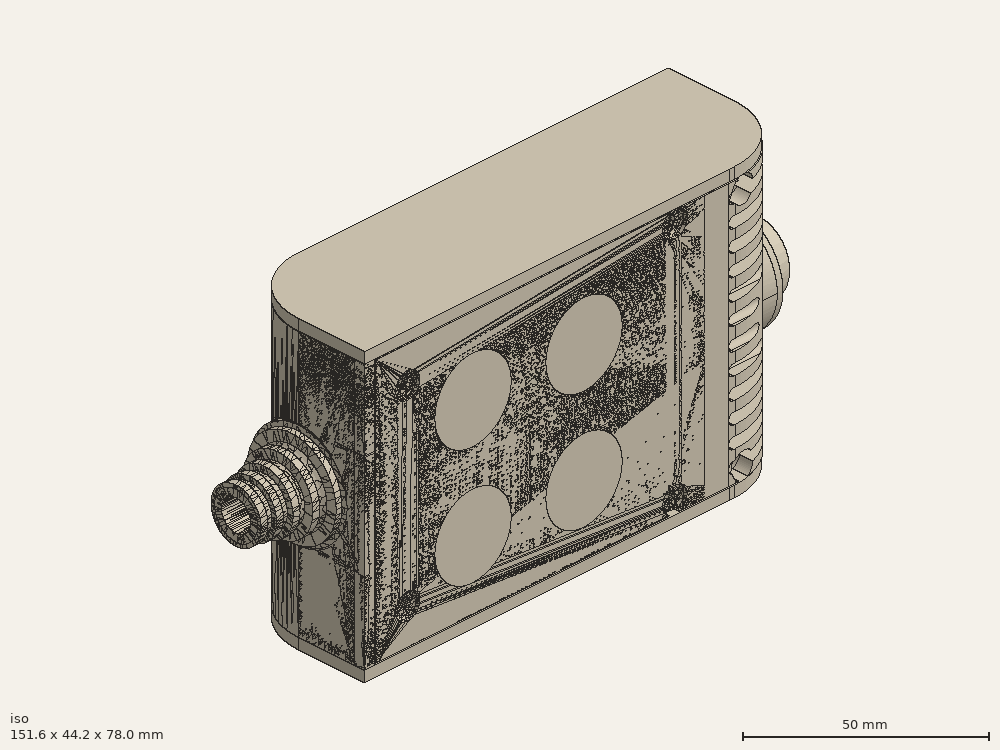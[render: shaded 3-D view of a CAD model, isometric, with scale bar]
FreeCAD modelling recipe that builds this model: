
FCSTD DOCUMENT  (FreeCAD 0.19R0.19.2)
Label: enclosure_179FCStd
License: All rights reserved
LicenseURL: http://en.wikipedia.org/wiki/All_rights_reserved
objects: Part::Revolution×152, Part::MultiFuse×146, Part::Feature×146, Sketcher::SketchObject×84, Part::Cut×70, Part::Cylinder×70, Part::Extrusion×67, Part::Fillet×58, Part::Box×36, App::MeasureDistance×4, PartDesign::Body×2, Image::ImagePlane×1
note: 831 computed .brp shape members not serialized (recipe doc carries the construction recipe); baked Part::Feature solids carry a one-line shape summary decoded from their .brp

FEATURE [Sketcher::SketchObject] Sketch  label="topSketch"
  FullyConstrained = true
  sketch-geometry (20):
    g0: LineSegment StartX=5.21097e-06 StartY=3 StartZ=0 EndX=5.21097e-06 EndY=19 EndZ=0
    g1: ArcOfCircle CenterX=19 CenterY=19 CenterZ=0 NormalX=0 NormalY=0 NormalZ=1 AngleXU=0 Radius=19 StartAngle=1.5708 EndAngle=3.14159
    g2: ArcOfCircle CenterX=19 CenterY=19 CenterZ=0 NormalX=0 NormalY=0 NormalZ=1 AngleXU=0 Radius=16 StartAngle=1.5708 EndAngle=3.14159
    g3: LineSegment StartX=114 StartY=35 StartZ=0 EndX=19 EndY=35 EndZ=0
    g4: LineSegment StartX=5.21097e-06 StartY=3 StartZ=0 EndX=5.21097e-06 EndY=0 EndZ=0
    g5: LineSegment StartX=3 StartY=0 StartZ=0 EndX=5.21097e-06 EndY=0 EndZ=0
    g6: LineSegment StartX=3 StartY=19 StartZ=0 EndX=3 EndY=0 EndZ=0
    g7: LineSegment StartX=19 StartY=38 StartZ=0 EndX=124 EndY=38 EndZ=0
    g8: Circle CenterX=119 CenterY=35 CenterZ=0 NormalX=0 NormalY=0 NormalZ=1 AngleXU=0 Radius=1
    g9: Circle CenterX=121 CenterY=35 CenterZ=0 NormalX=0 NormalY=0 NormalZ=1 AngleXU=0 Radius=1
    g10: Circle CenterX=121 CenterY=33 CenterZ=0 NormalX=0 NormalY=0 NormalZ=1 AngleXU=0 Radius=1
    g11: BSplineCurve PolesCount=3 KnotsCount=2 Degree=2 IsPeriodic=0
    g12: GeomPoint X=119 Y=35 Z=0
    g13: GeomPoint X=121 Y=33 Z=0
    g14: LineSegment StartX=119 StartY=35 StartZ=0 EndX=114 EndY=35 EndZ=0
    g15: ArcOfCircle CenterX=105 CenterY=19 CenterZ=0 NormalX=0 NormalY=0 NormalZ=1 AngleXU=0 Radius=19 StartAngle=5.7297 EndAngle=6.28319
    g16: ArcOfCircle CenterX=105 CenterY=19 CenterZ=0 NormalX=0 NormalY=0 NormalZ=1 AngleXU=0 Radius=16 StartAngle=5.60905 EndAngle=6.28319
    g17: LineSegment StartX=121 StartY=33 StartZ=0 EndX=121 EndY=19 EndZ=0
    g18: LineSegment StartX=124 StartY=38 StartZ=0 EndX=124 EndY=19 EndZ=0
    g19: LineSegment StartX=117.5 StartY=9.01251 StartZ=0 EndX=121.163 EndY=9.0125 EndZ=0
  constraints (46):
    c: Vertical(g0)
    c: Block(g0)
    c: Coincident(g1,g0)
    c: Block(g1)
    c: Coincident(g2,g1)
    c: Block(g2)
    c: Coincident(g3,g2)
    c: Horizontal(g3)
    c: Tangent(g3,g2)
    c: Coincident(g4,g0)
    c: Distance(g4) = 3
    c: Vertical(g4)
    c: Coincident(g5,g4)
    c: Horizontal(g5)
    c: Coincident(g6,g2)
    c: Coincident(g6,g5)
    c: Vertical(g6)
    c: Horizontal(g7)
    c: Distance(g7) = 105
    c: Coincident(g7,g1)
    c: Block(g3)
    c: Weight(g8) = 1
    c: Equal(g8,g9)
    c: Equal(g8,g10)
    c: InternalAlignment(g8,g11)
    c: InternalAlignment(g9,g11)
    c: InternalAlignment(g10,g11)
    c: InternalAlignment(g12,g11)
    c: InternalAlignment(g13,g11)
    c: Block(g11)
    c: Coincident(g14,g11)
    c: Coincident(g14,g3)
    c: Horizontal(g14)
    c: Block(g15)
    c: Coincident(g16,g15)
    c: Block(g16)
    c: Coincident(g17,g11)
    c: Coincident(g17,g16)
    c: Vertical(g17)
    c: Distance(g17) = 14
    c: Coincident(g18,g7)
    c: Coincident(g18,g15)
    c: Vertical(g18)
    c: Distance(g18) = 19
    c: Coincident(g19,g16)
    c: Coincident(g19,g15)
FEATURE [Sketcher::SketchObject] Sketch001  label="bottomSketch"
  FullyConstrained = true
  sketch-geometry (32):
    g0: LineSegment StartX=3.3 StartY=-6.03275e-07 StartZ=0 EndX=98 EndY=-6.03275e-07 EndZ=0
    g1: ArcOfCircle CenterX=98 CenterY=19 CenterZ=0 NormalX=0 NormalY=0 NormalZ=1 AngleXU=0 Radius=19 StartAngle=4.71239 EndAngle=5.71103
    g2: LineSegment StartX=6.3 StartY=8 StartZ=0 EndX=3.3 EndY=8 EndZ=0
    g3: LineSegment StartX=3.3 StartY=8 StartZ=0 EndX=3.3 EndY=-6.03275e-07 EndZ=0
    g4: ArcOfCircle CenterX=8.3 CenterY=5 CenterZ=0 NormalX=0 NormalY=0 NormalZ=1 AngleXU=0 Radius=2 StartAngle=3.14159 EndAngle=4.71239
    g5: LineSegment StartX=6.3 StartY=8 StartZ=0 EndX=6.3 EndY=5 EndZ=0
    g6: ArcOfCircle CenterX=98 CenterY=19 CenterZ=0 NormalX=0 NormalY=0 NormalZ=1 AngleXU=0 Radius=12.7 StartAngle=4.71239 EndAngle=6.28319
    g7: LineSegment StartX=94.7 StartY=3 StartZ=0 EndX=8.3 EndY=3 EndZ=0
    g8-g12: Circle x5 (B-spline internal-alignment scaffolding for g13; pole/knot coordinates omitted)
    g13: BSplineCurve PolesCount=5 KnotsCount=3 Degree=3 IsPeriodic=0
    g14: GeomPoint X=98 Y=6.3 Z=0
    g15: GeomPoint X=96.3938 Y=4.71946 Z=0
    g16: GeomPoint X=94.7 Y=3 Z=0
    g17-g23: Circle x7 (B-spline internal-alignment scaffolding for g24; pole/knot coordinates omitted)
    g24: BSplineCurve PolesCount=7 KnotsCount=5 Degree=3 IsPeriodic=0
    g25-g29: GeomPoint x5 (B-spline internal-alignment scaffolding for g24; pole/knot coordinates omitted)
    g30: ArcOfCircle CenterX=98 CenterY=19 CenterZ=0 NormalX=0 NormalY=0 NormalZ=1 AngleXU=0 Radius=15.7 StartAngle=5.81226 EndAngle=6.28319
    g31: LineSegment StartX=110.7 StartY=19 StartZ=0 EndX=113.7 EndY=19 EndZ=0
  constraints (41):
    c: Horizontal(g0)
    c: Coincident(g1,g0)
    c: Block(g1)
    c: Horizontal(g2)
    c: Distance(g2) = 3
    c: Coincident(g3,g2)
    c: Vertical(g3)
    c: Coincident(g3,g0)
    c: Block(g4)
    c: Block(g2)
    c: Coincident(g5,g2)
    c: Coincident(g5,g4)
    c: Vertical(g5)
    c: Coincident(g6,g1)
    c: Block(g6)
    c: Coincident(g7,g4)
    c: Horizontal(g7)
    c: Block(g0)
    c: Block(g7)
    c: Block(g3)
    c: Coincident(g13,g6)
    c: Weight(g8) = 1
    c: Equal(g8, g9-g12) x4
    c: Coincident(g13,g7)
    c: InternalAlignment(g8-g12 -> g13) x5
    c: InternalAlignment(g14,g13)
    c: InternalAlignment(g15,g13)
    c: InternalAlignment(g16,g13)
    c: Block(g13)
    c: Weight(g17) = 1
    c: Equal(g17, g18-g23) x6
    c: Coincident(g24,g1)
    c: InternalAlignment(g17-g23 -> g24) x7
    c: InternalAlignment(g25-g29 -> g24) x5
    c: Block(g24)
    c: Coincident(g30,g24)
    c: Coincident(g31,g6)
    c: Coincident(g31,g30)
    c: Horizontal(g31)
    c: Block(g31)
    c: Block(g30)
FEATURE [Part::Extrusion] Extrude  label="top"
  Base = -> Sketch
  Dir = (0,0,1)
  DirMode = 2
  FaceMakerClass = Part::FaceMakerBullseye
  LengthFwd = 72
  LengthRev = 0
  Solid = true
  Symmetric = false
FEATURE [Part::Extrusion] Extrude001  label="bottom"
  Base = -> Sketch001
  Dir = (0,0,1)
  DirMode = 2
  FaceMakerClass = Part::FaceMakerBullseye
  LengthFwd = 71.4
  LengthRev = 0
  Placement = pos=(0,0,0.3) rot=(0,0,1;0rad)
  Solid = true
  Symmetric = false
FEATURE [Sketcher::SketchObject] Sketch002  label="topSketch001"
  FullyConstrained = true
  sketch-geometry (8):
    g0: ArcOfCircle CenterX=19 CenterY=19.0975 CenterZ=0 NormalX=0 NormalY=0 NormalZ=1 AngleXU=0 Radius=18.9025 StartAngle=1.5708 EndAngle=3.14674
    g1: LineSegment StartX=0.0977805 StartY=19.0003 StartZ=0 EndX=0.0977805 EndY=0.000251602 EndZ=0
    g2: LineSegment StartX=19 StartY=38 StartZ=0 EndX=124 EndY=38 EndZ=0
    g3: LineSegment StartX=0.0977805 StartY=0.000251602 StartZ=0 EndX=105.098 EndY=0.000251602 EndZ=0
    g4: LineSegment StartX=124 StartY=38 StartZ=0 EndX=125.616 EndY=38 EndZ=0
    g5: LineSegment StartX=105.098 StartY=0.000251602 StartZ=0 EndX=106.713 EndY=0.000251602 EndZ=0
    g6: ArcOfCircle CenterX=106.616 CenterY=19 CenterZ=0 NormalX=0 NormalY=0 NormalZ=1 AngleXU=0 Radius=19 StartAngle=4.71754 EndAngle=6.28319
    g7: LineSegment StartX=125.616 StartY=38 StartZ=0 EndX=125.616 EndY=19 EndZ=0
  constraints (21):
    c: Block(g0)
    c: Coincident(g1,g0)
    c: Vertical(g1)
    c: Horizontal(g2)
    c: Distance(g2) = 105
    c: Coincident(g2,g0)
    c: Distance(g1) = 19
    c: Coincident(g3,g1)
    c: Horizontal(g3)
    c: Distance(g3) = 105
    c: Coincident(g4,g2)
    c: Horizontal(g4)
    c: Distance(g4) = 1.61553
    c: Horizontal(g5)
    c: Equal(g4,g5) = 1.61553
    c: Coincident(g5,g3)
    c: Block(g6)
    c: Coincident(g6,g5)
    c: Coincident(g7,g4)
    c: Coincident(g7,g6)
    c: Vertical(g7)
FEATURE [Part::Extrusion] Extrude002  label="sideA"
  Base = -> Sketch002
  Dir = (0,0,1)
  DirMode = 2
  FaceMakerClass = Part::FaceMakerBullseye
  LengthFwd = 3
  LengthRev = 0
  Placement = pos=(0,0,-3) rot=(0,0,1;0rad)
  Solid = true
  Symmetric = false
FEATURE [Sketcher::SketchObject] Sketch003  label="topSketch002"
  FullyConstrained = true
  sketch-geometry (6):
    g0: LineSegment StartX=19 StartY=38 StartZ=0 EndX=117 EndY=38 EndZ=0
    g1: ArcOfCircle CenterX=19 CenterY=19 CenterZ=0 NormalX=0 NormalY=0 NormalZ=1 AngleXU=0 Radius=19 StartAngle=1.5708 EndAngle=3.14159
    g2: LineSegment StartX=117 StartY=38 StartZ=0 EndX=117 EndY=19 EndZ=0
    g3: LineSegment StartX=98 StartY=1.0161e-12 StartZ=0 EndX=5.22862e-06 EndY=1.0161e-12 EndZ=0
    g4: LineSegment StartX=5.22862e-06 StartY=19 StartZ=0 EndX=5.22862e-06 EndY=1.0161e-12 EndZ=0
    g5: ArcOfCircle CenterX=98 CenterY=19 CenterZ=0 NormalX=0 NormalY=0 NormalZ=1 AngleXU=0 Radius=19 StartAngle=4.71239 EndAngle=6.28319
  constraints (16):
    c: Horizontal(g0)
    c: Distance(g0) = 98
    c: Coincident(g1,g0)
    c: Block(g1)
    c: Coincident(g2,g0)
    c: Vertical(g2)
    c: Distance(g2) = 19
    c: Horizontal(g3)
    c: Coincident(g4,g1)
    c: Vertical(g4)
    c: Coincident(g3,g4)
    c: Block(g3)
    c: Coincident(g5,g2)
    c: Coincident(g5,g3)
    c: Block(g0)
    c: Block(g5)
FEATURE [Sketcher::SketchObject] Sketch004
  FullyConstrained = true
  MapMode = 3
  Placement = pos=(0,0,0) rot=(1,0,0;1.5708rad)
  Support = -> [Extrude]
  sketch-geometry (8):
    g0: Circle CenterX=80.351 CenterY=-67.6202 CenterZ=0 NormalX=0 NormalY=0 NormalZ=1 AngleXU=0 Radius=2
    g1: Circle CenterX=80.351 CenterY=-67.6202 CenterZ=0 NormalX=0 NormalY=0 NormalZ=1 AngleXU=0 Radius=3
    g2: Circle CenterX=80.351 CenterY=-4.92017 CenterZ=0 NormalX=0 NormalY=0 NormalZ=1 AngleXU=0 Radius=2
    g3: Circle CenterX=80.351 CenterY=-4.92017 CenterZ=0 NormalX=0 NormalY=0 NormalZ=1 AngleXU=0 Radius=3
    g4: Circle CenterX=23.851 CenterY=-4.92017 CenterZ=0 NormalX=0 NormalY=0 NormalZ=1 AngleXU=0 Radius=2
    g5: Circle CenterX=23.851 CenterY=-4.92017 CenterZ=0 NormalX=0 NormalY=0 NormalZ=1 AngleXU=0 Radius=3
    g6: Circle CenterX=23.851 CenterY=-67.6202 CenterZ=0 NormalX=0 NormalY=0 NormalZ=1 AngleXU=0 Radius=2
    g7: Circle CenterX=23.851 CenterY=-67.6202 CenterZ=0 NormalX=0 NormalY=0 NormalZ=1 AngleXU=0 Radius=3
  constraints (8):
    c: Block(g3)
    c: Block(g2)
    c: Block(g1)
    c: Block(g0)
    c: Block(g6)
    c: Block(g7)
    c: Block(g4)
    c: Block(g5)
FEATURE [Part::Extrusion] Extrude004
  Base = -> Sketch004
  Dir = (0,-1,2e-16)
  DirMode = 2
  FaceMakerClass = Part::FaceMakerBullseye
  LengthFwd = 6
  LengthRev = 0
  Placement = pos=(0,9,0) rot=(0,0,1;0rad)
  Solid = true
  Symmetric = false
FEATURE [Sketcher::SketchObject] Sketch005
  FullyConstrained = true
  MapMode = 3
  Placement = pos=(0,0,0) rot=(1,0,0;1.5708rad)
  Support = -> [Extrude]
  sketch-geometry (8):
    g0: Circle CenterX=80.351 CenterY=-67.6202 CenterZ=0 NormalX=0 NormalY=0 NormalZ=1 AngleXU=0 Radius=3
    g1: Circle CenterX=80.351 CenterY=-4.92017 CenterZ=0 NormalX=0 NormalY=0 NormalZ=1 AngleXU=0 Radius=3
    g2: Circle CenterX=23.851 CenterY=-4.92017 CenterZ=0 NormalX=0 NormalY=0 NormalZ=1 AngleXU=0 Radius=3
    g3: Circle CenterX=23.851 CenterY=-67.6202 CenterZ=0 NormalX=0 NormalY=0 NormalZ=1 AngleXU=0 Radius=3
    g4: Circle CenterX=23.851 CenterY=-67.6202 CenterZ=0 NormalX=0 NormalY=0 NormalZ=1 AngleXU=0 Radius=5
    g5: Circle CenterX=80.351 CenterY=-67.6202 CenterZ=0 NormalX=0 NormalY=0 NormalZ=1 AngleXU=0 Radius=5
    g6: Circle CenterX=23.851 CenterY=-4.92017 CenterZ=0 NormalX=0 NormalY=0 NormalZ=1 AngleXU=0 Radius=5
    g7: Circle CenterX=80.351 CenterY=-4.92017 CenterZ=0 NormalX=0 NormalY=0 NormalZ=1 AngleXU=0 Radius=5
  constraints (8):
    c: Block(g1)
    c: Block(g0)
    c: Block(g3)
    c: Block(g2)
    c: Block(g5)
    c: Block(g4)
    c: Block(g6)
    c: Block(g7)
FEATURE [Part::Extrusion] Extrude005
  Base = -> Sketch005
  Dir = (0,-1,2e-16)
  DirMode = 2
  FaceMakerClass = Part::FaceMakerBullseye
  LengthFwd = 2
  LengthRev = 0
  Solid = true
  Symmetric = false
FEATURE [Sketcher::SketchObject] Sketch006
  FullyConstrained = true
  MapMode = 3
  Placement = pos=(0,0,0) rot=(1,0,0;1.5708rad)
  sketch-geometry (8):
    g0: Circle CenterX=80.351 CenterY=-67.6202 CenterZ=0 NormalX=0 NormalY=0 NormalZ=1 AngleXU=0 Radius=3
    g1: Circle CenterX=80.351 CenterY=-4.92017 CenterZ=0 NormalX=0 NormalY=0 NormalZ=1 AngleXU=0 Radius=3
    g2: Circle CenterX=23.851 CenterY=-4.92017 CenterZ=0 NormalX=0 NormalY=0 NormalZ=1 AngleXU=0 Radius=3
    g3: Circle CenterX=23.851 CenterY=-67.6202 CenterZ=0 NormalX=0 NormalY=0 NormalZ=1 AngleXU=0 Radius=3
    g4: Circle CenterX=23.851 CenterY=-67.6202 CenterZ=0 NormalX=0 NormalY=0 NormalZ=1 AngleXU=0 Radius=5
    g5: Circle CenterX=80.351 CenterY=-67.6202 CenterZ=0 NormalX=0 NormalY=0 NormalZ=1 AngleXU=0 Radius=5
    g6: Circle CenterX=23.851 CenterY=-4.92017 CenterZ=0 NormalX=0 NormalY=0 NormalZ=1 AngleXU=0 Radius=5
    g7: Circle CenterX=80.351 CenterY=-4.92017 CenterZ=0 NormalX=0 NormalY=0 NormalZ=1 AngleXU=0 Radius=5
  constraints (8):
    c: Block(g1)
    c: Block(g0)
    c: Block(g3)
    c: Block(g2)
    c: Block(g5)
    c: Block(g4)
    c: Block(g6)
    c: Block(g7)
FEATURE [Part::Extrusion] Extrude007
  Base = -> Sketch006
  Dir = (0,-1,2e-16)
  DirMode = 2
  FaceMakerClass = Part::FaceMakerBullseye
  LengthFwd = 2
  LengthRev = 0
  Solid = true
  Symmetric = false
FEATURE [Part::Fillet] Fillet
  Base = -> Extrude007
  Edges = 4 edges r=1.99: [Edge6,Edge12,Edge18,Edge24]
FEATURE [Part::Cut] Cut
  Base = -> Extrude005
  Placement = pos=(0,5,0) rot=(0,0,1;0rad)
  Tool = -> Fillet
FEATURE [Part::MultiFuse] Fusion  label="pCBScrews"
  Placement = pos=(-2.5,0,72.3) rot=(0,0,1;0rad)
  Shapes = -> [Extrude004,Cut]
FEATURE [App::MeasureDistance] Distance  label="Distance: 0.69 mm"
  Distance = 0.685967
  P1 = (24.0138,2.9647,0.3)
  P2 = (23.8901,3,-0.373787)
FEATURE [App::MeasureDistance] Distance001  label="Distance: 0.53 mm"
  Distance = 0.533607
  P1 = (80.2939,3,72.2334)
  P2 = (80.281,2.99661,71.7)
FEATURE [Part::Fillet] Fillet001
  Base = -> Extrude001
  Edges = 1 edges r=2.4: [Edge17]
FEATURE [Part::Fillet] Fillet002  label="bottom001"
  Base = -> Fillet001
  Edges = 1 edges r=2.4: [Edge36]
FEATURE [Part::Fillet] Fillet003  label="top001"
  Base = -> Extrude
  Edges = 1 edges r=2: [Edge1]
FEATURE [Sketcher::SketchObject] Sketch007
  FullyConstrained = true
  sketch-geometry (16):
    g0: LineSegment StartX=4 StartY=0 StartZ=0 EndX=4 EndY=2.4 EndZ=0
    g1: LineSegment StartX=4 StartY=2.4 StartZ=0 EndX=7 EndY=2.4 EndZ=0
    g2: LineSegment StartX=4 StartY=0 StartZ=0 EndX=5.7 EndY=0 EndZ=0
    g3: LineSegment StartX=5.7 StartY=0 StartZ=0 EndX=5.7 EndY=-5.6 EndZ=0
    g4-g8: Circle x5 (B-spline internal-alignment scaffolding for g9; pole/knot coordinates omitted)
    g9: BSplineCurve PolesCount=5 KnotsCount=3 Degree=3 IsPeriodic=0
    g10: GeomPoint X=7 Y=2.4 Z=0
    g11: GeomPoint X=10.4582 Y=-1.55472 Z=0
    g12: GeomPoint X=14 Y=-5.6 Z=0
    g13: LineSegment StartX=14 StartY=-5.6 StartZ=0 EndX=14 EndY=-14.1 EndZ=0
    g14: LineSegment StartX=14 StartY=-14.1 StartZ=0 EndX=6.5 EndY=-14.1 EndZ=0
    g15: LineSegment StartX=5.7 StartY=-5.6 StartZ=0 EndX=6.5 EndY=-14.1 EndZ=0
  constraints (28):
    c: Distance(g0) = 2.4
    c: Vertical(g0)
    c: Block(g0)
    c: Coincident(g1,g0)
    c: Horizontal(g1)
    c: Distance(g1) = 3
    c: Coincident(g2,g0)
    c: Horizontal(g2)
    c: Distance(g2) = 1.7
    c: Coincident(g3,g2)
    c: Vertical(g3)
    c: Distance(g3) = 5.6
    c: Coincident(g9,g1)
    c: Weight(g4) = 1
    c: Equal(g4, g5-g8) x4
    c: InternalAlignment(g4-g8 -> g9) x5
    c: InternalAlignment(g10,g9)
    c: InternalAlignment(g11,g9)
    c: InternalAlignment(g12,g9)
    c: Block(g9)
    c: Coincident(g13,g9)
    c: Vertical(g13)
    c: Distance(g13) = 8.5
    c: Coincident(g14,g13)
    c: Horizontal(g14)
    c: Distance(g14) = 7.5
    c: Coincident(g15,g3)
    c: Coincident(g15,g14)
FEATURE [Part::Feature] Face
  shape: bbox 10 x 16.5 x 2e-07 mm, 1 faces, 0 solids (baked)
FEATURE [Part::Revolution] Revolve  label="plugHousing"
  Angle = 360
  Axis = (0,1,0)
  Base = (0,0,0)
  FaceMakerClass = Part::FaceMakerBullseye
  Placement = pos=(0,0,36.15) rot=(0,0,1;0rad)
  Solid = false
  Source = -> Face
  Symmetric = false
FEATURE [Part::Feature] Face001
  shape: bbox 10 x 16.5 x 2e-07 mm, 1 faces, 0 solids (baked)
FEATURE [Part::Revolution] Revolve001  label="plugHousing001"
  Angle = 360
  Axis = (0,1,0)
  Base = (0,0,0)
  FaceMakerClass = Part::FaceMakerBullseye
  Placement = pos=(0,0,36.15) rot=(0,0,1;0rad)
  Solid = false
  Source = -> Face001
  Symmetric = false
FEATURE [Part::MultiFuse] Fusion001  label="plugHousing002"
  Placement = pos=(0,0,0) rot=(0,0,1;1.5708rad)
  Shapes = -> [Revolve001,Revolve]
FEATURE [Part::Feature] Face002
  shape: bbox 10 x 16.5 x 2e-07 mm, 1 faces, 0 solids (baked)
FEATURE [Part::Revolution] Revolve003  label="plugHousing005"
  Angle = 360
  Axis = (0,1,0)
  Base = (0,0,0)
  FaceMakerClass = Part::FaceMakerBullseye
  Placement = pos=(0,0,36.15) rot=(0,0,1;0rad)
  Solid = false
  Source = -> Face002
  Symmetric = false
FEATURE [Part::Feature] Face003
  shape: bbox 10 x 16.5 x 2e-07 mm, 1 faces, 0 solids (baked)
FEATURE [Part::Revolution] Revolve002  label="plugHousing003"
  Angle = 360
  Axis = (0,1,0)
  Base = (0,0,0)
  FaceMakerClass = Part::FaceMakerBullseye
  Placement = pos=(0,0,36.15) rot=(0,0,1;0rad)
  Solid = false
  Source = -> Face003
  Symmetric = false
FEATURE [Part::MultiFuse] Fusion002  label="plugHousing004"
  Placement = pos=(0,0,0) rot=(0,0,1;1.5708rad)
  Shapes = -> [Revolve002,Revolve003]
FEATURE [Part::MultiFuse] Fusion003  label="plugHousing006"
  Placement = pos=(0,19,0) rot=(0,0,1;3.14159rad)
  Shapes = -> [Fusion002,Fusion001]
FEATURE [Part::Feature] Face004
  shape: bbox 10 x 16.5 x 2e-07 mm, 1 faces, 0 solids (baked)
FEATURE [Part::Revolution] Revolve006  label="plugHousing010"
  Angle = 360
  Axis = (0,1,0)
  Base = (0,0,0)
  FaceMakerClass = Part::FaceMakerBullseye
  Placement = pos=(0,0,36.15) rot=(0,0,1;0rad)
  Solid = false
  Source = -> Face004
  Symmetric = false
FEATURE [Part::Feature] Face005
  shape: bbox 10 x 16.5 x 2e-07 mm, 1 faces, 0 solids (baked)
FEATURE [Part::Revolution] Revolve007  label="plugHousing011"
  Angle = 360
  Axis = (0,1,0)
  Base = (0,0,0)
  FaceMakerClass = Part::FaceMakerBullseye
  Placement = pos=(0,0,36.15) rot=(0,0,1;0rad)
  Solid = false
  Source = -> Face005
  Symmetric = false
FEATURE [Part::Feature] Face006
  shape: bbox 10 x 16.5 x 2e-07 mm, 1 faces, 0 solids (baked)
FEATURE [Part::Revolution] Revolve004  label="plugHousing007"
  Angle = 360
  Axis = (0,1,0)
  Base = (0,0,0)
  FaceMakerClass = Part::FaceMakerBullseye
  Placement = pos=(0,0,36.15) rot=(0,0,1;0rad)
  Solid = false
  Source = -> Face006
  Symmetric = false
FEATURE [Part::MultiFuse] Fusion004  label="plugHousing009"
  Placement = pos=(0,0,0) rot=(0,0,1;1.5708rad)
  Shapes = -> [Revolve004,Revolve007]
FEATURE [Part::Feature] Face007
  shape: bbox 10 x 16.5 x 2e-07 mm, 1 faces, 0 solids (baked)
FEATURE [Part::Revolution] Revolve005  label="plugHousing008"
  Angle = 360
  Axis = (0,1,0)
  Base = (0,0,0)
  FaceMakerClass = Part::FaceMakerBullseye
  Placement = pos=(0,0,36.15) rot=(0,0,1;0rad)
  Solid = false
  Source = -> Face007
  Symmetric = false
FEATURE [Part::MultiFuse] Fusion005  label="plugHousing012"
  Placement = pos=(0,0,0) rot=(0,0,1;1.5708rad)
  Shapes = -> [Revolve006,Revolve005]
FEATURE [Part::MultiFuse] Fusion006  label="plugHousing013"
  Placement = pos=(0,19,0) rot=(0,0,1;3.14159rad)
  Shapes = -> [Fusion005,Fusion004]
FEATURE [Part::MultiFuse] Fusion007  label="plugHousing014"
  Placement = pos=(122.621,0,-0.15) rot=(0,0,1;0rad)
  Shapes = -> [Fusion003,Fusion006]
FEATURE [Part::Cylinder] Cylinder002
  Angle = 360
  AttacherType = Attacher::AttachEngine3D
  Height = 20
  Placement = pos=(0,0,36.15) rot=(0,0,1;0rad)
  Radius = 4
FEATURE [Part::Cylinder] Cylinder003
  Angle = 360
  AttacherType = Attacher::AttachEngine3D
  Height = 10
  Placement = pos=(0,0,36.15) rot=(0,0,1;0rad)
  Radius = 4
FEATURE [Part::MultiFuse] Fusion009  label="removeToCreateHoleForPlugHousing"
  Placement = pos=(70,19,36.15) rot=(0,1,0;1.5708rad)
  Shapes = -> [Cylinder002,Cylinder003]
FEATURE [Part::Cylinder] Cylinder004
  Angle = 360
  AttacherType = Attacher::AttachEngine3D
  Height = 20
  Placement = pos=(0,0,36.15) rot=(0,0,1;0rad)
  Radius = 4
FEATURE [Part::Cylinder] Cylinder005
  Angle = 360
  AttacherType = Attacher::AttachEngine3D
  Height = 10
  Placement = pos=(0,0,36.15) rot=(0,0,1;0rad)
  Radius = 4
FEATURE [Part::MultiFuse] Fusion010  label="removeToCreateHoleForPlugHousing001"
  Placement = pos=(70,19,36.15) rot=(0,1,0;1.5708rad)
  Shapes = -> [Cylinder004,Cylinder005]
FEATURE [Part::Cut] Cut001
  Base = -> Fillet003
  Tool = -> Fusion010
FEATURE [Part::Cut] Cut002  label="Bottom"
  Base = -> Fillet002
  Tool = -> Fusion009
FEATURE [Part::Feature] Face008
  shape: bbox 10 x 16.5 x 2e-07 mm, 1 faces, 0 solids (baked)
FEATURE [Part::Revolution] Revolve011  label="plugHousing021"
  Angle = 360
  Axis = (0,1,0)
  Base = (0,0,0)
  FaceMakerClass = Part::FaceMakerBullseye
  Placement = pos=(0,0,36.15) rot=(0,0,1;0rad)
  Solid = false
  Source = -> Face008
  Symmetric = false
FEATURE [Part::Feature] Face009
  shape: bbox 10 x 16.5 x 2e-07 mm, 1 faces, 0 solids (baked)
FEATURE [Part::Revolution] Revolve012  label="plugHousing022"
  Angle = 360
  Axis = (0,1,0)
  Base = (0,0,0)
  FaceMakerClass = Part::FaceMakerBullseye
  Placement = pos=(0,0,36.15) rot=(0,0,1;0rad)
  Solid = false
  Source = -> Face009
  Symmetric = false
FEATURE [Part::Feature] Face010 .. Face013  x4 (patterned run collapsed; names and placements below)
  shape: bbox 10 x 16.5 x 2e-07 mm, 1 faces, 0 solids (baked)
FEATURE [Part::Revolution] Revolve015  label="plugHousing027"
  Angle = 360
  Axis = (0,1,0)
  Base = (0,0,0)
  FaceMakerClass = Part::FaceMakerBullseye
  Placement = pos=(0,0,36.15) rot=(0,0,1;0rad)
  Solid = false
  Source = -> Face013
  Symmetric = false
FEATURE [Part::Feature] Face014
  shape: bbox 10 x 16.5 x 2e-07 mm, 1 faces, 0 solids (baked)
FEATURE [Part::Feature] Face015
  shape: bbox 10 x 16.5 x 2e-07 mm, 1 faces, 0 solids (baked)
FEATURE [Part::Feature] Face016
  shape: bbox 10 x 16.5 x 2e-07 mm, 1 faces, 0 solids (baked)
FEATURE [Part::Revolution] Revolve019  label="plugHousing033"
  Angle = 360
  Axis = (0,1,0)
  Base = (0,0,0)
  FaceMakerClass = Part::FaceMakerBullseye
  Placement = pos=(0,0,36.15) rot=(0,0,1;0rad)
  Solid = false
  Source = -> Face016
  Symmetric = false
FEATURE [Part::Feature] Face017
  shape: bbox 10 x 16.5 x 2e-07 mm, 1 faces, 0 solids (baked)
FEATURE [Part::Revolution] Revolve020  label="plugHousing034"
  Angle = 360
  Axis = (0,1,0)
  Base = (0,0,0)
  FaceMakerClass = Part::FaceMakerBullseye
  Placement = pos=(0,0,36.15) rot=(0,0,1;0rad)
  Solid = false
  Source = -> Face017
  Symmetric = false
FEATURE [Part::Feature] Face018
  shape: bbox 10 x 16.5 x 2e-07 mm, 1 faces, 0 solids (baked)
FEATURE [Part::Revolution] Revolve016  label="plugHousing030"
  Angle = 360
  Axis = (0,1,0)
  Base = (0,0,0)
  FaceMakerClass = Part::FaceMakerBullseye
  Placement = pos=(0,0,36.15) rot=(0,0,1;0rad)
  Solid = false
  Source = -> Face018
  Symmetric = false
FEATURE [Part::MultiFuse] Fusion020  label="plugHousing038"
  Placement = pos=(0,0,0) rot=(0,0,1;1.5708rad)
  Shapes = -> [Revolve016,Revolve020]
FEATURE [Part::Feature] Face019
  shape: bbox 10 x 16.5 x 2e-07 mm, 1 faces, 0 solids (baked)
FEATURE [Part::Feature] Face020
  shape: bbox 10 x 16.5 x 2e-07 mm, 1 faces, 0 solids (baked)
FEATURE [Part::Revolution] Revolve017  label="plugHousing031"
  Angle = 360
  Axis = (0,1,0)
  Base = (0,0,0)
  FaceMakerClass = Part::FaceMakerBullseye
  Placement = pos=(0,0,36.15) rot=(0,0,1;0rad)
  Solid = false
  Source = -> Face020
  Symmetric = false
FEATURE [Part::MultiFuse] Fusion021  label="plugHousing039"
  Placement = pos=(0,0,0) rot=(0,0,1;1.5708rad)
  Shapes = -> [Revolve019,Revolve017]
FEATURE [Part::MultiFuse] Fusion023  label="plugHousing041"
  Placement = pos=(0,19,0) rot=(0,0,1;3.14159rad)
  Shapes = -> [Fusion021,Fusion020]
FEATURE [Part::Revolution] Revolve022  label="plugHousing043"
  Angle = 360
  Axis = (0,1,0)
  Base = (0,0,0)
  FaceMakerClass = Part::FaceMakerBullseye
  Placement = pos=(0,0,36.15) rot=(0,0,1;0rad)
  Solid = false
  Source = -> Face019
  Symmetric = false
FEATURE [Part::Feature] Face021
  shape: bbox 10 x 16.5 x 2e-07 mm, 1 faces, 0 solids (baked)
FEATURE [Part::Revolution] Revolve023  label="plugHousing044"
  Angle = 360
  Axis = (0,1,0)
  Base = (0,0,0)
  FaceMakerClass = Part::FaceMakerBullseye
  Placement = pos=(0,0,36.15) rot=(0,0,1;0rad)
  Solid = false
  Source = -> Face021
  Symmetric = false
FEATURE [Part::Feature] Face022
  shape: bbox 10 x 16.5 x 2e-07 mm, 1 faces, 0 solids (baked)
FEATURE [Part::Revolution] Revolve018  label="plugHousing032"
  Angle = 360
  Axis = (0,1,0)
  Base = (0,0,0)
  FaceMakerClass = Part::FaceMakerBullseye
  Placement = pos=(0,0,36.15) rot=(0,0,1;0rad)
  Solid = false
  Source = -> Face022
  Symmetric = false
FEATURE [Part::MultiFuse] Fusion022  label="plugHousing040"
  Placement = pos=(0,0,0) rot=(0,0,1;1.5708rad)
  Shapes = -> [Revolve018,Revolve023]
FEATURE [Part::Feature] Face023
  shape: bbox 10 x 16.5 x 2e-07 mm, 1 faces, 0 solids (baked)
FEATURE [Part::Revolution] Revolve021  label="plugHousing035"
  Angle = 360
  Axis = (0,1,0)
  Base = (0,0,0)
  FaceMakerClass = Part::FaceMakerBullseye
  Placement = pos=(0,0,36.15) rot=(0,0,1;0rad)
  Solid = false
  Source = -> Face023
  Symmetric = false
FEATURE [Part::MultiFuse] Fusion018  label="plugHousing036"
  Placement = pos=(0,0,0) rot=(0,0,1;1.5708rad)
  Shapes = -> [Revolve022,Revolve021]
FEATURE [Part::MultiFuse] Fusion019  label="plugHousing037"
  Placement = pos=(0,19,0) rot=(0,0,1;3.14159rad)
  Shapes = -> [Fusion018,Fusion022]
FEATURE [Part::MultiFuse] Fusion024  label="plugHousing042"
  Placement = pos=(122.621,0,-0.15) rot=(0,0,1;0rad)
  Shapes = -> [Fusion023,Fusion019]
FEATURE [Part::Cylinder] Cylinder006
  Angle = 360
  AttacherType = Attacher::AttachEngine3D
  Height = 20
  Placement = pos=(0,0,36.15) rot=(0,0,1;0rad)
  Radius = 14.3
FEATURE [Part::Cylinder] Cylinder007
  Angle = 360
  AttacherType = Attacher::AttachEngine3D
  Height = 10
  Placement = pos=(0,0,36.15) rot=(0,0,1;0rad)
  Radius = 4
FEATURE [Part::MultiFuse] Fusion026  label="removeToCreteHoleForPlugHousing"
  Placement = pos=(70,19,36) rot=(0,1,0;1.5708rad)
  Shapes = -> [Cylinder006,Cylinder007]
FEATURE [Part::Box] Box001  label="Cube001"
  AttacherType = Attacher::AttachEngine3D
  Height = 28
  Length = 3
  Placement = pos=(110.7,19,22) rot=(0,0,1;0rad)
  Width = 15.7
FEATURE [Part::Cut] Cut003  label="top002"
  Base = -> Cut001
  Tool = -> Fusion007
FEATURE [Part::Revolution] Revolve008  label="plugHousing015"
  Angle = 360
  Axis = (0,1,0)
  Base = (0,0,0)
  FaceMakerClass = Part::FaceMakerBullseye
  Placement = pos=(0,0,36.15) rot=(0,0,1;0rad)
  Solid = false
  Source = -> Face010
  Symmetric = false
FEATURE [Part::MultiFuse] Fusion013  label="plugHousing020"
  Placement = pos=(0,0,0) rot=(0,0,1;1.5708rad)
  Shapes = -> [Revolve008,Revolve012]
FEATURE [Part::Cut] Cut004  label="top003"
  Base = -> Cut003
  Placement = pos=(1,0,0) rot=(0,0,1;0rad)
  Tool = -> Fusion026
FEATURE [Part::Cylinder] Cylinder008
  Angle = 360
  AttacherType = Attacher::AttachEngine3D
  Height = 20
  Placement = pos=(0,0,36.15) rot=(0,0,1;0rad)
  Radius = 10.3
FEATURE [Part::Cylinder] Cylinder009
  Angle = 360
  AttacherType = Attacher::AttachEngine3D
  Height = 10
  Placement = pos=(0,0,36.15) rot=(0,0,1;0rad)
  Radius = 4
FEATURE [Part::MultiFuse] Fusion027  label="removeToCreteHoleForPlugHousing001"
  Placement = pos=(70,19,36) rot=(0,1,0;1.5708rad)
  Shapes = -> [Cylinder008,Cylinder009]
FEATURE [Part::Cut] Cut005  label="plugHousingTab"
  Base = -> Box001
  Tool = -> Fusion027
FEATURE [Part::MultiFuse] Fusion028  label="plugHousing045"
  Shapes = -> [Fusion024,Cut005]
FEATURE [Part::Box] Box002  label="Cube002"
  AttacherType = Attacher::AttachEngine3D
  Height = 28.8
  Length = 3
  Placement = pos=(107.3,28,21.6) rot=(0,0,1;0rad)
  Width = 7
FEATURE [Part::Box] Box003  label="Cube003"
  AttacherType = Attacher::AttachEngine3D
  Height = 3
  Length = 6.4
  Placement = pos=(107.3,28,18.6) rot=(0,0,1;0rad)
  Width = 7
FEATURE [Part::Box] Box004  label="Cube004"
  AttacherType = Attacher::AttachEngine3D
  Height = 3
  Length = 6.4
  Placement = pos=(107.3,28,50.4) rot=(0,0,1;0rad)
  Width = 7
FEATURE [Part::MultiFuse] Fusion029  label="plugHousingBracketHolder"
  Shapes = -> [Box004,Box002,Box003]
FEATURE [Part::Cylinder] Cylinder010
  Angle = 360
  AttacherType = Attacher::AttachEngine3D
  Height = 20
  Placement = pos=(0,0,36.15) rot=(0,0,1;0rad)
  Radius = 14.3
FEATURE [Part::Cylinder] Cylinder011
  Angle = 360
  AttacherType = Attacher::AttachEngine3D
  Height = 10
  Placement = pos=(0,0,36.15) rot=(0,0,1;0rad)
  Radius = 4
FEATURE [Part::MultiFuse] Fusion030  label="removeToCreteHoleForPlugHousing002"
  Placement = pos=(70,19,36) rot=(0,1,0;1.5708rad)
  Shapes = -> [Cylinder010,Cylinder011]
FEATURE [Part::Cut] Cut006  label="plugHousingBracketHolder001"
  Base = -> Fusion029
  Tool = -> Fusion030
FEATURE [Part::Cylinder] Cylinder012
  Angle = 360
  AttacherType = Attacher::AttachEngine3D
  Height = 20
  Placement = pos=(0,0,36.15) rot=(0,0,1;0rad)
  Radius = 7
FEATURE [Part::Cylinder] Cylinder013
  Angle = 360
  AttacherType = Attacher::AttachEngine3D
  Height = 10
  Placement = pos=(0,0,36.15) rot=(0,0,1;0rad)
  Radius = 4
FEATURE [Part::MultiFuse] Fusion032  label="removeToCreteHoleForPlugHousing003"
  Placement = pos=(70,19,36) rot=(0,1,0;1.5708rad)
  Shapes = -> [Cylinder012,Cylinder013]
FEATURE [Part::Cut] Cut007  label="bottom002"
  Base = -> Cut002
  Tool = -> Fusion032
FEATURE [Sketcher::SketchObject] Sketch008
  FullyConstrained = true
  sketch-geometry (54):
    g0: LineSegment StartX=-4.2 StartY=0 StartZ=0 EndX=-6.2 EndY=0 EndZ=0
    g1: LineSegment StartX=-14 StartY=-18 StartZ=0 EndX=-14 EndY=-26.5 EndZ=0
    g2: LineSegment StartX=-4.2 StartY=0 StartZ=0 EndX=-4.2 EndY=-13.4877 EndZ=0
    g3: Circle CenterX=-4.2 CenterY=-13.4877 CenterZ=0 NormalX=0 NormalY=0 NormalZ=1 AngleXU=0 Radius=1
    g4: Circle CenterX=-4.2 CenterY=-26.5 CenterZ=0 NormalX=0 NormalY=0 NormalZ=1 AngleXU=0 Radius=1
    g5: Circle CenterX=-8.2 CenterY=-26.5 CenterZ=0 NormalX=0 NormalY=0 NormalZ=1 AngleXU=0 Radius=1
    g6: BSplineCurve PolesCount=3 KnotsCount=2 Degree=2 IsPeriodic=0
    g7: GeomPoint X=-4.2 Y=-13.4877 Z=0
    g8: GeomPoint X=-8.2 Y=-26.5 Z=0
    g9: LineSegment StartX=-14 StartY=-26.5 StartZ=0 EndX=-8.2 EndY=-26.5 EndZ=0
    g10: LineSegment StartX=-10.15 StartY=-12 StartZ=0 EndX=-10.15 EndY=-14 EndZ=0
    g11: LineSegment StartX=-12.8401 StartY=-16 StartZ=0 EndX=-10.1571 EndY=-16 EndZ=0
    g12: LineSegment StartX=-10.15 StartY=-14 StartZ=0 EndX=-8.70761 EndY=-14 EndZ=0
    g13: LineSegment StartX=-12.8401 StartY=-16 StartZ=0 EndX=-12.8401 EndY=-17.6958 EndZ=0
    g14: LineSegment StartX=-10.15 StartY=-12 StartZ=0 EndX=-7.79258 EndY=-12 EndZ=0
    g15: Circle CenterX=-6.2215 CenterY=-2 CenterZ=0 NormalX=0 NormalY=0 NormalZ=1 AngleXU=0 Radius=1
    g16: Circle CenterX=-6.22762 CenterY=-2.58724 CenterZ=0 NormalX=0 NormalY=0 NormalZ=1 AngleXU=0 Radius=1
    g17: Circle CenterX=-6.32538 CenterY=-4 CenterZ=0 NormalX=0 NormalY=0 NormalZ=1 AngleXU=0 Radius=1
    g18: BSplineCurve PolesCount=3 KnotsCount=2 Degree=2 IsPeriodic=0
    g19: GeomPoint X=-6.2215 Y=-2 Z=0
    g20: GeomPoint X=-6.32538 Y=-4 Z=0
    g21: Circle CenterX=-6.48644 CenterY=-5.99526 CenterZ=0 NormalX=0 NormalY=0 NormalZ=1 AngleXU=0 Radius=1
    g22: Circle CenterX=-6.58486 CenterY=-6.99526 CenterZ=0 NormalX=0 NormalY=0 NormalZ=1 AngleXU=0 Radius=1
    g23: Circle CenterX=-6.77343 CenterY=-8 CenterZ=0 NormalX=0 NormalY=0 NormalZ=1 AngleXU=0 Radius=1
    g24: BSplineCurve PolesCount=3 KnotsCount=2 Degree=2 IsPeriodic=0
    g25: GeomPoint X=-6.48644 Y=-5.99526 Z=0
    g26: GeomPoint X=-6.77343 Y=-8 Z=0
    g27: Circle CenterX=-7.19003 CenterY=-10 CenterZ=0 NormalX=0 NormalY=0 NormalZ=1 AngleXU=0 Radius=1
    g28: Circle CenterX=-7.44407 CenterY=-11.0915 CenterZ=0 NormalX=0 NormalY=0 NormalZ=1 AngleXU=0 Radius=1
    g29: Circle CenterX=-7.79258 CenterY=-12 CenterZ=0 NormalX=0 NormalY=0 NormalZ=1 AngleXU=0 Radius=1
    g30: BSplineCurve PolesCount=3 KnotsCount=2 Degree=2 IsPeriodic=0
    g31: GeomPoint X=-7.19003 Y=-10 Z=0
    g32: GeomPoint X=-7.79258 Y=-12 Z=0
    g33: Circle CenterX=-8.70761 CenterY=-14 CenterZ=0 NormalX=0 NormalY=0 NormalZ=1 AngleXU=0 Radius=1
    g34: Circle CenterX=-9.33087 CenterY=-15.1837 CenterZ=0 NormalX=0 NormalY=0 NormalZ=1 AngleXU=0 Radius=1
    g35: Circle CenterX=-10.1571 CenterY=-16 CenterZ=0 NormalX=0 NormalY=0 NormalZ=1 AngleXU=0 Radius=1
    g36: BSplineCurve PolesCount=3 KnotsCount=2 Degree=2 IsPeriodic=0
    g37: GeomPoint X=-8.70761 Y=-14 Z=0
    g38: GeomPoint X=-10.1571 Y=-16 Z=0
    g39: Circle CenterX=-12.8401 CenterY=-17.6958 CenterZ=0 NormalX=0 NormalY=0 NormalZ=1 AngleXU=0 Radius=1
    g40: Circle CenterX=-13.3521 CenterY=-17.9027 CenterZ=0 NormalX=0 NormalY=0 NormalZ=1 AngleXU=0 Radius=1
    g41: Circle CenterX=-14 CenterY=-18 CenterZ=0 NormalX=0 NormalY=0 NormalZ=1 AngleXU=0 Radius=1
    g42: BSplineCurve PolesCount=3 KnotsCount=2 Degree=2 IsPeriodic=0
    g43: GeomPoint X=-12.8401 Y=-17.6958 Z=0
    g44: GeomPoint X=-14 Y=-18 Z=0
    g45: LineSegment StartX=-6.2 StartY=0 StartZ=0 EndX=-7.2 EndY=0 EndZ=0
    g46: LineSegment StartX=-7.2 StartY=0 StartZ=0 EndX=-7.2 EndY=-2 EndZ=0
    g47: LineSegment StartX=-7.2 StartY=-2 StartZ=0 EndX=-6.2215 EndY=-2 EndZ=0
    g48: LineSegment StartX=-6.32538 StartY=-4 StartZ=0 EndX=-7.65538 EndY=-4 EndZ=0
    g49: LineSegment StartX=-7.65538 StartY=-4 StartZ=0 EndX=-7.65538 EndY=-5.99526 EndZ=0
    g50: LineSegment StartX=-7.65538 StartY=-5.99526 StartZ=0 EndX=-6.48644 EndY=-5.99526 EndZ=0
    g51: LineSegment StartX=-6.77343 StartY=-8 StartZ=0 EndX=-8.43343 EndY=-8 EndZ=0
    g52: LineSegment StartX=-8.43343 StartY=-8 StartZ=0 EndX=-8.43343 EndY=-10 EndZ=0
    g53: LineSegment StartX=-8.43343 StartY=-10 StartZ=0 EndX=-7.19003 EndY=-10 EndZ=0
  constraints (112):
    c: Horizontal(g0)
    c: Distance(g0) = 2
    c: Block(g0)
    c: Vertical(g1)
    c: Coincident(g2,g0)
    c: Vertical(g2)
    c: Block(g2)
    c: Coincident(g6,g2)
    c: Weight(g3) = 1
    c: Equal(g3,g4)
    c: Equal(g3,g5)
    c: InternalAlignment(g3,g6)
    c: InternalAlignment(g4,g6)
    c: InternalAlignment(g5,g6)
    c: InternalAlignment(g7,g6)
    c: InternalAlignment(g8,g6)
    c: Block(g6)
    c: Coincident(g9,g1)
    c: Coincident(g9,g6)
    c: Horizontal(g9)
    c: Vertical(g10)
    c: Block(g10)
    c: Horizontal(g11)
    c: Block(g11)
    c: Coincident(g12,g10)
    c: Horizontal(g12)
    c: Block(g12)
    c: Coincident(g13,g11)
    c: Vertical(g13)
    c: Block(g13)
    c: Coincident(g14,g10)
    c: Horizontal(g14)
    c: Block(g14)
    c: Block(g9)
    c: Block(g1)
    c: Weight(g15) = 1
    c: Equal(g15,g16)
    c: Equal(g15,g17)
    c: InternalAlignment(g15,g18)
    c: InternalAlignment(g16,g18)
    c: InternalAlignment(g17,g18)
    c: InternalAlignment(g19,g18)
    c: InternalAlignment(g20,g18)
    c: Weight(g21) = 1
    c: Equal(g21,g22)
    c: Equal(g21,g23)
    c: InternalAlignment(g21,g24)
    c: InternalAlignment(g22,g24)
    c: InternalAlignment(g23,g24)
    c: InternalAlignment(g25,g24)
    c: InternalAlignment(g26,g24)
    c: Weight(g27) = 1
    c: Equal(g27,g28)
    c: Equal(g27,g29)
    c: Coincident(g30,g14)
    c: InternalAlignment(g27,g30)
    c: InternalAlignment(g28,g30)
    c: InternalAlignment(g29,g30)
    c: InternalAlignment(g31,g30)
    c: InternalAlignment(g32,g30)
    c: Coincident(g36,g12)
    c: Weight(g33) = 1
    c: Equal(g33,g34)
    c: Equal(g33,g35)
    c: Coincident(g36,g11)
    c: InternalAlignment(g33,g36)
    c: InternalAlignment(g34,g36)
    c: InternalAlignment(g35,g36)
    c: InternalAlignment(g37,g36)
    c: InternalAlignment(g38,g36)
    c: Coincident(g42,g13)
    c: Weight(g39) = 1
    c: Equal(g39,g40)
    c: Equal(g39,g41)
    c: Coincident(g42,g1)
    c: InternalAlignment(g39,g42)
    c: InternalAlignment(g40,g42)
    c: InternalAlignment(g41,g42)
    c: InternalAlignment(g43,g42)
    c: InternalAlignment(g44,g42)
    c: Block(g18)
    c: Block(g24)
    c: Block(g30)
    c: Block(g36)
    c: Block(g42)
    c: Horizontal(g45)
    c: Coincident(g45,g0)
    c: Vertical(g46)
    c: Coincident(g46,g45)
    c: Coincident(g47,g46)
    c: Coincident(g47,g18)
    c: Horizontal(g47)
    c: Block(g46)
    c: Coincident(g48,g18)
    c: Horizontal(g48)
    c: Distance(g48) = 1.33
    c: Vertical(g49)
    c: Coincident(g49,g48)
    c: Coincident(g50,g49)
    c: Coincident(g50,g24)
    c: Horizontal(g50)
    c: Tangent(g50,g22)
    c: Horizontal(g51)
    c: Coincident(g51,g24)
    c: Block(g51)
    c: Vertical(g52)
    c: Block(g52)
    c: Coincident(g52,g51)
    c: Coincident(g53,g52)
    c: Coincident(g53,g30)
    c: Horizontal(g53)
    c: Distance(g1) = 8.5
FEATURE [Part::Feature] Face024
  shape: bbox 9.8 x 26.5 x 2e-07 mm, 1 faces, 0 solids (baked)
FEATURE [Part::Revolution] Revolve024
  Angle = 360
  Axis = (0,1,0)
  Base = (0,0,0)
  FaceMakerClass = Part::FaceMakerBullseye
  Placement = pos=(0,0,0) rot=(0,0,1;1.5708rad)
  Solid = false
  Source = -> Face024
  Symmetric = false
FEATURE [Part::Feature] Face025
  shape: bbox 9.8 x 26.5 x 2e-07 mm, 1 faces, 0 solids (baked)
FEATURE [Part::Revolution] Revolve025
  Angle = 360
  Axis = (0,1,0)
  Base = (0,0,0)
  FaceMakerClass = Part::FaceMakerBullseye
  Placement = pos=(0,0,0) rot=(0,0,1;1.5708rad)
  Solid = false
  Source = -> Face025
  Symmetric = false
FEATURE [Part::MultiFuse] Fusion033
  Placement = pos=(-18,19,36) rot=(0,0,1;0rad)
  Shapes = -> [Revolve025,Revolve024]
FEATURE [Part::Cylinder] Cylinder014
  Angle = 360
  AttacherType = Attacher::AttachEngine3D
  Height = 20
  Placement = pos=(0,0,36.15) rot=(0,0,1;0rad)
  Radius = 14.3
FEATURE [Part::Cylinder] Cylinder015
  Angle = 360
  AttacherType = Attacher::AttachEngine3D
  Height = 10
  Placement = pos=(0,0,36.15) rot=(0,0,1;0rad)
  Radius = 4
FEATURE [Part::MultiFuse] Fusion034  label="removeToCreteHoleForPlugHousing004"
  Placement = pos=(-42,19,36) rot=(0,1,0;1.5708rad)
  Shapes = -> [Cylinder014,Cylinder015]
FEATURE [Part::Cut] Cut008  label="top004"
  Base = -> Cut004
  Placement = pos=(-1,0,0) rot=(0,0,1;0rad)
  Tool = -> Fusion034
FEATURE [Part::Box] Box005  label="Cube005"
  AttacherType = Attacher::AttachEngine3D
  Height = 28
  Length = 3
  Placement = pos=(110.7,19,22) rot=(0,0,1;0rad)
  Width = 15.7
FEATURE [Part::Cylinder] Cylinder016
  Angle = 360
  AttacherType = Attacher::AttachEngine3D
  Height = 10
  Placement = pos=(0,0,36.15) rot=(0,0,1;0rad)
  Radius = 4
FEATURE [Part::Cylinder] Cylinder017
  Angle = 360
  AttacherType = Attacher::AttachEngine3D
  Height = 20
  Placement = pos=(0,0,36.15) rot=(0,0,1;0rad)
  Radius = 10.3
FEATURE [Part::MultiFuse] Fusion035  label="removeToCreteHoleForPlugHousing005"
  Placement = pos=(70,19,36) rot=(0,1,0;1.5708rad)
  Shapes = -> [Cylinder017,Cylinder016]
FEATURE [Part::Cut] Cut009  label="plugHousingTab001"
  Base = -> Box005
  Placement = pos=(-107.4,-14,0) rot=(0,0,1;0rad)
  Tool = -> Fusion035
FEATURE [Part::Box] Box006  label="Cube006"
  AttacherType = Attacher::AttachEngine3D
  Height = 28
  Length = 3
  Placement = pos=(110.7,19,22) rot=(0,0,1;0rad)
  Width = 15.7
FEATURE [Part::Cylinder] Cylinder018
  Angle = 360
  AttacherType = Attacher::AttachEngine3D
  Height = 10
  Placement = pos=(0,0,36.15) rot=(0,0,1;0rad)
  Radius = 4
FEATURE [Part::Cylinder] Cylinder019
  Angle = 360
  AttacherType = Attacher::AttachEngine3D
  Height = 20
  Placement = pos=(0,0,36.15) rot=(0,0,1;0rad)
  Radius = 10.3
FEATURE [Part::MultiFuse] Fusion036  label="removeToCreteHoleForPlugHousing006"
  Placement = pos=(70,19,36) rot=(0,1,0;1.5708rad)
  Shapes = -> [Cylinder019,Cylinder018]
FEATURE [Part::Cut] Cut010  label="plugHousingTab002"
  Base = -> Box006
  Placement = pos=(-107.4,-14,0) rot=(0,0,1;0rad)
  Tool = -> Fusion036
FEATURE [Part::MultiFuse] Fusion037
  Placement = pos=(9.6,23,0) rot=(0,0,1;3.14159rad)
  Shapes = -> [Cut009,Cut010]
FEATURE [Part::Box] Box  label="Cube"
  AttacherType = Attacher::AttachEngine3D
  Height = 10
  Length = 3
  Placement = pos=(3.3,4,12) rot=(0,0,1;0rad)
  Width = 10
FEATURE [Part::Fillet] Fillet004
  Base = -> Fusion028
  Edges = 1 edges r=2: [Edge25]
FEATURE [Part::Fillet] Fillet005  label="plugHousing046"
  Base = -> Fillet004
  Edges = 1 edges r=2: [Edge8]
FEATURE [Part::Fillet] Fillet006
  Base = -> Box
  Edges = 1 edges r=2: [Edge11]
FEATURE [Part::Box] Box007  label="Cube007"
  AttacherType = Attacher::AttachEngine3D
  Height = 10
  Length = 3
  Placement = pos=(3.3,4,50) rot=(0,0,1;0rad)
  Width = 10
FEATURE [Part::Fillet] Fillet007
  Base = -> Box007
  Edges = 1 edges r=2: [Edge12]
FEATURE [Part::Box] Box008  label="Cube008"
  AttacherType = Attacher::AttachEngine3D
  Height = 28
  Length = 4
  Placement = pos=(5,0,22) rot=(0,0,1;0rad)
  Width = 10
FEATURE [Part::Fillet] Fillet008
  Base = -> Box008
  Edges = 1 edges r=1: [Edge7]
FEATURE [Part::Fillet] Fillet009
  Base = -> Fillet008
  Edges = 1 edges r=2: [Edge5]
FEATURE [Part::Fillet] Fillet010
  Base = -> Fillet009
  Edges = 1 edges r=2: [Edge2]
FEATURE [Sketcher::SketchObject] Sketch009  label="topSketch003"
  FullyConstrained = true
  sketch-geometry (4):
    g0: LineSegment StartX=16.8446 StartY=31.512 StartZ=0 EndX=16.3251 EndY=34.4666 EndZ=0
    g1: ArcOfCircle CenterX=19 CenterY=19.2524 CenterZ=0 NormalX=0 NormalY=0 NormalZ=1 AngleXU=0 Radius=15.4476 StartAngle=1.74483 EndAngle=2.72717
    g2: ArcOfCircle CenterX=19 CenterY=19.2524 CenterZ=0 NormalX=0 NormalY=0 NormalZ=1 AngleXU=0 Radius=12.4476 StartAngle=1.74483 EndAngle=2.73189
    g3: LineSegment StartX=4.86004 StartY=25.4725 StartZ=0 EndX=7.58253 EndY=24.2107 EndZ=0
  constraints (7):
    c: Block(g0)
    c: Coincident(g1,g0)
    c: Coincident(g2,g0)
    c: Coincident(g3,g1)
    c: Coincident(g3,g2)
    c: Block(g1)
    c: Block(g2)
FEATURE [Part::Extrusion] Extrude008
  Base = -> Sketch009
  Dir = (0,0,1)
  DirMode = 2
  FaceMakerClass = Part::FaceMakerBullseye
  LengthFwd = 10
  LengthRev = 0
  Placement = pos=(0,0,31) rot=(0,0,1;0rad)
  Solid = true
  Symmetric = false
FEATURE [Part::Cylinder] Cylinder020
  Angle = 360
  AttacherType = Attacher::AttachEngine3D
  Height = 20
  Placement = pos=(0,0,36.15) rot=(0,0,1;0rad)
  Radius = 8.2
FEATURE [Part::Cylinder] Cylinder021
  Angle = 360
  AttacherType = Attacher::AttachEngine3D
  Height = 10
  Placement = pos=(0,0,36.15) rot=(0,0,1;0rad)
  Radius = 4
FEATURE [Part::MultiFuse] Fusion038  label="removeToCreteHoleForPlugHousing007"
  Placement = pos=(-42,19,36) rot=(0,1,0;1.5708rad)
  Shapes = -> [Cylinder020,Cylinder021]
FEATURE [Part::Cut] Cut011
  Base = -> Extrude008
  Tool = -> Fusion038
FEATURE [Part::Fillet] Fillet011
  Base = -> Cut011
  Edges = 1 edges r=2: [Edge1]
FEATURE [Part::Fillet] Fillet012
  Base = -> Fillet011
  Edges = 1 edges r=2.5: [Edge1]
FEATURE [Part::Fillet] Fillet013
  Base = -> Fillet012
  Edges = 1 edges r=2.5: [Edge2]
FEATURE [Part::Box] Box010  label="Cube010"
  AttacherType = Attacher::AttachEngine3D
  Height = 16
  Length = 8
  Placement = pos=(12.7,31.52,28) rot=(0,0,1;0rad)
  Width = 4
FEATURE [Sketcher::SketchObject] Sketch010  label="topSketch004"
  FullyConstrained = true
  sketch-geometry (4):
    g0: LineSegment StartX=16.8446 StartY=31.512 StartZ=0 EndX=16.3251 EndY=34.4666 EndZ=0
    g1: ArcOfCircle CenterX=19 CenterY=19.2524 CenterZ=0 NormalX=0 NormalY=0 NormalZ=1 AngleXU=0 Radius=15.4476 StartAngle=1.74483 EndAngle=2.72717
    g2: ArcOfCircle CenterX=19 CenterY=19.2524 CenterZ=0 NormalX=0 NormalY=0 NormalZ=1 AngleXU=0 Radius=12.4476 StartAngle=1.74483 EndAngle=2.73189
    g3: LineSegment StartX=4.86004 StartY=25.4725 StartZ=0 EndX=7.58253 EndY=24.2107 EndZ=0
  constraints (7):
    c: Block(g0)
    c: Coincident(g1,g0)
    c: Coincident(g2,g0)
    c: Coincident(g3,g1)
    c: Coincident(g3,g2)
    c: Block(g1)
    c: Block(g2)
FEATURE [Part::Cylinder] Cylinder022
  Angle = 360
  AttacherType = Attacher::AttachEngine3D
  Height = 10
  Placement = pos=(0,0,36.15) rot=(0,0,1;0rad)
  Radius = 4
FEATURE [Sketcher::SketchObject] Sketch011  label="topSketch005"
  FullyConstrained = true
  sketch-geometry (4):
    g0: LineSegment StartX=16.8446 StartY=31.512 StartZ=0 EndX=16.3251 EndY=34.4666 EndZ=0
    g1: ArcOfCircle CenterX=19 CenterY=19.2524 CenterZ=0 NormalX=0 NormalY=0 NormalZ=1 AngleXU=0 Radius=15.4476 StartAngle=1.74483 EndAngle=2.72717
    g2: ArcOfCircle CenterX=19 CenterY=19.2524 CenterZ=0 NormalX=0 NormalY=0 NormalZ=1 AngleXU=0 Radius=12.4476 StartAngle=1.74483 EndAngle=2.73189
    g3: LineSegment StartX=4.86004 StartY=25.4725 StartZ=0 EndX=7.58253 EndY=24.2107 EndZ=0
  constraints (7):
    c: Block(g0)
    c: Coincident(g1,g0)
    c: Coincident(g2,g0)
    c: Coincident(g3,g1)
    c: Coincident(g3,g2)
    c: Block(g1)
    c: Block(g2)
FEATURE [Part::Extrusion] Extrude010
  Base = -> Sketch011
  Dir = (0,0,1)
  DirMode = 2
  FaceMakerClass = Part::FaceMakerBullseye
  LengthFwd = 10.6
  LengthRev = 0
  Placement = pos=(0,0,31) rot=(0,0,1;0rad)
  Solid = true
  Symmetric = false
FEATURE [Part::Cylinder] Cylinder023
  Angle = 360
  AttacherType = Attacher::AttachEngine3D
  Height = 20
  Placement = pos=(0,0,36.15) rot=(0,0,1;0rad)
  Radius = 8.2
FEATURE [Part::MultiFuse] Fusion039  label="removeToCreteHoleForPlugHousing008"
  Placement = pos=(-42,19,36) rot=(0,1,0;1.5708rad)
  Shapes = -> [Cylinder023,Cylinder022]
FEATURE [Part::Cut] Cut012
  Base = -> Extrude010
  Placement = pos=(0,0,-0.3) rot=(0,0,1;0rad)
  Tool = -> Fusion039
FEATURE [Part::Cut] Cut013
  Base = -> Box010
  Tool = -> Cut012
FEATURE [Part::Fillet] Fillet014
  Base = -> Cut013
  Edges = 1 edges r=0.7: [Edge13]
FEATURE [Part::Fillet] Fillet015
  Base = -> Fillet014
  Edges = 1 edges r=0.7: [Edge13]
FEATURE [Part::Fillet] Fillet016
  Base = -> Fillet015
  Edges = 1 edges r=0.7: [Edge16]
FEATURE [Part::Fillet] Fillet017
  Base = -> Fillet016
  Edges = 1 edges r=0.7: [Edge11]
FEATURE [Part::Fillet] Fillet018
  Base = -> Fillet017
  Edges = 1 edges r=0.7: [Edge10]
FEATURE [Part::Fillet] Fillet019
  Base = -> Fillet018
  Edges = 1 edges r=1.2: [Edge5]
FEATURE [Part::Fillet] Fillet020
  Base = -> Fillet019
  Edges = 1 edges r=1.2: [Edge12]
FEATURE [Part::Fillet] Fillet021
  Base = -> Fillet020
  Edges = 1 edges r=2: [Edge1]
  Placement = pos=(0.3,0,0) rot=(0,0,1;0rad)
FEATURE [Part::MultiFuse] Fusion040  label="top005"
  Shapes = -> [Cut008,Fillet021]
FEATURE [Part::MultiFuse] Fusion041  label="wireHolder"
  Shapes = -> [Fusion033,Fillet013]
FEATURE [Part::MultiFuse] Fusion042
  Shapes = -> [Fillet007,Fusion041]
FEATURE [Part::MultiFuse] Fusion043  label="wireHolder001"
  Shapes = -> [Fusion042,Fillet010]
FEATURE [Part::MultiFuse] Fusion044  label="wireHolder002"
  Shapes = -> [Fillet006,Fusion037,Fusion043]
FEATURE [Part::Feature] Face026
  shape: bbox 11 x 6 x 2e-07 mm, 1 faces, 0 solids (baked)
FEATURE [Part::Revolution] Revolve026
  Angle = 360
  Axis = (0,1,0)
  Base = (0,0,0)
  FaceMakerClass = Part::FaceMakerBullseye
  Placement = pos=(30.3,-1,19.7) rot=(0,0,1;0rad)
  Solid = false
  Source = -> Face026
  Symmetric = false
FEATURE [Sketcher::SketchObject] Sketch013  label="topSketch006"
  FullyConstrained = true
  sketch-geometry (13):
    g0: LineSegment StartX=117 StartY=19 StartZ=0 EndX=117 EndY=38 EndZ=0
    g1: ArcOfCircle CenterX=98 CenterY=19 CenterZ=0 NormalX=0 NormalY=0 NormalZ=1 AngleXU=0 Radius=19 StartAngle=5.7297 EndAngle=6.28319
    g2: LineSegment StartX=0 StartY=3 StartZ=0 EndX=0 EndY=19 EndZ=0
    g3: LineSegment StartX=19 StartY=38 StartZ=0 EndX=117 EndY=38 EndZ=0
    g4: ArcOfCircle CenterX=19 CenterY=19 CenterZ=0 NormalX=0 NormalY=0 NormalZ=1 AngleXU=0 Radius=19 StartAngle=1.5708 EndAngle=3.14159
    g5: ArcOfCircle CenterX=19 CenterY=19 CenterZ=0 NormalX=0 NormalY=0 NormalZ=1 AngleXU=0 Radius=16 StartAngle=1.5708 EndAngle=3.14159
    g6: ArcOfCircle CenterX=98 CenterY=19 CenterZ=0 NormalX=0 NormalY=0 NormalZ=1 AngleXU=0 Radius=16 StartAngle=5.60905 EndAngle=6.28319
    g7: LineSegment StartX=114 StartY=19 StartZ=0 EndX=114 EndY=35 EndZ=0
    g8: LineSegment StartX=110.5 StartY=9.01251 StartZ=0 EndX=114.163 EndY=9.01251 EndZ=0
    g9: LineSegment StartX=114 StartY=35 StartZ=0 EndX=19 EndY=35 EndZ=0
    g10: LineSegment StartX=0 StartY=3 StartZ=0 EndX=0 EndY=0 EndZ=0
    g11: LineSegment StartX=3 StartY=0 StartZ=0 EndX=0 EndY=0 EndZ=0
    g12: LineSegment StartX=3 StartY=19 StartZ=0 EndX=3 EndY=0 EndZ=0
  constraints (33):
    c: Vertical(g0)
    c: Distance(g0) = 19
    c: Block(g0)
    c: Coincident(g1,g0)
    c: Block(g1)
    c: Vertical(g2)
    c: Block(g2)
    c: Coincident(g3,g0)
    c: Horizontal(g3)
    c: Distance(g3) = 98
    c: Coincident(g4,g3)
    c: Coincident(g4,g2)
    c: Block(g4)
    c: Coincident(g5,g4)
    c: Coincident(g6,g1)
    c: Block(g6)
    c: Block(g5)
    c: Coincident(g7,g6)
    c: Vertical(g7)
    c: Coincident(g8,g6)
    c: Coincident(g8,g1)
    c: Coincident(g9,g7)
    c: Coincident(g9,g5)
    c: Horizontal(g9)
    c: Tangent(g9,g5)
    c: Coincident(g10,g2)
    c: Distance(g10) = 3
    c: Vertical(g10)
    c: Coincident(g11,g10)
    c: Horizontal(g11)
    c: Coincident(g12,g5)
    c: Coincident(g12,g11)
    c: Vertical(g12)
FEATURE [Part::Extrusion] Extrude011  label="top006"
  Base = -> Sketch013
  Dir = (0,0,1)
  DirMode = 2
  FaceMakerClass = Part::FaceMakerBullseye
  LengthFwd = 72
  LengthRev = 0
  Solid = true
  Symmetric = false
FEATURE [Sketcher::SketchObject] Sketch014
  FullyConstrained = true
  MapMode = 3
  Placement = pos=(0,0,0) rot=(1,0,0;1.5708rad)
  Support = -> [Extrude011]
  sketch-geometry (8):
    g0: Circle CenterX=80.351 CenterY=-67.6202 CenterZ=0 NormalX=0 NormalY=0 NormalZ=1 AngleXU=0 Radius=2
    g1: Circle CenterX=80.351 CenterY=-67.6202 CenterZ=0 NormalX=0 NormalY=0 NormalZ=1 AngleXU=0 Radius=3
    g2: Circle CenterX=80.351 CenterY=-4.92017 CenterZ=0 NormalX=0 NormalY=0 NormalZ=1 AngleXU=0 Radius=2
    g3: Circle CenterX=80.351 CenterY=-4.92017 CenterZ=0 NormalX=0 NormalY=0 NormalZ=1 AngleXU=0 Radius=3
    g4: Circle CenterX=23.851 CenterY=-4.92017 CenterZ=0 NormalX=0 NormalY=0 NormalZ=1 AngleXU=0 Radius=2
    g5: Circle CenterX=23.851 CenterY=-4.92017 CenterZ=0 NormalX=0 NormalY=0 NormalZ=1 AngleXU=0 Radius=3
    g6: Circle CenterX=23.851 CenterY=-67.6202 CenterZ=0 NormalX=0 NormalY=0 NormalZ=1 AngleXU=0 Radius=2
    g7: Circle CenterX=23.851 CenterY=-67.6202 CenterZ=0 NormalX=0 NormalY=0 NormalZ=1 AngleXU=0 Radius=3
  constraints (8):
    c: Block(g3)
    c: Block(g2)
    c: Block(g1)
    c: Block(g0)
    c: Block(g6)
    c: Block(g7)
    c: Block(g4)
    c: Block(g5)
FEATURE [Part::Feature] Face027
  shape: bbox 11 x 6 x 2e-07 mm, 1 faces, 0 solids (baked)
FEATURE [Part::Revolution] Revolve027
  Angle = 360
  Axis = (0,1,0)
  Base = (0,0,0)
  FaceMakerClass = Part::FaceMakerBullseye
  Placement = pos=(30.3,-1,51.7) rot=(0,0,1;0rad)
  Solid = false
  Source = -> Face027
  Symmetric = false
FEATURE [Part::Feature] Face028
  shape: bbox 11 x 6 x 2e-07 mm, 1 faces, 0 solids (baked)
FEATURE [Part::Revolution] Revolve028
  Angle = 360
  Axis = (0,1,0)
  Base = (0,0,0)
  FaceMakerClass = Part::FaceMakerBullseye
  Placement = pos=(62.3,-1,19.7) rot=(0,0,1;0rad)
  Solid = false
  Source = -> Face028
  Symmetric = false
FEATURE [Part::Feature] Face029
  shape: bbox 11 x 6 x 2e-07 mm, 1 faces, 0 solids (baked)
FEATURE [Part::Revolution] Revolve029
  Angle = 360
  Axis = (0,1,0)
  Base = (0,0,0)
  FaceMakerClass = Part::FaceMakerBullseye
  Placement = pos=(62.3,-1,51.7) rot=(0,0,1;0rad)
  Solid = false
  Source = -> Face029
  Symmetric = false
FEATURE [Part::Feature] Wire
  shape: bbox 11 x 5.2 x 2e-07 mm, 0 faces, 0 solids (baked)
FEATURE [Part::Revolution] Revolve030
  Angle = 360
  Axis = (0,1,0)
  Base = (0,0,0)
  FaceMakerClass = Part::FaceMakerBullseye
  Placement = pos=(30.3,38,19.7) rot=(0,0,1;0rad)
  Solid = true
  Source = -> Wire
  Symmetric = false
FEATURE [Part::Feature] Wire001
  shape: bbox 11 x 5.2 x 2e-07 mm, 0 faces, 0 solids (baked)
FEATURE [Part::Revolution] Revolve031
  Angle = 360
  Axis = (0,1,0)
  Base = (0,0,0)
  FaceMakerClass = Part::FaceMakerBullseye
  Placement = pos=(30.3,38,51.7) rot=(0,0,1;0rad)
  Solid = true
  Source = -> Wire001
  Symmetric = false
FEATURE [Part::Feature] Wire002
  shape: bbox 11 x 5.2 x 2e-07 mm, 0 faces, 0 solids (baked)
FEATURE [Part::Revolution] Revolve032
  Angle = 360
  Axis = (0,1,0)
  Base = (0,0,0)
  FaceMakerClass = Part::FaceMakerBullseye
  Placement = pos=(62.3,38,51.7) rot=(0,0,1;0rad)
  Solid = true
  Source = -> Wire002
  Symmetric = false
FEATURE [Part::Feature] Wire003
  shape: bbox 11 x 5.2 x 2e-07 mm, 0 faces, 0 solids (baked)
FEATURE [Part::Revolution] Revolve033
  Angle = 360
  Axis = (0,1,0)
  Base = (0,0,0)
  FaceMakerClass = Part::FaceMakerBullseye
  Placement = pos=(62.3,38,19.7) rot=(0,0,1;0rad)
  Solid = true
  Source = -> Wire003
  Symmetric = false
FEATURE [Part::MultiFuse] Fusion045  label="altRandScrewHousing"
  Shapes = -> [Revolve029,Revolve027,Revolve028,Revolve026]
FEATURE [Part::MultiFuse] Fusion046  label="fanScrewHousing"
  Shapes = -> [Revolve033,Revolve032,Revolve031,Revolve030]
FEATURE [Sketcher::SketchObject] Sketch015
  FullyConstrained = true
  sketch-geometry (17):
    g0: Circle CenterX=-3.5 CenterY=23.5 CenterZ=0 NormalX=0 NormalY=0 NormalZ=1 AngleXU=0 Radius=1
    g1: Circle CenterX=-1 CenterY=15.25 CenterZ=0 NormalX=0 NormalY=0 NormalZ=1 AngleXU=0 Radius=1
    g2: Circle CenterX=-3.5 CenterY=7 CenterZ=0 NormalX=0 NormalY=0 NormalZ=1 AngleXU=0 Radius=1
    g3: BSplineCurve PolesCount=3 KnotsCount=2 Degree=2 IsPeriodic=0
    g4: GeomPoint X=-3.5 Y=23.5 Z=0
    g5: GeomPoint X=-3.5 Y=7 Z=0
    g6: Circle CenterX=-4.8 CenterY=30.5 CenterZ=0 NormalX=0 NormalY=0 NormalZ=1 AngleXU=0 Radius=1
    g7: Circle CenterX=-3.5 CenterY=30.5 CenterZ=0 NormalX=0 NormalY=0 NormalZ=1 AngleXU=0 Radius=1
    g8: Circle CenterX=-3.5 CenterY=29.2 CenterZ=0 NormalX=0 NormalY=0 NormalZ=1 AngleXU=0 Radius=1
    g9: BSplineCurve PolesCount=3 KnotsCount=2 Degree=2 IsPeriodic=0
    g10: GeomPoint X=-4.8 Y=30.5 Z=0
    g11: GeomPoint X=-3.5 Y=29.2 Z=0
    g12: LineSegment StartX=-3.5 StartY=29.2 StartZ=0 EndX=-3.5 EndY=23.5 EndZ=0
    g13: LineSegment StartX=-4.8 StartY=30.5 StartZ=0 EndX=0 EndY=30.5 EndZ=0
    g14: LineSegment StartX=-3.5 StartY=0.3 StartZ=0 EndX=0 EndY=0.3 EndZ=0
    g15: LineSegment StartX=-3.5 StartY=0.3 StartZ=0 EndX=-3.5 EndY=7 EndZ=0
    g16: LineSegment StartX=0 StartY=0.3 StartZ=0 EndX=0 EndY=30.5 EndZ=0
  constraints (33):
    c: Weight(g0) = 1
    c: Equal(g0,g1)
    c: Equal(g0,g2)
    c: InternalAlignment(g0,g3)
    c: InternalAlignment(g1,g3)
    c: InternalAlignment(g2,g3)
    c: InternalAlignment(g4,g3)
    c: InternalAlignment(g5,g3)
    c: Block(g3)
    c: Weight(g6) = 1
    c: Equal(g6,g7)
    c: Equal(g6,g8)
    c: InternalAlignment(g6,g9)
    c: InternalAlignment(g7,g9)
    c: InternalAlignment(g8,g9)
    c: InternalAlignment(g10,g9)
    c: InternalAlignment(g11,g9)
    c: Block(g9)
    c: Coincident(g12,g9)
    c: Coincident(g12,g3)
    c: Vertical(g12)
    c: Coincident(g13,g9)
    c: Horizontal(g13)
    c: Distance(g13) = 4.8
    c: Horizontal(g14)
    c: Block(g14)
    c: Coincident(g15,g14)
    c: Coincident(g15,g3)
    c: Vertical(g15)
    c: Coincident(g16,g14)
    c: Coincident(g16,g13)
    c: Vertical(g16)
    c: Tangent(g16,g1)
FEATURE [Sketcher::SketchObject] Sketch016
  FullyConstrained = true
  sketch-geometry (16):
    g0: Circle CenterX=-3.5 CenterY=23.5 CenterZ=0 NormalX=0 NormalY=0 NormalZ=1 AngleXU=0 Radius=1
    g1: Circle CenterX=-1 CenterY=15.25 CenterZ=0 NormalX=0 NormalY=0 NormalZ=1 AngleXU=0 Radius=1
    g2: Circle CenterX=-3.5 CenterY=7 CenterZ=0 NormalX=0 NormalY=0 NormalZ=1 AngleXU=0 Radius=1
    g3: BSplineCurve PolesCount=3 KnotsCount=2 Degree=2 IsPeriodic=0
    g4: GeomPoint X=-3.5 Y=23.5 Z=0
    g5: GeomPoint X=-3.5 Y=7 Z=0
    g6: LineSegment StartX=-3.5 StartY=28.2 StartZ=0 EndX=-3.5 EndY=23.5 EndZ=0
    g7: LineSegment StartX=0 StartY=29.5 StartZ=0 EndX=0 EndY=30 EndZ=0
    g8: LineSegment StartX=-3.5 StartY=28.2 StartZ=0 EndX=-3.5 EndY=30 EndZ=0
    g9: LineSegment StartX=0 StartY=30 StartZ=0 EndX=0 EndY=30.5 EndZ=0
    g10: LineSegment StartX=0 StartY=30.5 StartZ=0 EndX=-3.5 EndY=30.5 EndZ=0
    g11: LineSegment StartX=-3.5 StartY=30.5 StartZ=0 EndX=-3.5 EndY=30 EndZ=0
    g12: LineSegment StartX=0 StartY=29.5 StartZ=0 EndX=0 EndY=5 EndZ=0
    g13: LineSegment StartX=-3.5 StartY=0.3 StartZ=0 EndX=-3.5 EndY=7 EndZ=0
    g14: LineSegment StartX=-3.5 StartY=0.3 StartZ=0 EndX=0 EndY=0.3 EndZ=0
    g15: LineSegment StartX=0 StartY=5 StartZ=0 EndX=0 EndY=0.3 EndZ=0
  constraints (39):
    c: Weight(g0) = 1
    c: Equal(g0,g1)
    c: Equal(g0,g2)
    c: InternalAlignment(g0,g3)
    c: InternalAlignment(g1,g3)
    c: InternalAlignment(g2,g3)
    c: InternalAlignment(g4,g3)
    c: InternalAlignment(g5,g3)
    c: Block(g3)
    c: Coincident(g6,g3)
    c: Vertical(g6)
    c: Vertical(g7)
    c: Distance(g7) = 0.5
    c: Coincident(g8,g6)
    c: Vertical(g8)
    c: Block(g6)
    c: Block(g7)
    c: Vertical(g9)
    c: Equal(g7,g9) = 0.5
    c: Block(g9)
    c: Coincident(g9,g7)
    c: Horizontal(g10)
    c: Coincident(g10,g9)
    c: Coincident(g11,g10)
    c: Coincident(g11,g8)
    c: Vertical(g11)
    c: Block(g11)
    c: Coincident(g12,g7)
    c: Vertical(g12)
    c: Coincident(g13,g3)
    c: Vertical(g13)
    c: Distance(g13) = 6.7
    c: Coincident(g14,g13)
    c: Horizontal(g14)
    c: Block(g14)
    c: Coincident(g15,g12)
    c: Coincident(g15,g14)
    c: Vertical(g15)
    c: Block(g15)
FEATURE [Sketcher::SketchObject] Sketch017
  FullyConstrained = true
  sketch-geometry (11):
    g0: LineSegment StartX=-3.5 StartY=1e-16 StartZ=0 EndX=-1.6 EndY=1e-16 EndZ=0
    g1: LineSegment StartX=-1.6 StartY=1e-16 StartZ=0 EndX=-1.6 EndY=1.5 EndZ=0
    g2: LineSegment StartX=-3.5 StartY=1.5 StartZ=0 EndX=-1.6 EndY=1.5 EndZ=0
    g3: LineSegment StartX=-3.5 StartY=1e-16 StartZ=0 EndX=-4.8 EndY=1e-16 EndZ=0
    g4: Circle CenterX=-3.5 CenterY=1.3 CenterZ=0 NormalX=0 NormalY=0 NormalZ=1 AngleXU=0 Radius=1
    g5: Circle CenterX=-3.5 CenterY=1e-16 CenterZ=0 NormalX=0 NormalY=0 NormalZ=1 AngleXU=0 Radius=1
    g6: Circle CenterX=-4.8 CenterY=1e-16 CenterZ=0 NormalX=0 NormalY=0 NormalZ=1 AngleXU=0 Radius=1
    g7: BSplineCurve PolesCount=3 KnotsCount=2 Degree=2 IsPeriodic=0
    g8: GeomPoint X=-3.5 Y=1.3 Z=0
    g9: GeomPoint X=-4.8 Y=1e-16 Z=0
    g10: LineSegment StartX=-3.5 StartY=1.3 StartZ=0 EndX=-3.5 EndY=1.5 EndZ=0
  constraints (24):
    c: Horizontal(g0)
    c: Distance(g0) = 1.9
    c: Block(g0)
    c: Coincident(g1,g0)
    c: Vertical(g1)
    c: Coincident(g2,g1)
    c: Horizontal(g2)
    c: Coincident(g3,g0)
    c: Horizontal(g3)
    c: Distance(g3) = 1.3
    c: Weight(g4) = 1
    c: Equal(g4,g5)
    c: Coincident(g5,g0)
    c: Equal(g4,g6)
    c: Coincident(g7,g3)
    c: InternalAlignment(g4,g7)
    c: InternalAlignment(g5,g7)
    c: InternalAlignment(g6,g7)
    c: InternalAlignment(g8,g7)
    c: InternalAlignment(g9,g7)
    c: Coincident(g10,g7)
    c: Coincident(g10,g2)
    c: Vertical(g10)
    c: Block(g10)
FEATURE [Part::Feature] Face035
  shape: bbox 3.2 x 1.5 x 2e-07 mm, 1 faces, 0 solids (baked)
FEATURE [Part::Revolution] Revolve039  label="backCaseScrewRetainer"
  Angle = 360
  Axis = (0,1,0)
  Base = (0,0,0)
  FaceMakerClass = Part::FaceMakerBullseye
  Placement = pos=(12.5,3,62) rot=(0,0,1;0rad)
  Solid = false
  Source = -> Face035
  Symmetric = false
FEATURE [Part::Feature] Face036
  shape: bbox 3.2 x 1.5 x 2e-07 mm, 1 faces, 0 solids (baked)
FEATURE [Part::Feature] Face039
  shape: bbox 4.8 x 30.2 x 2e-07 mm, 1 faces, 0 solids (baked)
FEATURE [Part::Revolution] Revolve043  label="frontCaseScrewPost002"
  Angle = 360
  Axis = (0,1,0)
  Base = (0,0,0)
  FaceMakerClass = Part::FaceMakerBullseye
  Placement = pos=(89.5,4.5,3.5) rot=(0,0,1;0rad)
  Solid = false
  Source = -> Face039
  Symmetric = false
FEATURE [Part::Feature] Face042
  shape: bbox 4.8 x 30.2 x 2e-07 mm, 1 faces, 0 solids (baked)
FEATURE [Part::Revolution] Revolve046  label="frontCaseScrewPost003"
  Angle = 360
  Axis = (0,1,0)
  Base = (0,0,0)
  FaceMakerClass = Part::FaceMakerBullseye
  Placement = pos=(89.5,4.5,68.5) rot=(0,0,1;0rad)
  Solid = false
  Source = -> Face042
  Symmetric = false
FEATURE [Part::Feature] Face043
  shape: bbox 3.2 x 1.5 x 2e-07 mm, 1 faces, 0 solids (baked)
FEATURE [Part::Revolution] Revolve047  label="frontCaseScrewRetainer002"
  Angle = 360
  Axis = (0,1,0)
  Base = (0,0,0)
  FaceMakerClass = Part::FaceMakerBullseye
  Placement = pos=(89.5,3,68.5) rot=(0,0,1;0rad)
  Solid = false
  Source = -> Face043
  Symmetric = false
FEATURE [Part::Feature] Face044
  shape: bbox 3.2 x 1.5 x 2e-07 mm, 1 faces, 0 solids (baked)
FEATURE [Part::Revolution] Revolve048  label="frontCaseScrewRetainer003"
  Angle = 360
  Axis = (0,1,0)
  Base = (0,0,0)
  FaceMakerClass = Part::FaceMakerBullseye
  Placement = pos=(89.5,3,3.5) rot=(0,0,1;0rad)
  Solid = false
  Source = -> Face044
  Symmetric = false
FEATURE [App::MeasureDistance] Distance002  label="Distance: 1.67 mm"
  Distance = 1.66921
  P1 = (99.2361,4.7524,71.7)
  P2 = (99.2347,6.42161,71.7)
FEATURE [Sketcher::SketchObject] Sketch018
  FullyConstrained = true
  sketch-geometry (7):
    g0: LineSegment StartX=0 StartY=0 StartZ=0 EndX=0 EndY=6 EndZ=0
    g1: Circle CenterX=0 CenterY=0 CenterZ=0 NormalX=0 NormalY=0 NormalZ=1 AngleXU=0 Radius=1
    g2: Circle CenterX=8 CenterY=6 CenterZ=0 NormalX=0 NormalY=0 NormalZ=1 AngleXU=0 Radius=1
    g3: BSplineCurve PolesCount=3 KnotsCount=2 Degree=2 IsPeriodic=0
    g4: GeomPoint X=0 Y=0 Z=0
    g5: GeomPoint X=8 Y=6 Z=0
    g6: LineSegment StartX=0 StartY=6 StartZ=0 EndX=8 EndY=6 EndZ=0
  constraints (14):
    c: Coincident(g0,g-1)
    c: Distance(g0) = 6
    c: Vertical(g0)
    c: Coincident(g3,g0)
    c: Weight(g1) = 1
    c: Equal(g1,g2)
    c: InternalAlignment(g1,g3)
    c: InternalAlignment(g2,g3)
    c: InternalAlignment(g4,g3)
    c: InternalAlignment(g5,g3)
    c: Block(g3)
    c: Coincident(g6,g0)
    c: Coincident(g6,g3)
    c: Horizontal(g6)
FEATURE [Part::Extrusion] Extrude012  label="caseScrewPillarBracket"
  Base = -> Sketch018
  Dir = (0,0,1)
  DirMode = 2
  FaceMakerClass = Part::FaceMakerBullseye
  LengthFwd = 2.4
  LengthRev = 0
  Placement = pos=(15.76,29,8.8) rot=(0,1,0;0rad)
  Solid = true
  Symmetric = false
FEATURE [Sketcher::SketchObject] Sketch019
  FullyConstrained = true
  sketch-geometry (7):
    g0: LineSegment StartX=0 StartY=0 StartZ=0 EndX=0 EndY=6 EndZ=0
    g1: Circle CenterX=0 CenterY=0 CenterZ=0 NormalX=0 NormalY=0 NormalZ=1 AngleXU=0 Radius=1
    g2: Circle CenterX=8 CenterY=6 CenterZ=0 NormalX=0 NormalY=0 NormalZ=1 AngleXU=0 Radius=1
    g3: BSplineCurve PolesCount=3 KnotsCount=2 Degree=2 IsPeriodic=0
    g4: GeomPoint X=0 Y=0 Z=0
    g5: GeomPoint X=8 Y=6 Z=0
    g6: LineSegment StartX=0 StartY=6 StartZ=0 EndX=8 EndY=6 EndZ=0
  constraints (14):
    c: Coincident(g0,g-1)
    c: Distance(g0) = 6
    c: Vertical(g0)
    c: Coincident(g3,g0)
    c: Weight(g1) = 1
    c: Equal(g1,g2)
    c: InternalAlignment(g1,g3)
    c: InternalAlignment(g2,g3)
    c: InternalAlignment(g4,g3)
    c: InternalAlignment(g5,g3)
    c: Block(g3)
    c: Coincident(g6,g0)
    c: Coincident(g6,g3)
    c: Horizontal(g6)
FEATURE [Part::Extrusion] Extrude013  label="caseScrewPillarBracket001"
  Base = -> Sketch019
  Dir = (0,0,1)
  DirMode = 2
  FaceMakerClass = Part::FaceMakerBullseye
  LengthFwd = 2.4
  LengthRev = 0
  Placement = pos=(15.76,29,60.8) rot=(0,0,1;0rad)
  Solid = true
  Symmetric = false
FEATURE [Sketcher::SketchObject] Sketch020
  FullyConstrained = true
  sketch-geometry (7):
    g0: LineSegment StartX=0 StartY=0 StartZ=0 EndX=0 EndY=6 EndZ=0
    g1: Circle CenterX=0 CenterY=0 CenterZ=0 NormalX=0 NormalY=0 NormalZ=1 AngleXU=0 Radius=1
    g2: Circle CenterX=8 CenterY=6 CenterZ=0 NormalX=0 NormalY=0 NormalZ=1 AngleXU=0 Radius=1
    g3: BSplineCurve PolesCount=3 KnotsCount=2 Degree=2 IsPeriodic=0
    g4: GeomPoint X=0 Y=0 Z=0
    g5: GeomPoint X=8 Y=6 Z=0
    g6: LineSegment StartX=0 StartY=6 StartZ=0 EndX=8 EndY=6 EndZ=0
  constraints (14):
    c: Coincident(g0,g-1)
    c: Distance(g0) = 6
    c: Vertical(g0)
    c: Coincident(g3,g0)
    c: Weight(g1) = 1
    c: Equal(g1,g2)
    c: InternalAlignment(g1,g3)
    c: InternalAlignment(g2,g3)
    c: InternalAlignment(g4,g3)
    c: InternalAlignment(g5,g3)
    c: Block(g3)
    c: Coincident(g6,g0)
    c: Coincident(g6,g3)
    c: Horizontal(g6)
FEATURE [Part::Extrusion] Extrude014  label="caseScrewPillarBracket002"
  Base = -> Sketch020
  Dir = (0,0,1)
  DirMode = 2
  FaceMakerClass = Part::FaceMakerBullseye
  LengthFwd = 2.4
  LengthRev = 0
  Placement = pos=(13.7,29,13.26) rot=(0,-1,0;1.5708rad)
  Solid = true
  Symmetric = false
FEATURE [Sketcher::SketchObject] Sketch021
  FullyConstrained = true
  sketch-geometry (7):
    g0: LineSegment StartX=0 StartY=0 StartZ=0 EndX=0 EndY=6 EndZ=0
    g1: Circle CenterX=0 CenterY=0 CenterZ=0 NormalX=0 NormalY=0 NormalZ=1 AngleXU=0 Radius=1
    g2: Circle CenterX=8 CenterY=6 CenterZ=0 NormalX=0 NormalY=0 NormalZ=1 AngleXU=0 Radius=1
    g3: BSplineCurve PolesCount=3 KnotsCount=2 Degree=2 IsPeriodic=0
    g4: GeomPoint X=0 Y=0 Z=0
    g5: GeomPoint X=8 Y=6 Z=0
    g6: LineSegment StartX=0 StartY=6 StartZ=0 EndX=8 EndY=6 EndZ=0
  constraints (14):
    c: Coincident(g0,g-1)
    c: Distance(g0) = 6
    c: Vertical(g0)
    c: Coincident(g3,g0)
    c: Weight(g1) = 1
    c: Equal(g1,g2)
    c: InternalAlignment(g1,g3)
    c: InternalAlignment(g2,g3)
    c: InternalAlignment(g4,g3)
    c: InternalAlignment(g5,g3)
    c: Block(g3)
    c: Coincident(g6,g0)
    c: Coincident(g6,g3)
    c: Horizontal(g6)
FEATURE [Part::Extrusion] Extrude015  label="caseScrewPillarBracket003"
  Base = -> Sketch021
  Dir = (0,0,1)
  DirMode = 2
  FaceMakerClass = Part::FaceMakerBullseye
  LengthFwd = 2.4
  LengthRev = 0
  Placement = pos=(11.3,29,58.74) rot=(0,1,0;1.5708rad)
  Solid = true
  Symmetric = false
FEATURE [Sketcher::SketchObject] Sketch022
  FullyConstrained = true
  sketch-geometry (7):
    g0: LineSegment StartX=0 StartY=0 StartZ=0 EndX=0 EndY=6 EndZ=0
    g1: Circle CenterX=0 CenterY=0 CenterZ=0 NormalX=0 NormalY=0 NormalZ=1 AngleXU=0 Radius=1
    g2: Circle CenterX=8 CenterY=6 CenterZ=0 NormalX=0 NormalY=0 NormalZ=1 AngleXU=0 Radius=1
    g3: BSplineCurve PolesCount=3 KnotsCount=2 Degree=2 IsPeriodic=0
    g4: GeomPoint X=0 Y=0 Z=0
    g5: GeomPoint X=8 Y=6 Z=0
    g6: LineSegment StartX=0 StartY=6 StartZ=0 EndX=8 EndY=6 EndZ=0
  constraints (14):
    c: Coincident(g0,g-1)
    c: Distance(g0) = 6
    c: Vertical(g0)
    c: Coincident(g3,g0)
    c: Weight(g1) = 1
    c: Equal(g1,g2)
    c: InternalAlignment(g1,g3)
    c: InternalAlignment(g2,g3)
    c: InternalAlignment(g4,g3)
    c: InternalAlignment(g5,g3)
    c: Block(g3)
    c: Coincident(g6,g0)
    c: Coincident(g6,g3)
    c: Horizontal(g6)
FEATURE [Part::Extrusion] Extrude016  label="caseScrewPillarBracket004"
  Base = -> Sketch022
  Dir = (0,0,1)
  DirMode = 2
  FaceMakerClass = Part::FaceMakerBullseye
  LengthFwd = 2.4
  LengthRev = 0
  Placement = pos=(88.3,29,65.23) rot=(0,1,0;1.5708rad)
  Solid = true
  Symmetric = false
FEATURE [Sketcher::SketchObject] Sketch023
  FullyConstrained = true
  sketch-geometry (7):
    g0: LineSegment StartX=0 StartY=0 StartZ=0 EndX=0 EndY=6 EndZ=0
    g1: Circle CenterX=0 CenterY=0 CenterZ=0 NormalX=0 NormalY=0 NormalZ=1 AngleXU=0 Radius=1
    g2: Circle CenterX=8 CenterY=6 CenterZ=0 NormalX=0 NormalY=0 NormalZ=1 AngleXU=0 Radius=1
    g3: BSplineCurve PolesCount=3 KnotsCount=2 Degree=2 IsPeriodic=0
    g4: GeomPoint X=0 Y=0 Z=0
    g5: GeomPoint X=8 Y=6 Z=0
    g6: LineSegment StartX=0 StartY=6 StartZ=0 EndX=8 EndY=6 EndZ=0
  constraints (14):
    c: Coincident(g0,g-1)
    c: Distance(g0) = 6
    c: Vertical(g0)
    c: Coincident(g3,g0)
    c: Weight(g1) = 1
    c: Equal(g1,g2)
    c: InternalAlignment(g1,g3)
    c: InternalAlignment(g2,g3)
    c: InternalAlignment(g4,g3)
    c: InternalAlignment(g5,g3)
    c: Block(g3)
    c: Coincident(g6,g0)
    c: Coincident(g6,g3)
    c: Horizontal(g6)
FEATURE [Part::Extrusion] Extrude017  label="caseScrewPillarBracket005"
  Base = -> Sketch023
  Dir = (0,0,1)
  DirMode = 2
  FaceMakerClass = Part::FaceMakerBullseye
  LengthFwd = 2.4
  LengthRev = 0
  Placement = pos=(90.7,29,6.77) rot=(0,-1,0;1.5708rad)
  Solid = true
  Symmetric = false
FEATURE [Sketcher::SketchObject] Sketch024
  FullyConstrained = true
  sketch-geometry (7):
    g0: LineSegment StartX=0 StartY=0 StartZ=0 EndX=0 EndY=6 EndZ=0
    g1: Circle CenterX=0 CenterY=0 CenterZ=0 NormalX=0 NormalY=0 NormalZ=1 AngleXU=0 Radius=1
    g2: Circle CenterX=8 CenterY=6 CenterZ=0 NormalX=0 NormalY=0 NormalZ=1 AngleXU=0 Radius=1
    g3: BSplineCurve PolesCount=3 KnotsCount=2 Degree=2 IsPeriodic=0
    g4: GeomPoint X=0 Y=0 Z=0
    g5: GeomPoint X=8 Y=6 Z=0
    g6: LineSegment StartX=0 StartY=6 StartZ=0 EndX=8 EndY=6 EndZ=0
  constraints (14):
    c: Coincident(g0,g-1)
    c: Distance(g0) = 6
    c: Vertical(g0)
    c: Coincident(g3,g0)
    c: Weight(g1) = 1
    c: Equal(g1,g2)
    c: InternalAlignment(g1,g3)
    c: InternalAlignment(g2,g3)
    c: InternalAlignment(g4,g3)
    c: InternalAlignment(g5,g3)
    c: Block(g3)
    c: Coincident(g6,g0)
    c: Coincident(g6,g3)
    c: Horizontal(g6)
FEATURE [Part::Extrusion] Extrude018  label="caseScrewPillarBracket006"
  Base = -> Sketch024
  Dir = (0,0,1)
  DirMode = 2
  FaceMakerClass = Part::FaceMakerBullseye
  LengthFwd = 2.4
  LengthRev = 0
  Placement = pos=(103.7,29,6.77) rot=(0,-1,0;1.5708rad)
  Solid = true
  Symmetric = false
FEATURE [Sketcher::SketchObject] Sketch025
  FullyConstrained = true
  sketch-geometry (7):
    g0: LineSegment StartX=0 StartY=0 StartZ=0 EndX=0 EndY=6 EndZ=0
    g1: Circle CenterX=0 CenterY=0 CenterZ=0 NormalX=0 NormalY=0 NormalZ=1 AngleXU=0 Radius=1
    g2: Circle CenterX=8 CenterY=6 CenterZ=0 NormalX=0 NormalY=0 NormalZ=1 AngleXU=0 Radius=1
    g3: BSplineCurve PolesCount=3 KnotsCount=2 Degree=2 IsPeriodic=0
    g4: GeomPoint X=0 Y=0 Z=0
    g5: GeomPoint X=8 Y=6 Z=0
    g6: LineSegment StartX=0 StartY=6 StartZ=0 EndX=8 EndY=6 EndZ=0
  constraints (14):
    c: Coincident(g0,g-1)
    c: Distance(g0) = 6
    c: Vertical(g0)
    c: Coincident(g3,g0)
    c: Weight(g1) = 1
    c: Equal(g1,g2)
    c: InternalAlignment(g1,g3)
    c: InternalAlignment(g2,g3)
    c: InternalAlignment(g4,g3)
    c: InternalAlignment(g5,g3)
    c: Block(g3)
    c: Coincident(g6,g0)
    c: Coincident(g6,g3)
    c: Horizontal(g6)
FEATURE [Part::Extrusion] Extrude019  label="caseScrewPillarBracket007"
  Base = -> Sketch025
  Dir = (0,0,1)
  DirMode = 2
  FaceMakerClass = Part::FaceMakerBullseye
  LengthFwd = 2.4
  LengthRev = 0
  Placement = pos=(101.3,29,65.23) rot=(0,1,0;1.5708rad)
  Solid = true
  Symmetric = false
FEATURE [Part::Box] Box011  label="frontCaseScrewPillarBracket"
  AttacherType = Attacher::AttachEngine3D
  Height = 2.4
  Length = 16
  Placement = pos=(87,28,2.3) rot=(0,0,1;0rad)
  Width = 7
FEATURE [Part::Box] Box012  label="frontCaseScrewPillarBracket001"
  AttacherType = Attacher::AttachEngine3D
  Height = 2.4
  Length = 16
  Placement = pos=(87,28,67.3) rot=(0,0,1;0rad)
  Width = 7
FEATURE [Sketcher::SketchObject] Sketch026
  FullyConstrained = true
  sketch-geometry (17):
    g0: Circle CenterX=-3.5 CenterY=23.5 CenterZ=0 NormalX=0 NormalY=0 NormalZ=1 AngleXU=0 Radius=1
    g1: Circle CenterX=-1 CenterY=15.25 CenterZ=0 NormalX=0 NormalY=0 NormalZ=1 AngleXU=0 Radius=1
    g2: Circle CenterX=-3.5 CenterY=7 CenterZ=0 NormalX=0 NormalY=0 NormalZ=1 AngleXU=0 Radius=1
    g3: BSplineCurve PolesCount=3 KnotsCount=2 Degree=2 IsPeriodic=0
    g4: GeomPoint X=-3.5 Y=23.5 Z=0
    g5: GeomPoint X=-3.5 Y=7 Z=0
    g6: Circle CenterX=-4.8 CenterY=30.5 CenterZ=0 NormalX=0 NormalY=0 NormalZ=1 AngleXU=0 Radius=1
    g7: Circle CenterX=-3.5 CenterY=30.5 CenterZ=0 NormalX=0 NormalY=0 NormalZ=1 AngleXU=0 Radius=1
    g8: Circle CenterX=-3.5 CenterY=29.2 CenterZ=0 NormalX=0 NormalY=0 NormalZ=1 AngleXU=0 Radius=1
    g9: BSplineCurve PolesCount=3 KnotsCount=2 Degree=2 IsPeriodic=0
    g10: GeomPoint X=-4.8 Y=30.5 Z=0
    g11: GeomPoint X=-3.5 Y=29.2 Z=0
    g12: LineSegment StartX=-3.5 StartY=29.2 StartZ=0 EndX=-3.5 EndY=23.5 EndZ=0
    g13: LineSegment StartX=-4.8 StartY=30.5 StartZ=0 EndX=0 EndY=30.5 EndZ=0
    g14: LineSegment StartX=-3.5 StartY=5 StartZ=0 EndX=-3.5 EndY=7 EndZ=0
    g15: LineSegment StartX=0 StartY=5 StartZ=0 EndX=0 EndY=30.5 EndZ=0
    g16: LineSegment StartX=-3.5 StartY=5 StartZ=0 EndX=0 EndY=5 EndZ=0
  constraints (33):
    c: Weight(g0) = 1
    c: Equal(g0,g1)
    c: Equal(g0,g2)
    c: InternalAlignment(g0,g3)
    c: InternalAlignment(g1,g3)
    c: InternalAlignment(g2,g3)
    c: InternalAlignment(g4,g3)
    c: InternalAlignment(g5,g3)
    c: Block(g3)
    c: Weight(g6) = 1
    c: Equal(g6,g7)
    c: Equal(g6,g8)
    c: InternalAlignment(g6,g9)
    c: InternalAlignment(g7,g9)
    c: InternalAlignment(g8,g9)
    c: InternalAlignment(g10,g9)
    c: InternalAlignment(g11,g9)
    c: Block(g9)
    c: Coincident(g12,g9)
    c: Coincident(g12,g3)
    c: Vertical(g12)
    c: Coincident(g13,g9)
    c: Horizontal(g13)
    c: Distance(g13) = 4.8
    c: Coincident(g14,g3)
    c: Vertical(g14)
    c: Coincident(g15,g13)
    c: Vertical(g15)
    c: Tangent(g15,g1)
    c: Distance(g14) = 2
    c: Coincident(g16,g14)
    c: Horizontal(g16)
    c: Coincident(g15,g16)
FEATURE [Part::Feature] Face050
  shape: bbox 4.8 x 25.5 x 2e-07 mm, 1 faces, 0 solids (baked)
FEATURE [Part::Revolution] Revolve054  label="moreFrontCaseScrewPost001"
  Angle = 360
  Axis = (0,1,0)
  Base = (0,0,0)
  FaceMakerClass = Part::FaceMakerBullseye
  Placement = pos=(102.5,4.5,3.5) rot=(0,0,1;0rad)
  Solid = false
  Source = -> Face050
  Symmetric = false
FEATURE [Part::Feature] Face051
  shape: bbox 4.8 x 25.5 x 2e-07 mm, 1 faces, 0 solids (baked)
FEATURE [Part::Revolution] Revolve055  label="moreFrontCaseScrewPost002"
  Angle = 360
  Axis = (0,1,0)
  Base = (0,0,0)
  FaceMakerClass = Part::FaceMakerBullseye
  Placement = pos=(102.5,4.5,68.5) rot=(0,0,1;0rad)
  Solid = false
  Source = -> Face051
  Symmetric = false
FEATURE [Sketcher::SketchObject] Sketch027
  FullyConstrained = true
  sketch-geometry (10):
    g0: LineSegment StartX=-1.6 StartY=4.7 StartZ=0 EndX=-1.6 EndY=1.7 EndZ=0
    g1: LineSegment StartX=-3.5 StartY=4.7 StartZ=0 EndX=-1.6 EndY=4.7 EndZ=0
    g2: LineSegment StartX=-1.6 StartY=1.7 StartZ=0 EndX=-1.6 EndY=1.5 EndZ=0
    g3: LineSegment StartX=-1.6 StartY=1.5 StartZ=0 EndX=-5.2 EndY=1.5 EndZ=0
    g4: Circle CenterX=-3.5 CenterY=4.7 CenterZ=0 NormalX=0 NormalY=0 NormalZ=1 AngleXU=0 Radius=1
    g5: Circle CenterX=-3.59627 CenterY=2.99743 CenterZ=0 NormalX=0 NormalY=0 NormalZ=1 AngleXU=0 Radius=1
    g6: Circle CenterX=-5.2 CenterY=1.5 CenterZ=0 NormalX=0 NormalY=0 NormalZ=1 AngleXU=0 Radius=1
    g7: BSplineCurve PolesCount=3 KnotsCount=2 Degree=2 IsPeriodic=0
    g8: GeomPoint X=-3.5 Y=4.7 Z=0
    g9: GeomPoint X=-5.2 Y=1.5 Z=0
  constraints (23):
    c: Vertical(g0)
    c: Distance(g0) = 3
    c: Coincident(g1,g0)
    c: Horizontal(g1)
    c: Block(g0)
    c: Block(g1)
    c: Coincident(g2,g0)
    c: Vertical(g2)
    c: Distance(g2) = 0.2
    c: Coincident(g3,g2)
    c: Horizontal(g3)
    c: Block(g3)
    c: Coincident(g7,g1)
    c: Weight(g4) = 1
    c: Equal(g4,g5)
    c: Equal(g4,g6)
    c: Coincident(g7,g3)
    c: InternalAlignment(g4,g7)
    c: InternalAlignment(g5,g7)
    c: InternalAlignment(g6,g7)
    c: InternalAlignment(g8,g7)
    c: InternalAlignment(g9,g7)
    c: Block(g7)
FEATURE [Sketcher::SketchObject] Sketch028
  FullyConstrained = true
  sketch-geometry (18):
    g0: LineSegment StartX=0 StartY=3e-16 StartZ=0 EndX=0 EndY=1.7 EndZ=0
    g1: LineSegment StartX=-3.5 StartY=0 StartZ=0 EndX=-3.5 EndY=0.9 EndZ=0
    g2: Circle CenterX=-2.7 CenterY=1.7 CenterZ=0 NormalX=0 NormalY=0 NormalZ=1 AngleXU=0 Radius=1
    g3: Circle CenterX=-3.5 CenterY=1.7 CenterZ=0 NormalX=0 NormalY=0 NormalZ=1 AngleXU=0 Radius=1
    g4: Circle CenterX=-3.5 CenterY=0.9 CenterZ=0 NormalX=0 NormalY=0 NormalZ=1 AngleXU=0 Radius=1
    g5: BSplineCurve PolesCount=3 KnotsCount=2 Degree=2 IsPeriodic=0
    g6: GeomPoint X=-2.7 Y=1.7 Z=0
    g7: GeomPoint X=-3.5 Y=0.9 Z=0
    g8: LineSegment StartX=-3.5 StartY=0 StartZ=0 EndX=-3.5 EndY=-7 EndZ=0
    g9: LineSegment StartX=0 StartY=3e-16 StartZ=0 EndX=0 EndY=-7 EndZ=0
    g10: LineSegment StartX=-3.5 StartY=-7 StartZ=0 EndX=0 EndY=-7 EndZ=0
    g11: LineSegment StartX=-2.7 StartY=1.7 StartZ=0 EndX=-1.6 EndY=1.7 EndZ=0
    g12: LineSegment StartX=0 StartY=1.7 StartZ=0 EndX=0 EndY=4.5 EndZ=0
    g13: LineSegment StartX=0 StartY=4.5 StartZ=0 EndX=0 EndY=10.8 EndZ=0
    g14: LineSegment StartX=0 StartY=10.8 StartZ=0 EndX=-2 EndY=10.8 EndZ=0
    g15: LineSegment StartX=-1.6 StartY=4.7 StartZ=0 EndX=-1.6 EndY=1.7 EndZ=0
    g16: LineSegment StartX=-1.6 StartY=4.7 StartZ=0 EndX=-2 EndY=4.7 EndZ=0
    g17: LineSegment StartX=-2 StartY=4.7 StartZ=0 EndX=-2 EndY=10.8 EndZ=0
  constraints (44):
    c: Vertical(g0)
    c: Vertical(g1)
    c: Distance(g1) = 0.9
    c: Block(g0)
    c: Distance(g0) = 1.7
    c: Weight(g2) = 1
    c: Equal(g2,g3)
    c: Equal(g2,g4)
    c: Coincident(g5,g1)
    c: InternalAlignment(g2,g5)
    c: InternalAlignment(g3,g5)
    c: InternalAlignment(g4,g5)
    c: InternalAlignment(g6,g5)
    c: InternalAlignment(g7,g5)
    c: Block(g5)
    c: Coincident(g8,g1)
    c: Vertical(g8)
    c: Distance(g8) = 7
    c: Vertical(g9)
    c: Equal(g8,g9) = 7
    c: Coincident(g9,g0)
    c: Coincident(g10,g8)
    c: Coincident(g10,g9)
    c: Horizontal(g10)
    c: Coincident(g11,g5)
    c: Horizontal(g11)
    c: Coincident(g12,g0)
    c: Vertical(g12)
    c: Distance(g12) = 2.8
    c: Coincident(g13,g12)
    c: Vertical(g13)
    c: Distance(g13) = 6.3
    c: Coincident(g14,g13)
    c: Horizontal(g14)
    c: Distance(g14) = 2
    c: Vertical(g15)
    c: Distance(g15) = 3
    c: Block(g11)
    c: Coincident(g15,g11)
    c: Coincident(g16,g15)
    c: Horizontal(g16)
    c: Coincident(g17,g16)
    c: Coincident(g17,g14)
    c: Vertical(g17)
FEATURE [Part::Revolution] Revolve040  label="backCaseScrewRetainer001"
  Angle = 360
  Axis = (0,1,0)
  Base = (0,0,0)
  FaceMakerClass = Part::FaceMakerBullseye
  Placement = pos=(12.5,3,10) rot=(0,0,1;0rad)
  Solid = false
  Source = -> Face036
  Symmetric = false
FEATURE [Part::Feature] Face055
  shape: bbox 3.5 x 30.2 x 2e-07 mm, 1 faces, 0 solids (baked)
FEATURE [Part::Revolution] Revolve059  label="backCaseScrewPost"
  Angle = 360
  Axis = (0,1,0)
  Base = (0,0,0)
  FaceMakerClass = Part::FaceMakerBullseye
  Placement = pos=(12.5,4.5,10) rot=(0,0,1;0rad)
  Solid = false
  Source = -> Face055
  Symmetric = false
FEATURE [Part::Feature] Face056
  shape: bbox 3.5 x 30.2 x 2e-07 mm, 1 faces, 0 solids (baked)
FEATURE [Part::Revolution] Revolve060  label="backCaseScrewPost001"
  Angle = 360
  Axis = (0,1,0)
  Base = (0,0,0)
  FaceMakerClass = Part::FaceMakerBullseye
  Placement = pos=(12.5,4.5,62) rot=(0,0,1;0rad)
  Solid = false
  Source = -> Face056
  Symmetric = false
FEATURE [Part::Feature] Face057
  shape: bbox 3.5 x 17.8 x 2e-07 mm, 1 faces, 0 solids (baked)
FEATURE [Part::Revolution] Revolve061  label="removeToCreateScrewAndThreadedInsertHole"
  Angle = 360
  Axis = (0,1,0)
  Base = (0,0,0)
  FaceMakerClass = Part::FaceMakerBullseye
  Placement = pos=(12.5,0,10) rot=(0,0,1;0rad)
  Solid = false
  Source = -> Face057
  Symmetric = false
FEATURE [Part::Feature] Face058
  shape: bbox 3.5 x 17.8 x 2e-07 mm, 1 faces, 0 solids (baked)
FEATURE [Part::Revolution] Revolve062  label="removeToCreateScrewAndThreadedInsertHole001"
  Angle = 360
  Axis = (0,1,0)
  Base = (0,0,0)
  FaceMakerClass = Part::FaceMakerBullseye
  Placement = pos=(12.5,0,62) rot=(0,0,1;0rad)
  Solid = false
  Source = -> Face058
  Symmetric = false
FEATURE [Part::Feature] Face059
  shape: bbox 3.5 x 17.8 x 2e-07 mm, 1 faces, 0 solids (baked)
FEATURE [Part::Revolution] Revolve063  label="removeToCreateScrewAndThreadedInsertHole002"
  Angle = 360
  Axis = (0,1,0)
  Base = (0,0,0)
  FaceMakerClass = Part::FaceMakerBullseye
  Placement = pos=(89.5,0,68.5) rot=(0,0,1;0rad)
  Solid = false
  Source = -> Face059
  Symmetric = false
FEATURE [Part::Feature] Face060
  shape: bbox 3.5 x 17.8 x 2e-07 mm, 1 faces, 0 solids (baked)
FEATURE [Part::Revolution] Revolve064  label="removeToCreateScrewAndThreadedInsertHole003"
  Angle = 360
  Axis = (0,1,0)
  Base = (0,0,0)
  FaceMakerClass = Part::FaceMakerBullseye
  Placement = pos=(89.5,0,3.5) rot=(0,0,1;0rad)
  Solid = false
  Source = -> Face060
  Symmetric = false
FEATURE [Part::Feature] Face061
  shape: bbox 3.5 x 17.8 x 2e-07 mm, 1 faces, 0 solids (baked)
FEATURE [Part::Revolution] Revolve065  label="removeToCreateScrewAndThreadedInsertHole004"
  Angle = 360
  Axis = (0,1,0)
  Base = (0,0,0)
  FaceMakerClass = Part::FaceMakerBullseye
  Placement = pos=(102.5,4.7,3.5) rot=(0,0,1;0rad)
  Solid = false
  Source = -> Face061
  Symmetric = false
FEATURE [Part::Feature] Face062
  shape: bbox 3.5 x 17.8 x 2e-07 mm, 1 faces, 0 solids (baked)
FEATURE [Part::Revolution] Revolve066  label="removeToCreateScrewAndThreadedInsertHole005"
  Angle = 360
  Axis = (0,1,0)
  Base = (0,0,0)
  FaceMakerClass = Part::FaceMakerBullseye
  Placement = pos=(102.5,4.7,68.5) rot=(0,0,1;0rad)
  Solid = false
  Source = -> Face062
  Symmetric = false
FEATURE [Part::MultiFuse] Fusion047  label="makeHoles"
  Shapes = -> [Revolve066,Revolve065,Revolve064,Revolve063,Revolve062,Revolve061]
FEATURE [Part::Feature] Face063
  shape: bbox 3.6 x 3.2 x 2e-07 mm, 1 faces, 0 solids (baked)
FEATURE [Part::Revolution] Revolve067  label="moreFrontCaseScrewRetainer002"
  Angle = 360
  Axis = (0,1,0)
  Base = (0,0,0)
  FaceMakerClass = Part::FaceMakerBullseye
  Placement = pos=(102.5,4.5,68.5) rot=(0,0,1;0rad)
  Solid = false
  Source = -> Face063
  Symmetric = false
FEATURE [Part::Feature] Face064
  shape: bbox 3.6 x 3.2 x 2e-07 mm, 1 faces, 0 solids (baked)
FEATURE [Part::Revolution] Revolve068  label="moreFrontCaseScrewRetainer003"
  Angle = 360
  Axis = (0,1,0)
  Base = (0,0,0)
  FaceMakerClass = Part::FaceMakerBullseye
  Placement = pos=(102.5,4.5,3.5) rot=(0,0,1;0rad)
  Solid = false
  Source = -> Face064
  Symmetric = false
FEATURE [Part::Feature] Face065
  shape: bbox 3.5 x 17.8 x 2e-07 mm, 1 faces, 0 solids (baked)
FEATURE [Part::Revolution] Revolve069  label="removeToCreateScrewAndThreadedInsertHole006"
  Angle = 360
  Axis = (0,1,0)
  Base = (0,0,0)
  FaceMakerClass = Part::FaceMakerBullseye
  Placement = pos=(12.5,0,10) rot=(0,0,1;0rad)
  Solid = false
  Source = -> Face065
  Symmetric = false
FEATURE [Part::Feature] Face066
  shape: bbox 3.5 x 17.8 x 2e-07 mm, 1 faces, 0 solids (baked)
FEATURE [Part::Revolution] Revolve070  label="removeToCreateScrewAndThreadedInsertHole007"
  Angle = 360
  Axis = (0,1,0)
  Base = (0,0,0)
  FaceMakerClass = Part::FaceMakerBullseye
  Placement = pos=(12.5,0,62) rot=(0,0,1;0rad)
  Solid = false
  Source = -> Face066
  Symmetric = false
FEATURE [Part::Feature] Face067
  shape: bbox 3.5 x 17.8 x 2e-07 mm, 1 faces, 0 solids (baked)
FEATURE [Part::Revolution] Revolve071  label="removeToCreateScrewAndThreadedInsertHole008"
  Angle = 360
  Axis = (0,1,0)
  Base = (0,0,0)
  FaceMakerClass = Part::FaceMakerBullseye
  Placement = pos=(89.5,0,68.5) rot=(0,0,1;0rad)
  Solid = false
  Source = -> Face067
  Symmetric = false
FEATURE [Part::Feature] Face068
  shape: bbox 3.5 x 17.8 x 2e-07 mm, 1 faces, 0 solids (baked)
FEATURE [Part::Revolution] Revolve072  label="removeToCreateScrewAndThreadedInsertHole009"
  Angle = 360
  Axis = (0,1,0)
  Base = (0,0,0)
  FaceMakerClass = Part::FaceMakerBullseye
  Placement = pos=(89.5,0,3.5) rot=(0,0,1;0rad)
  Solid = false
  Source = -> Face068
  Symmetric = false
FEATURE [Part::Feature] Face069
  shape: bbox 3.5 x 17.8 x 2e-07 mm, 1 faces, 0 solids (baked)
FEATURE [Part::Feature] Face070
  shape: bbox 3.5 x 17.8 x 2e-07 mm, 1 faces, 0 solids (baked)
FEATURE [Part::Revolution] Revolve073  label="removeToCreateScrewAndThreadedInsertHole010"
  Angle = 360
  Axis = (0,1,0)
  Base = (0,0,0)
  FaceMakerClass = Part::FaceMakerBullseye
  Placement = pos=(102.5,4.7,3.5) rot=(0,0,1;0rad)
  Solid = false
  Source = -> Face069
  Symmetric = false
FEATURE [Part::Revolution] Revolve074  label="removeToCreateScrewAndThreadedInsertHole011"
  Angle = 360
  Axis = (0,1,0)
  Base = (0,0,0)
  FaceMakerClass = Part::FaceMakerBullseye
  Placement = pos=(102.5,4.7,68.5) rot=(0,0,1;0rad)
  Solid = false
  Source = -> Face070
  Symmetric = false
FEATURE [Part::MultiFuse] Fusion048  label="makeHoles001"
  Shapes = -> [Revolve074,Revolve073,Revolve072,Revolve071,Revolve070,Revolve069]
FEATURE [Part::MultiFuse] Fusion049  label="caseScrewRetainers"
  Shapes = -> [Revolve067,Revolve068,Revolve048,Revolve047,Revolve039,Revolve040]
FEATURE [Part::Cut] Cut015  label="caseScrewRetainers001"
  Base = -> Fusion049
  Tool = -> Fusion048
FEATURE [Part::MultiFuse] Fusion050  label="casePillars"
  Shapes = -> [Revolve055,Revolve054,Revolve043,Revolve046,Revolve059,Revolve060]
FEATURE [Part::Feature] Face071 .. Face076  x6 (patterned run collapsed; names and placements below)
  shape: bbox 3.5 x 17.8 x 2e-07 mm, 1 faces, 0 solids (baked)
FEATURE [Part::Revolution] Revolve075  label="removeToCreateScrewAndThreadedInsertHole012"
  Angle = 360
  Axis = (0,1,0)
  Base = (0,0,0)
  FaceMakerClass = Part::FaceMakerBullseye
  Placement = pos=(12.5,0,10) rot=(0,0,1;0rad)
  Solid = false
  Source = -> Face071
  Symmetric = false
FEATURE [Part::Revolution] Revolve076  label="removeToCreateScrewAndThreadedInsertHole013"
  Angle = 360
  Axis = (0,1,0)
  Base = (0,0,0)
  FaceMakerClass = Part::FaceMakerBullseye
  Placement = pos=(12.5,0,62) rot=(0,0,1;0rad)
  Solid = false
  Source = -> Face072
  Symmetric = false
FEATURE [Part::Revolution] Revolve077  label="removeToCreateScrewAndThreadedInsertHole014"
  Angle = 360
  Axis = (0,1,0)
  Base = (0,0,0)
  FaceMakerClass = Part::FaceMakerBullseye
  Placement = pos=(89.5,0,68.5) rot=(0,0,1;0rad)
  Solid = false
  Source = -> Face073
  Symmetric = false
FEATURE [Part::Revolution] Revolve078  label="removeToCreateScrewAndThreadedInsertHole015"
  Angle = 360
  Axis = (0,1,0)
  Base = (0,0,0)
  FaceMakerClass = Part::FaceMakerBullseye
  Placement = pos=(89.5,0,3.5) rot=(0,0,1;0rad)
  Solid = false
  Source = -> Face074
  Symmetric = false
FEATURE [Part::Revolution] Revolve079  label="removeToCreateScrewAndThreadedInsertHole016"
  Angle = 360
  Axis = (0,1,0)
  Base = (0,0,0)
  FaceMakerClass = Part::FaceMakerBullseye
  Placement = pos=(102.5,4.7,3.5) rot=(0,0,1;0rad)
  Solid = false
  Source = -> Face075
  Symmetric = false
FEATURE [Part::Revolution] Revolve080  label="removeToCreateScrewAndThreadedInsertHole017"
  Angle = 360
  Axis = (0,1,0)
  Base = (0,0,0)
  FaceMakerClass = Part::FaceMakerBullseye
  Placement = pos=(102.5,4.7,68.5) rot=(0,0,1;0rad)
  Solid = false
  Source = -> Face076
  Symmetric = false
FEATURE [Part::MultiFuse] Fusion051  label="makeHoles002"
  Shapes = -> [Revolve080,Revolve079,Revolve078,Revolve077,Revolve076,Revolve075]
FEATURE [Part::Cut] Cut016  label="caesPillars"
  Base = -> Fusion050
  Tool = -> Fusion051
FEATURE [Part::Revolution] Revolve009  label="plugHousing016"
  Angle = 360
  Axis = (0,1,0)
  Base = (0,0,0)
  FaceMakerClass = Part::FaceMakerBullseye
  Placement = pos=(0,0,36.15) rot=(0,0,1;0rad)
  Solid = false
  Source = -> Face012
  Symmetric = false
FEATURE [Part::MultiFuse] Fusion014  label="plugHousing023"
  Placement = pos=(0,0,0) rot=(0,0,1;1.5708rad)
  Shapes = -> [Revolve011,Revolve009]
FEATURE [Part::Revolution] Revolve010  label="plugHousing017"
  Angle = 360
  Axis = (0,1,0)
  Base = (0,0,0)
  FaceMakerClass = Part::FaceMakerBullseye
  Placement = pos=(0,0,36.15) rot=(0,0,1;0rad)
  Solid = false
  Source = -> Face014
  Symmetric = false
FEATURE [Part::MultiFuse] Fusion015  label="plugHousing024"
  Placement = pos=(0,0,0) rot=(0,0,1;1.5708rad)
  Shapes = -> [Revolve010,Revolve015]
FEATURE [Part::Revolution] Revolve014  label="plugHousing026"
  Angle = 360
  Axis = (0,1,0)
  Base = (0,0,0)
  FaceMakerClass = Part::FaceMakerBullseye
  Placement = pos=(0,0,36.15) rot=(0,0,1;0rad)
  Solid = false
  Source = -> Face011
  Symmetric = false
FEATURE [Part::Revolution] Revolve013  label="plugHousing025"
  Angle = 360
  Axis = (0,1,0)
  Base = (0,0,0)
  FaceMakerClass = Part::FaceMakerBullseye
  Placement = pos=(0,0,36.15) rot=(0,0,1;0rad)
  Solid = false
  Source = -> Face015
  Symmetric = false
FEATURE [Part::MultiFuse] Fusion016  label="plugHousing028"
  Placement = pos=(0,19,0) rot=(0,0,1;3.14159rad)
  Shapes = -> [Fusion014,Fusion013]
FEATURE [Part::MultiFuse] Fusion011  label="plugHousing018"
  Placement = pos=(0,0,0) rot=(0,0,1;1.5708rad)
  Shapes = -> [Revolve014,Revolve013]
FEATURE [Part::MultiFuse] Fusion012  label="plugHousing019"
  Placement = pos=(0,19,0) rot=(0,0,1;3.14159rad)
  Shapes = -> [Fusion011,Fusion015]
FEATURE [Part::MultiFuse] Fusion017  label="plugHousing029"
  Placement = pos=(122.621,0,-0.15) rot=(0,0,1;0rad)
  Shapes = -> [Fusion016,Fusion012]
FEATURE [Part::MultiFuse] Fusion052  label="casePillarRetainers"
  Shapes = -> [Extrude012,Extrude013,Extrude014,Extrude015,Extrude016,Extrude017,Extrude018,Extrude019,Box011,Box012]
FEATURE [Part::Feature] Face077
  shape: bbox 3.5 x 17.8 x 2e-07 mm, 1 faces, 0 solids (baked)
FEATURE [Part::Revolution] Revolve081  label="removeToCreateScrewAndThreadedInsertHole018"
  Angle = 360
  Axis = (0,1,0)
  Base = (0,0,0)
  FaceMakerClass = Part::FaceMakerBullseye
  Placement = pos=(62.3,30.3,19.7) rot=(0,0,1;0rad)
  Solid = false
  Source = -> Face077
  Symmetric = false
FEATURE [Part::Feature] Face078
  shape: bbox 3.5 x 17.8 x 2e-07 mm, 1 faces, 0 solids (baked)
FEATURE [Part::Revolution] Revolve082  label="removeToCreateScrewAndThreadedInsertHole019"
  Angle = 360
  Axis = (0,1,0)
  Base = (0,0,0)
  FaceMakerClass = Part::FaceMakerBullseye
  Placement = pos=(62.3,30.3,51.7) rot=(0,0,1;0rad)
  Solid = false
  Source = -> Face078
  Symmetric = false
FEATURE [Part::Feature] Face079
  shape: bbox 3.5 x 17.8 x 2e-07 mm, 1 faces, 0 solids (baked)
FEATURE [Part::Revolution] Revolve083  label="removeToCreateScrewAndThreadedInsertHole020"
  Angle = 360
  Axis = (0,1,0)
  Base = (0,0,0)
  FaceMakerClass = Part::FaceMakerBullseye
  Placement = pos=(30.3,30.3,19.7) rot=(0,0,1;0rad)
  Solid = false
  Source = -> Face079
  Symmetric = false
FEATURE [Part::Feature] Face080
  shape: bbox 3.5 x 17.8 x 2e-07 mm, 1 faces, 0 solids (baked)
FEATURE [Part::Revolution] Revolve084  label="removeToCreateScrewAndThreadedInsertHole021"
  Angle = 360
  Axis = (0,1,0)
  Base = (0,0,0)
  FaceMakerClass = Part::FaceMakerBullseye
  Placement = pos=(30.3,30.3,51.7) rot=(0,0,1;0rad)
  Solid = false
  Source = -> Face080
  Symmetric = false
FEATURE [Part::MultiFuse] Fusion053  label="createThreadedInsertHolesForFan"
  Shapes = -> [Revolve081,Revolve082,Revolve083,Revolve084]
FEATURE [Part::Cut] Cut017  label="fanScrewHousing001"
  Base = -> Fusion046
  Tool = -> Fusion053
FEATURE [Part::Feature] Face081
  shape: bbox 3.5 x 17.8 x 2e-07 mm, 1 faces, 0 solids (baked)
FEATURE [Part::Revolution] Revolve085  label="removeToCreateScrewAndThreadedInsertHole022"
  Angle = 360
  Axis = (0,1,0)
  Base = (0,0,0)
  FaceMakerClass = Part::FaceMakerBullseye
  Placement = pos=(62.3,30.3,19.7) rot=(0,0,1;0rad)
  Solid = false
  Source = -> Face081
  Symmetric = false
FEATURE [Part::Feature] Face082
  shape: bbox 3.5 x 17.8 x 2e-07 mm, 1 faces, 0 solids (baked)
FEATURE [Part::Revolution] Revolve086  label="removeToCreateScrewAndThreadedInsertHole023"
  Angle = 360
  Axis = (0,1,0)
  Base = (0,0,0)
  FaceMakerClass = Part::FaceMakerBullseye
  Placement = pos=(62.3,30.3,51.7) rot=(0,0,1;0rad)
  Solid = false
  Source = -> Face082
  Symmetric = false
FEATURE [Part::Feature] Face083
  shape: bbox 3.5 x 17.8 x 2e-07 mm, 1 faces, 0 solids (baked)
FEATURE [Part::Revolution] Revolve087  label="removeToCreateScrewAndThreadedInsertHole024"
  Angle = 360
  Axis = (0,1,0)
  Base = (0,0,0)
  FaceMakerClass = Part::FaceMakerBullseye
  Placement = pos=(30.3,30.3,19.7) rot=(0,0,1;0rad)
  Solid = false
  Source = -> Face083
  Symmetric = false
FEATURE [Part::Feature] Face084
  shape: bbox 3.5 x 17.8 x 2e-07 mm, 1 faces, 0 solids (baked)
FEATURE [Part::Revolution] Revolve088  label="removeToCreateScrewAndThreadedInsertHole025"
  Angle = 360
  Axis = (0,1,0)
  Base = (0,0,0)
  FaceMakerClass = Part::FaceMakerBullseye
  Placement = pos=(30.3,30.3,51.7) rot=(0,0,1;0rad)
  Solid = false
  Source = -> Face084
  Symmetric = false
FEATURE [Part::MultiFuse] Fusion054  label="createThreadedInsertHolesForFan001"
  Shapes = -> [Revolve085,Revolve086,Revolve087,Revolve088]
FEATURE [Part::Cut] Cut018  label="top007"
  Base = -> Fusion040
  Tool = -> Fusion054
FEATURE [Sketcher::SketchObject] Sketch029
  FullyConstrained = false
  Placement = pos=(0,0,0) rot=(1,0,0;1.5708rad)
  sketch-geometry (24):
    g0: ArcOfCircle CenterX=-4 CenterY=-10.5 CenterZ=0 NormalX=0 NormalY=0 NormalZ=1 AngleXU=0 Radius=1.5 StartAngle=6e-16 EndAngle=3.14159
    g1: ArcOfCircle CenterX=-34.2 CenterY=-10.5 CenterZ=0 NormalX=0 NormalY=0 NormalZ=1 AngleXU=0 Radius=1.5 StartAngle=0 EndAngle=3.14159
    g2: ArcOfCircle CenterX=-34.2 CenterY=-27.7 CenterZ=0 NormalX=0 NormalY=0 NormalZ=1 AngleXU=0 Radius=1.5 StartAngle=3.14159 EndAngle=6.28319
    g3: ArcOfCircle CenterX=-4 CenterY=-27.7 CenterZ=0 NormalX=0 NormalY=0 NormalZ=1 AngleXU=0 Radius=1.5 StartAngle=3.1416 EndAngle=6.28319
    g4: ArcOfCircle CenterX=-10 CenterY=-4.3 CenterZ=0 NormalX=0 NormalY=0 NormalZ=1 AngleXU=0 Radius=1.5 StartAngle=2e-16 EndAngle=3.14159
    g5: ArcOfCircle CenterX=-16.1 CenterY=-1.8 CenterZ=0 NormalX=0 NormalY=0 NormalZ=1 AngleXU=0 Radius=1.5 StartAngle=5e-16 EndAngle=3.14159
    g6: ArcOfCircle CenterX=-22.1 CenterY=-1.8 CenterZ=0 NormalX=0 NormalY=0 NormalZ=1 AngleXU=0 Radius=1.5 StartAngle=5e-16 EndAngle=3.14159
    g7: ArcOfCircle CenterX=-28.2 CenterY=-4.3 CenterZ=0 NormalX=0 NormalY=0 NormalZ=1 AngleXU=0 Radius=1.5 StartAngle=2e-16 EndAngle=3.14159
    g8: ArcOfCircle CenterX=-10 CenterY=-33.9 CenterZ=0 NormalX=0 NormalY=0 NormalZ=1 AngleXU=0 Radius=1.5 StartAngle=3.14159 EndAngle=6.28319
    g9: ArcOfCircle CenterX=-16.1 CenterY=-36.4 CenterZ=0 NormalX=0 NormalY=0 NormalZ=1 AngleXU=0 Radius=1.5 StartAngle=3.14159 EndAngle=6.28319
    g10: ArcOfCircle CenterX=-22.1 CenterY=-36.4 CenterZ=0 NormalX=0 NormalY=0 NormalZ=1 AngleXU=0 Radius=1.5 StartAngle=3.14159 EndAngle=6.28319
    g11: ArcOfCircle CenterX=-28.2 CenterY=-33.9 CenterZ=0 NormalX=0 NormalY=0 NormalZ=1 AngleXU=0 Radius=1.5 StartAngle=3.14159 EndAngle=6.28319
    g12: LineSegment StartX=-35.7 StartY=-10.5 StartZ=0 EndX=-35.7 EndY=-27.7 EndZ=0
    g13: LineSegment StartX=-32.7 StartY=-10.5 StartZ=0 EndX=-32.7 EndY=-27.7 EndZ=0
    g14: LineSegment StartX=-29.7 StartY=-33.9 StartZ=0 EndX=-29.7 EndY=-4.3 EndZ=0
    g15: LineSegment StartX=-26.7 StartY=-33.9 StartZ=0 EndX=-26.7 EndY=-4.3 EndZ=0
    g16: LineSegment StartX=-2.5 StartY=-10.5 StartZ=0 EndX=-2.5 EndY=-27.7 EndZ=0
    g17: LineSegment StartX=-8.5 StartY=-4.3 StartZ=0 EndX=-8.5 EndY=-33.9 EndZ=0
    g18: LineSegment StartX=-5.5 StartY=-10.5 StartZ=0 EndX=-5.5 EndY=-27.7 EndZ=0
    g19: LineSegment StartX=-11.5 StartY=-4.3 StartZ=0 EndX=-11.5 EndY=-33.9 EndZ=0
    g20: LineSegment StartX=-14.6 StartY=-1.8 StartZ=0 EndX=-14.6 EndY=-36.4 EndZ=0
    g21: LineSegment StartX=-17.6 StartY=-1.8 StartZ=0 EndX=-17.6 EndY=-36.4 EndZ=0
    g22: LineSegment StartX=-20.6 StartY=-36.4 StartZ=0 EndX=-20.6 EndY=-1.8 EndZ=0
    g23: LineSegment StartX=-23.6 StartY=-1.8 StartZ=0 EndX=-23.6 EndY=-36.4 EndZ=0
  constraints (48):
    c: Block(g0)
    c: Block(g1)
    c: Block(g2)
    c: Block(g3)
    c: Block(g4)
    c: Block(g5)
    c: Block(g6)
    c: Block(g7)
    c: Block(g8)
    c: Block(g9)
    c: Block(g10)
    c: Block(g11)
    c: Coincident(g12,g1)
    c: Coincident(g12,g2)
    c: Vertical(g12)
    c: Coincident(g13,g1)
    c: Coincident(g13,g2)
    c: Vertical(g13)
    c: Coincident(g14,g11)
    c: Coincident(g14,g7)
    c: Vertical(g14)
    c: Coincident(g15,g11)
    c: Coincident(g15,g7)
    c: Vertical(g15)
    c: Coincident(g16,g0)
    c: Coincident(g16,g3)
    c: Vertical(g16)
    c: Coincident(g17,g4)
    c: Coincident(g17,g8)
    c: Vertical(g17)
    c: Coincident(g18,g0)
    c: Coincident(g18,g3)
    c: Vertical(g18)
    c: Coincident(g19,g4)
    c: Coincident(g19,g8)
    c: Vertical(g19)
    c: Coincident(g20,g5)
    c: Coincident(g20,g9)
    c: Vertical(g20)
    c: Coincident(g21,g5)
    c: Coincident(g21,g9)
    c: Vertical(g21)
    c: Coincident(g22,g10)
    c: Coincident(g22,g6)
    c: Vertical(g22)
    c: Coincident(g23,g6)
    c: Coincident(g23,g10)
    c: Vertical(g23)
FEATURE [Part::Extrusion] Extrude020  label="removeToCreateFanGrillHoles"
  Base = -> Sketch029
  Dir = (0,-1,6e-16)
  DirMode = 2
  FaceMakerClass = Part::FaceMakerBullseye
  LengthFwd = 10
  LengthRev = 0
  Placement = pos=(65.4,44,54.82) rot=(0,0,1;0rad)
  Solid = true
  Symmetric = false
FEATURE [Part::MultiFuse] Fusion055  label="top008"
  Shapes = -> [Cut017,Cut018]
FEATURE [Part::Cut] Cut019  label="top009"
  Base = -> Fusion055
  Tool = -> Extrude020
FEATURE [App::MeasureDistance] Distance003  label="Distance: 71.95 mm"
  Distance = 71.9513
  P1 = (117,38,72)
  P2 = (117,38,0.0487319)
FEATURE [Sketcher::SketchObject] Sketch030
  FullyConstrained = true
  Placement = pos=(117,19,0) rot=(0.57735,0.57735,0.57735;2.0944rad)
  sketch-geometry (48):
    g0: LineSegment StartX=-49.19 StartY=69.25 StartZ=0 EndX=-49.19 EndY=66.25 EndZ=0
    g1: LineSegment StartX=-49.19 StartY=63.5 StartZ=0 EndX=-49.19 EndY=60.5 EndZ=0
    g2: LineSegment StartX=-49.19 StartY=57.75 StartZ=0 EndX=-49.19 EndY=54.75 EndZ=0
    g3: LineSegment StartX=-49.19 StartY=52 StartZ=0 EndX=-49.19 EndY=49 EndZ=0
    g4: LineSegment StartX=-49.19 StartY=46.25 StartZ=0 EndX=-49.19 EndY=43.25 EndZ=0
    g5: LineSegment StartX=-49.19 StartY=40.5 StartZ=0 EndX=-49.19 EndY=37.5 EndZ=0
    g6: LineSegment StartX=-49.19 StartY=34.5 StartZ=0 EndX=-49.19 EndY=31.5 EndZ=0
    g7: LineSegment StartX=-49.19 StartY=28.75 StartZ=0 EndX=-49.19 EndY=25.75 EndZ=0
    g8: LineSegment StartX=-49.19 StartY=23 StartZ=0 EndX=-49.19 EndY=20 EndZ=0
    g9: LineSegment StartX=-49.19 StartY=17.25 StartZ=0 EndX=-49.19 EndY=14.25 EndZ=0
    g10: LineSegment StartX=-49.19 StartY=11.5 StartZ=0 EndX=-49.19 EndY=8.5 EndZ=0
    g11: LineSegment StartX=-49.19 StartY=5.75 StartZ=0 EndX=-49.19 EndY=2.75 EndZ=0
    g12: ArcOfCircle CenterX=-1.5 CenterY=67.75 CenterZ=0 NormalX=0 NormalY=0 NormalZ=1 AngleXU=0 Radius=1.5 StartAngle=4.71239 EndAngle=7.85398
    g13: ArcOfCircle CenterX=-1.5 CenterY=62 CenterZ=0 NormalX=0 NormalY=0 NormalZ=1 AngleXU=0 Radius=1.5 StartAngle=4.71239 EndAngle=7.85398
    g14: ArcOfCircle CenterX=-1.5 CenterY=56.25 CenterZ=0 NormalX=0 NormalY=0 NormalZ=1 AngleXU=0 Radius=1.5 StartAngle=4.71239 EndAngle=7.85398
    g15: ArcOfCircle CenterX=-11.49 CenterY=50.5 CenterZ=0 NormalX=0 NormalY=0 NormalZ=1 AngleXU=0 Radius=1.5 StartAngle=4.71239 EndAngle=7.85398
    g16: ArcOfCircle CenterX=-16.28 CenterY=44.75 CenterZ=0 NormalX=0 NormalY=0 NormalZ=1 AngleXU=0 Radius=1.5 StartAngle=4.71239 EndAngle=7.85398
    g17: ArcOfCircle CenterX=-18.2337 CenterY=39 CenterZ=0 NormalX=0 NormalY=0 NormalZ=1 AngleXU=0 Radius=1.5 StartAngle=4.71485 EndAngle=7.85398
    g18: ArcOfCircle CenterX=-16.2837 CenterY=27.25 CenterZ=0 NormalX=0 NormalY=0 NormalZ=1 AngleXU=0 Radius=1.5 StartAngle=4.71485 EndAngle=7.85398
    g19: ArcOfCircle CenterX=-18.2337 CenterY=33 CenterZ=0 NormalX=0 NormalY=0 NormalZ=1 AngleXU=0 Radius=1.5 StartAngle=4.71485 EndAngle=7.85398
    g20: ArcOfCircle CenterX=-11.49 CenterY=21.5 CenterZ=0 NormalX=0 NormalY=0 NormalZ=1 AngleXU=0 Radius=1.5 StartAngle=4.71239 EndAngle=7.85398
    g21: ArcOfCircle CenterX=-1.5 CenterY=4.25 CenterZ=0 NormalX=0 NormalY=0 NormalZ=1 AngleXU=0 Radius=1.5 StartAngle=4.71239 EndAngle=7.85398
    g22: ArcOfCircle CenterX=-1.5 CenterY=10 CenterZ=0 NormalX=0 NormalY=0 NormalZ=1 AngleXU=0 Radius=1.5 StartAngle=4.71239 EndAngle=7.85398
    g23: ArcOfCircle CenterX=-1.5 CenterY=15.75 CenterZ=0 NormalX=0 NormalY=0 NormalZ=1 AngleXU=0 Radius=1.5 StartAngle=4.71239 EndAngle=7.85398
    g24: LineSegment StartX=-49.19 StartY=69.25 StartZ=0 EndX=-1.5 EndY=69.25 EndZ=0
    g25: LineSegment StartX=-49.19 StartY=66.25 StartZ=0 EndX=-1.5 EndY=66.25 EndZ=0
    g26: LineSegment StartX=-49.19 StartY=63.5 StartZ=0 EndX=-1.5 EndY=63.5 EndZ=0
    g27: LineSegment StartX=-49.19 StartY=60.5 StartZ=0 EndX=-1.5 EndY=60.5 EndZ=0
    g28: LineSegment StartX=-49.19 StartY=57.75 StartZ=0 EndX=-1.5 EndY=57.75 EndZ=0
    g29: LineSegment StartX=-49.19 StartY=54.75 StartZ=0 EndX=-1.5 EndY=54.75 EndZ=0
    g30: LineSegment StartX=-49.19 StartY=52 StartZ=0 EndX=-11.49 EndY=52 EndZ=0
    g31: LineSegment StartX=-49.19 StartY=49 StartZ=0 EndX=-11.49 EndY=49 EndZ=0
    g32: LineSegment StartX=-49.19 StartY=46.25 StartZ=0 EndX=-16.28 EndY=46.25 EndZ=0
    g33: LineSegment StartX=-49.19 StartY=43.25 StartZ=0 EndX=-16.28 EndY=43.25 EndZ=0
    g34: LineSegment StartX=-49.19 StartY=40.5 StartZ=0 EndX=-18.2337 EndY=40.5 EndZ=0
    g35: LineSegment StartX=-49.19 StartY=37.5 StartZ=0 EndX=-18.23 EndY=37.5 EndZ=0
    g36: LineSegment StartX=-49.19 StartY=34.5 StartZ=0 EndX=-18.2337 EndY=34.5 EndZ=0
    g37: LineSegment StartX=-49.19 StartY=31.5 StartZ=0 EndX=-18.23 EndY=31.5 EndZ=0
    g38: LineSegment StartX=-49.19 StartY=28.75 StartZ=0 EndX=-16.2837 EndY=28.75 EndZ=0
    g39: LineSegment StartX=-49.19 StartY=25.75 StartZ=0 EndX=-16.28 EndY=25.75 EndZ=0
    g40: LineSegment StartX=-49.19 StartY=23 StartZ=0 EndX=-11.49 EndY=23 EndZ=0
    g41: LineSegment StartX=-49.19 StartY=20 StartZ=0 EndX=-11.49 EndY=20 EndZ=0
    g42: LineSegment StartX=-49.19 StartY=17.25 StartZ=0 EndX=-1.5 EndY=17.25 EndZ=0
    g43: LineSegment StartX=-49.19 StartY=14.25 StartZ=0 EndX=-1.5 EndY=14.25 EndZ=0
    g44: LineSegment StartX=-49.19 StartY=11.5 StartZ=0 EndX=-1.5 EndY=11.5 EndZ=0
    g45: LineSegment StartX=-49.19 StartY=8.5 StartZ=0 EndX=-1.5 EndY=8.5 EndZ=0
    g46: LineSegment StartX=-49.19 StartY=5.75 StartZ=0 EndX=-1.5 EndY=5.75 EndZ=0
    g47: LineSegment StartX=-49.19 StartY=2.75 StartZ=0 EndX=-1.5 EndY=2.75 EndZ=0
  constraints (120):
    c: Vertical(g0)
    c: Distance(g0) = 3
    c: Block(g0)
    c: Vertical(g1)
    c: Distance(g1) = 3
    c: Vertical(g2)
    c: Equal(g0,g2) = 3
    c: Block(g2)
    c: Vertical(g3)
    c: Equal(g1,g3) = 3
    c: Vertical(g4)
    c: Equal(g0,g4) = 3
    c: Block(g4)
    c: Vertical(g5)
    c: Equal(g1,g5) = 3
    c: Vertical(g6)
    c: Equal(g0,g6) = 3
    c: Block(g6)
    c: Vertical(g7)
    c: Equal(g1,g7) = 3
    c: Vertical(g8)
    c: Equal(g0,g8) = 3
    c: Block(g8)
    c: Vertical(g9)
    c: Equal(g1,g9) = 3
    c: Vertical(g10)
    c: Equal(g0,g10) = 3
    c: Block(g10)
    c: Vertical(g11)
    c: Equal(g1,g11) = 3
    c: Block(g12)
    c: Block(g13)
    c: Block(g14)
    c: Block(g15)
    c: Block(g16)
    c: Block(g17)
    c: Block(g18)
    c: Block(g19)
    c: Block(g20)
    c: Block(g21)
    c: Block(g22)
    c: Block(g23)
    c: Block(g11)
    c: Block(g9)
    c: Block(g7)
    c: Block(g5)
    c: Block(g3)
    c: Block(g1)
    c: Coincident(g24,g0)
    c: Coincident(g24,g12)
    c: Horizontal(g24)
    c: Coincident(g25,g0)
    c: Coincident(g25,g12)
    c: Horizontal(g25)
    c: Coincident(g26,g1)
    c: Coincident(g26,g13)
    c: Horizontal(g26)
    c: Coincident(g27,g1)
    c: Coincident(g27,g13)
    c: Horizontal(g27)
    c: Coincident(g28,g2)
    c: Coincident(g28,g14)
    c: Horizontal(g28)
    c: Coincident(g29,g2)
    c: Coincident(g29,g14)
    c: Horizontal(g29)
    c: Coincident(g30,g3)
    c: Coincident(g30,g15)
    c: Horizontal(g30)
    c: Coincident(g31,g3)
    c: Coincident(g31,g15)
    c: Horizontal(g31)
    c: Coincident(g32,g4)
    c: Coincident(g32,g16)
    c: Horizontal(g32)
    c: Coincident(g33,g4)
    c: Coincident(g33,g16)
    c: Horizontal(g33)
    c: Coincident(g34,g5)
    c: Coincident(g34,g17)
    c: Horizontal(g34)
    c: Coincident(g35,g5)
    c: Coincident(g35,g17)
    c: Horizontal(g35)
    c: Coincident(g36,g6)
    c: Coincident(g36,g19)
    c: Horizontal(g36)
    c: Coincident(g37,g6)
    c: Coincident(g37,g19)
    c: Horizontal(g37)
    c: Coincident(g38,g7)
    c: Coincident(g38,g18)
    c: Horizontal(g38)
    c: Coincident(g39,g7)
    c: Coincident(g39,g18)
    c: Horizontal(g39)
    c: Coincident(g40,g8)
    c: Coincident(g40,g20)
    c: Horizontal(g40)
    c: Coincident(g41,g8)
    c: Coincident(g41,g20)
    c: Horizontal(g41)
    c: Coincident(g42,g9)
    c: Coincident(g42,g23)
    c: Horizontal(g42)
    c: Coincident(g43,g9)
    c: Coincident(g43,g23)
    c: Horizontal(g43)
    c: Coincident(g44,g10)
    c: Coincident(g44,g22)
    c: Horizontal(g44)
    c: Coincident(g45,g10)
    c: Coincident(g45,g22)
    c: Horizontal(g45)
    c: Coincident(g46,g11)
    c: Coincident(g46,g21)
    c: Horizontal(g46)
    c: Coincident(g47,g11)
    c: Coincident(g47,g21)
    c: Horizontal(g47)
FEATURE [Sketcher::SketchObject] Sketch031
  FullyConstrained = true
  Placement = pos=(117,19,0) rot=(0.57735,0.57735,0.57735;2.0944rad)
  sketch-geometry (24):
    g0: ArcOfCircle CenterX=-49.19 CenterY=67.75 CenterZ=0 NormalX=0 NormalY=0 NormalZ=1 AngleXU=0 Radius=1.5 StartAngle=1.5708 EndAngle=4.71239
    g1: ArcOfCircle CenterX=-49.19 CenterY=62 CenterZ=0 NormalX=0 NormalY=0 NormalZ=1 AngleXU=0 Radius=1.5 StartAngle=1.5708 EndAngle=4.71239
    g2: ArcOfCircle CenterX=-49.19 CenterY=56.25 CenterZ=0 NormalX=0 NormalY=0 NormalZ=1 AngleXU=0 Radius=1.5 StartAngle=1.5708 EndAngle=4.71239
    g3: ArcOfCircle CenterX=-49.19 CenterY=50.5 CenterZ=0 NormalX=0 NormalY=0 NormalZ=1 AngleXU=0 Radius=1.5 StartAngle=1.5708 EndAngle=4.71239
    g4: ArcOfCircle CenterX=-49.19 CenterY=44.75 CenterZ=0 NormalX=0 NormalY=0 NormalZ=1 AngleXU=0 Radius=1.5 StartAngle=1.5708 EndAngle=4.71239
    g5: ArcOfCircle CenterX=-49.19 CenterY=39 CenterZ=0 NormalX=0 NormalY=0 NormalZ=1 AngleXU=0 Radius=1.5 StartAngle=1.5708 EndAngle=4.71239
    g6: ArcOfCircle CenterX=-49.19 CenterY=33 CenterZ=0 NormalX=0 NormalY=0 NormalZ=1 AngleXU=0 Radius=1.5 StartAngle=1.5708 EndAngle=4.71239
    g7: ArcOfCircle CenterX=-49.19 CenterY=27.25 CenterZ=0 NormalX=0 NormalY=0 NormalZ=1 AngleXU=0 Radius=1.5 StartAngle=1.5708 EndAngle=4.71239
    g8: ArcOfCircle CenterX=-49.19 CenterY=21.5 CenterZ=0 NormalX=0 NormalY=0 NormalZ=1 AngleXU=0 Radius=1.5 StartAngle=1.5708 EndAngle=4.71239
    g9: ArcOfCircle CenterX=-49.19 CenterY=15.75 CenterZ=0 NormalX=0 NormalY=0 NormalZ=1 AngleXU=0 Radius=1.5 StartAngle=1.5708 EndAngle=4.71239
    g10: ArcOfCircle CenterX=-49.19 CenterY=10 CenterZ=0 NormalX=0 NormalY=0 NormalZ=1 AngleXU=0 Radius=1.5 StartAngle=1.5708 EndAngle=4.71239
    g11: ArcOfCircle CenterX=-49.19 CenterY=4.25 CenterZ=0 NormalX=0 NormalY=0 NormalZ=1 AngleXU=0 Radius=1.5 StartAngle=1.5708 EndAngle=4.71239
    g12: LineSegment StartX=-49.19 StartY=69.25 StartZ=0 EndX=-49.19 EndY=66.25 EndZ=0
    g13: LineSegment StartX=-49.19 StartY=63.5 StartZ=0 EndX=-49.19 EndY=60.5 EndZ=0
    g14: LineSegment StartX=-49.19 StartY=57.75 StartZ=0 EndX=-49.19 EndY=54.75 EndZ=0
    g15: LineSegment StartX=-49.19 StartY=52 StartZ=0 EndX=-49.19 EndY=49 EndZ=0
    g16: LineSegment StartX=-49.19 StartY=46.25 StartZ=0 EndX=-49.19 EndY=43.25 EndZ=0
    g17: LineSegment StartX=-49.19 StartY=40.5 StartZ=0 EndX=-49.19 EndY=37.5 EndZ=0
    g18: LineSegment StartX=-49.19 StartY=34.5 StartZ=0 EndX=-49.19 EndY=31.5 EndZ=0
    g19: LineSegment StartX=-49.19 StartY=28.75 StartZ=0 EndX=-49.19 EndY=25.75 EndZ=0
    g20: LineSegment StartX=-49.19 StartY=23 StartZ=0 EndX=-49.19 EndY=20 EndZ=0
    g21: LineSegment StartX=-49.19 StartY=17.25 StartZ=0 EndX=-49.19 EndY=14.25 EndZ=0
    g22: LineSegment StartX=-49.19 StartY=11.5 StartZ=0 EndX=-49.19 EndY=8.5 EndZ=0
    g23: LineSegment StartX=-49.19 StartY=5.75 StartZ=0 EndX=-49.19 EndY=2.75 EndZ=0
  constraints (48):
    c: Block(g0)
    c: Block(g1)
    c: Block(g2)
    c: Block(g3)
    c: Block(g4)
    c: Block(g5)
    c: Block(g6)
    c: Block(g7)
    c: Block(g8)
    c: Block(g9)
    c: Block(g10)
    c: Block(g11)
    c: Coincident(g12,g0)
    c: Coincident(g12,g0)
    c: Vertical(g12)
    c: Vertical(g13)
    c: Coincident(g13,g1)
    c: Vertical(g14)
    c: Coincident(g14,g2)
    c: Vertical(g15)
    c: Coincident(g15,g3)
    c: Vertical(g16)
    c: Coincident(g16,g4)
    c: Vertical(g17)
    c: Coincident(g17,g5)
    c: Vertical(g18)
    c: Coincident(g18,g6)
    c: Vertical(g19)
    c: Coincident(g19,g7)
    c: Vertical(g20)
    c: Coincident(g20,g8)
    c: Vertical(g21)
    c: Coincident(g21,g9)
    c: Vertical(g22)
    c: Coincident(g22,g10)
    c: Vertical(g23)
    c: Coincident(g23,g11)
    c: Block(g23)
    c: Block(g22)
    c: Block(g21)
    c: Block(g20)
    c: Block(g13)
    c: Block(g14)
    c: Block(g15)
    c: Block(g16)
    c: Block(g17)
    c: Block(g18)
    c: Block(g19)
FEATURE [Part::Extrusion] Extrude022
  Base = -> Sketch030
  Dir = (1,-2e-16,2e-16)
  DirMode = 2
  FaceMakerClass = Part::FaceMakerBullseye
  LengthFwd = 19
  LengthRev = 0
  Placement = pos=(-19,0,0) rot=(0,0,1;0rad)
  Solid = true
  Symmetric = false
FEATURE [Part::Fillet] Fillet022
  Base = -> Extrude022
  Edges = 24 edges r=1.49: [Edge6,Edge11,Edge18,Edge23,Edge30,Edge35,Edge42,Edge47,Edge54,Edge59,Edge66,Edge71,Edge78,Edge83,Edge90,Edge95,Edge102,Edge107,Edge114,Edge119,Edge126,Edge131,Edge138,Edge143]
FEATURE [Part::Cut] Cut020  label="top010"
  Base = -> Cut019
  Tool = -> Fillet022
FEATURE [Sketcher::SketchObject] Sketch032
  FullyConstrained = true
  Placement = pos=(117,19,0) rot=(0.57735,0.57735,0.57735;2.0944rad)
  sketch-geometry (48):
    g0: LineSegment StartX=-49.19 StartY=69.25 StartZ=0 EndX=-49.19 EndY=66.25 EndZ=0
    g1: LineSegment StartX=-49.19 StartY=63.5 StartZ=0 EndX=-49.19 EndY=60.5 EndZ=0
    g2: LineSegment StartX=-49.19 StartY=57.75 StartZ=0 EndX=-49.19 EndY=54.75 EndZ=0
    g3: LineSegment StartX=-49.19 StartY=52 StartZ=0 EndX=-49.19 EndY=49 EndZ=0
    g4: LineSegment StartX=-49.19 StartY=46.25 StartZ=0 EndX=-49.19 EndY=43.25 EndZ=0
    g5: LineSegment StartX=-49.19 StartY=40.5 StartZ=0 EndX=-49.19 EndY=37.5 EndZ=0
    g6: LineSegment StartX=-49.19 StartY=34.5 StartZ=0 EndX=-49.19 EndY=31.5 EndZ=0
    g7: LineSegment StartX=-49.19 StartY=28.75 StartZ=0 EndX=-49.19 EndY=25.75 EndZ=0
    g8: LineSegment StartX=-49.19 StartY=23 StartZ=0 EndX=-49.19 EndY=20 EndZ=0
    g9: LineSegment StartX=-49.19 StartY=17.25 StartZ=0 EndX=-49.19 EndY=14.25 EndZ=0
    g10: LineSegment StartX=-49.19 StartY=11.5 StartZ=0 EndX=-49.19 EndY=8.5 EndZ=0
    g11: LineSegment StartX=-49.19 StartY=5.75 StartZ=0 EndX=-49.19 EndY=2.75 EndZ=0
    g12: ArcOfCircle CenterX=-1.5 CenterY=67.75 CenterZ=0 NormalX=0 NormalY=0 NormalZ=1 AngleXU=0 Radius=1.5 StartAngle=4.71239 EndAngle=7.85398
    g13: ArcOfCircle CenterX=-1.5 CenterY=62 CenterZ=0 NormalX=0 NormalY=0 NormalZ=1 AngleXU=0 Radius=1.5 StartAngle=4.71239 EndAngle=7.85398
    g14: ArcOfCircle CenterX=-1.5 CenterY=56.25 CenterZ=0 NormalX=0 NormalY=0 NormalZ=1 AngleXU=0 Radius=1.5 StartAngle=4.71239 EndAngle=7.85398
    g15: ArcOfCircle CenterX=-11.49 CenterY=50.5 CenterZ=0 NormalX=0 NormalY=0 NormalZ=1 AngleXU=0 Radius=1.5 StartAngle=4.71239 EndAngle=7.85398
    g16: ArcOfCircle CenterX=-16.28 CenterY=44.75 CenterZ=0 NormalX=0 NormalY=0 NormalZ=1 AngleXU=0 Radius=1.5 StartAngle=4.71239 EndAngle=7.85398
    g17: ArcOfCircle CenterX=-18.2337 CenterY=39 CenterZ=0 NormalX=0 NormalY=0 NormalZ=1 AngleXU=0 Radius=1.5 StartAngle=4.71485 EndAngle=7.85398
    g18: ArcOfCircle CenterX=-16.2837 CenterY=27.25 CenterZ=0 NormalX=0 NormalY=0 NormalZ=1 AngleXU=0 Radius=1.5 StartAngle=4.71485 EndAngle=7.85398
    g19: ArcOfCircle CenterX=-18.2337 CenterY=33 CenterZ=0 NormalX=0 NormalY=0 NormalZ=1 AngleXU=0 Radius=1.5 StartAngle=4.71485 EndAngle=7.85398
    g20: ArcOfCircle CenterX=-11.49 CenterY=21.5 CenterZ=0 NormalX=0 NormalY=0 NormalZ=1 AngleXU=0 Radius=1.5 StartAngle=4.71239 EndAngle=7.85398
    g21: ArcOfCircle CenterX=-1.5 CenterY=4.25 CenterZ=0 NormalX=0 NormalY=0 NormalZ=1 AngleXU=0 Radius=1.5 StartAngle=4.71239 EndAngle=7.85398
    g22: ArcOfCircle CenterX=-1.5 CenterY=10 CenterZ=0 NormalX=0 NormalY=0 NormalZ=1 AngleXU=0 Radius=1.5 StartAngle=4.71239 EndAngle=7.85398
    g23: ArcOfCircle CenterX=-1.5 CenterY=15.75 CenterZ=0 NormalX=0 NormalY=0 NormalZ=1 AngleXU=0 Radius=1.5 StartAngle=4.71239 EndAngle=7.85398
    g24: LineSegment StartX=-49.19 StartY=69.25 StartZ=0 EndX=-1.5 EndY=69.25 EndZ=0
    g25: LineSegment StartX=-49.19 StartY=66.25 StartZ=0 EndX=-1.5 EndY=66.25 EndZ=0
    g26: LineSegment StartX=-49.19 StartY=63.5 StartZ=0 EndX=-1.5 EndY=63.5 EndZ=0
    g27: LineSegment StartX=-49.19 StartY=60.5 StartZ=0 EndX=-1.5 EndY=60.5 EndZ=0
    g28: LineSegment StartX=-49.19 StartY=57.75 StartZ=0 EndX=-1.5 EndY=57.75 EndZ=0
    g29: LineSegment StartX=-49.19 StartY=54.75 StartZ=0 EndX=-1.5 EndY=54.75 EndZ=0
    g30: LineSegment StartX=-49.19 StartY=52 StartZ=0 EndX=-11.49 EndY=52 EndZ=0
    g31: LineSegment StartX=-49.19 StartY=49 StartZ=0 EndX=-11.49 EndY=49 EndZ=0
    g32: LineSegment StartX=-49.19 StartY=46.25 StartZ=0 EndX=-16.28 EndY=46.25 EndZ=0
    g33: LineSegment StartX=-49.19 StartY=43.25 StartZ=0 EndX=-16.28 EndY=43.25 EndZ=0
    g34: LineSegment StartX=-49.19 StartY=40.5 StartZ=0 EndX=-18.2337 EndY=40.5 EndZ=0
    g35: LineSegment StartX=-49.19 StartY=37.5 StartZ=0 EndX=-18.23 EndY=37.5 EndZ=0
    g36: LineSegment StartX=-49.19 StartY=34.5 StartZ=0 EndX=-18.2337 EndY=34.5 EndZ=0
    g37: LineSegment StartX=-49.19 StartY=31.5 StartZ=0 EndX=-18.23 EndY=31.5 EndZ=0
    g38: LineSegment StartX=-49.19 StartY=28.75 StartZ=0 EndX=-16.2837 EndY=28.75 EndZ=0
    g39: LineSegment StartX=-49.19 StartY=25.75 StartZ=0 EndX=-16.28 EndY=25.75 EndZ=0
    g40: LineSegment StartX=-49.19 StartY=23 StartZ=0 EndX=-11.49 EndY=23 EndZ=0
    g41: LineSegment StartX=-49.19 StartY=20 StartZ=0 EndX=-11.49 EndY=20 EndZ=0
    g42: LineSegment StartX=-49.19 StartY=17.25 StartZ=0 EndX=-1.5 EndY=17.25 EndZ=0
    g43: LineSegment StartX=-49.19 StartY=14.25 StartZ=0 EndX=-1.5 EndY=14.25 EndZ=0
    g44: LineSegment StartX=-49.19 StartY=11.5 StartZ=0 EndX=-1.5 EndY=11.5 EndZ=0
    g45: LineSegment StartX=-49.19 StartY=8.5 StartZ=0 EndX=-1.5 EndY=8.5 EndZ=0
    g46: LineSegment StartX=-49.19 StartY=5.75 StartZ=0 EndX=-1.5 EndY=5.75 EndZ=0
    g47: LineSegment StartX=-49.19 StartY=2.75 StartZ=0 EndX=-1.5 EndY=2.75 EndZ=0
  constraints (120):
    c: Vertical(g0)
    c: Distance(g0) = 3
    c: Block(g0)
    c: Vertical(g1)
    c: Distance(g1) = 3
    c: Vertical(g2)
    c: Equal(g0,g2) = 3
    c: Block(g2)
    c: Vertical(g3)
    c: Equal(g1,g3) = 3
    c: Vertical(g4)
    c: Equal(g0,g4) = 3
    c: Block(g4)
    c: Vertical(g5)
    c: Equal(g1,g5) = 3
    c: Vertical(g6)
    c: Equal(g0,g6) = 3
    c: Block(g6)
    c: Vertical(g7)
    c: Equal(g1,g7) = 3
    c: Vertical(g8)
    c: Equal(g0,g8) = 3
    c: Block(g8)
    c: Vertical(g9)
    c: Equal(g1,g9) = 3
    c: Vertical(g10)
    c: Equal(g0,g10) = 3
    c: Block(g10)
    c: Vertical(g11)
    c: Equal(g1,g11) = 3
    c: Block(g12)
    c: Block(g13)
    c: Block(g14)
    c: Block(g15)
    c: Block(g16)
    c: Block(g17)
    c: Block(g18)
    c: Block(g19)
    c: Block(g20)
    c: Block(g21)
    c: Block(g22)
    c: Block(g23)
    c: Block(g11)
    c: Block(g9)
    c: Block(g7)
    c: Block(g5)
    c: Block(g3)
    c: Block(g1)
    c: Coincident(g24,g0)
    c: Coincident(g24,g12)
    c: Horizontal(g24)
    c: Coincident(g25,g0)
    c: Coincident(g25,g12)
    c: Horizontal(g25)
    c: Coincident(g26,g1)
    c: Coincident(g26,g13)
    c: Horizontal(g26)
    c: Coincident(g27,g1)
    c: Coincident(g27,g13)
    c: Horizontal(g27)
    c: Coincident(g28,g2)
    c: Coincident(g28,g14)
    c: Horizontal(g28)
    c: Coincident(g29,g2)
    c: Coincident(g29,g14)
    c: Horizontal(g29)
    c: Coincident(g30,g3)
    c: Coincident(g30,g15)
    c: Horizontal(g30)
    c: Coincident(g31,g3)
    c: Coincident(g31,g15)
    c: Horizontal(g31)
    c: Coincident(g32,g4)
    c: Coincident(g32,g16)
    c: Horizontal(g32)
    c: Coincident(g33,g4)
    c: Coincident(g33,g16)
    c: Horizontal(g33)
    c: Coincident(g34,g5)
    c: Coincident(g34,g17)
    c: Horizontal(g34)
    c: Coincident(g35,g5)
    c: Coincident(g35,g17)
    c: Horizontal(g35)
    c: Coincident(g36,g6)
    c: Coincident(g36,g19)
    c: Horizontal(g36)
    c: Coincident(g37,g6)
    c: Coincident(g37,g19)
    c: Horizontal(g37)
    c: Coincident(g38,g7)
    c: Coincident(g38,g18)
    c: Horizontal(g38)
    c: Coincident(g39,g7)
    c: Coincident(g39,g18)
    c: Horizontal(g39)
    c: Coincident(g40,g8)
    c: Coincident(g40,g20)
    c: Horizontal(g40)
    c: Coincident(g41,g8)
    c: Coincident(g41,g20)
    c: Horizontal(g41)
    c: Coincident(g42,g9)
    c: Coincident(g42,g23)
    c: Horizontal(g42)
    c: Coincident(g43,g9)
    c: Coincident(g43,g23)
    c: Horizontal(g43)
    c: Coincident(g44,g10)
    c: Coincident(g44,g22)
    c: Horizontal(g44)
    c: Coincident(g45,g10)
    c: Coincident(g45,g22)
    c: Horizontal(g45)
    c: Coincident(g46,g11)
    c: Coincident(g46,g21)
    c: Horizontal(g46)
    c: Coincident(g47,g11)
    c: Coincident(g47,g21)
    c: Horizontal(g47)
FEATURE [Part::Extrusion] Extrude023
  Base = -> Sketch032
  Dir = (1,-2e-16,2e-16)
  DirMode = 2
  FaceMakerClass = Part::FaceMakerBullseye
  LengthFwd = 19
  LengthRev = 0
  Placement = pos=(-19,0,0) rot=(0,0,1;0rad)
  Solid = true
  Symmetric = false
FEATURE [Part::Fillet] Fillet023
  Base = -> Extrude023
  Edges = <same value as first occurrence — deduplicated (x6 in doc)>
  Placement = pos=(0,0.05,0) rot=(0,0,1;0rad)
FEATURE [Part::Cut] Cut014  label="bottom003"
  Base = -> Cut007
  Tool = -> Fusion047
FEATURE [Part::Cut] Cut021  label="bottom004"
  Base = -> Cut014
  Tool = -> Fillet023
FEATURE [Sketcher::SketchObject] Sketch033
  FullyConstrained = true
  Placement = pos=(117,19,0) rot=(0.57735,0.57735,0.57735;2.0944rad)
  sketch-geometry (8):
    g0: LineSegment StartX=-49.19 StartY=69.25 StartZ=0 EndX=-49.19 EndY=66.25 EndZ=0
    g1: LineSegment StartX=-49.19 StartY=5.75 StartZ=0 EndX=-49.19 EndY=2.75 EndZ=0
    g2: ArcOfCircle CenterX=-1.5 CenterY=67.75 CenterZ=0 NormalX=0 NormalY=0 NormalZ=1 AngleXU=0 Radius=1.5 StartAngle=4.71239 EndAngle=7.85398
    g3: ArcOfCircle CenterX=-1.5 CenterY=4.25 CenterZ=0 NormalX=0 NormalY=0 NormalZ=1 AngleXU=0 Radius=1.5 StartAngle=4.71239 EndAngle=7.85398
    g4: LineSegment StartX=-49.19 StartY=69.25 StartZ=0 EndX=-1.5 EndY=69.25 EndZ=0
    g5: LineSegment StartX=-49.19 StartY=66.25 StartZ=0 EndX=-1.5 EndY=66.25 EndZ=0
    g6: LineSegment StartX=-49.19 StartY=5.75 StartZ=0 EndX=-1.5 EndY=5.75 EndZ=0
    g7: LineSegment StartX=-49.19 StartY=2.75 StartZ=0 EndX=-1.5 EndY=2.75 EndZ=0
  constraints (19):
    c: Vertical(g0)
    c: Distance(g0) = 3
    c: Block(g0)
    c: Vertical(g1)
    c: Block(g2)
    c: Block(g3)
    c: Block(g1)
    c: Coincident(g4,g0)
    c: Coincident(g4,g2)
    c: Horizontal(g4)
    c: Coincident(g5,g0)
    c: Coincident(g5,g2)
    c: Horizontal(g5)
    c: Coincident(g6,g1)
    c: Coincident(g6,g3)
    c: Horizontal(g6)
    c: Coincident(g7,g1)
    c: Coincident(g7,g3)
    c: Horizontal(g7)
FEATURE [Sketcher::SketchObject] Sketch034
  FullyConstrained = true
  Placement = pos=(117,19,0) rot=(0.57735,0.57735,0.57735;2.0944rad)
  sketch-geometry (8):
    g0: LineSegment StartX=-49.19 StartY=63.5 StartZ=0 EndX=-49.19 EndY=60.5 EndZ=0
    g1: LineSegment StartX=-49.19 StartY=11.5 StartZ=0 EndX=-49.19 EndY=8.5 EndZ=0
    g2: ArcOfCircle CenterX=-1.5 CenterY=62 CenterZ=0 NormalX=0 NormalY=0 NormalZ=1 AngleXU=0 Radius=1.5 StartAngle=4.71239 EndAngle=7.85398
    g3: ArcOfCircle CenterX=-1.5 CenterY=10 CenterZ=0 NormalX=0 NormalY=0 NormalZ=1 AngleXU=0 Radius=1.5 StartAngle=4.71239 EndAngle=7.85398
    g4: LineSegment StartX=-49.19 StartY=63.5 StartZ=0 EndX=-1.5 EndY=63.5 EndZ=0
    g5: LineSegment StartX=-49.19 StartY=60.5 StartZ=0 EndX=-1.5 EndY=60.5 EndZ=0
    g6: LineSegment StartX=-49.19 StartY=11.5 StartZ=0 EndX=-1.5 EndY=11.5 EndZ=0
    g7: LineSegment StartX=-49.19 StartY=8.5 StartZ=0 EndX=-1.5 EndY=8.5 EndZ=0
  constraints (19):
    c: Vertical(g0)
    c: Distance(g0) = 3
    c: Vertical(g1)
    c: Block(g1)
    c: Block(g2)
    c: Block(g3)
    c: Block(g0)
    c: Coincident(g4,g0)
    c: Coincident(g4,g2)
    c: Horizontal(g4)
    c: Coincident(g5,g0)
    c: Coincident(g5,g2)
    c: Horizontal(g5)
    c: Coincident(g6,g1)
    c: Coincident(g6,g3)
    c: Horizontal(g6)
    c: Coincident(g7,g1)
    c: Coincident(g7,g3)
    c: Horizontal(g7)
FEATURE [Part::Extrusion] Extrude024
  Base = -> Sketch033
  Dir = (1,0,0)
  DirMode = 2
  FaceMakerClass = Part::FaceMakerBullseye
  LengthFwd = 10
  LengthRev = 0
  Solid = true
  Symmetric = false
FEATURE [Part::Extrusion] Extrude025
  Base = -> Sketch034
  Dir = (1,0,0)
  DirMode = 2
  FaceMakerClass = Part::FaceMakerBullseye
  LengthFwd = 10
  LengthRev = 0
  Solid = true
  Symmetric = false
FEATURE [Part::Fillet] Fillet024  label="removeFromtMoreFrontCaseScrewRetainers"
  Base = -> Extrude024
  Edges = 4 edges r=1.49: [Edge6,Edge11,Edge18,Edge23]
  Placement = pos=(-11,0,0) rot=(0,0,1;0rad)
FEATURE [Part::Fillet] Fillet025  label="removeFromtMoreFrontCaseScrewRetainers001"
  Base = -> Extrude025
  Edges = 4 edges r=1.49: [Edge6,Edge11,Edge18,Edge23]
  Placement = pos=(-19,0,0) rot=(0,0,1;0rad)
FEATURE [Part::Cut] Cut022
  Base = -> Cut015
  Tool = -> Fillet025
FEATURE [Part::Cut] Cut023  label="screwRetainers"
  Base = -> Cut022
  Tool = -> Fillet024
FEATURE [Part::MultiFuse] Fusion056  label="bottom005"
  Shapes = -> [Fusion044,Cut021]
FEATURE [Part::MultiFuse] Fusion057  label="casePillars001"
  Shapes = -> [Cut016,Fusion052]
FEATURE [Part::MultiFuse] Fusion058  label="bottom006"
  Shapes = -> [Fusion056,Cut023]
FEATURE [Part::MultiFuse] Fusion059  label="bottom007"
  Shapes = -> [Fusion058,Fillet005]
FEATURE [Part::MultiFuse] Fusion060  label="bottom008"
  Shapes = -> [Fusion059,Fusion]
FEATURE [Part::MultiFuse] Fusion061  label="top011"
  Shapes = -> [Cut006,Cut020]
FEATURE [Part::MultiFuse] Fusion062  label="top012"
  Shapes = -> [Fusion057,Fusion061]
FEATURE [Sketcher::SketchObject] Sketch035  label="topSketch007"
  FullyConstrained = true
  sketch-geometry (6):
    g0: LineSegment StartX=19 StartY=38 StartZ=0 EndX=117 EndY=38 EndZ=0
    g1: ArcOfCircle CenterX=19 CenterY=19 CenterZ=0 NormalX=0 NormalY=0 NormalZ=1 AngleXU=0 Radius=19 StartAngle=1.5708 EndAngle=3.14159
    g2: LineSegment StartX=117 StartY=38 StartZ=0 EndX=117 EndY=19 EndZ=0
    g3: LineSegment StartX=98 StartY=1.0161e-12 StartZ=0 EndX=5.22862e-06 EndY=1.0161e-12 EndZ=0
    g4: LineSegment StartX=5.22862e-06 StartY=19 StartZ=0 EndX=5.22862e-06 EndY=1.0161e-12 EndZ=0
    g5: ArcOfCircle CenterX=98 CenterY=19 CenterZ=0 NormalX=0 NormalY=0 NormalZ=1 AngleXU=0 Radius=19 StartAngle=4.71239 EndAngle=6.28319
  constraints (16):
    c: Horizontal(g0)
    c: Distance(g0) = 98
    c: Coincident(g1,g0)
    c: Block(g1)
    c: Coincident(g2,g0)
    c: Vertical(g2)
    c: Distance(g2) = 19
    c: Horizontal(g3)
    c: Coincident(g4,g1)
    c: Vertical(g4)
    c: Coincident(g3,g4)
    c: Block(g3)
    c: Coincident(g5,g2)
    c: Coincident(g5,g3)
    c: Block(g0)
    c: Block(g5)
FEATURE [Part::Extrusion] Extrude026  label="sideA001"
  Base = -> Sketch035
  Dir = (0,0,1)
  DirMode = 2
  FaceMakerClass = Part::FaceMakerBullseye
  LengthFwd = 3
  LengthRev = 0
  Placement = pos=(0,0,-2.7) rot=(0,0,1;0rad)
  Solid = true
  Symmetric = false
FEATURE [Sketcher::SketchObject] Sketch036  label="topSketch008"
  FullyConstrained = true
  sketch-geometry (6):
    g0: LineSegment StartX=19 StartY=38 StartZ=0 EndX=117 EndY=38 EndZ=0
    g1: ArcOfCircle CenterX=19 CenterY=19 CenterZ=0 NormalX=0 NormalY=0 NormalZ=1 AngleXU=0 Radius=19 StartAngle=1.5708 EndAngle=3.14159
    g2: LineSegment StartX=117 StartY=38 StartZ=0 EndX=117 EndY=19 EndZ=0
    g3: LineSegment StartX=98 StartY=1.0161e-12 StartZ=0 EndX=5.22862e-06 EndY=1.0161e-12 EndZ=0
    g4: LineSegment StartX=5.22862e-06 StartY=19 StartZ=0 EndX=5.22862e-06 EndY=1.0161e-12 EndZ=0
    g5: ArcOfCircle CenterX=98 CenterY=19 CenterZ=0 NormalX=0 NormalY=0 NormalZ=1 AngleXU=0 Radius=19 StartAngle=4.71239 EndAngle=6.28319
  constraints (16):
    c: Horizontal(g0)
    c: Distance(g0) = 98
    c: Coincident(g1,g0)
    c: Block(g1)
    c: Coincident(g2,g0)
    c: Vertical(g2)
    c: Distance(g2) = 19
    c: Horizontal(g3)
    c: Coincident(g4,g1)
    c: Vertical(g4)
    c: Coincident(g3,g4)
    c: Block(g3)
    c: Coincident(g5,g2)
    c: Coincident(g5,g3)
    c: Block(g0)
    c: Block(g5)
FEATURE [Part::Extrusion] Extrude027  label="sideB001"
  Base = -> Sketch036
  Dir = (0,0,1)
  DirMode = 2
  FaceMakerClass = Part::FaceMakerBullseye
  LengthFwd = 3
  LengthRev = 0
  Placement = pos=(0,0,71.7) rot=(0,0,1;0rad)
  Solid = true
  Symmetric = false
FEATURE [Part::MultiFuse] Fusion064  label="removeFromBottom"
  Shapes = -> [Extrude026,Extrude027]
FEATURE [Part::Cut] Cut024  label="bottom009"
  Base = -> Fusion060
  Tool = -> Fusion064
FEATURE [Sketcher::SketchObject] Sketch037  label="topSketch009"
  FullyConstrained = true
  sketch-geometry (8):
    g0: ArcOfCircle CenterX=19 CenterY=19.1201 CenterZ=0 NormalX=0 NormalY=0 NormalZ=1 AngleXU=0 Radius=18.8799 StartAngle=1.5708 EndAngle=3.14793
    g1: LineSegment StartX=0.120501 StartY=19.0004 StartZ=0 EndX=0.120501 EndY=0.000382114 EndZ=0
    g2: LineSegment StartX=19 StartY=38 StartZ=0 EndX=124 EndY=38 EndZ=0
    g3: LineSegment StartX=0.120501 StartY=0.000382114 StartZ=0 EndX=105.121 EndY=0.000382114 EndZ=0
    g4: LineSegment StartX=124 StartY=38 StartZ=0 EndX=125.616 EndY=38 EndZ=0
    g5: LineSegment StartX=105.121 StartY=0.000382114 StartZ=0 EndX=106.736 EndY=0.000382114 EndZ=0
    g6: ArcOfCircle CenterX=106.616 CenterY=19 CenterZ=0 NormalX=0 NormalY=0 NormalZ=1 AngleXU=0 Radius=19 StartAngle=4.71873 EndAngle=6.28319
    g7: LineSegment StartX=125.616 StartY=38 StartZ=0 EndX=125.616 EndY=19 EndZ=0
  constraints (21):
    c: Block(g0)
    c: Coincident(g1,g0)
    c: Vertical(g1)
    c: Horizontal(g2)
    c: Distance(g2) = 105
    c: Coincident(g2,g0)
    c: Distance(g1) = 19
    c: Coincident(g3,g1)
    c: Horizontal(g3)
    c: Distance(g3) = 105
    c: Coincident(g4,g2)
    c: Horizontal(g4)
    c: Distance(g4) = 1.61553
    c: Horizontal(g5)
    c: Equal(g4,g5) = 1.61553
    c: Coincident(g5,g3)
    c: Block(g6)
    c: Coincident(g6,g5)
    c: Coincident(g7,g4)
    c: Coincident(g7,g6)
    c: Vertical(g7)
FEATURE [Part::Extrusion] Extrude028  label="sideB"
  Base = -> Sketch037
  Dir = (0,0,1)
  DirMode = 2
  FaceMakerClass = Part::FaceMakerBullseye
  LengthFwd = 3
  LengthRev = 0
  Placement = pos=(0,0,72) rot=(0,0,1;0rad)
  Solid = true
  Symmetric = false
FEATURE [Sketcher::SketchObject] Sketch038  label="topSketch010"
  FullyConstrained = true
  sketch-geometry (22):
    g0: LineSegment StartX=5.21097e-06 StartY=3 StartZ=0 EndX=5.21097e-06 EndY=19 EndZ=0
    g1: ArcOfCircle CenterX=19 CenterY=19 CenterZ=0 NormalX=0 NormalY=0 NormalZ=1 AngleXU=0 Radius=19 StartAngle=1.5708 EndAngle=3.14159
    g2: ArcOfCircle CenterX=19 CenterY=19 CenterZ=0 NormalX=0 NormalY=0 NormalZ=1 AngleXU=0 Radius=16 StartAngle=1.5708 EndAngle=3.14159
    g3: LineSegment StartX=114 StartY=35 StartZ=0 EndX=19 EndY=35 EndZ=0
    g4: LineSegment StartX=5.21097e-06 StartY=3 StartZ=0 EndX=5.21097e-06 EndY=0 EndZ=0
    g5: LineSegment StartX=3 StartY=0 StartZ=0 EndX=5.21097e-06 EndY=0 EndZ=0
    g6: LineSegment StartX=3 StartY=19 StartZ=0 EndX=3 EndY=0 EndZ=0
    g7: LineSegment StartX=19 StartY=38 StartZ=0 EndX=124 EndY=38 EndZ=0
    g8: Circle CenterX=119 CenterY=35 CenterZ=0 NormalX=0 NormalY=0 NormalZ=1 AngleXU=0 Radius=1
    g9: Circle CenterX=121 CenterY=35 CenterZ=0 NormalX=0 NormalY=0 NormalZ=1 AngleXU=0 Radius=1
    g10: Circle CenterX=121 CenterY=33 CenterZ=0 NormalX=0 NormalY=0 NormalZ=1 AngleXU=0 Radius=1
    g11: BSplineCurve PolesCount=3 KnotsCount=2 Degree=2 IsPeriodic=0
    g12: GeomPoint X=119 Y=35 Z=0
    g13: GeomPoint X=121 Y=33 Z=0
    g14: LineSegment StartX=119 StartY=35 StartZ=0 EndX=114 EndY=35 EndZ=0
    g15: ArcOfCircle CenterX=105 CenterY=19 CenterZ=0 NormalX=0 NormalY=0 NormalZ=1 AngleXU=0 Radius=16 StartAngle=5.60905 EndAngle=6.28319
    g16: LineSegment StartX=121 StartY=33 StartZ=0 EndX=121 EndY=19 EndZ=0
    g17: LineSegment StartX=117.5 StartY=9.01251 StartZ=0 EndX=121.163 EndY=9.0125 EndZ=0
    g18: ArcOfCircle CenterX=105 CenterY=19 CenterZ=0 NormalX=0 NormalY=0 NormalZ=1 AngleXU=0 Radius=20.6155 StartAngle=5.7297 EndAngle=6.28319
    g19: LineSegment StartX=121.163 StartY=9.0125 StartZ=0 EndX=122.538 EndY=8.16329 EndZ=0
    g20: LineSegment StartX=124 StartY=38 StartZ=0 EndX=125.616 EndY=38 EndZ=0
    g21: LineSegment StartX=125.616 StartY=19 StartZ=0 EndX=125.616 EndY=38 EndZ=0
  constraints (49):
    c: Vertical(g0)
    c: Block(g0)
    c: Coincident(g1,g0)
    c: Block(g1)
    c: Coincident(g2,g1)
    c: Block(g2)
    c: Coincident(g3,g2)
    c: Horizontal(g3)
    c: Tangent(g3,g2)
    c: Coincident(g4,g0)
    c: Distance(g4) = 3
    c: Vertical(g4)
    c: Coincident(g5,g4)
    c: Horizontal(g5)
    c: Coincident(g6,g2)
    c: Coincident(g6,g5)
    c: Vertical(g6)
    c: Horizontal(g7)
    c: Distance(g7) = 105
    c: Coincident(g7,g1)
    c: Block(g3)
    c: Weight(g8) = 1
    c: Equal(g8,g9)
    c: Equal(g8,g10)
    c: InternalAlignment(g8,g11)
    c: InternalAlignment(g9,g11)
    c: InternalAlignment(g10,g11)
    c: InternalAlignment(g12,g11)
    c: InternalAlignment(g13,g11)
    c: Block(g11)
    c: Coincident(g14,g11)
    c: Coincident(g14,g3)
    c: Horizontal(g14)
    c: Block(g15)
    c: Coincident(g16,g11)
    c: Coincident(g16,g15)
    c: Vertical(g16)
    c: Distance(g16) = 14
    c: Coincident(g17,g15)
    c: Block(g18)
    c: Coincident(g19,g18)
    c: Coincident(g20,g7)
    c: Horizontal(g20)
    c: Vertical(g21)
    c: Coincident(g20,g21)
    c: Block(g20)
    c: Block(g21)
    c: Block(g19)
    c: Block(g17)
FEATURE [Part::Extrusion] Extrude029
  Base = -> Sketch038
  Dir = (0,0,1)
  DirMode = 2
  FaceMakerClass = Part::FaceMakerBullseye
  LengthFwd = 72
  LengthRev = 0
  Solid = true
  Symmetric = false
FEATURE [Part::Feature] Face085
  shape: bbox 4.8 x 25.5 x 2e-07 mm, 1 faces, 0 solids (baked)
FEATURE [Part::Revolution] Revolve089  label="moreFrontCaseScrewPost003"
  Angle = 360
  Axis = (0,1,0)
  Base = (0,0,0)
  FaceMakerClass = Part::FaceMakerBullseye
  Placement = pos=(109.5,4.5,3.5) rot=(0,0,1;0rad)
  Solid = false
  Source = -> Face085
  Symmetric = false
FEATURE [Part::Feature] Face086
  shape: bbox 4.8 x 25.5 x 2e-07 mm, 1 faces, 0 solids (baked)
FEATURE [Part::Revolution] Revolve090  label="moreFrontCaseScrewPost004"
  Angle = 360
  Axis = (0,1,0)
  Base = (0,0,0)
  FaceMakerClass = Part::FaceMakerBullseye
  Placement = pos=(109.5,4.5,68.5) rot=(0,0,1;0rad)
  Solid = false
  Source = -> Face086
  Symmetric = false
FEATURE [Part::Fillet] Fillet026  label="top013"
  Base = -> Extrude029
  Edges = 1 edges r=2: [Edge35]
FEATURE [Sketcher::SketchObject] Sketch039
  FullyConstrained = true
  sketch-geometry (7):
    g0: LineSegment StartX=0 StartY=0 StartZ=0 EndX=0 EndY=6 EndZ=0
    g1: Circle CenterX=0 CenterY=0 CenterZ=0 NormalX=0 NormalY=0 NormalZ=1 AngleXU=0 Radius=1
    g2: Circle CenterX=8 CenterY=6 CenterZ=0 NormalX=0 NormalY=0 NormalZ=1 AngleXU=0 Radius=1
    g3: BSplineCurve PolesCount=3 KnotsCount=2 Degree=2 IsPeriodic=0
    g4: GeomPoint X=0 Y=0 Z=0
    g5: GeomPoint X=8 Y=6 Z=0
    g6: LineSegment StartX=0 StartY=6 StartZ=0 EndX=8 EndY=6 EndZ=0
  constraints (14):
    c: Coincident(g0,g-1)
    c: Distance(g0) = 6
    c: Vertical(g0)
    c: Coincident(g3,g0)
    c: Weight(g1) = 1
    c: Equal(g1,g2)
    c: InternalAlignment(g1,g3)
    c: InternalAlignment(g2,g3)
    c: InternalAlignment(g4,g3)
    c: InternalAlignment(g5,g3)
    c: Block(g3)
    c: Coincident(g6,g0)
    c: Coincident(g6,g3)
    c: Horizontal(g6)
FEATURE [Sketcher::SketchObject] Sketch040
  FullyConstrained = true
  sketch-geometry (7):
    g0: LineSegment StartX=0 StartY=0 StartZ=0 EndX=0 EndY=6 EndZ=0
    g1: Circle CenterX=0 CenterY=0 CenterZ=0 NormalX=0 NormalY=0 NormalZ=1 AngleXU=0 Radius=1
    g2: Circle CenterX=8 CenterY=6 CenterZ=0 NormalX=0 NormalY=0 NormalZ=1 AngleXU=0 Radius=1
    g3: BSplineCurve PolesCount=3 KnotsCount=2 Degree=2 IsPeriodic=0
    g4: GeomPoint X=0 Y=0 Z=0
    g5: GeomPoint X=8 Y=6 Z=0
    g6: LineSegment StartX=0 StartY=6 StartZ=0 EndX=8 EndY=6 EndZ=0
  constraints (14):
    c: Coincident(g0,g-1)
    c: Distance(g0) = 6
    c: Vertical(g0)
    c: Coincident(g3,g0)
    c: Weight(g1) = 1
    c: Equal(g1,g2)
    c: InternalAlignment(g1,g3)
    c: InternalAlignment(g2,g3)
    c: InternalAlignment(g4,g3)
    c: InternalAlignment(g5,g3)
    c: Block(g3)
    c: Coincident(g6,g0)
    c: Coincident(g6,g3)
    c: Horizontal(g6)
FEATURE [Sketcher::SketchObject] Sketch041
  FullyConstrained = true
  sketch-geometry (7):
    g0: LineSegment StartX=0 StartY=0 StartZ=0 EndX=0 EndY=6 EndZ=0
    g1: Circle CenterX=0 CenterY=0 CenterZ=0 NormalX=0 NormalY=0 NormalZ=1 AngleXU=0 Radius=1
    g2: Circle CenterX=8 CenterY=6 CenterZ=0 NormalX=0 NormalY=0 NormalZ=1 AngleXU=0 Radius=1
    g3: BSplineCurve PolesCount=3 KnotsCount=2 Degree=2 IsPeriodic=0
    g4: GeomPoint X=0 Y=0 Z=0
    g5: GeomPoint X=8 Y=6 Z=0
    g6: LineSegment StartX=0 StartY=6 StartZ=0 EndX=8 EndY=6 EndZ=0
  constraints (14):
    c: Coincident(g0,g-1)
    c: Distance(g0) = 6
    c: Vertical(g0)
    c: Coincident(g3,g0)
    c: Weight(g1) = 1
    c: Equal(g1,g2)
    c: InternalAlignment(g1,g3)
    c: InternalAlignment(g2,g3)
    c: InternalAlignment(g4,g3)
    c: InternalAlignment(g5,g3)
    c: Block(g3)
    c: Coincident(g6,g0)
    c: Coincident(g6,g3)
    c: Horizontal(g6)
FEATURE [Sketcher::SketchObject] Sketch042
  FullyConstrained = true
  sketch-geometry (7):
    g0: LineSegment StartX=0 StartY=0 StartZ=0 EndX=0 EndY=6 EndZ=0
    g1: Circle CenterX=0 CenterY=0 CenterZ=0 NormalX=0 NormalY=0 NormalZ=1 AngleXU=0 Radius=1
    g2: Circle CenterX=8 CenterY=6 CenterZ=0 NormalX=0 NormalY=0 NormalZ=1 AngleXU=0 Radius=1
    g3: BSplineCurve PolesCount=3 KnotsCount=2 Degree=2 IsPeriodic=0
    g4: GeomPoint X=0 Y=0 Z=0
    g5: GeomPoint X=8 Y=6 Z=0
    g6: LineSegment StartX=0 StartY=6 StartZ=0 EndX=8 EndY=6 EndZ=0
  constraints (14):
    c: Coincident(g0,g-1)
    c: Distance(g0) = 6
    c: Vertical(g0)
    c: Coincident(g3,g0)
    c: Weight(g1) = 1
    c: Equal(g1,g2)
    c: InternalAlignment(g1,g3)
    c: InternalAlignment(g2,g3)
    c: InternalAlignment(g4,g3)
    c: InternalAlignment(g5,g3)
    c: Block(g3)
    c: Coincident(g6,g0)
    c: Coincident(g6,g3)
    c: Horizontal(g6)
FEATURE [Part::Extrusion] Extrude030  label="caseScrewPillarBracket008"
  Base = -> Sketch039
  Dir = (0,0,1)
  DirMode = 2
  FaceMakerClass = Part::FaceMakerBullseye
  LengthFwd = 2.4
  LengthRev = 0
  Placement = pos=(15.76,29,8.8) rot=(0,1,0;0rad)
  Solid = true
  Symmetric = false
FEATURE [Part::Extrusion] Extrude031  label="caseScrewPillarBracket009"
  Base = -> Sketch040
  Dir = (0,0,1)
  DirMode = 2
  FaceMakerClass = Part::FaceMakerBullseye
  LengthFwd = 2.4
  LengthRev = 0
  Placement = pos=(15.76,29,60.8) rot=(0,0,1;0rad)
  Solid = true
  Symmetric = false
FEATURE [Part::Extrusion] Extrude032  label="caseScrewPillarBracket010"
  Base = -> Sketch041
  Dir = (0,0,1)
  DirMode = 2
  FaceMakerClass = Part::FaceMakerBullseye
  LengthFwd = 2.4
  LengthRev = 0
  Placement = pos=(13.7,29,13.26) rot=(0,-1,0;1.5708rad)
  Solid = true
  Symmetric = false
FEATURE [Part::Extrusion] Extrude033  label="caseScrewPillarBracket011"
  Base = -> Sketch042
  Dir = (0,0,1)
  DirMode = 2
  FaceMakerClass = Part::FaceMakerBullseye
  LengthFwd = 2.4
  LengthRev = 0
  Placement = pos=(11.3,29,58.74) rot=(0,1,0;1.5708rad)
  Solid = true
  Symmetric = false
FEATURE [Sketcher::SketchObject] Sketch043
  FullyConstrained = true
  sketch-geometry (7):
    g0: LineSegment StartX=0 StartY=0 StartZ=0 EndX=0 EndY=6 EndZ=0
    g1: Circle CenterX=0 CenterY=0 CenterZ=0 NormalX=0 NormalY=0 NormalZ=1 AngleXU=0 Radius=1
    g2: Circle CenterX=8 CenterY=6 CenterZ=0 NormalX=0 NormalY=0 NormalZ=1 AngleXU=0 Radius=1
    g3: BSplineCurve PolesCount=3 KnotsCount=2 Degree=2 IsPeriodic=0
    g4: GeomPoint X=0 Y=0 Z=0
    g5: GeomPoint X=8 Y=6 Z=0
    g6: LineSegment StartX=0 StartY=6 StartZ=0 EndX=8 EndY=6 EndZ=0
  constraints (14):
    c: Coincident(g0,g-1)
    c: Distance(g0) = 6
    c: Vertical(g0)
    c: Coincident(g3,g0)
    c: Weight(g1) = 1
    c: Equal(g1,g2)
    c: InternalAlignment(g1,g3)
    c: InternalAlignment(g2,g3)
    c: InternalAlignment(g4,g3)
    c: InternalAlignment(g5,g3)
    c: Block(g3)
    c: Coincident(g6,g0)
    c: Coincident(g6,g3)
    c: Horizontal(g6)
FEATURE [Part::Extrusion] Extrude034  label="caseScrewPillarBracket012"
  Base = -> Sketch043
  Dir = (0,0,1)
  DirMode = 2
  FaceMakerClass = Part::FaceMakerBullseye
  LengthFwd = 2.4
  LengthRev = 0
  Placement = pos=(88.3,29,65.23) rot=(0,1,0;1.5708rad)
  Solid = true
  Symmetric = false
FEATURE [Sketcher::SketchObject] Sketch044
  FullyConstrained = true
  sketch-geometry (7):
    g0: LineSegment StartX=0 StartY=0 StartZ=0 EndX=0 EndY=6 EndZ=0
    g1: Circle CenterX=0 CenterY=0 CenterZ=0 NormalX=0 NormalY=0 NormalZ=1 AngleXU=0 Radius=1
    g2: Circle CenterX=8 CenterY=6 CenterZ=0 NormalX=0 NormalY=0 NormalZ=1 AngleXU=0 Radius=1
    g3: BSplineCurve PolesCount=3 KnotsCount=2 Degree=2 IsPeriodic=0
    g4: GeomPoint X=0 Y=0 Z=0
    g5: GeomPoint X=8 Y=6 Z=0
    g6: LineSegment StartX=0 StartY=6 StartZ=0 EndX=8 EndY=6 EndZ=0
  constraints (14):
    c: Coincident(g0,g-1)
    c: Distance(g0) = 6
    c: Vertical(g0)
    c: Coincident(g3,g0)
    c: Weight(g1) = 1
    c: Equal(g1,g2)
    c: InternalAlignment(g1,g3)
    c: InternalAlignment(g2,g3)
    c: InternalAlignment(g4,g3)
    c: InternalAlignment(g5,g3)
    c: Block(g3)
    c: Coincident(g6,g0)
    c: Coincident(g6,g3)
    c: Horizontal(g6)
FEATURE [Part::Extrusion] Extrude035  label="caseScrewPillarBracket013"
  Base = -> Sketch044
  Dir = (0,0,1)
  DirMode = 2
  FaceMakerClass = Part::FaceMakerBullseye
  LengthFwd = 2.4
  LengthRev = 0
  Placement = pos=(90.7,29,6.77) rot=(0,-1,0;1.5708rad)
  Solid = true
  Symmetric = false
FEATURE [Sketcher::SketchObject] Sketch045
  FullyConstrained = true
  sketch-geometry (7):
    g0: LineSegment StartX=0 StartY=0 StartZ=0 EndX=0 EndY=6 EndZ=0
    g1: Circle CenterX=0 CenterY=0 CenterZ=0 NormalX=0 NormalY=0 NormalZ=1 AngleXU=0 Radius=1
    g2: Circle CenterX=8 CenterY=6 CenterZ=0 NormalX=0 NormalY=0 NormalZ=1 AngleXU=0 Radius=1
    g3: BSplineCurve PolesCount=3 KnotsCount=2 Degree=2 IsPeriodic=0
    g4: GeomPoint X=0 Y=0 Z=0
    g5: GeomPoint X=8 Y=6 Z=0
    g6: LineSegment StartX=0 StartY=6 StartZ=0 EndX=8 EndY=6 EndZ=0
  constraints (14):
    c: Coincident(g0,g-1)
    c: Distance(g0) = 6
    c: Vertical(g0)
    c: Coincident(g3,g0)
    c: Weight(g1) = 1
    c: Equal(g1,g2)
    c: InternalAlignment(g1,g3)
    c: InternalAlignment(g2,g3)
    c: InternalAlignment(g4,g3)
    c: InternalAlignment(g5,g3)
    c: Block(g3)
    c: Coincident(g6,g0)
    c: Coincident(g6,g3)
    c: Horizontal(g6)
FEATURE [Sketcher::SketchObject] Sketch046
  FullyConstrained = true
  sketch-geometry (7):
    g0: LineSegment StartX=0 StartY=0 StartZ=0 EndX=0 EndY=6 EndZ=0
    g1: Circle CenterX=0 CenterY=0 CenterZ=0 NormalX=0 NormalY=0 NormalZ=1 AngleXU=0 Radius=1
    g2: Circle CenterX=8 CenterY=6 CenterZ=0 NormalX=0 NormalY=0 NormalZ=1 AngleXU=0 Radius=1
    g3: BSplineCurve PolesCount=3 KnotsCount=2 Degree=2 IsPeriodic=0
    g4: GeomPoint X=0 Y=0 Z=0
    g5: GeomPoint X=8 Y=6 Z=0
    g6: LineSegment StartX=0 StartY=6 StartZ=0 EndX=8 EndY=6 EndZ=0
  constraints (14):
    c: Coincident(g0,g-1)
    c: Distance(g0) = 6
    c: Vertical(g0)
    c: Coincident(g3,g0)
    c: Weight(g1) = 1
    c: Equal(g1,g2)
    c: InternalAlignment(g1,g3)
    c: InternalAlignment(g2,g3)
    c: InternalAlignment(g4,g3)
    c: InternalAlignment(g5,g3)
    c: Block(g3)
    c: Coincident(g6,g0)
    c: Coincident(g6,g3)
    c: Horizontal(g6)
FEATURE [Part::Extrusion] Extrude036  label="caseScrewPillarBracket014"
  Base = -> Sketch045
  Dir = (0,0,1)
  DirMode = 2
  FaceMakerClass = Part::FaceMakerBullseye
  LengthFwd = 2.4
  LengthRev = 0
  Placement = pos=(110.7,29,6.77) rot=(0,-1,0;1.5708rad)
  Solid = true
  Symmetric = false
FEATURE [Part::Extrusion] Extrude037  label="caseScrewPillarBracket015"
  Base = -> Sketch046
  Dir = (0,0,1)
  DirMode = 2
  FaceMakerClass = Part::FaceMakerBullseye
  LengthFwd = 2.4
  LengthRev = 0
  Placement = pos=(108.3,29,65.23) rot=(0,1,0;1.5708rad)
  Solid = true
  Symmetric = false
FEATURE [Part::Box] Box013  label="frontCaseScrewPillarBracket002"
  AttacherType = Attacher::AttachEngine3D
  Height = 2.4
  Length = 22
  Placement = pos=(87,28,2.3) rot=(0,0,1;0rad)
  Width = 7
FEATURE [Part::Box] Box014  label="frontCaseScrewPillarBracket003"
  AttacherType = Attacher::AttachEngine3D
  Height = 2.4
  Length = 22
  Placement = pos=(87,28,67.3) rot=(0,0,1;0rad)
  Width = 7
FEATURE [Part::Feature] Face087
  shape: bbox 4.8 x 30.2 x 2e-07 mm, 1 faces, 0 solids (baked)
FEATURE [Part::Revolution] Revolve091  label="frontCaseScrewPost004"
  Angle = 360
  Axis = (0,1,0)
  Base = (0,0,0)
  FaceMakerClass = Part::FaceMakerBullseye
  Placement = pos=(89.5,4.5,3.5) rot=(0,0,1;0rad)
  Solid = false
  Source = -> Face087
  Symmetric = false
FEATURE [Part::Feature] Face088
  shape: bbox 4.8 x 30.2 x 2e-07 mm, 1 faces, 0 solids (baked)
FEATURE [Part::Revolution] Revolve092  label="frontCaseScrewPost005"
  Angle = 360
  Axis = (0,1,0)
  Base = (0,0,0)
  FaceMakerClass = Part::FaceMakerBullseye
  Placement = pos=(89.5,4.5,68.5) rot=(0,0,1;0rad)
  Solid = false
  Source = -> Face088
  Symmetric = false
FEATURE [Part::Feature] Face089
  shape: bbox 3.5 x 30.2 x 2e-07 mm, 1 faces, 0 solids (baked)
FEATURE [Part::Revolution] Revolve093  label="backCaseScrewPost002"
  Angle = 360
  Axis = (0,1,0)
  Base = (0,0,0)
  FaceMakerClass = Part::FaceMakerBullseye
  Placement = pos=(12.5,4.5,10) rot=(0,0,1;0rad)
  Solid = false
  Source = -> Face089
  Symmetric = false
FEATURE [Part::Feature] Face090
  shape: bbox 3.5 x 30.2 x 2e-07 mm, 1 faces, 0 solids (baked)
FEATURE [Part::Revolution] Revolve094  label="backCaseScrewPost003"
  Angle = 360
  Axis = (0,1,0)
  Base = (0,0,0)
  FaceMakerClass = Part::FaceMakerBullseye
  Placement = pos=(12.5,4.5,62) rot=(0,0,1;0rad)
  Solid = false
  Source = -> Face090
  Symmetric = false
FEATURE [Part::Box] Box015  label="Cube011"
  AttacherType = Attacher::AttachEngine3D
  Height = 28.8
  Length = 3
  Placement = pos=(107.3,28,21.6) rot=(0,0,1;0rad)
  Width = 7
FEATURE [Part::Box] Box016  label="Cube012"
  AttacherType = Attacher::AttachEngine3D
  Height = 3
  Length = 7.4
  Placement = pos=(107.3,28,18.6) rot=(0,0,1;0rad)
  Width = 7
FEATURE [Part::Box] Box017  label="Cube013"
  AttacherType = Attacher::AttachEngine3D
  Height = 3
  Length = 7.4
  Placement = pos=(107.3,28,50.4) rot=(0,0,1;0rad)
  Width = 7
FEATURE [Part::Cylinder] Cylinder024
  Angle = 360
  AttacherType = Attacher::AttachEngine3D
  Height = 20
  Placement = pos=(0,0,36.15) rot=(0,0,1;0rad)
  Radius = 14.3
FEATURE [Part::Cylinder] Cylinder025
  Angle = 360
  AttacherType = Attacher::AttachEngine3D
  Height = 10
  Placement = pos=(0,0,36.15) rot=(0,0,1;0rad)
  Radius = 4
FEATURE [Part::MultiFuse] Fusion066  label="removeToCreteHoleForPlugHousing009"
  Placement = pos=(70,19,36) rot=(0,1,0;1.5708rad)
  Shapes = -> [Cylinder024,Cylinder025]
FEATURE [Part::MultiFuse] Fusion065  label="plugHousingBracketHolder002"
  Shapes = -> [Box017,Box015,Box016]
FEATURE [Part::Cut] Cut025  label="plugHousingBracketHolder003"
  Base = -> Fusion065
  Placement = pos=(7,0,0) rot=(0,0,1;0rad)
  Tool = -> Fusion066
FEATURE [Sketcher::SketchObject] Sketch047
  FullyConstrained = false
  Placement = pos=(0,0,0) rot=(1,0,0;1.5708rad)
  sketch-geometry (24):
    g0: ArcOfCircle CenterX=-4 CenterY=-10.5 CenterZ=0 NormalX=0 NormalY=0 NormalZ=1 AngleXU=0 Radius=1.5 StartAngle=6e-16 EndAngle=3.14159
    g1: ArcOfCircle CenterX=-34.2 CenterY=-10.5 CenterZ=0 NormalX=0 NormalY=0 NormalZ=1 AngleXU=0 Radius=1.5 StartAngle=0 EndAngle=3.14159
    g2: ArcOfCircle CenterX=-34.2 CenterY=-27.7 CenterZ=0 NormalX=0 NormalY=0 NormalZ=1 AngleXU=0 Radius=1.5 StartAngle=3.14159 EndAngle=6.28319
    g3: ArcOfCircle CenterX=-4 CenterY=-27.7 CenterZ=0 NormalX=0 NormalY=0 NormalZ=1 AngleXU=0 Radius=1.5 StartAngle=3.1416 EndAngle=6.28319
    g4: ArcOfCircle CenterX=-10 CenterY=-4.3 CenterZ=0 NormalX=0 NormalY=0 NormalZ=1 AngleXU=0 Radius=1.5 StartAngle=2e-16 EndAngle=3.14159
    g5: ArcOfCircle CenterX=-16.1 CenterY=-1.8 CenterZ=0 NormalX=0 NormalY=0 NormalZ=1 AngleXU=0 Radius=1.5 StartAngle=5e-16 EndAngle=3.14159
    g6: ArcOfCircle CenterX=-22.1 CenterY=-1.8 CenterZ=0 NormalX=0 NormalY=0 NormalZ=1 AngleXU=0 Radius=1.5 StartAngle=5e-16 EndAngle=3.14159
    g7: ArcOfCircle CenterX=-28.2 CenterY=-4.3 CenterZ=0 NormalX=0 NormalY=0 NormalZ=1 AngleXU=0 Radius=1.5 StartAngle=2e-16 EndAngle=3.14159
    g8: ArcOfCircle CenterX=-10 CenterY=-33.9 CenterZ=0 NormalX=0 NormalY=0 NormalZ=1 AngleXU=0 Radius=1.5 StartAngle=3.14159 EndAngle=6.28319
    g9: ArcOfCircle CenterX=-16.1 CenterY=-36.4 CenterZ=0 NormalX=0 NormalY=0 NormalZ=1 AngleXU=0 Radius=1.5 StartAngle=3.14159 EndAngle=6.28319
    g10: ArcOfCircle CenterX=-22.1 CenterY=-36.4 CenterZ=0 NormalX=0 NormalY=0 NormalZ=1 AngleXU=0 Radius=1.5 StartAngle=3.14159 EndAngle=6.28319
    g11: ArcOfCircle CenterX=-28.2 CenterY=-33.9 CenterZ=0 NormalX=0 NormalY=0 NormalZ=1 AngleXU=0 Radius=1.5 StartAngle=3.14159 EndAngle=6.28319
    g12: LineSegment StartX=-35.7 StartY=-10.5 StartZ=0 EndX=-35.7 EndY=-27.7 EndZ=0
    g13: LineSegment StartX=-32.7 StartY=-10.5 StartZ=0 EndX=-32.7 EndY=-27.7 EndZ=0
    g14: LineSegment StartX=-29.7 StartY=-33.9 StartZ=0 EndX=-29.7 EndY=-4.3 EndZ=0
    g15: LineSegment StartX=-26.7 StartY=-33.9 StartZ=0 EndX=-26.7 EndY=-4.3 EndZ=0
    g16: LineSegment StartX=-2.5 StartY=-10.5 StartZ=0 EndX=-2.5 EndY=-27.7 EndZ=0
    g17: LineSegment StartX=-8.5 StartY=-4.3 StartZ=0 EndX=-8.5 EndY=-33.9 EndZ=0
    g18: LineSegment StartX=-5.5 StartY=-10.5 StartZ=0 EndX=-5.5 EndY=-27.7 EndZ=0
    g19: LineSegment StartX=-11.5 StartY=-4.3 StartZ=0 EndX=-11.5 EndY=-33.9 EndZ=0
    g20: LineSegment StartX=-14.6 StartY=-1.8 StartZ=0 EndX=-14.6 EndY=-36.4 EndZ=0
    g21: LineSegment StartX=-17.6 StartY=-1.8 StartZ=0 EndX=-17.6 EndY=-36.4 EndZ=0
    g22: LineSegment StartX=-20.6 StartY=-36.4 StartZ=0 EndX=-20.6 EndY=-1.8 EndZ=0
    g23: LineSegment StartX=-23.6 StartY=-1.8 StartZ=0 EndX=-23.6 EndY=-36.4 EndZ=0
  constraints (48):
    c: Block(g0)
    c: Block(g1)
    c: Block(g2)
    c: Block(g3)
    c: Block(g4)
    c: Block(g5)
    c: Block(g6)
    c: Block(g7)
    c: Block(g8)
    c: Block(g9)
    c: Block(g10)
    c: Block(g11)
    c: Coincident(g12,g1)
    c: Coincident(g12,g2)
    c: Vertical(g12)
    c: Coincident(g13,g1)
    c: Coincident(g13,g2)
    c: Vertical(g13)
    c: Coincident(g14,g11)
    c: Coincident(g14,g7)
    c: Vertical(g14)
    c: Coincident(g15,g11)
    c: Coincident(g15,g7)
    c: Vertical(g15)
    c: Coincident(g16,g0)
    c: Coincident(g16,g3)
    c: Vertical(g16)
    c: Coincident(g17,g4)
    c: Coincident(g17,g8)
    c: Vertical(g17)
    c: Coincident(g18,g0)
    c: Coincident(g18,g3)
    c: Vertical(g18)
    c: Coincident(g19,g4)
    c: Coincident(g19,g8)
    c: Vertical(g19)
    c: Coincident(g20,g5)
    c: Coincident(g20,g9)
    c: Vertical(g20)
    c: Coincident(g21,g5)
    c: Coincident(g21,g9)
    c: Vertical(g21)
    c: Coincident(g22,g10)
    c: Coincident(g22,g6)
    c: Vertical(g22)
    c: Coincident(g23,g6)
    c: Coincident(g23,g10)
    c: Vertical(g23)
FEATURE [Part::Extrusion] Extrude038  label="removeToCreateFanGrillHoles001"
  Base = -> Sketch047
  Dir = (0,-1,6e-16)
  DirMode = 2
  FaceMakerClass = Part::FaceMakerBullseye
  LengthFwd = 10
  LengthRev = 0
  Placement = pos=(65.4,44,54.82) rot=(0,0,1;0rad)
  Solid = true
  Symmetric = false
FEATURE [Part::Feature] Wire004
  shape: bbox 11 x 5.2 x 2e-07 mm, 0 faces, 0 solids (baked)
FEATURE [Part::Revolution] Revolve095
  Angle = 360
  Axis = (0,1,0)
  Base = (0,0,0)
  FaceMakerClass = Part::FaceMakerBullseye
  Placement = pos=(30.3,38,19.7) rot=(0,0,1;0rad)
  Solid = true
  Source = -> Wire004
  Symmetric = false
FEATURE [Part::Feature] Wire005
  shape: bbox 11 x 5.2 x 2e-07 mm, 0 faces, 0 solids (baked)
FEATURE [Part::Revolution] Revolve096
  Angle = 360
  Axis = (0,1,0)
  Base = (0,0,0)
  FaceMakerClass = Part::FaceMakerBullseye
  Placement = pos=(30.3,38,51.7) rot=(0,0,1;0rad)
  Solid = true
  Source = -> Wire005
  Symmetric = false
FEATURE [Part::Feature] Wire006
  shape: bbox 11 x 5.2 x 2e-07 mm, 0 faces, 0 solids (baked)
FEATURE [Part::Revolution] Revolve097
  Angle = 360
  Axis = (0,1,0)
  Base = (0,0,0)
  FaceMakerClass = Part::FaceMakerBullseye
  Placement = pos=(62.3,38,51.7) rot=(0,0,1;0rad)
  Solid = true
  Source = -> Wire006
  Symmetric = false
FEATURE [Part::Feature] Wire007
  shape: bbox 11 x 5.2 x 2e-07 mm, 0 faces, 0 solids (baked)
FEATURE [Part::Revolution] Revolve098
  Angle = 360
  Axis = (0,1,0)
  Base = (0,0,0)
  FaceMakerClass = Part::FaceMakerBullseye
  Placement = pos=(62.3,38,19.7) rot=(0,0,1;0rad)
  Solid = true
  Source = -> Wire007
  Symmetric = false
FEATURE [Part::MultiFuse] Fusion067  label="fanScrewHousing002"
  Shapes = -> [Revolve098,Revolve097,Revolve096,Revolve095]
FEATURE [Part::Feature] Face091 .. Face094  x4 (patterned run collapsed; names and placements below)
  shape: bbox 3.5 x 17.8 x 2e-07 mm, 1 faces, 0 solids (baked)
FEATURE [Part::Revolution] Revolve099  label="removeToCreateScrewAndThreadedInsertHole026"
  Angle = 360
  Axis = (0,1,0)
  Base = (0,0,0)
  FaceMakerClass = Part::FaceMakerBullseye
  Placement = pos=(62.3,30.3,19.7) rot=(0,0,1;0rad)
  Solid = false
  Source = -> Face091
  Symmetric = false
FEATURE [Part::Revolution] Revolve100  label="removeToCreateScrewAndThreadedInsertHole027"
  Angle = 360
  Axis = (0,1,0)
  Base = (0,0,0)
  FaceMakerClass = Part::FaceMakerBullseye
  Placement = pos=(62.3,30.3,51.7) rot=(0,0,1;0rad)
  Solid = false
  Source = -> Face092
  Symmetric = false
FEATURE [Part::Revolution] Revolve101  label="removeToCreateScrewAndThreadedInsertHole028"
  Angle = 360
  Axis = (0,1,0)
  Base = (0,0,0)
  FaceMakerClass = Part::FaceMakerBullseye
  Placement = pos=(30.3,30.3,19.7) rot=(0,0,1;0rad)
  Solid = false
  Source = -> Face093
  Symmetric = false
FEATURE [Part::Revolution] Revolve102  label="removeToCreateScrewAndThreadedInsertHole029"
  Angle = 360
  Axis = (0,1,0)
  Base = (0,0,0)
  FaceMakerClass = Part::FaceMakerBullseye
  Placement = pos=(30.3,30.3,51.7) rot=(0,0,1;0rad)
  Solid = false
  Source = -> Face094
  Symmetric = false
FEATURE [Part::MultiFuse] Fusion068  label="createThreadedInsertHolesForFan002"
  Shapes = -> [Revolve099,Revolve100,Revolve101,Revolve102]
FEATURE [Part::Cut] Cut026  label="fanScrewHousing003"
  Base = -> Fusion067
  Tool = -> Fusion068
FEATURE [Sketcher::SketchObject] Sketch048
  FullyConstrained = false
  Placement = pos=(0,0,0) rot=(1,0,0;1.5708rad)
  sketch-geometry (24):
    g0: ArcOfCircle CenterX=-4 CenterY=-10.5 CenterZ=0 NormalX=0 NormalY=0 NormalZ=1 AngleXU=0 Radius=1.5 StartAngle=6e-16 EndAngle=3.14159
    g1: ArcOfCircle CenterX=-34.2 CenterY=-10.5 CenterZ=0 NormalX=0 NormalY=0 NormalZ=1 AngleXU=0 Radius=1.5 StartAngle=0 EndAngle=3.14159
    g2: ArcOfCircle CenterX=-34.2 CenterY=-27.7 CenterZ=0 NormalX=0 NormalY=0 NormalZ=1 AngleXU=0 Radius=1.5 StartAngle=3.14159 EndAngle=6.28319
    g3: ArcOfCircle CenterX=-4 CenterY=-27.7 CenterZ=0 NormalX=0 NormalY=0 NormalZ=1 AngleXU=0 Radius=1.5 StartAngle=3.1416 EndAngle=6.28319
    g4: ArcOfCircle CenterX=-10 CenterY=-4.3 CenterZ=0 NormalX=0 NormalY=0 NormalZ=1 AngleXU=0 Radius=1.5 StartAngle=2e-16 EndAngle=3.14159
    g5: ArcOfCircle CenterX=-16.1 CenterY=-1.8 CenterZ=0 NormalX=0 NormalY=0 NormalZ=1 AngleXU=0 Radius=1.5 StartAngle=5e-16 EndAngle=3.14159
    g6: ArcOfCircle CenterX=-22.1 CenterY=-1.8 CenterZ=0 NormalX=0 NormalY=0 NormalZ=1 AngleXU=0 Radius=1.5 StartAngle=5e-16 EndAngle=3.14159
    g7: ArcOfCircle CenterX=-28.2 CenterY=-4.3 CenterZ=0 NormalX=0 NormalY=0 NormalZ=1 AngleXU=0 Radius=1.5 StartAngle=2e-16 EndAngle=3.14159
    g8: ArcOfCircle CenterX=-10 CenterY=-33.9 CenterZ=0 NormalX=0 NormalY=0 NormalZ=1 AngleXU=0 Radius=1.5 StartAngle=3.14159 EndAngle=6.28319
    g9: ArcOfCircle CenterX=-16.1 CenterY=-36.4 CenterZ=0 NormalX=0 NormalY=0 NormalZ=1 AngleXU=0 Radius=1.5 StartAngle=3.14159 EndAngle=6.28319
    g10: ArcOfCircle CenterX=-22.1 CenterY=-36.4 CenterZ=0 NormalX=0 NormalY=0 NormalZ=1 AngleXU=0 Radius=1.5 StartAngle=3.14159 EndAngle=6.28319
    g11: ArcOfCircle CenterX=-28.2 CenterY=-33.9 CenterZ=0 NormalX=0 NormalY=0 NormalZ=1 AngleXU=0 Radius=1.5 StartAngle=3.14159 EndAngle=6.28319
    g12: LineSegment StartX=-35.7 StartY=-10.5 StartZ=0 EndX=-35.7 EndY=-27.7 EndZ=0
    g13: LineSegment StartX=-32.7 StartY=-10.5 StartZ=0 EndX=-32.7 EndY=-27.7 EndZ=0
    g14: LineSegment StartX=-29.7 StartY=-33.9 StartZ=0 EndX=-29.7 EndY=-4.3 EndZ=0
    g15: LineSegment StartX=-26.7 StartY=-33.9 StartZ=0 EndX=-26.7 EndY=-4.3 EndZ=0
    g16: LineSegment StartX=-2.5 StartY=-10.5 StartZ=0 EndX=-2.5 EndY=-27.7 EndZ=0
    g17: LineSegment StartX=-8.5 StartY=-4.3 StartZ=0 EndX=-8.5 EndY=-33.9 EndZ=0
    g18: LineSegment StartX=-5.5 StartY=-10.5 StartZ=0 EndX=-5.5 EndY=-27.7 EndZ=0
    g19: LineSegment StartX=-11.5 StartY=-4.3 StartZ=0 EndX=-11.5 EndY=-33.9 EndZ=0
    g20: LineSegment StartX=-14.6 StartY=-1.8 StartZ=0 EndX=-14.6 EndY=-36.4 EndZ=0
    g21: LineSegment StartX=-17.6 StartY=-1.8 StartZ=0 EndX=-17.6 EndY=-36.4 EndZ=0
    g22: LineSegment StartX=-20.6 StartY=-36.4 StartZ=0 EndX=-20.6 EndY=-1.8 EndZ=0
    g23: LineSegment StartX=-23.6 StartY=-1.8 StartZ=0 EndX=-23.6 EndY=-36.4 EndZ=0
  constraints (48):
    c: Block(g0)
    c: Block(g1)
    c: Block(g2)
    c: Block(g3)
    c: Block(g4)
    c: Block(g5)
    c: Block(g6)
    c: Block(g7)
    c: Block(g8)
    c: Block(g9)
    c: Block(g10)
    c: Block(g11)
    c: Coincident(g12,g1)
    c: Coincident(g12,g2)
    c: Vertical(g12)
    c: Coincident(g13,g1)
    c: Coincident(g13,g2)
    c: Vertical(g13)
    c: Coincident(g14,g11)
    c: Coincident(g14,g7)
    c: Vertical(g14)
    c: Coincident(g15,g11)
    c: Coincident(g15,g7)
    c: Vertical(g15)
    c: Coincident(g16,g0)
    c: Coincident(g16,g3)
    c: Vertical(g16)
    c: Coincident(g17,g4)
    c: Coincident(g17,g8)
    c: Vertical(g17)
    c: Coincident(g18,g0)
    c: Coincident(g18,g3)
    c: Vertical(g18)
    c: Coincident(g19,g4)
    c: Coincident(g19,g8)
    c: Vertical(g19)
    c: Coincident(g20,g5)
    c: Coincident(g20,g9)
    c: Vertical(g20)
    c: Coincident(g21,g5)
    c: Coincident(g21,g9)
    c: Vertical(g21)
    c: Coincident(g22,g10)
    c: Coincident(g22,g6)
    c: Vertical(g22)
    c: Coincident(g23,g6)
    c: Coincident(g23,g10)
    c: Vertical(g23)
FEATURE [Part::Extrusion] Extrude039  label="removeToCreateFanGrillHoles002"
  Base = -> Sketch048
  Dir = (0,-1,6e-16)
  DirMode = 2
  FaceMakerClass = Part::FaceMakerBullseye
  LengthFwd = 10
  LengthRev = 0
  Placement = pos=(65.4,44,54.82) rot=(0,0,1;0rad)
  Solid = true
  Symmetric = false
FEATURE [Part::Cut] Cut027  label="fanScrewHousing004"
  Base = -> Cut026
  Tool = -> Extrude038
FEATURE [Part::Cut] Cut028  label="top014"
  Base = -> Fillet026
  Tool = -> Extrude039
FEATURE [Part::Feature] Face095 .. Face098  x4 (patterned run collapsed; names and placements below)
  shape: bbox 3.5 x 17.8 x 2e-07 mm, 1 faces, 0 solids (baked)
FEATURE [Part::Revolution] Revolve103  label="removeToCreateScrewAndThreadedInsertHole030"
  Angle = 360
  Axis = (0,1,0)
  Base = (0,0,0)
  FaceMakerClass = Part::FaceMakerBullseye
  Placement = pos=(62.3,30.3,19.7) rot=(0,0,1;0rad)
  Solid = false
  Source = -> Face095
  Symmetric = false
FEATURE [Part::Revolution] Revolve104  label="removeToCreateScrewAndThreadedInsertHole031"
  Angle = 360
  Axis = (0,1,0)
  Base = (0,0,0)
  FaceMakerClass = Part::FaceMakerBullseye
  Placement = pos=(62.3,30.3,51.7) rot=(0,0,1;0rad)
  Solid = false
  Source = -> Face096
  Symmetric = false
FEATURE [Part::Revolution] Revolve105  label="removeToCreateScrewAndThreadedInsertHole032"
  Angle = 360
  Axis = (0,1,0)
  Base = (0,0,0)
  FaceMakerClass = Part::FaceMakerBullseye
  Placement = pos=(30.3,30.3,19.7) rot=(0,0,1;0rad)
  Solid = false
  Source = -> Face097
  Symmetric = false
FEATURE [Part::Revolution] Revolve106  label="removeToCreateScrewAndThreadedInsertHole033"
  Angle = 360
  Axis = (0,1,0)
  Base = (0,0,0)
  FaceMakerClass = Part::FaceMakerBullseye
  Placement = pos=(30.3,30.3,51.7) rot=(0,0,1;0rad)
  Solid = false
  Source = -> Face098
  Symmetric = false
FEATURE [Part::MultiFuse] Fusion069  label="createThreadedInsertHolesForFan003"
  Shapes = -> [Revolve103,Revolve104,Revolve105,Revolve106]
FEATURE [Part::Cut] Cut029  label="top015"
  Base = -> Cut028
  Tool = -> Fusion054
FEATURE [Part::Cut] Cut030  label="fanScrewHousing005"
  Base = -> Cut027
  Tool = -> Fusion069
FEATURE [Part::Cylinder] Cylinder026  label="removeToCreteHoleForPlugHousing010"
  Angle = 360
  AttacherType = Attacher::AttachEngine3D
  Height = 20
  Placement = pos=(-2,19,36) rot=(0,1,0;1.5708rad)
  Radius = 14.3
FEATURE [Part::Box] Box018  label="removeToCreteHoleForPlugHousing011"
  AttacherType = Attacher::AttachEngine3D
  Height = 28.6
  Length = 10
  Placement = pos=(-2,0,21.7) rot=(0,0,1;0rad)
  Width = 19
FEATURE [Part::Box] Box019  label="wireHolderBottomCaseBit"
  AttacherType = Attacher::AttachEngine3D
  Height = 28
  Length = 3
  Placement = pos=(0,0,22) rot=(0,0,1;0rad)
  Width = 21
FEATURE [Part::Cylinder] Cylinder027  label="removeToCreteHoleForPlugHousing012"
  Angle = 360
  AttacherType = Attacher::AttachEngine3D
  Height = 20
  Placement = pos=(-2,19,36) rot=(0,1,0;1.5708rad)
  Radius = 14.3
FEATURE [Part::Cut] Cut031  label="wireHolderBottomCaseBit001"
  Base = -> Box019
  Tool = -> Cylinder027
FEATURE [Part::MultiFuse] Fusion070  label="removeToCreteHoleForPlugHousing013"
  Shapes = -> [Box018,Cylinder026]
FEATURE [Part::Cut] Cut032  label="top016"
  Base = -> Cut029
  Tool = -> Fusion070
FEATURE [Part::Cylinder] Cylinder028
  Angle = 360
  AttacherType = Attacher::AttachEngine3D
  Height = 20
  Placement = pos=(0,0,36.15) rot=(0,0,1;0rad)
  Radius = 14.3
FEATURE [Part::Cylinder] Cylinder029
  Angle = 360
  AttacherType = Attacher::AttachEngine3D
  Height = 10
  Placement = pos=(0,0,36.15) rot=(0,0,1;0rad)
  Radius = 4
FEATURE [Part::MultiFuse] Fusion071  label="removeToCreteHoleForPlugHousing014"
  Placement = pos=(70,19,36) rot=(0,1,0;1.5708rad)
  Shapes = -> [Cylinder028,Cylinder029]
FEATURE [Sketcher::SketchObject] Sketch049  label="topSketch011"
  FullyConstrained = true
  sketch-geometry (4):
    g0: ArcOfCircle CenterX=105 CenterY=19 CenterZ=0 NormalX=0 NormalY=0 NormalZ=1 AngleXU=0 Radius=20.6155 StartAngle=5.54125 EndAngle=6.28319
    g1: ArcOfCircle CenterX=105 CenterY=19 CenterZ=0 NormalX=0 NormalY=0 NormalZ=1 AngleXU=0 Radius=13 StartAngle=5.54125 EndAngle=6.28319
    g2: LineSegment StartX=118 StartY=19 StartZ=0 EndX=125.616 EndY=19 EndZ=0
    g3: LineSegment StartX=114.583 StartY=10.2157 StartZ=0 EndX=120.197 EndY=5.06982 EndZ=0
  constraints (7):
    c: Block(g0)
    c: Block(g1)
    c: Coincident(g2,g1)
    c: Coincident(g2,g0)
    c: Horizontal(g2)
    c: Coincident(g3,g1)
    c: Coincident(g3,g0)
FEATURE [Part::Box] Box020  label="removeToCreteHoleForPlugHousing015"
  AttacherType = Attacher::AttachEngine3D
  Height = 28.6
  Length = 20
  Placement = pos=(106.15,0,21.7) rot=(0,0,1;0rad)
  Width = 19
FEATURE [Part::MultiFuse] Fusion072  label="removeToCreteHoleForPlugHousing016"
  Shapes = -> [Box020,Fusion071]
FEATURE [Part::Cut] Cut033  label="removeToCreteHoleForPlugHousing017"
  Base = -> Cut032
  Tool = -> Fusion072
FEATURE [Part::Cylinder] Cylinder030
  Angle = 360
  AttacherType = Attacher::AttachEngine3D
  Height = 20
  Placement = pos=(0,0,36.15) rot=(0,0,1;0rad)
  Radius = 14.3
FEATURE [Part::Cylinder] Cylinder031
  Angle = 360
  AttacherType = Attacher::AttachEngine3D
  Height = 10
  Placement = pos=(0,0,36.15) rot=(0,0,1;0rad)
  Radius = 4
FEATURE [Part::Box] Box021  label="removeToCreteHoleForPlugHousing019"
  AttacherType = Attacher::AttachEngine3D
  Height = 28.6
  Length = 20
  Placement = pos=(106.15,0,21.7) rot=(0,0,1;0rad)
  Width = 19
FEATURE [Part::MultiFuse] Fusion074  label="removeToCreteHoleForPlugHousing020"
  Placement = pos=(70,19,36) rot=(0,1,0;1.5708rad)
  Shapes = -> [Cylinder030,Cylinder031]
FEATURE [Part::MultiFuse] Fusion073  label="removeToCreteHoleForPlugHousing018"
  Placement = pos=(0,0,28.3) rot=(0,0,1;0rad)
  Shapes = -> [Box021,Fusion074]
FEATURE [Part::Cylinder] Cylinder032
  Angle = 360
  AttacherType = Attacher::AttachEngine3D
  Height = 20
  Placement = pos=(0,0,36.15) rot=(0,0,1;0rad)
  Radius = 14.3
FEATURE [Part::Cylinder] Cylinder033
  Angle = 360
  AttacherType = Attacher::AttachEngine3D
  Height = 10
  Placement = pos=(0,0,36.15) rot=(0,0,1;0rad)
  Radius = 4
FEATURE [Part::Box] Box022  label="removeToCreteHoleForPlugHousing021"
  AttacherType = Attacher::AttachEngine3D
  Height = 28.6
  Length = 20
  Placement = pos=(106.15,0,21.7) rot=(0,0,1;0rad)
  Width = 19
FEATURE [Part::MultiFuse] Fusion076  label="removeToCreteHoleForPlugHousing023"
  Placement = pos=(70,19,36) rot=(0,1,0;1.5708rad)
  Shapes = -> [Cylinder032,Cylinder033]
FEATURE [Part::MultiFuse] Fusion075  label="removeToCreteHoleForPlugHousing022"
  Placement = pos=(0,0,-28.3) rot=(0,0,1;0rad)
  Shapes = -> [Box022,Fusion076]
FEATURE [Part::MultiFuse] Fusion077  label="removeToCreatePlugHousingBottomBit"
  Shapes = -> [Fusion075,Fusion073]
FEATURE [Part::Cylinder] Cylinder034
  Angle = 360
  AttacherType = Attacher::AttachEngine3D
  Height = 20
  Placement = pos=(0,0,36.15) rot=(0,0,1;0rad)
  Radius = 14
FEATURE [Part::Cylinder] Cylinder035
  Angle = 360
  AttacherType = Attacher::AttachEngine3D
  Height = 10
  Placement = pos=(0,0,36.15) rot=(0,0,1;0rad)
  Radius = 4
FEATURE [Part::MultiFuse] Fusion078  label="removeToCreteHoleForPlugHousing024"
  Placement = pos=(70,19,36) rot=(0,1,0;1.5708rad)
  Shapes = -> [Cylinder034,Cylinder035]
FEATURE [Part::MultiFuse] Fusion079  label="removeToCreatePlugHousingBottomBit001"
  Shapes = -> [Fusion078,Fusion077]
FEATURE [Part::Extrusion] Extrude040  label="bottomPlugHousingBit"
  Base = -> Sketch049
  Dir = (0,0,1)
  DirMode = 2
  FaceMakerClass = Part::FaceMakerBullseye
  LengthFwd = 72
  LengthRev = 0
  Solid = true
  Symmetric = false
FEATURE [Part::Cut] Cut034  label="bottomPlugHousingBit001"
  Base = -> Extrude040
  Placement = pos=(-0.09,0,0) rot=(0,0,1;0rad)
  Tool = -> Fusion079
FEATURE [Part::Box] Box023  label="Cube014"
  AttacherType = Attacher::AttachEngine3D
  Height = 16
  Length = 8
  Placement = pos=(12.7,31.52,28) rot=(0,0,1;0rad)
  Width = 4
FEATURE [Part::Cylinder] Cylinder036
  Angle = 360
  AttacherType = Attacher::AttachEngine3D
  Height = 10
  Placement = pos=(0,0,36.15) rot=(0,0,1;0rad)
  Radius = 4
FEATURE [Part::Cylinder] Cylinder037
  Angle = 360
  AttacherType = Attacher::AttachEngine3D
  Height = 20
  Placement = pos=(0,0,36.15) rot=(0,0,1;0rad)
  Radius = 8.2
FEATURE [Part::MultiFuse] Fusion080  label="removeToCreteHoleForPlugHousing025"
  Placement = pos=(-42,19,36) rot=(0,1,0;1.5708rad)
  Shapes = -> [Cylinder037,Cylinder036]
FEATURE [Sketcher::SketchObject] Sketch050  label="topSketch012"
  FullyConstrained = true
  sketch-geometry (4):
    g0: LineSegment StartX=16.8446 StartY=31.512 StartZ=0 EndX=16.3251 EndY=34.4666 EndZ=0
    g1: ArcOfCircle CenterX=19 CenterY=19.2524 CenterZ=0 NormalX=0 NormalY=0 NormalZ=1 AngleXU=0 Radius=15.4476 StartAngle=1.74483 EndAngle=2.72717
    g2: ArcOfCircle CenterX=19 CenterY=19.2524 CenterZ=0 NormalX=0 NormalY=0 NormalZ=1 AngleXU=0 Radius=12.4476 StartAngle=1.74483 EndAngle=2.73189
    g3: LineSegment StartX=4.86004 StartY=25.4725 StartZ=0 EndX=7.58253 EndY=24.2107 EndZ=0
  constraints (7):
    c: Block(g0)
    c: Coincident(g1,g0)
    c: Coincident(g2,g0)
    c: Coincident(g3,g1)
    c: Coincident(g3,g2)
    c: Block(g1)
    c: Block(g2)
FEATURE [Part::Extrusion] Extrude041
  Base = -> Sketch050
  Dir = (0,0,1)
  DirMode = 2
  FaceMakerClass = Part::FaceMakerBullseye
  LengthFwd = 10.6
  LengthRev = 0
  Placement = pos=(0,0,31) rot=(0,0,1;0rad)
  Solid = true
  Symmetric = false
FEATURE [Part::Cut] Cut035
  Base = -> Extrude041
  Placement = pos=(0,0,-0.3) rot=(0,0,1;0rad)
  Tool = -> Fusion080
FEATURE [Part::Cut] Cut036
  Base = -> Box023
  Tool = -> Cut035
FEATURE [Part::Fillet] Fillet027
  Base = -> Cut036
  Edges = 1 edges r=0.7: [Edge13]
FEATURE [Part::Fillet] Fillet028
  Base = -> Fillet027
  Edges = 1 edges r=0.7: [Edge13]
FEATURE [Part::Fillet] Fillet029
  Base = -> Fillet028
  Edges = 1 edges r=0.7: [Edge16]
FEATURE [Part::Fillet] Fillet030
  Base = -> Fillet029
  Edges = 1 edges r=0.7: [Edge11]
FEATURE [Part::Fillet] Fillet031
  Base = -> Fillet030
  Edges = 1 edges r=0.7: [Edge10]
FEATURE [Part::Fillet] Fillet032
  Base = -> Fillet031
  Edges = 1 edges r=1.2: [Edge5]
FEATURE [Part::Fillet] Fillet033
  Base = -> Fillet032
  Edges = 1 edges r=1.2: [Edge12]
FEATURE [Part::Fillet] Fillet034  label="wireHousingRetainer"
  Base = -> Fillet033
  Edges = 1 edges r=2: [Edge1]
  Placement = pos=(0.3,0,0) rot=(0,0,1;0rad)
FEATURE [Part::Feature] Face099
  shape: bbox 3.5 x 17.8 x 2e-07 mm, 1 faces, 0 solids (baked)
FEATURE [Part::Revolution] Revolve107  label="removeToCreateScrewAndThreadedInsertHole034"
  Angle = 360
  Axis = (0,1,0)
  Base = (0,0,0)
  FaceMakerClass = Part::FaceMakerBullseye
  Placement = pos=(12.5,0,10) rot=(0,0,1;0rad)
  Solid = false
  Source = -> Face099
  Symmetric = false
FEATURE [Part::Feature] Face100
  shape: bbox 3.5 x 17.8 x 2e-07 mm, 1 faces, 0 solids (baked)
FEATURE [Part::Revolution] Revolve108  label="removeToCreateScrewAndThreadedInsertHole035"
  Angle = 360
  Axis = (0,1,0)
  Base = (0,0,0)
  FaceMakerClass = Part::FaceMakerBullseye
  Placement = pos=(12.5,0,62) rot=(0,0,1;0rad)
  Solid = false
  Source = -> Face100
  Symmetric = false
FEATURE [Part::Feature] Face101
  shape: bbox 3.5 x 17.8 x 2e-07 mm, 1 faces, 0 solids (baked)
FEATURE [Part::Revolution] Revolve109  label="removeToCreateScrewAndThreadedInsertHole036"
  Angle = 360
  Axis = (0,1,0)
  Base = (0,0,0)
  FaceMakerClass = Part::FaceMakerBullseye
  Placement = pos=(89.5,0,68.5) rot=(0,0,1;0rad)
  Solid = false
  Source = -> Face101
  Symmetric = false
FEATURE [Part::Feature] Face102
  shape: bbox 3.5 x 17.8 x 2e-07 mm, 1 faces, 0 solids (baked)
FEATURE [Part::Revolution] Revolve110  label="removeToCreateScrewAndThreadedInsertHole037"
  Angle = 360
  Axis = (0,1,0)
  Base = (0,0,0)
  FaceMakerClass = Part::FaceMakerBullseye
  Placement = pos=(89.5,0,3.5) rot=(0,0,1;0rad)
  Solid = false
  Source = -> Face102
  Symmetric = false
FEATURE [Part::Feature] Face103
  shape: bbox 3.5 x 17.8 x 2e-07 mm, 1 faces, 0 solids (baked)
FEATURE [Part::Revolution] Revolve111  label="removeToCreateScrewAndThreadedInsertHole038"
  Angle = 360
  Axis = (0,1,0)
  Base = (0,0,0)
  FaceMakerClass = Part::FaceMakerBullseye
  Placement = pos=(109.5,4.7,3.5) rot=(0,0,1;0rad)
  Solid = false
  Source = -> Face103
  Symmetric = false
FEATURE [Part::Feature] Face104
  shape: bbox 3.5 x 17.8 x 2e-07 mm, 1 faces, 0 solids (baked)
FEATURE [Part::Revolution] Revolve112  label="removeToCreateScrewAndThreadedInsertHole039"
  Angle = 360
  Axis = (0,1,0)
  Base = (0,0,0)
  FaceMakerClass = Part::FaceMakerBullseye
  Placement = pos=(109.5,4.7,68.5) rot=(0,0,1;0rad)
  Solid = false
  Source = -> Face104
  Symmetric = false
FEATURE [Part::MultiFuse] Fusion081  label="removeToCreateScrewAndThreadedInsertHole040"
  Shapes = -> [Revolve107,Revolve108,Revolve109,Revolve110,Revolve111,Revolve112]
FEATURE [Part::MultiFuse] Fusion082  label="casePillars002"
  Shapes = -> [Revolve094,Revolve092,Revolve090,Revolve089,Revolve091,Revolve093]
FEATURE [Part::Cut] Cut037  label="casePillars003"
  Base = -> Fusion082
  Tool = -> Fusion081
FEATURE [Sketcher::SketchObject] Sketch051
  FullyConstrained = true
  Placement = pos=(117,19,0) rot=(0.57735,0.57735,0.57735;2.0944rad)
  sketch-geometry (48):
    g0: LineSegment StartX=-49.19 StartY=69.25 StartZ=0 EndX=-49.19 EndY=66.25 EndZ=0
    g1: LineSegment StartX=-49.19 StartY=63.5 StartZ=0 EndX=-49.19 EndY=60.5 EndZ=0
    g2: LineSegment StartX=-49.19 StartY=57.75 StartZ=0 EndX=-49.19 EndY=54.75 EndZ=0
    g3: LineSegment StartX=-49.19 StartY=52 StartZ=0 EndX=-49.19 EndY=49 EndZ=0
    g4: LineSegment StartX=-49.19 StartY=46.25 StartZ=0 EndX=-49.19 EndY=43.25 EndZ=0
    g5: LineSegment StartX=-49.19 StartY=40.5 StartZ=0 EndX=-49.19 EndY=37.5 EndZ=0
    g6: LineSegment StartX=-49.19 StartY=34.5 StartZ=0 EndX=-49.19 EndY=31.5 EndZ=0
    g7: LineSegment StartX=-49.19 StartY=28.75 StartZ=0 EndX=-49.19 EndY=25.75 EndZ=0
    g8: LineSegment StartX=-49.19 StartY=23 StartZ=0 EndX=-49.19 EndY=20 EndZ=0
    g9: LineSegment StartX=-49.19 StartY=17.25 StartZ=0 EndX=-49.19 EndY=14.25 EndZ=0
    g10: LineSegment StartX=-49.19 StartY=11.5 StartZ=0 EndX=-49.19 EndY=8.5 EndZ=0
    g11: LineSegment StartX=-49.19 StartY=5.75 StartZ=0 EndX=-49.19 EndY=2.75 EndZ=0
    g12: ArcOfCircle CenterX=-1.5 CenterY=67.75 CenterZ=0 NormalX=0 NormalY=0 NormalZ=1 AngleXU=0 Radius=1.5 StartAngle=4.71239 EndAngle=7.85398
    g13: ArcOfCircle CenterX=-1.5 CenterY=62 CenterZ=0 NormalX=0 NormalY=0 NormalZ=1 AngleXU=0 Radius=1.5 StartAngle=4.71239 EndAngle=7.85398
    g14: ArcOfCircle CenterX=-1.5 CenterY=56.25 CenterZ=0 NormalX=0 NormalY=0 NormalZ=1 AngleXU=0 Radius=1.5 StartAngle=4.71239 EndAngle=7.85398
    g15: ArcOfCircle CenterX=-11.49 CenterY=50.5 CenterZ=0 NormalX=0 NormalY=0 NormalZ=1 AngleXU=0 Radius=1.5 StartAngle=4.71239 EndAngle=7.85398
    g16: ArcOfCircle CenterX=-16.28 CenterY=44.75 CenterZ=0 NormalX=0 NormalY=0 NormalZ=1 AngleXU=0 Radius=1.5 StartAngle=4.71239 EndAngle=7.85398
    g17: ArcOfCircle CenterX=-18.2337 CenterY=39 CenterZ=0 NormalX=0 NormalY=0 NormalZ=1 AngleXU=0 Radius=1.5 StartAngle=4.71485 EndAngle=7.85398
    g18: ArcOfCircle CenterX=-16.2837 CenterY=27.25 CenterZ=0 NormalX=0 NormalY=0 NormalZ=1 AngleXU=0 Radius=1.5 StartAngle=4.71485 EndAngle=7.85398
    g19: ArcOfCircle CenterX=-18.2337 CenterY=33 CenterZ=0 NormalX=0 NormalY=0 NormalZ=1 AngleXU=0 Radius=1.5 StartAngle=4.71485 EndAngle=7.85398
    g20: ArcOfCircle CenterX=-11.49 CenterY=21.5 CenterZ=0 NormalX=0 NormalY=0 NormalZ=1 AngleXU=0 Radius=1.5 StartAngle=4.71239 EndAngle=7.85398
    g21: ArcOfCircle CenterX=-1.5 CenterY=4.25 CenterZ=0 NormalX=0 NormalY=0 NormalZ=1 AngleXU=0 Radius=1.5 StartAngle=4.71239 EndAngle=7.85398
    g22: ArcOfCircle CenterX=-1.5 CenterY=10 CenterZ=0 NormalX=0 NormalY=0 NormalZ=1 AngleXU=0 Radius=1.5 StartAngle=4.71239 EndAngle=7.85398
    g23: ArcOfCircle CenterX=-1.5 CenterY=15.75 CenterZ=0 NormalX=0 NormalY=0 NormalZ=1 AngleXU=0 Radius=1.5 StartAngle=4.71239 EndAngle=7.85398
    g24: LineSegment StartX=-49.19 StartY=69.25 StartZ=0 EndX=-1.5 EndY=69.25 EndZ=0
    g25: LineSegment StartX=-49.19 StartY=66.25 StartZ=0 EndX=-1.5 EndY=66.25 EndZ=0
    g26: LineSegment StartX=-49.19 StartY=63.5 StartZ=0 EndX=-1.5 EndY=63.5 EndZ=0
    g27: LineSegment StartX=-49.19 StartY=60.5 StartZ=0 EndX=-1.5 EndY=60.5 EndZ=0
    g28: LineSegment StartX=-49.19 StartY=57.75 StartZ=0 EndX=-1.5 EndY=57.75 EndZ=0
    g29: LineSegment StartX=-49.19 StartY=54.75 StartZ=0 EndX=-1.5 EndY=54.75 EndZ=0
    g30: LineSegment StartX=-49.19 StartY=52 StartZ=0 EndX=-11.49 EndY=52 EndZ=0
    g31: LineSegment StartX=-49.19 StartY=49 StartZ=0 EndX=-11.49 EndY=49 EndZ=0
    g32: LineSegment StartX=-49.19 StartY=46.25 StartZ=0 EndX=-16.28 EndY=46.25 EndZ=0
    g33: LineSegment StartX=-49.19 StartY=43.25 StartZ=0 EndX=-16.28 EndY=43.25 EndZ=0
    g34: LineSegment StartX=-49.19 StartY=40.5 StartZ=0 EndX=-18.2337 EndY=40.5 EndZ=0
    g35: LineSegment StartX=-49.19 StartY=37.5 StartZ=0 EndX=-18.23 EndY=37.5 EndZ=0
    g36: LineSegment StartX=-49.19 StartY=34.5 StartZ=0 EndX=-18.2337 EndY=34.5 EndZ=0
    g37: LineSegment StartX=-49.19 StartY=31.5 StartZ=0 EndX=-18.23 EndY=31.5 EndZ=0
    g38: LineSegment StartX=-49.19 StartY=28.75 StartZ=0 EndX=-16.2837 EndY=28.75 EndZ=0
    g39: LineSegment StartX=-49.19 StartY=25.75 StartZ=0 EndX=-16.28 EndY=25.75 EndZ=0
    g40: LineSegment StartX=-49.19 StartY=23 StartZ=0 EndX=-11.49 EndY=23 EndZ=0
    g41: LineSegment StartX=-49.19 StartY=20 StartZ=0 EndX=-11.49 EndY=20 EndZ=0
    g42: LineSegment StartX=-49.19 StartY=17.25 StartZ=0 EndX=-1.5 EndY=17.25 EndZ=0
    g43: LineSegment StartX=-49.19 StartY=14.25 StartZ=0 EndX=-1.5 EndY=14.25 EndZ=0
    g44: LineSegment StartX=-49.19 StartY=11.5 StartZ=0 EndX=-1.5 EndY=11.5 EndZ=0
    g45: LineSegment StartX=-49.19 StartY=8.5 StartZ=0 EndX=-1.5 EndY=8.5 EndZ=0
    g46: LineSegment StartX=-49.19 StartY=5.75 StartZ=0 EndX=-1.5 EndY=5.75 EndZ=0
    g47: LineSegment StartX=-49.19 StartY=2.75 StartZ=0 EndX=-1.5 EndY=2.75 EndZ=0
  constraints (120):
    c: Vertical(g0)
    c: Distance(g0) = 3
    c: Block(g0)
    c: Vertical(g1)
    c: Distance(g1) = 3
    c: Vertical(g2)
    c: Equal(g0,g2) = 3
    c: Block(g2)
    c: Vertical(g3)
    c: Equal(g1,g3) = 3
    c: Vertical(g4)
    c: Equal(g0,g4) = 3
    c: Block(g4)
    c: Vertical(g5)
    c: Equal(g1,g5) = 3
    c: Vertical(g6)
    c: Equal(g0,g6) = 3
    c: Block(g6)
    c: Vertical(g7)
    c: Equal(g1,g7) = 3
    c: Vertical(g8)
    c: Equal(g0,g8) = 3
    c: Block(g8)
    c: Vertical(g9)
    c: Equal(g1,g9) = 3
    c: Vertical(g10)
    c: Equal(g0,g10) = 3
    c: Block(g10)
    c: Vertical(g11)
    c: Equal(g1,g11) = 3
    c: Block(g12)
    c: Block(g13)
    c: Block(g14)
    c: Block(g15)
    c: Block(g16)
    c: Block(g17)
    c: Block(g18)
    c: Block(g19)
    c: Block(g20)
    c: Block(g21)
    c: Block(g22)
    c: Block(g23)
    c: Block(g11)
    c: Block(g9)
    c: Block(g7)
    c: Block(g5)
    c: Block(g3)
    c: Block(g1)
    c: Coincident(g24,g0)
    c: Coincident(g24,g12)
    c: Horizontal(g24)
    c: Coincident(g25,g0)
    c: Coincident(g25,g12)
    c: Horizontal(g25)
    c: Coincident(g26,g1)
    c: Coincident(g26,g13)
    c: Horizontal(g26)
    c: Coincident(g27,g1)
    c: Coincident(g27,g13)
    c: Horizontal(g27)
    c: Coincident(g28,g2)
    c: Coincident(g28,g14)
    c: Horizontal(g28)
    c: Coincident(g29,g2)
    c: Coincident(g29,g14)
    c: Horizontal(g29)
    c: Coincident(g30,g3)
    c: Coincident(g30,g15)
    c: Horizontal(g30)
    c: Coincident(g31,g3)
    c: Coincident(g31,g15)
    c: Horizontal(g31)
    c: Coincident(g32,g4)
    c: Coincident(g32,g16)
    c: Horizontal(g32)
    c: Coincident(g33,g4)
    c: Coincident(g33,g16)
    c: Horizontal(g33)
    c: Coincident(g34,g5)
    c: Coincident(g34,g17)
    c: Horizontal(g34)
    c: Coincident(g35,g5)
    c: Coincident(g35,g17)
    c: Horizontal(g35)
    c: Coincident(g36,g6)
    c: Coincident(g36,g19)
    c: Horizontal(g36)
    c: Coincident(g37,g6)
    c: Coincident(g37,g19)
    c: Horizontal(g37)
    c: Coincident(g38,g7)
    c: Coincident(g38,g18)
    c: Horizontal(g38)
    c: Coincident(g39,g7)
    c: Coincident(g39,g18)
    c: Horizontal(g39)
    c: Coincident(g40,g8)
    c: Coincident(g40,g20)
    c: Horizontal(g40)
    c: Coincident(g41,g8)
    c: Coincident(g41,g20)
    c: Horizontal(g41)
    c: Coincident(g42,g9)
    c: Coincident(g42,g23)
    c: Horizontal(g42)
    c: Coincident(g43,g9)
    c: Coincident(g43,g23)
    c: Horizontal(g43)
    c: Coincident(g44,g10)
    c: Coincident(g44,g22)
    c: Horizontal(g44)
    c: Coincident(g45,g10)
    c: Coincident(g45,g22)
    c: Horizontal(g45)
    c: Coincident(g46,g11)
    c: Coincident(g46,g21)
    c: Horizontal(g46)
    c: Coincident(g47,g11)
    c: Coincident(g47,g21)
    c: Horizontal(g47)
FEATURE [Part::Extrusion] Extrude042
  Base = -> Sketch051
  Dir = (1,-2e-16,2e-16)
  DirMode = 2
  FaceMakerClass = Part::FaceMakerBullseye
  LengthFwd = 19
  LengthRev = 0
  Placement = pos=(-19,0,0) rot=(0,0,1;0rad)
  Solid = true
  Symmetric = false
FEATURE [Part::Fillet] Fillet035  label="removeToCreateVentalationHoles"
  Base = -> Extrude042
  Edges = <same value as first occurrence — deduplicated (x6 in doc)>
  Placement = pos=(7,0,0) rot=(0,0,1;0rad)
FEATURE [Part::Cut] Cut038  label="top017"
  Base = -> Cut033
  Tool = -> Fillet035
FEATURE [Sketcher::SketchObject] Sketch052  label="bottomSketch001"
  FullyConstrained = true
  sketch-geometry (45):
    g0: LineSegment StartX=6.29999 StartY=8 StartZ=0 EndX=3.29999 EndY=8 EndZ=0
    g1: LineSegment StartX=3.29999 StartY=8 StartZ=0 EndX=3.29999 EndY=-6.03275e-07 EndZ=0
    g2: ArcOfCircle CenterX=8.29999 CenterY=5 CenterZ=0 NormalX=0 NormalY=0 NormalZ=1 AngleXU=0 Radius=2 StartAngle=3.14159 EndAngle=4.71239
    g3: LineSegment StartX=6.29999 StartY=8 StartZ=0 EndX=6.29999 EndY=5 EndZ=0
    g4: ArcOfCircle CenterX=105 CenterY=19 CenterZ=0 NormalX=0 NormalY=0 NormalZ=1 AngleXU=0 Radius=12.7 StartAngle=4.71239 EndAngle=5.94289
    g5-g11: Circle x7 (B-spline internal-alignment scaffolding for g12; pole/knot coordinates omitted)
    g12: BSplineCurve PolesCount=7 KnotsCount=5 Degree=3 IsPeriodic=0
    g13-g17: GeomPoint x5 (B-spline internal-alignment scaffolding for g12; pole/knot coordinates omitted)
    g18: ArcOfCircle CenterX=105 CenterY=19 CenterZ=0 NormalX=0 NormalY=0 NormalZ=1 AngleXU=0 Radius=15.7 StartAngle=5.81226 EndAngle=6.28319
    g19: BSplineCurve PolesCount=5 KnotsCount=3 Degree=3 IsPeriodic=0
    g20: LineSegment StartX=8.29999 StartY=3 StartZ=0 EndX=101.7 EndY=3 EndZ=0
    g21: LineSegment StartX=3.29999 StartY=-6.03275e-07 StartZ=0 EndX=105 EndY=-6.03275e-07 EndZ=0
    g22: LineSegment StartX=120.974 StartY=8.71251 StartZ=0 EndX=122.332 EndY=7.83778 EndZ=0
    g23: LineSegment StartX=105 StartY=-6.03274e-07 StartZ=0 EndX=113 EndY=-6.03274e-07 EndZ=0
    g24: ArcOfCircle CenterX=105 CenterY=19 CenterZ=0 NormalX=0 NormalY=0 NormalZ=1 AngleXU=0 Radius=20.6155 StartAngle=5.11091 EndAngle=5.71103
    g25: ArcOfCircle CenterX=117.7 CenterY=19 CenterZ=0 NormalX=0 NormalY=0 NormalZ=1 AngleXU=0 Radius=3 StartAngle=1.2e-15 EndAngle=2.10468
    g26: Circle CenterX=116.345 CenterY=16.3232 CenterZ=0 NormalX=0 NormalY=0 NormalZ=1 AngleXU=0 Radius=1
    g27: Circle CenterX=117.24 CenterY=15.7584 CenterZ=0 NormalX=0 NormalY=0 NormalZ=1 AngleXU=0 Radius=1
    g28: Circle CenterX=116.972 CenterY=14.7612 CenterZ=0 NormalX=0 NormalY=0 NormalZ=1 AngleXU=0 Radius=1
    g29: BSplineCurve PolesCount=3 KnotsCount=2 Degree=2 IsPeriodic=0
    g30: GeomPoint X=116.345 Y=16.3232 Z=0
    g31: GeomPoint X=116.972 Y=14.7612 Z=0
    g32: Circle CenterX=115.828 CenterY=17.157 CenterZ=0 NormalX=0 NormalY=0 NormalZ=1 AngleXU=0 Radius=1
    g33: Circle CenterX=115.841 CenterY=16.639 CenterZ=0 NormalX=0 NormalY=0 NormalZ=1 AngleXU=0 Radius=1
    g34: Circle CenterX=116.345 CenterY=16.3232 CenterZ=0 NormalX=0 NormalY=0 NormalZ=1 AngleXU=0 Radius=1
    g35: BSplineCurve PolesCount=3 KnotsCount=2 Degree=2 IsPeriodic=0
    g36: GeomPoint X=115.828 Y=17.157 Z=0
    g37: GeomPoint X=116.345 Y=16.3232 Z=0
    g38: LineSegment StartX=115.828 StartY=17.157 StartZ=0 EndX=115.828 EndY=20.8307 EndZ=0
    g39: Circle CenterX=115.828 CenterY=20.8307 CenterZ=0 NormalX=0 NormalY=0 NormalZ=1 AngleXU=0 Radius=1
    g40: Circle CenterX=115.831 CenterY=21.3396 CenterZ=0 NormalX=0 NormalY=0 NormalZ=1 AngleXU=0 Radius=1
    g41: Circle CenterX=116.173 CenterY=21.5825 CenterZ=0 NormalX=0 NormalY=0 NormalZ=1 AngleXU=0 Radius=1
    g42: BSplineCurve PolesCount=3 KnotsCount=2 Degree=2 IsPeriodic=0
    g43: GeomPoint X=115.828 Y=20.8307 Z=0
    g44: GeomPoint X=116.173 Y=21.5825 Z=0
  constraints (70):
    c: Horizontal(g0)
    c: Distance(g0) = 3
    c: Coincident(g1,g0)
    c: Vertical(g1)
    c: Block(g2)
    c: Block(g0)
    c: Coincident(g3,g0)
    c: Coincident(g3,g2)
    c: Vertical(g3)
    c: Block(g1)
    c: Block(g4)
    c: Coincident(g19,g4)
    c: Block(g19)
    c: Equal(g5, g6-g11) x6
    c: InternalAlignment(g5-g11 -> g12) x7
    c: InternalAlignment(g13-g17 -> g12) x5
    c: Block(g12)
    c: Coincident(g18,g12)
    c: Block(g18)
    c: Coincident(g20,g2)
    c: Coincident(g20,g19)
    c: Horizontal(g20)
    c: Distance(g20) = 93.4
    c: Coincident(g21,g1)
    c: Horizontal(g21)
    c: Distance(g21) = 101.7
    c: Horizontal(g23)
    c: Distance(g23) = 8
    c: Coincident(g24,g23)
    c: Block(g23)
    c: Coincident(g22,g24)
    c: Block(g24)
    c: Block(g22)
    c: Distance(g22) = 1.61553
    c: Coincident(g25,g18)
    c: Block(g25)
    c: Weight(g26) = 1
    c: Equal(g26,g27)
    c: Equal(g26,g28)
    c: Coincident(g29,g4)
    c: InternalAlignment(g26,g29)
    c: InternalAlignment(g27,g29)
    c: InternalAlignment(g28,g29)
    c: InternalAlignment(g30,g29)
    c: InternalAlignment(g31,g29)
    c: Block(g29)
    c: Weight(g32) = 1
    c: Equal(g32,g33)
    c: Equal(g32,g34)
    c: Coincident(g35,g29)
    c: InternalAlignment(g32,g35)
    c: InternalAlignment(g33,g35)
    c: InternalAlignment(g34,g35)
    c: InternalAlignment(g36,g35)
    c: InternalAlignment(g37,g35)
    c: Block(g35)
    c: Coincident(g38,g35)
    c: Vertical(g38)
    c: Block(g38)
    c: Coincident(g42,g38)
    c: Weight(g39) = 1
    c: Equal(g39,g40)
    c: Equal(g39,g41)
    c: Coincident(g42,g25)
    c: InternalAlignment(g39,g42)
    c: InternalAlignment(g40,g42)
    c: InternalAlignment(g41,g42)
    c: InternalAlignment(g43,g42)
    c: InternalAlignment(g44,g42)
    c: Block(g42)
FEATURE [Part::Extrusion] Extrude043  label="bottom010"
  Base = -> Sketch052
  Dir = (0,0,1)
  DirMode = 2
  FaceMakerClass = Part::FaceMakerBullseye
  LengthFwd = 71.4
  LengthRev = 0
  Placement = pos=(0,0,0.3) rot=(0,0,1;0rad)
  Solid = true
  Symmetric = false
FEATURE [Sketcher::SketchObject] Sketch053  label="topSketch013"
  FullyConstrained = true
  sketch-geometry (22):
    g0: LineSegment StartX=5.21097e-06 StartY=3 StartZ=0 EndX=5.21097e-06 EndY=19 EndZ=0
    g1: ArcOfCircle CenterX=19 CenterY=19 CenterZ=0 NormalX=0 NormalY=0 NormalZ=1 AngleXU=0 Radius=19 StartAngle=1.5708 EndAngle=3.14159
    g2: ArcOfCircle CenterX=19 CenterY=19 CenterZ=0 NormalX=0 NormalY=0 NormalZ=1 AngleXU=0 Radius=16 StartAngle=1.5708 EndAngle=3.14159
    g3: LineSegment StartX=114 StartY=35 StartZ=0 EndX=19 EndY=35 EndZ=0
    g4: LineSegment StartX=5.21097e-06 StartY=3 StartZ=0 EndX=5.21097e-06 EndY=0 EndZ=0
    g5: LineSegment StartX=3 StartY=0 StartZ=0 EndX=5.21097e-06 EndY=0 EndZ=0
    g6: LineSegment StartX=3 StartY=19 StartZ=0 EndX=3 EndY=0 EndZ=0
    g7: LineSegment StartX=19 StartY=38 StartZ=0 EndX=124 EndY=38 EndZ=0
    g8: Circle CenterX=119 CenterY=35 CenterZ=0 NormalX=0 NormalY=0 NormalZ=1 AngleXU=0 Radius=1
    g9: Circle CenterX=121 CenterY=35 CenterZ=0 NormalX=0 NormalY=0 NormalZ=1 AngleXU=0 Radius=1
    g10: Circle CenterX=121 CenterY=33 CenterZ=0 NormalX=0 NormalY=0 NormalZ=1 AngleXU=0 Radius=1
    g11: BSplineCurve PolesCount=3 KnotsCount=2 Degree=2 IsPeriodic=0
    g12: GeomPoint X=119 Y=35 Z=0
    g13: GeomPoint X=121 Y=33 Z=0
    g14: LineSegment StartX=119 StartY=35 StartZ=0 EndX=114 EndY=35 EndZ=0
    g15: ArcOfCircle CenterX=105 CenterY=19 CenterZ=0 NormalX=0 NormalY=0 NormalZ=1 AngleXU=0 Radius=16 StartAngle=5.60905 EndAngle=6.28319
    g16: LineSegment StartX=121 StartY=33 StartZ=0 EndX=121 EndY=19 EndZ=0
    g17: LineSegment StartX=117.5 StartY=9.01251 StartZ=0 EndX=121.163 EndY=9.0125 EndZ=0
    g18: ArcOfCircle CenterX=105 CenterY=19 CenterZ=0 NormalX=0 NormalY=0 NormalZ=1 AngleXU=0 Radius=20.6155 StartAngle=5.7297 EndAngle=6.28319
    g19: LineSegment StartX=121.163 StartY=9.0125 StartZ=0 EndX=122.538 EndY=8.16329 EndZ=0
    g20: LineSegment StartX=124 StartY=38 StartZ=0 EndX=125.616 EndY=38 EndZ=0
    g21: LineSegment StartX=125.616 StartY=19 StartZ=0 EndX=125.616 EndY=38 EndZ=0
  constraints (50):
    c: Vertical(g0)
    c: Block(g0)
    c: Coincident(g1,g0)
    c: Block(g1)
    c: Coincident(g2,g1)
    c: Block(g2)
    c: Coincident(g3,g2)
    c: Horizontal(g3)
    c: Tangent(g3,g2)
    c: Coincident(g4,g0)
    c: Distance(g4) = 3
    c: Vertical(g4)
    c: Coincident(g5,g4)
    c: Horizontal(g5)
    c: Coincident(g6,g2)
    c: Coincident(g6,g5)
    c: Vertical(g6)
    c: Horizontal(g7)
    c: Distance(g7) = 105
    c: Coincident(g7,g1)
    c: Block(g3)
    c: Weight(g8) = 1
    c: Equal(g8,g9)
    c: Equal(g8,g10)
    c: InternalAlignment(g8,g11)
    c: InternalAlignment(g9,g11)
    c: InternalAlignment(g10,g11)
    c: InternalAlignment(g12,g11)
    c: InternalAlignment(g13,g11)
    c: Block(g11)
    c: Coincident(g14,g11)
    c: Coincident(g14,g3)
    c: Horizontal(g14)
    c: Block(g15)
    c: Coincident(g16,g11)
    c: Coincident(g16,g15)
    c: Vertical(g16)
    c: Distance(g16) = 14
    c: Coincident(g17,g15)
    c: Block(g18)
    c: Coincident(g19,g18)
    c: Coincident(g20,g7)
    c: Horizontal(g20)
    c: Vertical(g21)
    c: Coincident(g20,g21)
    c: Block(g20)
    c: Block(g21)
    c: Block(g19)
    c: Block(g17)
    c: Distance(g20) = 1.61553
FEATURE [Part::Extrusion] Extrude044
  Base = -> Sketch053
  Dir = (0,0,1)
  DirMode = 2
  FaceMakerClass = Part::FaceMakerBullseye
  LengthFwd = 72
  LengthRev = 0
  Solid = true
  Symmetric = false
FEATURE [Part::Fillet] Fillet036  label="top018"
  Base = -> Extrude044
  Edges = 1 edges r=2: [Edge41]
FEATURE [Sketcher::SketchObject] Sketch054
  FullyConstrained = false
  Placement = pos=(0,0,0) rot=(1,0,0;1.5708rad)
  sketch-geometry (24):
    g0: ArcOfCircle CenterX=-4 CenterY=-10.5 CenterZ=0 NormalX=0 NormalY=0 NormalZ=1 AngleXU=0 Radius=1.5 StartAngle=6e-16 EndAngle=3.14159
    g1: ArcOfCircle CenterX=-34.2 CenterY=-10.5 CenterZ=0 NormalX=0 NormalY=0 NormalZ=1 AngleXU=0 Radius=1.5 StartAngle=0 EndAngle=3.14159
    g2: ArcOfCircle CenterX=-34.2 CenterY=-27.7 CenterZ=0 NormalX=0 NormalY=0 NormalZ=1 AngleXU=0 Radius=1.5 StartAngle=3.14159 EndAngle=6.28319
    g3: ArcOfCircle CenterX=-4 CenterY=-27.7 CenterZ=0 NormalX=0 NormalY=0 NormalZ=1 AngleXU=0 Radius=1.5 StartAngle=3.1416 EndAngle=6.28319
    g4: ArcOfCircle CenterX=-10 CenterY=-4.3 CenterZ=0 NormalX=0 NormalY=0 NormalZ=1 AngleXU=0 Radius=1.5 StartAngle=2e-16 EndAngle=3.14159
    g5: ArcOfCircle CenterX=-16.1 CenterY=-1.8 CenterZ=0 NormalX=0 NormalY=0 NormalZ=1 AngleXU=0 Radius=1.5 StartAngle=5e-16 EndAngle=3.14159
    g6: ArcOfCircle CenterX=-22.1 CenterY=-1.8 CenterZ=0 NormalX=0 NormalY=0 NormalZ=1 AngleXU=0 Radius=1.5 StartAngle=5e-16 EndAngle=3.14159
    g7: ArcOfCircle CenterX=-28.2 CenterY=-4.3 CenterZ=0 NormalX=0 NormalY=0 NormalZ=1 AngleXU=0 Radius=1.5 StartAngle=2e-16 EndAngle=3.14159
    g8: ArcOfCircle CenterX=-10 CenterY=-33.9 CenterZ=0 NormalX=0 NormalY=0 NormalZ=1 AngleXU=0 Radius=1.5 StartAngle=3.14159 EndAngle=6.28319
    g9: ArcOfCircle CenterX=-16.1 CenterY=-36.4 CenterZ=0 NormalX=0 NormalY=0 NormalZ=1 AngleXU=0 Radius=1.5 StartAngle=3.14159 EndAngle=6.28319
    g10: ArcOfCircle CenterX=-22.1 CenterY=-36.4 CenterZ=0 NormalX=0 NormalY=0 NormalZ=1 AngleXU=0 Radius=1.5 StartAngle=3.14159 EndAngle=6.28319
    g11: ArcOfCircle CenterX=-28.2 CenterY=-33.9 CenterZ=0 NormalX=0 NormalY=0 NormalZ=1 AngleXU=0 Radius=1.5 StartAngle=3.14159 EndAngle=6.28319
    g12: LineSegment StartX=-35.7 StartY=-10.5 StartZ=0 EndX=-35.7 EndY=-27.7 EndZ=0
    g13: LineSegment StartX=-32.7 StartY=-10.5 StartZ=0 EndX=-32.7 EndY=-27.7 EndZ=0
    g14: LineSegment StartX=-29.7 StartY=-33.9 StartZ=0 EndX=-29.7 EndY=-4.3 EndZ=0
    g15: LineSegment StartX=-26.7 StartY=-33.9 StartZ=0 EndX=-26.7 EndY=-4.3 EndZ=0
    g16: LineSegment StartX=-2.5 StartY=-10.5 StartZ=0 EndX=-2.5 EndY=-27.7 EndZ=0
    g17: LineSegment StartX=-8.5 StartY=-4.3 StartZ=0 EndX=-8.5 EndY=-33.9 EndZ=0
    g18: LineSegment StartX=-5.5 StartY=-10.5 StartZ=0 EndX=-5.5 EndY=-27.7 EndZ=0
    g19: LineSegment StartX=-11.5 StartY=-4.3 StartZ=0 EndX=-11.5 EndY=-33.9 EndZ=0
    g20: LineSegment StartX=-14.6 StartY=-1.8 StartZ=0 EndX=-14.6 EndY=-36.4 EndZ=0
    g21: LineSegment StartX=-17.6 StartY=-1.8 StartZ=0 EndX=-17.6 EndY=-36.4 EndZ=0
    g22: LineSegment StartX=-20.6 StartY=-36.4 StartZ=0 EndX=-20.6 EndY=-1.8 EndZ=0
    g23: LineSegment StartX=-23.6 StartY=-1.8 StartZ=0 EndX=-23.6 EndY=-36.4 EndZ=0
  constraints (48):
    c: Block(g0)
    c: Block(g1)
    c: Block(g2)
    c: Block(g3)
    c: Block(g4)
    c: Block(g5)
    c: Block(g6)
    c: Block(g7)
    c: Block(g8)
    c: Block(g9)
    c: Block(g10)
    c: Block(g11)
    c: Coincident(g12,g1)
    c: Coincident(g12,g2)
    c: Vertical(g12)
    c: Coincident(g13,g1)
    c: Coincident(g13,g2)
    c: Vertical(g13)
    c: Coincident(g14,g11)
    c: Coincident(g14,g7)
    c: Vertical(g14)
    c: Coincident(g15,g11)
    c: Coincident(g15,g7)
    c: Vertical(g15)
    c: Coincident(g16,g0)
    c: Coincident(g16,g3)
    c: Vertical(g16)
    c: Coincident(g17,g4)
    c: Coincident(g17,g8)
    c: Vertical(g17)
    c: Coincident(g18,g0)
    c: Coincident(g18,g3)
    c: Vertical(g18)
    c: Coincident(g19,g4)
    c: Coincident(g19,g8)
    c: Vertical(g19)
    c: Coincident(g20,g5)
    c: Coincident(g20,g9)
    c: Vertical(g20)
    c: Coincident(g21,g5)
    c: Coincident(g21,g9)
    c: Vertical(g21)
    c: Coincident(g22,g10)
    c: Coincident(g22,g6)
    c: Vertical(g22)
    c: Coincident(g23,g6)
    c: Coincident(g23,g10)
    c: Vertical(g23)
FEATURE [Part::Extrusion] Extrude045  label="removeToCreateFanGrillHoles003"
  Base = -> Sketch054
  Dir = (0,-1,6e-16)
  DirMode = 2
  FaceMakerClass = Part::FaceMakerBullseye
  LengthFwd = 10
  LengthRev = 0
  Placement = pos=(65.4,44,54.82) rot=(0,0,1;0rad)
  Solid = true
  Symmetric = false
FEATURE [Part::Feature] Face105 .. Face108  x4 (patterned run collapsed; names and placements below)
  shape: bbox 3.5 x 17.8 x 2e-07 mm, 1 faces, 0 solids (baked)
FEATURE [Part::Revolution] Revolve113  label="removeToCreateScrewAndThreadedInsertHole041"
  Angle = 360
  Axis = (0,1,0)
  Base = (0,0,0)
  FaceMakerClass = Part::FaceMakerBullseye
  Placement = pos=(62.3,30.3,19.7) rot=(0,0,1;0rad)
  Solid = false
  Source = -> Face105
  Symmetric = false
FEATURE [Part::Revolution] Revolve114  label="removeToCreateScrewAndThreadedInsertHole042"
  Angle = 360
  Axis = (0,1,0)
  Base = (0,0,0)
  FaceMakerClass = Part::FaceMakerBullseye
  Placement = pos=(62.3,30.3,51.7) rot=(0,0,1;0rad)
  Solid = false
  Source = -> Face106
  Symmetric = false
FEATURE [Part::Revolution] Revolve115  label="removeToCreateScrewAndThreadedInsertHole043"
  Angle = 360
  Axis = (0,1,0)
  Base = (0,0,0)
  FaceMakerClass = Part::FaceMakerBullseye
  Placement = pos=(30.3,30.3,19.7) rot=(0,0,1;0rad)
  Solid = false
  Source = -> Face107
  Symmetric = false
FEATURE [Part::Revolution] Revolve116  label="removeToCreateScrewAndThreadedInsertHole044"
  Angle = 360
  Axis = (0,1,0)
  Base = (0,0,0)
  FaceMakerClass = Part::FaceMakerBullseye
  Placement = pos=(30.3,30.3,51.7) rot=(0,0,1;0rad)
  Solid = false
  Source = -> Face108
  Symmetric = false
FEATURE [Part::MultiFuse] Fusion083  label="createThreadedInsertHolesForFan004"
  Shapes = -> [Revolve113,Revolve114,Revolve115,Revolve116]
FEATURE [Part::Box] Box024  label="removeToCreteHoleForPlugHousing026"
  AttacherType = Attacher::AttachEngine3D
  Height = 28.6
  Length = 10
  Placement = pos=(-2,0,21.7) rot=(0,0,1;0rad)
  Width = 19
FEATURE [Part::Cylinder] Cylinder038  label="removeToCreteHoleForPlugHousing027"
  Angle = 360
  AttacherType = Attacher::AttachEngine3D
  Height = 20
  Placement = pos=(-2,19,36) rot=(0,1,0;1.5708rad)
  Radius = 14.3
FEATURE [Part::MultiFuse] Fusion084  label="removeToCreteHoleForPlugHousing028"
  Shapes = -> [Box024,Cylinder038]
FEATURE [Part::Cylinder] Cylinder039
  Angle = 360
  AttacherType = Attacher::AttachEngine3D
  Height = 20
  Placement = pos=(0,0,36.15) rot=(0,0,1;0rad)
  Radius = 14.3
FEATURE [Part::Cylinder] Cylinder040
  Angle = 360
  AttacherType = Attacher::AttachEngine3D
  Height = 10
  Placement = pos=(0,0,36.15) rot=(0,0,1;0rad)
  Radius = 4
FEATURE [Part::Box] Box025  label="removeToCreteHoleForPlugHousing030"
  AttacherType = Attacher::AttachEngine3D
  Height = 28.6
  Length = 20
  Placement = pos=(106.15,0,21.7) rot=(0,0,1;0rad)
  Width = 19
FEATURE [Part::MultiFuse] Fusion086  label="removeToCreteHoleForPlugHousing031"
  Placement = pos=(70,19,36) rot=(0,1,0;1.5708rad)
  Shapes = -> [Cylinder039,Cylinder040]
FEATURE [Part::MultiFuse] Fusion085  label="removeToCreteHoleForPlugHousing029"
  Shapes = -> [Box025,Fusion086]
FEATURE [Sketcher::SketchObject] Sketch055
  FullyConstrained = true
  Placement = pos=(117,19,0) rot=(0.57735,0.57735,0.57735;2.0944rad)
  sketch-geometry (48):
    g0: LineSegment StartX=-49.19 StartY=69.25 StartZ=0 EndX=-49.19 EndY=66.25 EndZ=0
    g1: LineSegment StartX=-49.19 StartY=63.5 StartZ=0 EndX=-49.19 EndY=60.5 EndZ=0
    g2: LineSegment StartX=-49.19 StartY=57.75 StartZ=0 EndX=-49.19 EndY=54.75 EndZ=0
    g3: LineSegment StartX=-49.19 StartY=52 StartZ=0 EndX=-49.19 EndY=49 EndZ=0
    g4: LineSegment StartX=-49.19 StartY=46.25 StartZ=0 EndX=-49.19 EndY=43.25 EndZ=0
    g5: LineSegment StartX=-49.19 StartY=40.5 StartZ=0 EndX=-49.19 EndY=37.5 EndZ=0
    g6: LineSegment StartX=-49.19 StartY=34.5 StartZ=0 EndX=-49.19 EndY=31.5 EndZ=0
    g7: LineSegment StartX=-49.19 StartY=28.75 StartZ=0 EndX=-49.19 EndY=25.75 EndZ=0
    g8: LineSegment StartX=-49.19 StartY=23 StartZ=0 EndX=-49.19 EndY=20 EndZ=0
    g9: LineSegment StartX=-49.19 StartY=17.25 StartZ=0 EndX=-49.19 EndY=14.25 EndZ=0
    g10: LineSegment StartX=-49.19 StartY=11.5 StartZ=0 EndX=-49.19 EndY=8.5 EndZ=0
    g11: LineSegment StartX=-49.19 StartY=5.75 StartZ=0 EndX=-49.19 EndY=2.75 EndZ=0
    g12: ArcOfCircle CenterX=-1.5 CenterY=67.75 CenterZ=0 NormalX=0 NormalY=0 NormalZ=1 AngleXU=0 Radius=1.5 StartAngle=4.71239 EndAngle=7.85398
    g13: ArcOfCircle CenterX=-1.5 CenterY=62 CenterZ=0 NormalX=0 NormalY=0 NormalZ=1 AngleXU=0 Radius=1.5 StartAngle=4.71239 EndAngle=7.85398
    g14: ArcOfCircle CenterX=-1.5 CenterY=56.25 CenterZ=0 NormalX=0 NormalY=0 NormalZ=1 AngleXU=0 Radius=1.5 StartAngle=4.71239 EndAngle=7.85398
    g15: ArcOfCircle CenterX=-11.49 CenterY=50.5 CenterZ=0 NormalX=0 NormalY=0 NormalZ=1 AngleXU=0 Radius=1.5 StartAngle=4.71239 EndAngle=7.85398
    g16: ArcOfCircle CenterX=-16.28 CenterY=44.75 CenterZ=0 NormalX=0 NormalY=0 NormalZ=1 AngleXU=0 Radius=1.5 StartAngle=4.71239 EndAngle=7.85398
    g17: ArcOfCircle CenterX=-18.2337 CenterY=39 CenterZ=0 NormalX=0 NormalY=0 NormalZ=1 AngleXU=0 Radius=1.5 StartAngle=4.71485 EndAngle=7.85398
    g18: ArcOfCircle CenterX=-16.2837 CenterY=27.25 CenterZ=0 NormalX=0 NormalY=0 NormalZ=1 AngleXU=0 Radius=1.5 StartAngle=4.71485 EndAngle=7.85398
    g19: ArcOfCircle CenterX=-18.2337 CenterY=33 CenterZ=0 NormalX=0 NormalY=0 NormalZ=1 AngleXU=0 Radius=1.5 StartAngle=4.71485 EndAngle=7.85398
    g20: ArcOfCircle CenterX=-11.49 CenterY=21.5 CenterZ=0 NormalX=0 NormalY=0 NormalZ=1 AngleXU=0 Radius=1.5 StartAngle=4.71239 EndAngle=7.85398
    g21: ArcOfCircle CenterX=-1.5 CenterY=4.25 CenterZ=0 NormalX=0 NormalY=0 NormalZ=1 AngleXU=0 Radius=1.5 StartAngle=4.71239 EndAngle=7.85398
    g22: ArcOfCircle CenterX=-1.5 CenterY=10 CenterZ=0 NormalX=0 NormalY=0 NormalZ=1 AngleXU=0 Radius=1.5 StartAngle=4.71239 EndAngle=7.85398
    g23: ArcOfCircle CenterX=-1.5 CenterY=15.75 CenterZ=0 NormalX=0 NormalY=0 NormalZ=1 AngleXU=0 Radius=1.5 StartAngle=4.71239 EndAngle=7.85398
    g24: LineSegment StartX=-49.19 StartY=69.25 StartZ=0 EndX=-1.5 EndY=69.25 EndZ=0
    g25: LineSegment StartX=-49.19 StartY=66.25 StartZ=0 EndX=-1.5 EndY=66.25 EndZ=0
    g26: LineSegment StartX=-49.19 StartY=63.5 StartZ=0 EndX=-1.5 EndY=63.5 EndZ=0
    g27: LineSegment StartX=-49.19 StartY=60.5 StartZ=0 EndX=-1.5 EndY=60.5 EndZ=0
    g28: LineSegment StartX=-49.19 StartY=57.75 StartZ=0 EndX=-1.5 EndY=57.75 EndZ=0
    g29: LineSegment StartX=-49.19 StartY=54.75 StartZ=0 EndX=-1.5 EndY=54.75 EndZ=0
    g30: LineSegment StartX=-49.19 StartY=52 StartZ=0 EndX=-11.49 EndY=52 EndZ=0
    g31: LineSegment StartX=-49.19 StartY=49 StartZ=0 EndX=-11.49 EndY=49 EndZ=0
    g32: LineSegment StartX=-49.19 StartY=46.25 StartZ=0 EndX=-16.28 EndY=46.25 EndZ=0
    g33: LineSegment StartX=-49.19 StartY=43.25 StartZ=0 EndX=-16.28 EndY=43.25 EndZ=0
    g34: LineSegment StartX=-49.19 StartY=40.5 StartZ=0 EndX=-18.2337 EndY=40.5 EndZ=0
    g35: LineSegment StartX=-49.19 StartY=37.5 StartZ=0 EndX=-18.23 EndY=37.5 EndZ=0
    g36: LineSegment StartX=-49.19 StartY=34.5 StartZ=0 EndX=-18.2337 EndY=34.5 EndZ=0
    g37: LineSegment StartX=-49.19 StartY=31.5 StartZ=0 EndX=-18.23 EndY=31.5 EndZ=0
    g38: LineSegment StartX=-49.19 StartY=28.75 StartZ=0 EndX=-16.2837 EndY=28.75 EndZ=0
    g39: LineSegment StartX=-49.19 StartY=25.75 StartZ=0 EndX=-16.28 EndY=25.75 EndZ=0
    g40: LineSegment StartX=-49.19 StartY=23 StartZ=0 EndX=-11.49 EndY=23 EndZ=0
    g41: LineSegment StartX=-49.19 StartY=20 StartZ=0 EndX=-11.49 EndY=20 EndZ=0
    g42: LineSegment StartX=-49.19 StartY=17.25 StartZ=0 EndX=-1.5 EndY=17.25 EndZ=0
    g43: LineSegment StartX=-49.19 StartY=14.25 StartZ=0 EndX=-1.5 EndY=14.25 EndZ=0
    g44: LineSegment StartX=-49.19 StartY=11.5 StartZ=0 EndX=-1.5 EndY=11.5 EndZ=0
    g45: LineSegment StartX=-49.19 StartY=8.5 StartZ=0 EndX=-1.5 EndY=8.5 EndZ=0
    g46: LineSegment StartX=-49.19 StartY=5.75 StartZ=0 EndX=-1.5 EndY=5.75 EndZ=0
    g47: LineSegment StartX=-49.19 StartY=2.75 StartZ=0 EndX=-1.5 EndY=2.75 EndZ=0
  constraints (120):
    c: Vertical(g0)
    c: Distance(g0) = 3
    c: Block(g0)
    c: Vertical(g1)
    c: Distance(g1) = 3
    c: Vertical(g2)
    c: Equal(g0,g2) = 3
    c: Block(g2)
    c: Vertical(g3)
    c: Equal(g1,g3) = 3
    c: Vertical(g4)
    c: Equal(g0,g4) = 3
    c: Block(g4)
    c: Vertical(g5)
    c: Equal(g1,g5) = 3
    c: Vertical(g6)
    c: Equal(g0,g6) = 3
    c: Block(g6)
    c: Vertical(g7)
    c: Equal(g1,g7) = 3
    c: Vertical(g8)
    c: Equal(g0,g8) = 3
    c: Block(g8)
    c: Vertical(g9)
    c: Equal(g1,g9) = 3
    c: Vertical(g10)
    c: Equal(g0,g10) = 3
    c: Block(g10)
    c: Vertical(g11)
    c: Equal(g1,g11) = 3
    c: Block(g12)
    c: Block(g13)
    c: Block(g14)
    c: Block(g15)
    c: Block(g16)
    c: Block(g17)
    c: Block(g18)
    c: Block(g19)
    c: Block(g20)
    c: Block(g21)
    c: Block(g22)
    c: Block(g23)
    c: Block(g11)
    c: Block(g9)
    c: Block(g7)
    c: Block(g5)
    c: Block(g3)
    c: Block(g1)
    c: Coincident(g24,g0)
    c: Coincident(g24,g12)
    c: Horizontal(g24)
    c: Coincident(g25,g0)
    c: Coincident(g25,g12)
    c: Horizontal(g25)
    c: Coincident(g26,g1)
    c: Coincident(g26,g13)
    c: Horizontal(g26)
    c: Coincident(g27,g1)
    c: Coincident(g27,g13)
    c: Horizontal(g27)
    c: Coincident(g28,g2)
    c: Coincident(g28,g14)
    c: Horizontal(g28)
    c: Coincident(g29,g2)
    c: Coincident(g29,g14)
    c: Horizontal(g29)
    c: Coincident(g30,g3)
    c: Coincident(g30,g15)
    c: Horizontal(g30)
    c: Coincident(g31,g3)
    c: Coincident(g31,g15)
    c: Horizontal(g31)
    c: Coincident(g32,g4)
    c: Coincident(g32,g16)
    c: Horizontal(g32)
    c: Coincident(g33,g4)
    c: Coincident(g33,g16)
    c: Horizontal(g33)
    c: Coincident(g34,g5)
    c: Coincident(g34,g17)
    c: Horizontal(g34)
    c: Coincident(g35,g5)
    c: Coincident(g35,g17)
    c: Horizontal(g35)
    c: Coincident(g36,g6)
    c: Coincident(g36,g19)
    c: Horizontal(g36)
    c: Coincident(g37,g6)
    c: Coincident(g37,g19)
    c: Horizontal(g37)
    c: Coincident(g38,g7)
    c: Coincident(g38,g18)
    c: Horizontal(g38)
    c: Coincident(g39,g7)
    c: Coincident(g39,g18)
    c: Horizontal(g39)
    c: Coincident(g40,g8)
    c: Coincident(g40,g20)
    c: Horizontal(g40)
    c: Coincident(g41,g8)
    c: Coincident(g41,g20)
    c: Horizontal(g41)
    c: Coincident(g42,g9)
    c: Coincident(g42,g23)
    c: Horizontal(g42)
    c: Coincident(g43,g9)
    c: Coincident(g43,g23)
    c: Horizontal(g43)
    c: Coincident(g44,g10)
    c: Coincident(g44,g22)
    c: Horizontal(g44)
    c: Coincident(g45,g10)
    c: Coincident(g45,g22)
    c: Horizontal(g45)
    c: Coincident(g46,g11)
    c: Coincident(g46,g21)
    c: Horizontal(g46)
    c: Coincident(g47,g11)
    c: Coincident(g47,g21)
    c: Horizontal(g47)
FEATURE [Part::Extrusion] Extrude046
  Base = -> Sketch055
  Dir = (1,0,0)
  DirMode = 2
  FaceMakerClass = Part::FaceMakerBullseye
  LengthFwd = 23
  LengthRev = 0
  Placement = pos=(-19,0,0) rot=(0,0,1;0rad)
  Solid = true
  Symmetric = false
FEATURE [Part::Fillet] Fillet038  label="removeToCreateVentalationHoles001"
  Base = -> Extrude046
  Edges = <same value as first occurrence — deduplicated (x6 in doc)>
  Placement = pos=(7,0,0) rot=(0,0,1;0rad)
FEATURE [Sketcher::SketchObject] Sketch056  label="topSketch014"
  FullyConstrained = true
  sketch-geometry (22):
    g0: LineSegment StartX=5.21097e-06 StartY=3 StartZ=0 EndX=5.21097e-06 EndY=19 EndZ=0
    g1: ArcOfCircle CenterX=19 CenterY=19 CenterZ=0 NormalX=0 NormalY=0 NormalZ=1 AngleXU=0 Radius=19 StartAngle=1.5708 EndAngle=3.14159
    g2: ArcOfCircle CenterX=19 CenterY=19 CenterZ=0 NormalX=0 NormalY=0 NormalZ=1 AngleXU=0 Radius=16 StartAngle=1.5708 EndAngle=3.14159
    g3: LineSegment StartX=114 StartY=35 StartZ=0 EndX=19 EndY=35 EndZ=0
    g4: LineSegment StartX=5.21097e-06 StartY=3 StartZ=0 EndX=5.21097e-06 EndY=0 EndZ=0
    g5: LineSegment StartX=3 StartY=0 StartZ=0 EndX=5.21097e-06 EndY=0 EndZ=0
    g6: LineSegment StartX=3 StartY=19 StartZ=0 EndX=3 EndY=0 EndZ=0
    g7: LineSegment StartX=19 StartY=38 StartZ=0 EndX=124 EndY=38 EndZ=0
    g8: Circle CenterX=119 CenterY=35 CenterZ=0 NormalX=0 NormalY=0 NormalZ=1 AngleXU=0 Radius=1
    g9: Circle CenterX=121 CenterY=35 CenterZ=0 NormalX=0 NormalY=0 NormalZ=1 AngleXU=0 Radius=1
    g10: Circle CenterX=121 CenterY=33 CenterZ=0 NormalX=0 NormalY=0 NormalZ=1 AngleXU=0 Radius=1
    g11: BSplineCurve PolesCount=3 KnotsCount=2 Degree=2 IsPeriodic=0
    g12: GeomPoint X=119 Y=35 Z=0
    g13: GeomPoint X=121 Y=33 Z=0
    g14: LineSegment StartX=119 StartY=35 StartZ=0 EndX=114 EndY=35 EndZ=0
    g15: ArcOfCircle CenterX=105 CenterY=19 CenterZ=0 NormalX=0 NormalY=0 NormalZ=1 AngleXU=0 Radius=16 StartAngle=5.60905 EndAngle=6.28319
    g16: LineSegment StartX=121 StartY=33 StartZ=0 EndX=121 EndY=19 EndZ=0
    g17: LineSegment StartX=117.5 StartY=9.01251 StartZ=0 EndX=121.163 EndY=9.0125 EndZ=0
    g18: ArcOfCircle CenterX=105 CenterY=19 CenterZ=0 NormalX=0 NormalY=0 NormalZ=1 AngleXU=0 Radius=20.6155 StartAngle=5.7297 EndAngle=6.28319
    g19: LineSegment StartX=121.163 StartY=9.0125 StartZ=0 EndX=122.538 EndY=8.16329 EndZ=0
    g20: LineSegment StartX=124 StartY=38 StartZ=0 EndX=125.616 EndY=38 EndZ=0
    g21: LineSegment StartX=125.616 StartY=19 StartZ=0 EndX=125.616 EndY=38 EndZ=0
  constraints (49):
    c: Vertical(g0)
    c: Block(g0)
    c: Coincident(g1,g0)
    c: Block(g1)
    c: Coincident(g2,g1)
    c: Block(g2)
    c: Coincident(g3,g2)
    c: Horizontal(g3)
    c: Tangent(g3,g2)
    c: Coincident(g4,g0)
    c: Distance(g4) = 3
    c: Vertical(g4)
    c: Coincident(g5,g4)
    c: Horizontal(g5)
    c: Coincident(g6,g2)
    c: Coincident(g6,g5)
    c: Vertical(g6)
    c: Horizontal(g7)
    c: Distance(g7) = 105
    c: Coincident(g7,g1)
    c: Block(g3)
    c: Weight(g8) = 1
    c: Equal(g8,g9)
    c: Equal(g8,g10)
    c: InternalAlignment(g8,g11)
    c: InternalAlignment(g9,g11)
    c: InternalAlignment(g10,g11)
    c: InternalAlignment(g12,g11)
    c: InternalAlignment(g13,g11)
    c: Block(g11)
    c: Coincident(g14,g11)
    c: Coincident(g14,g3)
    c: Horizontal(g14)
    c: Block(g15)
    c: Coincident(g16,g11)
    c: Coincident(g16,g15)
    c: Vertical(g16)
    c: Distance(g16) = 14
    c: Coincident(g17,g15)
    c: Block(g18)
    c: Coincident(g19,g18)
    c: Coincident(g20,g7)
    c: Horizontal(g20)
    c: Vertical(g21)
    c: Coincident(g20,g21)
    c: Block(g20)
    c: Block(g21)
    c: Block(g19)
    c: Block(g17)
FEATURE [Part::Box] Box026  label="removeToCreteHoleForPlugHousing032"
  AttacherType = Attacher::AttachEngine3D
  Height = 28.6
  Length = 10
  Placement = pos=(-2,0,21.7) rot=(0,0,1;0rad)
  Width = 19
FEATURE [Part::Feature] Face109 .. Face112  x4 (patterned run collapsed; names and placements below)
  shape: bbox 3.5 x 17.8 x 2e-07 mm, 1 faces, 0 solids (baked)
FEATURE [Part::Revolution] Revolve117  label="removeToCreateScrewAndThreadedInsertHole045"
  Angle = 360
  Axis = (0,1,0)
  Base = (0,0,0)
  FaceMakerClass = Part::FaceMakerBullseye
  Placement = pos=(62.3,30.3,19.7) rot=(0,0,1;0rad)
  Solid = false
  Source = -> Face109
  Symmetric = false
FEATURE [Part::Revolution] Revolve118  label="removeToCreateScrewAndThreadedInsertHole046"
  Angle = 360
  Axis = (0,1,0)
  Base = (0,0,0)
  FaceMakerClass = Part::FaceMakerBullseye
  Placement = pos=(62.3,30.3,51.7) rot=(0,0,1;0rad)
  Solid = false
  Source = -> Face110
  Symmetric = false
FEATURE [Part::Revolution] Revolve119  label="removeToCreateScrewAndThreadedInsertHole047"
  Angle = 360
  Axis = (0,1,0)
  Base = (0,0,0)
  FaceMakerClass = Part::FaceMakerBullseye
  Placement = pos=(30.3,30.3,19.7) rot=(0,0,1;0rad)
  Solid = false
  Source = -> Face111
  Symmetric = false
FEATURE [Part::Revolution] Revolve120  label="removeToCreateScrewAndThreadedInsertHole048"
  Angle = 360
  Axis = (0,1,0)
  Base = (0,0,0)
  FaceMakerClass = Part::FaceMakerBullseye
  Placement = pos=(30.3,30.3,51.7) rot=(0,0,1;0rad)
  Solid = false
  Source = -> Face112
  Symmetric = false
FEATURE [Part::MultiFuse] Fusion087  label="createThreadedInsertHolesForFan005"
  Shapes = -> [Revolve117,Revolve118,Revolve119,Revolve120]
FEATURE [Part::Extrusion] Extrude047
  Base = -> Sketch056
  Dir = (0,0,1)
  DirMode = 2
  FaceMakerClass = Part::FaceMakerBullseye
  LengthFwd = 72
  LengthRev = 0
  Solid = true
  Symmetric = false
FEATURE [Part::Fillet] Fillet039  label="top019"
  Base = -> Extrude047
  Edges = 1 edges r=2: [Edge35]
FEATURE [Sketcher::SketchObject] Sketch057
  FullyConstrained = false
  Placement = pos=(0,0,0) rot=(1,0,0;1.5708rad)
  sketch-geometry (24):
    g0: ArcOfCircle CenterX=-4 CenterY=-10.5 CenterZ=0 NormalX=0 NormalY=0 NormalZ=1 AngleXU=0 Radius=1.5 StartAngle=6e-16 EndAngle=3.14159
    g1: ArcOfCircle CenterX=-34.2 CenterY=-10.5 CenterZ=0 NormalX=0 NormalY=0 NormalZ=1 AngleXU=0 Radius=1.5 StartAngle=0 EndAngle=3.14159
    g2: ArcOfCircle CenterX=-34.2 CenterY=-27.7 CenterZ=0 NormalX=0 NormalY=0 NormalZ=1 AngleXU=0 Radius=1.5 StartAngle=3.14159 EndAngle=6.28319
    g3: ArcOfCircle CenterX=-4 CenterY=-27.7 CenterZ=0 NormalX=0 NormalY=0 NormalZ=1 AngleXU=0 Radius=1.5 StartAngle=3.1416 EndAngle=6.28319
    g4: ArcOfCircle CenterX=-10 CenterY=-4.3 CenterZ=0 NormalX=0 NormalY=0 NormalZ=1 AngleXU=0 Radius=1.5 StartAngle=2e-16 EndAngle=3.14159
    g5: ArcOfCircle CenterX=-16.1 CenterY=-1.8 CenterZ=0 NormalX=0 NormalY=0 NormalZ=1 AngleXU=0 Radius=1.5 StartAngle=5e-16 EndAngle=3.14159
    g6: ArcOfCircle CenterX=-22.1 CenterY=-1.8 CenterZ=0 NormalX=0 NormalY=0 NormalZ=1 AngleXU=0 Radius=1.5 StartAngle=5e-16 EndAngle=3.14159
    g7: ArcOfCircle CenterX=-28.2 CenterY=-4.3 CenterZ=0 NormalX=0 NormalY=0 NormalZ=1 AngleXU=0 Radius=1.5 StartAngle=2e-16 EndAngle=3.14159
    g8: ArcOfCircle CenterX=-10 CenterY=-33.9 CenterZ=0 NormalX=0 NormalY=0 NormalZ=1 AngleXU=0 Radius=1.5 StartAngle=3.14159 EndAngle=6.28319
    g9: ArcOfCircle CenterX=-16.1 CenterY=-36.4 CenterZ=0 NormalX=0 NormalY=0 NormalZ=1 AngleXU=0 Radius=1.5 StartAngle=3.14159 EndAngle=6.28319
    g10: ArcOfCircle CenterX=-22.1 CenterY=-36.4 CenterZ=0 NormalX=0 NormalY=0 NormalZ=1 AngleXU=0 Radius=1.5 StartAngle=3.14159 EndAngle=6.28319
    g11: ArcOfCircle CenterX=-28.2 CenterY=-33.9 CenterZ=0 NormalX=0 NormalY=0 NormalZ=1 AngleXU=0 Radius=1.5 StartAngle=3.14159 EndAngle=6.28319
    g12: LineSegment StartX=-35.7 StartY=-10.5 StartZ=0 EndX=-35.7 EndY=-27.7 EndZ=0
    g13: LineSegment StartX=-32.7 StartY=-10.5 StartZ=0 EndX=-32.7 EndY=-27.7 EndZ=0
    g14: LineSegment StartX=-29.7 StartY=-33.9 StartZ=0 EndX=-29.7 EndY=-4.3 EndZ=0
    g15: LineSegment StartX=-26.7 StartY=-33.9 StartZ=0 EndX=-26.7 EndY=-4.3 EndZ=0
    g16: LineSegment StartX=-2.5 StartY=-10.5 StartZ=0 EndX=-2.5 EndY=-27.7 EndZ=0
    g17: LineSegment StartX=-8.5 StartY=-4.3 StartZ=0 EndX=-8.5 EndY=-33.9 EndZ=0
    g18: LineSegment StartX=-5.5 StartY=-10.5 StartZ=0 EndX=-5.5 EndY=-27.7 EndZ=0
    g19: LineSegment StartX=-11.5 StartY=-4.3 StartZ=0 EndX=-11.5 EndY=-33.9 EndZ=0
    g20: LineSegment StartX=-14.6 StartY=-1.8 StartZ=0 EndX=-14.6 EndY=-36.4 EndZ=0
    g21: LineSegment StartX=-17.6 StartY=-1.8 StartZ=0 EndX=-17.6 EndY=-36.4 EndZ=0
    g22: LineSegment StartX=-20.6 StartY=-36.4 StartZ=0 EndX=-20.6 EndY=-1.8 EndZ=0
    g23: LineSegment StartX=-23.6 StartY=-1.8 StartZ=0 EndX=-23.6 EndY=-36.4 EndZ=0
  constraints (48):
    c: Block(g0)
    c: Block(g1)
    c: Block(g2)
    c: Block(g3)
    c: Block(g4)
    c: Block(g5)
    c: Block(g6)
    c: Block(g7)
    c: Block(g8)
    c: Block(g9)
    c: Block(g10)
    c: Block(g11)
    c: Coincident(g12,g1)
    c: Coincident(g12,g2)
    c: Vertical(g12)
    c: Coincident(g13,g1)
    c: Coincident(g13,g2)
    c: Vertical(g13)
    c: Coincident(g14,g11)
    c: Coincident(g14,g7)
    c: Vertical(g14)
    c: Coincident(g15,g11)
    c: Coincident(g15,g7)
    c: Vertical(g15)
    c: Coincident(g16,g0)
    c: Coincident(g16,g3)
    c: Vertical(g16)
    c: Coincident(g17,g4)
    c: Coincident(g17,g8)
    c: Vertical(g17)
    c: Coincident(g18,g0)
    c: Coincident(g18,g3)
    c: Vertical(g18)
    c: Coincident(g19,g4)
    c: Coincident(g19,g8)
    c: Vertical(g19)
    c: Coincident(g20,g5)
    c: Coincident(g20,g9)
    c: Vertical(g20)
    c: Coincident(g21,g5)
    c: Coincident(g21,g9)
    c: Vertical(g21)
    c: Coincident(g22,g10)
    c: Coincident(g22,g6)
    c: Vertical(g22)
    c: Coincident(g23,g6)
    c: Coincident(g23,g10)
    c: Vertical(g23)
FEATURE [Part::Extrusion] Extrude048  label="removeToCreateFanGrillHoles004"
  Base = -> Sketch057
  Dir = (0,-1,6e-16)
  DirMode = 2
  FaceMakerClass = Part::FaceMakerBullseye
  LengthFwd = 10
  LengthRev = 0
  Placement = pos=(65.4,44,54.82) rot=(0,0,1;0rad)
  Solid = true
  Symmetric = false
FEATURE [Part::Cut] Cut040  label="top021"
  Base = -> Fillet039
  Tool = -> Extrude048
FEATURE [Part::Cylinder] Cylinder041  label="removeToCreteHoleForPlugHousing034"
  Angle = 360
  AttacherType = Attacher::AttachEngine3D
  Height = 20
  Placement = pos=(-2,19,36) rot=(0,1,0;1.5708rad)
  Radius = 14.3
FEATURE [Part::MultiFuse] Fusion089  label="removeToCreteHoleForPlugHousing035"
  Shapes = -> [Box026,Cylinder041]
FEATURE [Part::Cylinder] Cylinder042
  Angle = 360
  AttacherType = Attacher::AttachEngine3D
  Height = 20
  Placement = pos=(0,0,36.15) rot=(0,0,1;0rad)
  Radius = 14.3
FEATURE [Part::Cylinder] Cylinder043
  Angle = 360
  AttacherType = Attacher::AttachEngine3D
  Height = 10
  Placement = pos=(0,0,36.15) rot=(0,0,1;0rad)
  Radius = 4
FEATURE [Part::Box] Box027  label="removeToCreteHoleForPlugHousing036"
  AttacherType = Attacher::AttachEngine3D
  Height = 28.6
  Length = 20
  Placement = pos=(106.15,0,21.7) rot=(0,0,1;0rad)
  Width = 19
FEATURE [Part::Cut] Cut041  label="top022"
  Base = -> Cut040
  Tool = -> Fusion087
FEATURE [Part::Cut] Cut039  label="top020"
  Base = -> Cut041
  Tool = -> Fusion089
FEATURE [Part::MultiFuse] Fusion090  label="removeToCreteHoleForPlugHousing037"
  Placement = pos=(70,19,36) rot=(0,1,0;1.5708rad)
  Shapes = -> [Cylinder042,Cylinder043]
FEATURE [Part::MultiFuse] Fusion088  label="removeToCreteHoleForPlugHousing033"
  Shapes = -> [Box027,Fusion090]
FEATURE [Part::Cut] Cut042  label="removeToCreteHoleForPlugHousing038"
  Base = -> Cut039
  Tool = -> Fusion088
FEATURE [Part::MultiFuse] Fusion091  label="removeFromTop"
  Shapes = -> [Fillet038,Fusion085,Fusion084,Fusion083,Extrude045]
FEATURE [Part::Cut] Cut043  label="REAL TOP ====="
  Base = -> Fillet036
  Tool = -> Fusion091
FEATURE [Part::MultiFuse] Fusion092  label="caseScrewPillarBracket016"
  Shapes = -> [Extrude030,Extrude031,Extrude032,Extrude033,Extrude034,Extrude035,Extrude036,Extrude037,Box013,Box014]
FEATURE [Sketcher::SketchObject] Sketch058  label="topSketch015"
  FullyConstrained = true
  sketch-geometry (20):
    g0: LineSegment StartX=5.21097e-06 StartY=3 StartZ=0 EndX=5.21097e-06 EndY=19 EndZ=0
    g1: ArcOfCircle CenterX=19 CenterY=19 CenterZ=0 NormalX=0 NormalY=0 NormalZ=1 AngleXU=0 Radius=19 StartAngle=1.5708 EndAngle=3.14159
    g2: ArcOfCircle CenterX=19 CenterY=19 CenterZ=0 NormalX=0 NormalY=0 NormalZ=1 AngleXU=0 Radius=16 StartAngle=1.5708 EndAngle=3.14159
    g3: LineSegment StartX=114 StartY=35 StartZ=0 EndX=19 EndY=35 EndZ=0
    g4: LineSegment StartX=5.21097e-06 StartY=3 StartZ=0 EndX=5.21097e-06 EndY=0 EndZ=0
    g5: LineSegment StartX=3 StartY=0 StartZ=0 EndX=5.21097e-06 EndY=0 EndZ=0
    g6: LineSegment StartX=3 StartY=19 StartZ=0 EndX=3 EndY=0 EndZ=0
    g7: LineSegment StartX=19 StartY=38 StartZ=0 EndX=124 EndY=38 EndZ=0
    g8: Circle CenterX=119 CenterY=35 CenterZ=0 NormalX=0 NormalY=0 NormalZ=1 AngleXU=0 Radius=1
    g9: Circle CenterX=121 CenterY=35 CenterZ=0 NormalX=0 NormalY=0 NormalZ=1 AngleXU=0 Radius=1
    g10: Circle CenterX=121 CenterY=33 CenterZ=0 NormalX=0 NormalY=0 NormalZ=1 AngleXU=0 Radius=1
    g11: BSplineCurve PolesCount=3 KnotsCount=2 Degree=2 IsPeriodic=0
    g12: GeomPoint X=119 Y=35 Z=0
    g13: GeomPoint X=121 Y=33 Z=0
    g14: LineSegment StartX=119 StartY=35 StartZ=0 EndX=114 EndY=35 EndZ=0
    g15: ArcOfCircle CenterX=105 CenterY=19 CenterZ=0 NormalX=0 NormalY=0 NormalZ=1 AngleXU=0 Radius=19 StartAngle=5.7297 EndAngle=6.28319
    g16: ArcOfCircle CenterX=105 CenterY=19 CenterZ=0 NormalX=0 NormalY=0 NormalZ=1 AngleXU=0 Radius=16 StartAngle=5.60905 EndAngle=6.28319
    g17: LineSegment StartX=121 StartY=33 StartZ=0 EndX=121 EndY=19 EndZ=0
    g18: LineSegment StartX=124 StartY=38 StartZ=0 EndX=124 EndY=19 EndZ=0
    g19: LineSegment StartX=117.5 StartY=9.01251 StartZ=0 EndX=121.163 EndY=9.0125 EndZ=0
  constraints (46):
    c: Vertical(g0)
    c: Block(g0)
    c: Coincident(g1,g0)
    c: Block(g1)
    c: Coincident(g2,g1)
    c: Block(g2)
    c: Coincident(g3,g2)
    c: Horizontal(g3)
    c: Tangent(g3,g2)
    c: Coincident(g4,g0)
    c: Distance(g4) = 3
    c: Vertical(g4)
    c: Coincident(g5,g4)
    c: Horizontal(g5)
    c: Coincident(g6,g2)
    c: Coincident(g6,g5)
    c: Vertical(g6)
    c: Horizontal(g7)
    c: Distance(g7) = 105
    c: Coincident(g7,g1)
    c: Block(g3)
    c: Weight(g8) = 1
    c: Equal(g8,g9)
    c: Equal(g8,g10)
    c: InternalAlignment(g8,g11)
    c: InternalAlignment(g9,g11)
    c: InternalAlignment(g10,g11)
    c: InternalAlignment(g12,g11)
    c: InternalAlignment(g13,g11)
    c: Block(g11)
    c: Coincident(g14,g11)
    c: Coincident(g14,g3)
    c: Horizontal(g14)
    c: Block(g15)
    c: Coincident(g16,g15)
    c: Block(g16)
    c: Coincident(g17,g11)
    c: Coincident(g17,g16)
    c: Vertical(g17)
    c: Distance(g17) = 14
    c: Coincident(g18,g7)
    c: Coincident(g18,g15)
    c: Vertical(g18)
    c: Distance(g18) = 19
    c: Coincident(g19,g16)
    c: Coincident(g19,g15)
FEATURE [Part::Extrusion] Extrude049  label="top023"
  Base = -> Sketch058
  Dir = (0,0,1)
  DirMode = 2
  FaceMakerClass = Part::FaceMakerBullseye
  LengthFwd = 72
  LengthRev = 0
  Solid = true
  Symmetric = false
FEATURE [Sketcher::SketchObject] Sketch059
  FullyConstrained = true
  MapMode = 3
  Placement = pos=(0,0,0) rot=(1,0,0;1.5708rad)
  Support = -> [Extrude049]
  sketch-geometry (8):
    g0: Circle CenterX=80.351 CenterY=-67.6202 CenterZ=0 NormalX=0 NormalY=0 NormalZ=1 AngleXU=0 Radius=2
    g1: Circle CenterX=80.351 CenterY=-67.6202 CenterZ=0 NormalX=0 NormalY=0 NormalZ=1 AngleXU=0 Radius=3
    g2: Circle CenterX=80.351 CenterY=-4.92017 CenterZ=0 NormalX=0 NormalY=0 NormalZ=1 AngleXU=0 Radius=2
    g3: Circle CenterX=80.351 CenterY=-4.92017 CenterZ=0 NormalX=0 NormalY=0 NormalZ=1 AngleXU=0 Radius=3
    g4: Circle CenterX=23.851 CenterY=-4.92017 CenterZ=0 NormalX=0 NormalY=0 NormalZ=1 AngleXU=0 Radius=2
    g5: Circle CenterX=23.851 CenterY=-4.92017 CenterZ=0 NormalX=0 NormalY=0 NormalZ=1 AngleXU=0 Radius=3
    g6: Circle CenterX=23.851 CenterY=-67.6202 CenterZ=0 NormalX=0 NormalY=0 NormalZ=1 AngleXU=0 Radius=2
    g7: Circle CenterX=23.851 CenterY=-67.6202 CenterZ=0 NormalX=0 NormalY=0 NormalZ=1 AngleXU=0 Radius=3
  constraints (8):
    c: Block(g3)
    c: Block(g2)
    c: Block(g1)
    c: Block(g0)
    c: Block(g6)
    c: Block(g7)
    c: Block(g4)
    c: Block(g5)
FEATURE [Sketcher::SketchObject] Sketch060
  FullyConstrained = true
  MapMode = 3
  Placement = pos=(0,0,0) rot=(1,0,0;1.5708rad)
  Support = -> [Extrude049]
  sketch-geometry (8):
    g0: Circle CenterX=80.351 CenterY=-67.6202 CenterZ=0 NormalX=0 NormalY=0 NormalZ=1 AngleXU=0 Radius=3
    g1: Circle CenterX=80.351 CenterY=-4.92017 CenterZ=0 NormalX=0 NormalY=0 NormalZ=1 AngleXU=0 Radius=3
    g2: Circle CenterX=23.851 CenterY=-4.92017 CenterZ=0 NormalX=0 NormalY=0 NormalZ=1 AngleXU=0 Radius=3
    g3: Circle CenterX=23.851 CenterY=-67.6202 CenterZ=0 NormalX=0 NormalY=0 NormalZ=1 AngleXU=0 Radius=3
    g4: Circle CenterX=23.851 CenterY=-67.6202 CenterZ=0 NormalX=0 NormalY=0 NormalZ=1 AngleXU=0 Radius=5
    g5: Circle CenterX=80.351 CenterY=-67.6202 CenterZ=0 NormalX=0 NormalY=0 NormalZ=1 AngleXU=0 Radius=5
    g6: Circle CenterX=23.851 CenterY=-4.92017 CenterZ=0 NormalX=0 NormalY=0 NormalZ=1 AngleXU=0 Radius=5
    g7: Circle CenterX=80.351 CenterY=-4.92017 CenterZ=0 NormalX=0 NormalY=0 NormalZ=1 AngleXU=0 Radius=5
  constraints (8):
    c: Block(g1)
    c: Block(g0)
    c: Block(g3)
    c: Block(g2)
    c: Block(g5)
    c: Block(g4)
    c: Block(g6)
    c: Block(g7)
FEATURE [Sketcher::SketchObject] Sketch061
  FullyConstrained = true
  MapMode = 3
  Placement = pos=(0,0,0) rot=(1,0,0;1.5708rad)
  sketch-geometry (8):
    g0: Circle CenterX=80.351 CenterY=-67.6202 CenterZ=0 NormalX=0 NormalY=0 NormalZ=1 AngleXU=0 Radius=3
    g1: Circle CenterX=80.351 CenterY=-4.92017 CenterZ=0 NormalX=0 NormalY=0 NormalZ=1 AngleXU=0 Radius=3
    g2: Circle CenterX=23.851 CenterY=-4.92017 CenterZ=0 NormalX=0 NormalY=0 NormalZ=1 AngleXU=0 Radius=3
    g3: Circle CenterX=23.851 CenterY=-67.6202 CenterZ=0 NormalX=0 NormalY=0 NormalZ=1 AngleXU=0 Radius=3
    g4: Circle CenterX=23.851 CenterY=-67.6202 CenterZ=0 NormalX=0 NormalY=0 NormalZ=1 AngleXU=0 Radius=5
    g5: Circle CenterX=80.351 CenterY=-67.6202 CenterZ=0 NormalX=0 NormalY=0 NormalZ=1 AngleXU=0 Radius=5
    g6: Circle CenterX=23.851 CenterY=-4.92017 CenterZ=0 NormalX=0 NormalY=0 NormalZ=1 AngleXU=0 Radius=5
    g7: Circle CenterX=80.351 CenterY=-4.92017 CenterZ=0 NormalX=0 NormalY=0 NormalZ=1 AngleXU=0 Radius=5
  constraints (8):
    c: Block(g1)
    c: Block(g0)
    c: Block(g3)
    c: Block(g2)
    c: Block(g5)
    c: Block(g4)
    c: Block(g6)
    c: Block(g7)
FEATURE [Sketcher::SketchObject] Sketch062  label="topSketch016"
  FullyConstrained = true
  sketch-geometry (20):
    g0: LineSegment StartX=5.21097e-06 StartY=3 StartZ=0 EndX=5.21097e-06 EndY=19 EndZ=0
    g1: ArcOfCircle CenterX=19 CenterY=19 CenterZ=0 NormalX=0 NormalY=0 NormalZ=1 AngleXU=0 Radius=19 StartAngle=1.5708 EndAngle=3.14159
    g2: ArcOfCircle CenterX=19 CenterY=19 CenterZ=0 NormalX=0 NormalY=0 NormalZ=1 AngleXU=0 Radius=16 StartAngle=1.5708 EndAngle=3.14159
    g3: LineSegment StartX=114 StartY=35 StartZ=0 EndX=19 EndY=35 EndZ=0
    g4: LineSegment StartX=5.21097e-06 StartY=3 StartZ=0 EndX=5.21097e-06 EndY=0 EndZ=0
    g5: LineSegment StartX=3 StartY=0 StartZ=0 EndX=5.21097e-06 EndY=0 EndZ=0
    g6: LineSegment StartX=3 StartY=19 StartZ=0 EndX=3 EndY=0 EndZ=0
    g7: LineSegment StartX=19 StartY=38 StartZ=0 EndX=124 EndY=38 EndZ=0
    g8: Circle CenterX=119 CenterY=35 CenterZ=0 NormalX=0 NormalY=0 NormalZ=1 AngleXU=0 Radius=1
    g9: Circle CenterX=121 CenterY=35 CenterZ=0 NormalX=0 NormalY=0 NormalZ=1 AngleXU=0 Radius=1
    g10: Circle CenterX=121 CenterY=33 CenterZ=0 NormalX=0 NormalY=0 NormalZ=1 AngleXU=0 Radius=1
    g11: BSplineCurve PolesCount=3 KnotsCount=2 Degree=2 IsPeriodic=0
    g12: GeomPoint X=119 Y=35 Z=0
    g13: GeomPoint X=121 Y=33 Z=0
    g14: LineSegment StartX=119 StartY=35 StartZ=0 EndX=114 EndY=35 EndZ=0
    g15: ArcOfCircle CenterX=105 CenterY=19 CenterZ=0 NormalX=0 NormalY=0 NormalZ=1 AngleXU=0 Radius=19 StartAngle=5.7297 EndAngle=6.28319
    g16: ArcOfCircle CenterX=105 CenterY=19 CenterZ=0 NormalX=0 NormalY=0 NormalZ=1 AngleXU=0 Radius=16 StartAngle=5.60905 EndAngle=6.28319
    g17: LineSegment StartX=121 StartY=33 StartZ=0 EndX=121 EndY=19 EndZ=0
    g18: LineSegment StartX=124 StartY=38 StartZ=0 EndX=124 EndY=19 EndZ=0
    g19: LineSegment StartX=117.5 StartY=9.01251 StartZ=0 EndX=121.163 EndY=9.0125 EndZ=0
  constraints (46):
    c: Vertical(g0)
    c: Block(g0)
    c: Coincident(g1,g0)
    c: Block(g1)
    c: Coincident(g2,g1)
    c: Block(g2)
    c: Coincident(g3,g2)
    c: Horizontal(g3)
    c: Tangent(g3,g2)
    c: Coincident(g4,g0)
    c: Distance(g4) = 3
    c: Vertical(g4)
    c: Coincident(g5,g4)
    c: Horizontal(g5)
    c: Coincident(g6,g2)
    c: Coincident(g6,g5)
    c: Vertical(g6)
    c: Horizontal(g7)
    c: Distance(g7) = 105
    c: Coincident(g7,g1)
    c: Block(g3)
    c: Weight(g8) = 1
    c: Equal(g8,g9)
    c: Equal(g8,g10)
    c: InternalAlignment(g8,g11)
    c: InternalAlignment(g9,g11)
    c: InternalAlignment(g10,g11)
    c: InternalAlignment(g12,g11)
    c: InternalAlignment(g13,g11)
    c: Block(g11)
    c: Coincident(g14,g11)
    c: Coincident(g14,g3)
    c: Horizontal(g14)
    c: Block(g15)
    c: Coincident(g16,g15)
    c: Block(g16)
    c: Coincident(g17,g11)
    c: Coincident(g17,g16)
    c: Vertical(g17)
    c: Distance(g17) = 14
    c: Coincident(g18,g7)
    c: Coincident(g18,g15)
    c: Vertical(g18)
    c: Distance(g18) = 19
    c: Coincident(g19,g16)
    c: Coincident(g19,g15)
FEATURE [Part::Extrusion] Extrude053  label="top024"
  Base = -> Sketch062
  Dir = (0,0,1)
  DirMode = 2
  FaceMakerClass = Part::FaceMakerBullseye
  LengthFwd = 72
  LengthRev = 0
  Solid = true
  Symmetric = false
FEATURE [Sketcher::SketchObject] Sketch063
  FullyConstrained = true
  MapMode = 3
  Placement = pos=(0,0,0) rot=(1,0,0;1.5708rad)
  Support = -> [Extrude053]
  sketch-geometry (8):
    g0: Circle CenterX=80.351 CenterY=-67.6202 CenterZ=0 NormalX=0 NormalY=0 NormalZ=1 AngleXU=0 Radius=2
    g1: Circle CenterX=80.351 CenterY=-67.6202 CenterZ=0 NormalX=0 NormalY=0 NormalZ=1 AngleXU=0 Radius=3
    g2: Circle CenterX=80.351 CenterY=-4.92017 CenterZ=0 NormalX=0 NormalY=0 NormalZ=1 AngleXU=0 Radius=2
    g3: Circle CenterX=80.351 CenterY=-4.92017 CenterZ=0 NormalX=0 NormalY=0 NormalZ=1 AngleXU=0 Radius=3
    g4: Circle CenterX=23.851 CenterY=-4.92017 CenterZ=0 NormalX=0 NormalY=0 NormalZ=1 AngleXU=0 Radius=2
    g5: Circle CenterX=23.851 CenterY=-4.92017 CenterZ=0 NormalX=0 NormalY=0 NormalZ=1 AngleXU=0 Radius=3
    g6: Circle CenterX=23.851 CenterY=-67.6202 CenterZ=0 NormalX=0 NormalY=0 NormalZ=1 AngleXU=0 Radius=2
    g7: Circle CenterX=23.851 CenterY=-67.6202 CenterZ=0 NormalX=0 NormalY=0 NormalZ=1 AngleXU=0 Radius=3
  constraints (8):
    c: Block(g3)
    c: Block(g2)
    c: Block(g1)
    c: Block(g0)
    c: Block(g6)
    c: Block(g7)
    c: Block(g4)
    c: Block(g5)
FEATURE [Part::Extrusion] Extrude054
  Base = -> Sketch063
  Dir = (0,-1,2e-16)
  DirMode = 2
  FaceMakerClass = Part::FaceMakerBullseye
  LengthFwd = 6
  LengthRev = 0
  Placement = pos=(0,9,0) rot=(0,0,1;0rad)
  Solid = true
  Symmetric = false
FEATURE [Sketcher::SketchObject] Sketch064  label="topSketch017"
  FullyConstrained = true
  sketch-geometry (20):
    g0: LineSegment StartX=5.21097e-06 StartY=3 StartZ=0 EndX=5.21097e-06 EndY=19 EndZ=0
    g1: ArcOfCircle CenterX=19 CenterY=19 CenterZ=0 NormalX=0 NormalY=0 NormalZ=1 AngleXU=0 Radius=19 StartAngle=1.5708 EndAngle=3.14159
    g2: ArcOfCircle CenterX=19 CenterY=19 CenterZ=0 NormalX=0 NormalY=0 NormalZ=1 AngleXU=0 Radius=16 StartAngle=1.5708 EndAngle=3.14159
    g3: LineSegment StartX=114 StartY=35 StartZ=0 EndX=19 EndY=35 EndZ=0
    g4: LineSegment StartX=5.21097e-06 StartY=3 StartZ=0 EndX=5.21097e-06 EndY=0 EndZ=0
    g5: LineSegment StartX=3 StartY=0 StartZ=0 EndX=5.21097e-06 EndY=0 EndZ=0
    g6: LineSegment StartX=3 StartY=19 StartZ=0 EndX=3 EndY=0 EndZ=0
    g7: LineSegment StartX=19 StartY=38 StartZ=0 EndX=124 EndY=38 EndZ=0
    g8: Circle CenterX=119 CenterY=35 CenterZ=0 NormalX=0 NormalY=0 NormalZ=1 AngleXU=0 Radius=1
    g9: Circle CenterX=121 CenterY=35 CenterZ=0 NormalX=0 NormalY=0 NormalZ=1 AngleXU=0 Radius=1
    g10: Circle CenterX=121 CenterY=33 CenterZ=0 NormalX=0 NormalY=0 NormalZ=1 AngleXU=0 Radius=1
    g11: BSplineCurve PolesCount=3 KnotsCount=2 Degree=2 IsPeriodic=0
    g12: GeomPoint X=119 Y=35 Z=0
    g13: GeomPoint X=121 Y=33 Z=0
    g14: LineSegment StartX=119 StartY=35 StartZ=0 EndX=114 EndY=35 EndZ=0
    g15: ArcOfCircle CenterX=105 CenterY=19 CenterZ=0 NormalX=0 NormalY=0 NormalZ=1 AngleXU=0 Radius=19 StartAngle=5.7297 EndAngle=6.28319
    g16: ArcOfCircle CenterX=105 CenterY=19 CenterZ=0 NormalX=0 NormalY=0 NormalZ=1 AngleXU=0 Radius=16 StartAngle=5.60905 EndAngle=6.28319
    g17: LineSegment StartX=121 StartY=33 StartZ=0 EndX=121 EndY=19 EndZ=0
    g18: LineSegment StartX=124 StartY=38 StartZ=0 EndX=124 EndY=19 EndZ=0
    g19: LineSegment StartX=117.5 StartY=9.01251 StartZ=0 EndX=121.163 EndY=9.0125 EndZ=0
  constraints (46):
    c: Vertical(g0)
    c: Block(g0)
    c: Coincident(g1,g0)
    c: Block(g1)
    c: Coincident(g2,g1)
    c: Block(g2)
    c: Coincident(g3,g2)
    c: Horizontal(g3)
    c: Tangent(g3,g2)
    c: Coincident(g4,g0)
    c: Distance(g4) = 3
    c: Vertical(g4)
    c: Coincident(g5,g4)
    c: Horizontal(g5)
    c: Coincident(g6,g2)
    c: Coincident(g6,g5)
    c: Vertical(g6)
    c: Horizontal(g7)
    c: Distance(g7) = 105
    c: Coincident(g7,g1)
    c: Block(g3)
    c: Weight(g8) = 1
    c: Equal(g8,g9)
    c: Equal(g8,g10)
    c: InternalAlignment(g8,g11)
    c: InternalAlignment(g9,g11)
    c: InternalAlignment(g10,g11)
    c: InternalAlignment(g12,g11)
    c: InternalAlignment(g13,g11)
    c: Block(g11)
    c: Coincident(g14,g11)
    c: Coincident(g14,g3)
    c: Horizontal(g14)
    c: Block(g15)
    c: Coincident(g16,g15)
    c: Block(g16)
    c: Coincident(g17,g11)
    c: Coincident(g17,g16)
    c: Vertical(g17)
    c: Distance(g17) = 14
    c: Coincident(g18,g7)
    c: Coincident(g18,g15)
    c: Vertical(g18)
    c: Distance(g18) = 19
    c: Coincident(g19,g16)
    c: Coincident(g19,g15)
FEATURE [Sketcher::SketchObject] Sketch065
  FullyConstrained = true
  MapMode = 3
  Placement = pos=(0,0,0) rot=(1,0,0;1.5708rad)
  sketch-geometry (8):
    g0: Circle CenterX=80.351 CenterY=-67.6202 CenterZ=0 NormalX=0 NormalY=0 NormalZ=1 AngleXU=0 Radius=3
    g1: Circle CenterX=80.351 CenterY=-4.92017 CenterZ=0 NormalX=0 NormalY=0 NormalZ=1 AngleXU=0 Radius=3
    g2: Circle CenterX=23.851 CenterY=-4.92017 CenterZ=0 NormalX=0 NormalY=0 NormalZ=1 AngleXU=0 Radius=3
    g3: Circle CenterX=23.851 CenterY=-67.6202 CenterZ=0 NormalX=0 NormalY=0 NormalZ=1 AngleXU=0 Radius=3
    g4: Circle CenterX=23.851 CenterY=-67.6202 CenterZ=0 NormalX=0 NormalY=0 NormalZ=1 AngleXU=0 Radius=5
    g5: Circle CenterX=80.351 CenterY=-67.6202 CenterZ=0 NormalX=0 NormalY=0 NormalZ=1 AngleXU=0 Radius=5
    g6: Circle CenterX=23.851 CenterY=-4.92017 CenterZ=0 NormalX=0 NormalY=0 NormalZ=1 AngleXU=0 Radius=5
    g7: Circle CenterX=80.351 CenterY=-4.92017 CenterZ=0 NormalX=0 NormalY=0 NormalZ=1 AngleXU=0 Radius=5
  constraints (8):
    c: Block(g1)
    c: Block(g0)
    c: Block(g3)
    c: Block(g2)
    c: Block(g5)
    c: Block(g4)
    c: Block(g6)
    c: Block(g7)
FEATURE [Part::Extrusion] Extrude056
  Base = -> Sketch065
  Dir = (0,-1,2e-16)
  DirMode = 2
  FaceMakerClass = Part::FaceMakerBullseye
  LengthFwd = 2
  LengthRev = 0
  Solid = true
  Symmetric = false
FEATURE [Part::Extrusion] Extrude057  label="top025"
  Base = -> Sketch064
  Dir = (0,0,1)
  DirMode = 2
  FaceMakerClass = Part::FaceMakerBullseye
  LengthFwd = 72
  LengthRev = 0
  Solid = true
  Symmetric = false
FEATURE [Sketcher::SketchObject] Sketch066
  FullyConstrained = true
  MapMode = 3
  Placement = pos=(0,0,0) rot=(1,0,0;1.5708rad)
  Support = -> [Extrude057]
  sketch-geometry (8):
    g0: Circle CenterX=80.351 CenterY=-67.6202 CenterZ=0 NormalX=0 NormalY=0 NormalZ=1 AngleXU=0 Radius=3
    g1: Circle CenterX=80.351 CenterY=-4.92017 CenterZ=0 NormalX=0 NormalY=0 NormalZ=1 AngleXU=0 Radius=3
    g2: Circle CenterX=23.851 CenterY=-4.92017 CenterZ=0 NormalX=0 NormalY=0 NormalZ=1 AngleXU=0 Radius=3
    g3: Circle CenterX=23.851 CenterY=-67.6202 CenterZ=0 NormalX=0 NormalY=0 NormalZ=1 AngleXU=0 Radius=3
    g4: Circle CenterX=23.851 CenterY=-67.6202 CenterZ=0 NormalX=0 NormalY=0 NormalZ=1 AngleXU=0 Radius=5
    g5: Circle CenterX=80.351 CenterY=-67.6202 CenterZ=0 NormalX=0 NormalY=0 NormalZ=1 AngleXU=0 Radius=5
    g6: Circle CenterX=23.851 CenterY=-4.92017 CenterZ=0 NormalX=0 NormalY=0 NormalZ=1 AngleXU=0 Radius=5
    g7: Circle CenterX=80.351 CenterY=-4.92017 CenterZ=0 NormalX=0 NormalY=0 NormalZ=1 AngleXU=0 Radius=5
  constraints (8):
    c: Block(g1)
    c: Block(g0)
    c: Block(g3)
    c: Block(g2)
    c: Block(g5)
    c: Block(g4)
    c: Block(g6)
    c: Block(g7)
FEATURE [Part::Extrusion] Extrude055
  Base = -> Sketch066
  Dir = (0,-1,2e-16)
  DirMode = 2
  FaceMakerClass = Part::FaceMakerBullseye
  LengthFwd = 2
  LengthRev = 0
  Solid = true
  Symmetric = false
FEATURE [Part::Fillet] Fillet041
  Base = -> Extrude056
  Edges = 4 edges r=1.99: [Edge6,Edge12,Edge18,Edge24]
FEATURE [Part::Cut] Cut045
  Base = -> Extrude055
  Placement = pos=(0,6,0) rot=(0,0,1;0rad)
  Tool = -> Fillet041
FEATURE [Part::MultiFuse] Fusion095  label="pcbScrewPillars"
  Placement = pos=(-3.2,-1,72.3) rot=(0,0,1;0rad)
  Shapes = -> [Cut045,Extrude054]
FEATURE [Part::Feature] Face113
  shape: bbox 3.2 x 1.5 x 2e-07 mm, 1 faces, 0 solids (baked)
FEATURE [Part::Revolution] Revolve121  label="backCaseScrewRetainer002"
  Angle = 360
  Axis = (0,1,0)
  Base = (0,0,0)
  FaceMakerClass = Part::FaceMakerBullseye
  Placement = pos=(12.5,3,62) rot=(0,0,1;0rad)
  Solid = false
  Source = -> Face113
  Symmetric = false
FEATURE [Part::Feature] Face114
  shape: bbox 3.2 x 1.5 x 2e-07 mm, 1 faces, 0 solids (baked)
FEATURE [Part::Feature] Face115
  shape: bbox 3.2 x 1.5 x 2e-07 mm, 1 faces, 0 solids (baked)
FEATURE [Part::Feature] Face116
  shape: bbox 3.2 x 1.5 x 2e-07 mm, 1 faces, 0 solids (baked)
FEATURE [Part::Revolution] Revolve122  label="frontCaseScrewRetainer004"
  Angle = 360
  Axis = (0,1,0)
  Base = (0,0,0)
  FaceMakerClass = Part::FaceMakerBullseye
  Placement = pos=(89.5,3,68.5) rot=(0,0,1;0rad)
  Solid = false
  Source = -> Face115
  Symmetric = false
FEATURE [Part::Revolution] Revolve123  label="frontCaseScrewRetainer005"
  Angle = 360
  Axis = (0,1,0)
  Base = (0,0,0)
  FaceMakerClass = Part::FaceMakerBullseye
  Placement = pos=(89.5,3,3.5) rot=(0,0,1;0rad)
  Solid = false
  Source = -> Face116
  Symmetric = false
FEATURE [Part::Revolution] Revolve124  label="backCaseScrewRetainer003"
  Angle = 360
  Axis = (0,1,0)
  Base = (0,0,0)
  FaceMakerClass = Part::FaceMakerBullseye
  Placement = pos=(12.5,3,10) rot=(0,0,1;0rad)
  Solid = false
  Source = -> Face114
  Symmetric = false
FEATURE [Part::Feature] Face117
  shape: bbox 3.6 x 3.2 x 2e-07 mm, 1 faces, 0 solids (baked)
FEATURE [Part::Revolution] Revolve125  label="moreFrontCaseScrewRetainer004"
  Angle = 360
  Axis = (0,1,0)
  Base = (0,0,0)
  FaceMakerClass = Part::FaceMakerBullseye
  Placement = pos=(109.5,4.5,68.5) rot=(0,0,1;0rad)
  Solid = false
  Source = -> Face117
  Symmetric = false
FEATURE [Part::Feature] Face118
  shape: bbox 3.6 x 3.2 x 2e-07 mm, 1 faces, 0 solids (baked)
FEATURE [Part::Revolution] Revolve126  label="moreFrontCaseScrewRetainer005"
  Angle = 360
  Axis = (0,1,0)
  Base = (0,0,0)
  FaceMakerClass = Part::FaceMakerBullseye
  Placement = pos=(109.5,4.5,3.5) rot=(0,0,1;0rad)
  Solid = false
  Source = -> Face118
  Symmetric = false
FEATURE [Part::MultiFuse] Fusion096  label="screwRetainers001"
  Shapes = -> [Revolve126,Revolve125,Revolve124,Revolve123,Revolve122,Revolve121]
FEATURE [Part::Feature] Face119
  shape: bbox 10 x 16.5 x 2e-07 mm, 1 faces, 0 solids (baked)
FEATURE [Part::Revolution] Revolve130  label="plugHousing050"
  Angle = 360
  Axis = (0,1,0)
  Base = (0,0,0)
  FaceMakerClass = Part::FaceMakerBullseye
  Placement = pos=(0,0,36.15) rot=(0,0,1;0rad)
  Solid = false
  Source = -> Face119
  Symmetric = false
FEATURE [Part::Feature] Face120
  shape: bbox 10 x 16.5 x 2e-07 mm, 1 faces, 0 solids (baked)
FEATURE [Part::Feature] Face121
  shape: bbox 10 x 16.5 x 2e-07 mm, 1 faces, 0 solids (baked)
FEATURE [Part::Revolution] Revolve127  label="plugHousing047"
  Angle = 360
  Axis = (0,1,0)
  Base = (0,0,0)
  FaceMakerClass = Part::FaceMakerBullseye
  Placement = pos=(0,0,36.15) rot=(0,0,1;0rad)
  Solid = false
  Source = -> Face121
  Symmetric = false
FEATURE [Part::Feature] Face122
  shape: bbox 10 x 16.5 x 2e-07 mm, 1 faces, 0 solids (baked)
FEATURE [Part::Feature] Face123
  shape: bbox 10 x 16.5 x 2e-07 mm, 1 faces, 0 solids (baked)
FEATURE [Part::Revolution] Revolve128  label="plugHousing048"
  Angle = 360
  Axis = (0,1,0)
  Base = (0,0,0)
  FaceMakerClass = Part::FaceMakerBullseye
  Placement = pos=(0,0,36.15) rot=(0,0,1;0rad)
  Solid = false
  Source = -> Face123
  Symmetric = false
FEATURE [Part::MultiFuse] Fusion100  label="plugHousing054"
  Placement = pos=(0,0,0) rot=(0,0,1;1.5708rad)
  Shapes = -> [Revolve130,Revolve128]
FEATURE [Part::Feature] Face124
  shape: bbox 10 x 16.5 x 2e-07 mm, 1 faces, 0 solids (baked)
FEATURE [Part::Feature] Face125
  shape: bbox 10 x 16.5 x 2e-07 mm, 1 faces, 0 solids (baked)
FEATURE [Part::Revolution] Revolve129  label="plugHousing049"
  Angle = 360
  Axis = (0,1,0)
  Base = (0,0,0)
  FaceMakerClass = Part::FaceMakerBullseye
  Placement = pos=(0,0,36.15) rot=(0,0,1;0rad)
  Solid = false
  Source = -> Face125
  Symmetric = false
FEATURE [Part::Feature] Face126
  shape: bbox 10 x 16.5 x 2e-07 mm, 1 faces, 0 solids (baked)
FEATURE [Part::Revolution] Revolve131  label="plugHousing058"
  Angle = 360
  Axis = (0,1,0)
  Base = (0,0,0)
  FaceMakerClass = Part::FaceMakerBullseye
  Placement = pos=(0,0,36.15) rot=(0,0,1;0rad)
  Solid = false
  Source = -> Face120
  Symmetric = false
FEATURE [Part::MultiFuse] Fusion099  label="plugHousing053"
  Placement = pos=(0,0,0) rot=(0,0,1;1.5708rad)
  Shapes = -> [Revolve127,Revolve131]
FEATURE [Part::MultiFuse] Fusion102  label="plugHousing056"
  Placement = pos=(0,19,0) rot=(0,0,1;3.14159rad)
  Shapes = -> [Fusion100,Fusion099]
FEATURE [Part::Revolution] Revolve132  label="plugHousing059"
  Angle = 360
  Axis = (0,1,0)
  Base = (0,0,0)
  FaceMakerClass = Part::FaceMakerBullseye
  Placement = pos=(0,0,36.15) rot=(0,0,1;0rad)
  Solid = false
  Source = -> Face126
  Symmetric = false
FEATURE [Part::Revolution] Revolve133  label="plugHousing060"
  Angle = 360
  Axis = (0,1,0)
  Base = (0,0,0)
  FaceMakerClass = Part::FaceMakerBullseye
  Placement = pos=(0,0,36.15) rot=(0,0,1;0rad)
  Solid = false
  Source = -> Face122
  Symmetric = false
FEATURE [Part::MultiFuse] Fusion097  label="plugHousing051"
  Placement = pos=(0,0,0) rot=(0,0,1;1.5708rad)
  Shapes = -> [Revolve133,Revolve132]
FEATURE [Part::Revolution] Revolve134  label="plugHousing061"
  Angle = 360
  Axis = (0,1,0)
  Base = (0,0,0)
  FaceMakerClass = Part::FaceMakerBullseye
  Placement = pos=(0,0,36.15) rot=(0,0,1;0rad)
  Solid = false
  Source = -> Face124
  Symmetric = false
FEATURE [Part::MultiFuse] Fusion101  label="plugHousing055"
  Placement = pos=(0,0,0) rot=(0,0,1;1.5708rad)
  Shapes = -> [Revolve129,Revolve134]
FEATURE [Part::MultiFuse] Fusion098  label="plugHousing052"
  Placement = pos=(0,19,0) rot=(0,0,1;3.14159rad)
  Shapes = -> [Fusion097,Fusion101]
FEATURE [Part::MultiFuse] Fusion103  label="plugHousing057"
  Placement = pos=(122.621,0,-0.15) rot=(0,0,1;0rad)
  Shapes = -> [Fusion102,Fusion098]
FEATURE [Part::Box] Box028  label="Cube015"
  AttacherType = Attacher::AttachEngine3D
  Height = 28
  Length = 3
  Placement = pos=(110.7,19,22) rot=(0,0,1;0rad)
  Width = 15.7
FEATURE [Part::Cylinder] Cylinder044
  Angle = 360
  AttacherType = Attacher::AttachEngine3D
  Height = 20
  Placement = pos=(0,0,36.15) rot=(0,0,1;0rad)
  Radius = 10.3
FEATURE [Part::Cylinder] Cylinder045
  Angle = 360
  AttacherType = Attacher::AttachEngine3D
  Height = 10
  Placement = pos=(0,0,36.15) rot=(0,0,1;0rad)
  Radius = 4
FEATURE [Part::MultiFuse] Fusion104  label="removeToCreteHoleForPlugHousing040"
  Placement = pos=(70,19,36) rot=(0,1,0;1.5708rad)
  Shapes = -> [Cylinder044,Cylinder045]
FEATURE [Part::Cut] Cut046  label="plugHousingTab003"
  Base = -> Box028
  Tool = -> Fusion104
FEATURE [Part::MultiFuse] Fusion105  label="plugHousing062"
  Shapes = -> [Fusion103,Cut046]
FEATURE [Part::Fillet] Fillet042
  Base = -> Fusion105
  Edges = 1 edges r=2: [Edge25]
FEATURE [Part::Fillet] Fillet043  label="plugHousing063"
  Base = -> Fillet042
  Edges = 1 edges r=2: [Edge8]
  Placement = pos=(7,0,0) rot=(0,0,1;0rad)
FEATURE [Part::Feature] Face127
  shape: bbox 10 x 16.5 x 2e-07 mm, 1 faces, 0 solids (baked)
FEATURE [Part::Feature] Face128
  shape: bbox 10 x 16.5 x 2e-07 mm, 1 faces, 0 solids (baked)
FEATURE [Part::Revolution] Revolve137  label="plugHousing070"
  Angle = 360
  Axis = (0,1,0)
  Base = (0,0,0)
  FaceMakerClass = Part::FaceMakerBullseye
  Placement = pos=(0,0,36.15) rot=(0,0,1;0rad)
  Solid = false
  Source = -> Face127
  Symmetric = false
FEATURE [Part::Revolution] Revolve140  label="plugHousing073"
  Angle = 360
  Axis = (0,1,0)
  Base = (0,0,0)
  FaceMakerClass = Part::FaceMakerBullseye
  Placement = pos=(0,0,36.15) rot=(0,0,1;0rad)
  Solid = false
  Source = -> Face128
  Symmetric = false
FEATURE [Part::Feature] Face129
  shape: bbox 10 x 16.5 x 2e-07 mm, 1 faces, 0 solids (baked)
FEATURE [Part::Revolution] Revolve138  label="plugHousing071"
  Angle = 360
  Axis = (0,1,0)
  Base = (0,0,0)
  FaceMakerClass = Part::FaceMakerBullseye
  Placement = pos=(0,0,36.15) rot=(0,0,1;0rad)
  Solid = false
  Source = -> Face129
  Symmetric = false
FEATURE [Part::Feature] Face130
  shape: bbox 10 x 16.5 x 2e-07 mm, 1 faces, 0 solids (baked)
FEATURE [Part::Revolution] Revolve139  label="plugHousing072"
  Angle = 360
  Axis = (0,1,0)
  Base = (0,0,0)
  FaceMakerClass = Part::FaceMakerBullseye
  Placement = pos=(0,0,36.15) rot=(0,0,1;0rad)
  Solid = false
  Source = -> Face130
  Symmetric = false
FEATURE [Part::Feature] Face131
  shape: bbox 10 x 16.5 x 2e-07 mm, 1 faces, 0 solids (baked)
FEATURE [Part::Revolution] Revolve135  label="plugHousing068"
  Angle = 360
  Axis = (0,1,0)
  Base = (0,0,0)
  FaceMakerClass = Part::FaceMakerBullseye
  Placement = pos=(0,0,36.15) rot=(0,0,1;0rad)
  Solid = false
  Source = -> Face131
  Symmetric = false
FEATURE [Part::MultiFuse] Fusion112  label="plugHousing078"
  Placement = pos=(0,0,0) rot=(0,0,1;1.5708rad)
  Shapes = -> [Revolve135,Revolve139]
FEATURE [Part::Feature] Face132
  shape: bbox 10 x 16.5 x 2e-07 mm, 1 faces, 0 solids (baked)
FEATURE [Part::Revolution] Revolve141  label="plugHousing074"
  Angle = 360
  Axis = (0,1,0)
  Base = (0,0,0)
  FaceMakerClass = Part::FaceMakerBullseye
  Placement = pos=(0,0,36.15) rot=(0,0,1;0rad)
  Solid = false
  Source = -> Face132
  Symmetric = false
FEATURE [Part::MultiFuse] Fusion110  label="plugHousing076"
  Placement = pos=(0,0,0) rot=(0,0,1;1.5708rad)
  Shapes = -> [Revolve141,Revolve140]
FEATURE [Part::Feature] Face133
  shape: bbox 10 x 16.5 x 2e-07 mm, 1 faces, 0 solids (baked)
FEATURE [Part::Revolution] Revolve136  label="plugHousing069"
  Angle = 360
  Axis = (0,1,0)
  Base = (0,0,0)
  FaceMakerClass = Part::FaceMakerBullseye
  Placement = pos=(0,0,36.15) rot=(0,0,1;0rad)
  Solid = false
  Source = -> Face133
  Symmetric = false
FEATURE [Part::MultiFuse] Fusion106  label="plugHousing064"
  Placement = pos=(0,0,0) rot=(0,0,1;1.5708rad)
  Shapes = -> [Revolve138,Revolve136]
FEATURE [Part::MultiFuse] Fusion108  label="plugHousing066"
  Placement = pos=(0,19,0) rot=(0,0,1;3.14159rad)
  Shapes = -> [Fusion106,Fusion112]
FEATURE [Part::Feature] Face134
  shape: bbox 10 x 16.5 x 2e-07 mm, 1 faces, 0 solids (baked)
FEATURE [Part::Revolution] Revolve142  label="plugHousing075"
  Angle = 360
  Axis = (0,1,0)
  Base = (0,0,0)
  FaceMakerClass = Part::FaceMakerBullseye
  Placement = pos=(0,0,36.15) rot=(0,0,1;0rad)
  Solid = false
  Source = -> Face134
  Symmetric = false
FEATURE [Part::MultiFuse] Fusion107  label="plugHousing065"
  Placement = pos=(0,0,0) rot=(0,0,1;1.5708rad)
  Shapes = -> [Revolve137,Revolve142]
FEATURE [Part::MultiFuse] Fusion111  label="plugHousing077"
  Placement = pos=(0,19,0) rot=(0,0,1;3.14159rad)
  Shapes = -> [Fusion110,Fusion107]
FEATURE [Part::MultiFuse] Fusion109  label="plugHousing067"
  Placement = pos=(131.236,0,-0.15) rot=(0,0,1;0rad)
  Shapes = -> [Fusion108,Fusion111]
FEATURE [Part::MultiFuse] Fusion113  label="plugHousing079"
  Shapes = -> [Fillet043,Fusion109]
FEATURE [Part::Feature] Face135
  shape: bbox 3.5 x 17.8 x 2e-07 mm, 1 faces, 0 solids (baked)
FEATURE [Part::Revolution] Revolve143  label="removeToCreateScrewAndThreadedInsertHole049"
  Angle = 360
  Axis = (0,1,0)
  Base = (0,0,0)
  FaceMakerClass = Part::FaceMakerBullseye
  Placement = pos=(12.5,0,10) rot=(0,0,1;0rad)
  Solid = false
  Source = -> Face135
  Symmetric = false
FEATURE [Part::Feature] Face136
  shape: bbox 3.5 x 17.8 x 2e-07 mm, 1 faces, 0 solids (baked)
FEATURE [Part::Revolution] Revolve144  label="removeToCreateScrewAndThreadedInsertHole050"
  Angle = 360
  Axis = (0,1,0)
  Base = (0,0,0)
  FaceMakerClass = Part::FaceMakerBullseye
  Placement = pos=(12.5,0,62) rot=(0,0,1;0rad)
  Solid = false
  Source = -> Face136
  Symmetric = false
FEATURE [Part::Feature] Face137
  shape: bbox 3.5 x 17.8 x 2e-07 mm, 1 faces, 0 solids (baked)
FEATURE [Part::Revolution] Revolve145  label="removeToCreateScrewAndThreadedInsertHole051"
  Angle = 360
  Axis = (0,1,0)
  Base = (0,0,0)
  FaceMakerClass = Part::FaceMakerBullseye
  Placement = pos=(89.5,0,68.5) rot=(0,0,1;0rad)
  Solid = false
  Source = -> Face137
  Symmetric = false
FEATURE [Part::Feature] Face138
  shape: bbox 3.5 x 17.8 x 2e-07 mm, 1 faces, 0 solids (baked)
FEATURE [Part::Revolution] Revolve146  label="removeToCreateScrewAndThreadedInsertHole052"
  Angle = 360
  Axis = (0,1,0)
  Base = (0,0,0)
  FaceMakerClass = Part::FaceMakerBullseye
  Placement = pos=(89.5,0,3.5) rot=(0,0,1;0rad)
  Solid = false
  Source = -> Face138
  Symmetric = false
FEATURE [Part::Feature] Face139
  shape: bbox 3.5 x 17.8 x 2e-07 mm, 1 faces, 0 solids (baked)
FEATURE [Part::Revolution] Revolve147  label="removeToCreateScrewAndThreadedInsertHole053"
  Angle = 360
  Axis = (0,1,0)
  Base = (0,0,0)
  FaceMakerClass = Part::FaceMakerBullseye
  Placement = pos=(109.5,4.7,3.5) rot=(0,0,1;0rad)
  Solid = false
  Source = -> Face139
  Symmetric = false
FEATURE [Part::Feature] Face140
  shape: bbox 3.5 x 17.8 x 2e-07 mm, 1 faces, 0 solids (baked)
FEATURE [Part::Revolution] Revolve148  label="removeToCreateScrewAndThreadedInsertHole054"
  Angle = 360
  Axis = (0,1,0)
  Base = (0,0,0)
  FaceMakerClass = Part::FaceMakerBullseye
  Placement = pos=(109.5,4.7,68.5) rot=(0,0,1;0rad)
  Solid = false
  Source = -> Face140
  Symmetric = false
FEATURE [Part::MultiFuse] Fusion114  label="removeToCreateScrewAndThreadedInsertHole055"
  Shapes = -> [Revolve148,Revolve147,Revolve146,Revolve145,Revolve144,Revolve143]
FEATURE [Part::Cut] Cut047  label="casePillars004"
  Base = -> Cut037
  Tool = -> Fusion114
FEATURE [Part::Feature] Face141
  shape: bbox 3.5 x 17.8 x 2e-07 mm, 1 faces, 0 solids (baked)
FEATURE [Part::Feature] Face142
  shape: bbox 3.5 x 17.8 x 2e-07 mm, 1 faces, 0 solids (baked)
FEATURE [Part::Feature] Face143
  shape: bbox 3.5 x 17.8 x 2e-07 mm, 1 faces, 0 solids (baked)
FEATURE [Part::Revolution] Revolve149  label="removeToCreateScrewAndThreadedInsertHole057"
  Angle = 360
  Axis = (0,1,0)
  Base = (0,0,0)
  FaceMakerClass = Part::FaceMakerBullseye
  Placement = pos=(12.5,0,10) rot=(0,0,1;0rad)
  Solid = false
  Source = -> Face141
  Symmetric = false
FEATURE [Part::Feature] Face144
  shape: bbox 3.5 x 17.8 x 2e-07 mm, 1 faces, 0 solids (baked)
FEATURE [Part::Feature] Face145
  shape: bbox 3.5 x 17.8 x 2e-07 mm, 1 faces, 0 solids (baked)
FEATURE [Part::Feature] Face146
  shape: bbox 3.5 x 17.8 x 2e-07 mm, 1 faces, 0 solids (baked)
FEATURE [Part::Revolution] Revolve150  label="removeToCreateScrewAndThreadedInsertHole058"
  Angle = 360
  Axis = (0,1,0)
  Base = (0,0,0)
  FaceMakerClass = Part::FaceMakerBullseye
  Placement = pos=(12.5,0,62) rot=(0,0,1;0rad)
  Solid = false
  Source = -> Face146
  Symmetric = false
FEATURE [Part::Revolution] Revolve151  label="removeToCreateScrewAndThreadedInsertHole059"
  Angle = 360
  Axis = (0,1,0)
  Base = (0,0,0)
  FaceMakerClass = Part::FaceMakerBullseye
  Placement = pos=(89.5,0,68.5) rot=(0,0,1;0rad)
  Solid = false
  Source = -> Face143
  Symmetric = false
FEATURE [Part::Revolution] Revolve152  label="removeToCreateScrewAndThreadedInsertHole060"
  Angle = 360
  Axis = (0,1,0)
  Base = (0,0,0)
  FaceMakerClass = Part::FaceMakerBullseye
  Placement = pos=(89.5,0,3.5) rot=(0,0,1;0rad)
  Solid = false
  Source = -> Face142
  Symmetric = false
FEATURE [Part::Revolution] Revolve153  label="removeToCreateScrewAndThreadedInsertHole061"
  Angle = 360
  Axis = (0,1,0)
  Base = (0,0,0)
  FaceMakerClass = Part::FaceMakerBullseye
  Placement = pos=(109.5,4.7,3.5) rot=(0,0,1;0rad)
  Solid = false
  Source = -> Face145
  Symmetric = false
FEATURE [Part::Revolution] Revolve154  label="removeToCreateScrewAndThreadedInsertHole062"
  Angle = 360
  Axis = (0,1,0)
  Base = (0,0,0)
  FaceMakerClass = Part::FaceMakerBullseye
  Placement = pos=(109.5,4.7,68.5) rot=(0,0,1;0rad)
  Solid = false
  Source = -> Face144
  Symmetric = false
FEATURE [Part::MultiFuse] Fusion115  label="removeToCreateScrewAndThreadedInsertHole056"
  Shapes = -> [Revolve154,Revolve153,Revolve152,Revolve151,Revolve150,Revolve149]
FEATURE [Part::Feature] Face147
  shape: bbox 9.8 x 26.5 x 2e-07 mm, 1 faces, 0 solids (baked)
FEATURE [Part::Revolution] Revolve155
  Angle = 360
  Axis = (0,1,0)
  Base = (0,0,0)
  FaceMakerClass = Part::FaceMakerBullseye
  Placement = pos=(0,0,0) rot=(0,0,1;1.5708rad)
  Solid = false
  Source = -> Face147
  Symmetric = false
FEATURE [Part::Feature] Face148
  shape: bbox 9.8 x 26.5 x 2e-07 mm, 1 faces, 0 solids (baked)
FEATURE [Part::Revolution] Revolve156
  Angle = 360
  Axis = (0,1,0)
  Base = (0,0,0)
  FaceMakerClass = Part::FaceMakerBullseye
  Placement = pos=(0,0,0) rot=(0,0,1;1.5708rad)
  Solid = false
  Source = -> Face148
  Symmetric = false
FEATURE [Part::MultiFuse] Fusion116
  Placement = pos=(-18,19,36) rot=(0,0,1;0rad)
  Shapes = -> [Revolve156,Revolve155]
FEATURE [Part::Box] Box029  label="Cube016"
  AttacherType = Attacher::AttachEngine3D
  Height = 28
  Length = 3
  Placement = pos=(110.7,19,22) rot=(0,0,1;0rad)
  Width = 15.7
FEATURE [Part::Cylinder] Cylinder046
  Angle = 360
  AttacherType = Attacher::AttachEngine3D
  Height = 10
  Placement = pos=(0,0,36.15) rot=(0,0,1;0rad)
  Radius = 4
FEATURE [Part::Cylinder] Cylinder047
  Angle = 360
  AttacherType = Attacher::AttachEngine3D
  Height = 20
  Placement = pos=(0,0,36.15) rot=(0,0,1;0rad)
  Radius = 10.3
FEATURE [Part::MultiFuse] Fusion117  label="removeToCreteHoleForPlugHousing041"
  Placement = pos=(70,19,36) rot=(0,1,0;1.5708rad)
  Shapes = -> [Cylinder047,Cylinder046]
FEATURE [Part::Cut] Cut049  label="plugHousingTab004"
  Base = -> Box029
  Placement = pos=(-107.4,-14,0) rot=(0,0,1;0rad)
  Tool = -> Fusion117
FEATURE [Part::Box] Box030  label="Cube017"
  AttacherType = Attacher::AttachEngine3D
  Height = 28
  Length = 3
  Placement = pos=(110.7,19,22) rot=(0,0,1;0rad)
  Width = 15.7
FEATURE [Part::Cylinder] Cylinder048
  Angle = 360
  AttacherType = Attacher::AttachEngine3D
  Height = 10
  Placement = pos=(0,0,36.15) rot=(0,0,1;0rad)
  Radius = 4
FEATURE [Part::Cylinder] Cylinder049
  Angle = 360
  AttacherType = Attacher::AttachEngine3D
  Height = 20
  Placement = pos=(0,0,36.15) rot=(0,0,1;0rad)
  Radius = 10.3
FEATURE [Part::MultiFuse] Fusion118  label="removeToCreteHoleForPlugHousing042"
  Placement = pos=(70,19,36) rot=(0,1,0;1.5708rad)
  Shapes = -> [Cylinder049,Cylinder048]
FEATURE [Part::Cut] Cut050  label="plugHousingTab005"
  Base = -> Box030
  Placement = pos=(-107.4,-14,0) rot=(0,0,1;0rad)
  Tool = -> Fusion118
FEATURE [Part::MultiFuse] Fusion119
  Placement = pos=(9.6,23,0) rot=(0,0,1;3.14159rad)
  Shapes = -> [Cut049,Cut050]
FEATURE [Part::Box] Box031  label="Cube018"
  AttacherType = Attacher::AttachEngine3D
  Height = 10
  Length = 3
  Placement = pos=(3.3,4,12) rot=(0,0,1;0rad)
  Width = 10
FEATURE [Part::Fillet] Fillet044
  Base = -> Box031
  Edges = 1 edges r=2: [Edge11]
FEATURE [Part::Box] Box032  label="Cube019"
  AttacherType = Attacher::AttachEngine3D
  Height = 10
  Length = 3
  Placement = pos=(3.3,4,50) rot=(0,0,1;0rad)
  Width = 10
FEATURE [Part::Fillet] Fillet045
  Base = -> Box032
  Edges = 1 edges r=2: [Edge12]
FEATURE [Part::Box] Box033  label="Cube020"
  AttacherType = Attacher::AttachEngine3D
  Height = 28
  Length = 4
  Placement = pos=(5,0,22) rot=(0,0,1;0rad)
  Width = 10
FEATURE [Part::Fillet] Fillet046
  Base = -> Box033
  Edges = 1 edges r=1: [Edge7]
FEATURE [Part::Fillet] Fillet047
  Base = -> Fillet046
  Edges = 1 edges r=2: [Edge5]
FEATURE [Part::Fillet] Fillet048
  Base = -> Fillet047
  Edges = 1 edges r=2: [Edge2]
FEATURE [Part::Cylinder] Cylinder050
  Angle = 360
  AttacherType = Attacher::AttachEngine3D
  Height = 20
  Placement = pos=(0,0,36.15) rot=(0,0,1;0rad)
  Radius = 8.2
FEATURE [Part::Cylinder] Cylinder051
  Angle = 360
  AttacherType = Attacher::AttachEngine3D
  Height = 10
  Placement = pos=(0,0,36.15) rot=(0,0,1;0rad)
  Radius = 4
FEATURE [Part::MultiFuse] Fusion120  label="removeToCreteHoleForPlugHousing043"
  Placement = pos=(-42,19,36) rot=(0,1,0;1.5708rad)
  Shapes = -> [Cylinder050,Cylinder051]
FEATURE [Sketcher::SketchObject] Sketch067  label="topSketch018"
  FullyConstrained = true
  sketch-geometry (4):
    g0: LineSegment StartX=16.8446 StartY=31.512 StartZ=0 EndX=16.3251 EndY=34.4666 EndZ=0
    g1: ArcOfCircle CenterX=19 CenterY=19.2524 CenterZ=0 NormalX=0 NormalY=0 NormalZ=1 AngleXU=0 Radius=15.4476 StartAngle=1.74483 EndAngle=2.72717
    g2: ArcOfCircle CenterX=19 CenterY=19.2524 CenterZ=0 NormalX=0 NormalY=0 NormalZ=1 AngleXU=0 Radius=12.4476 StartAngle=1.74483 EndAngle=2.73189
    g3: LineSegment StartX=4.86004 StartY=25.4725 StartZ=0 EndX=7.58253 EndY=24.2107 EndZ=0
  constraints (7):
    c: Block(g0)
    c: Coincident(g1,g0)
    c: Coincident(g2,g0)
    c: Coincident(g3,g1)
    c: Coincident(g3,g2)
    c: Block(g1)
    c: Block(g2)
FEATURE [Part::Extrusion] Extrude058
  Base = -> Sketch067
  Dir = (0,0,1)
  DirMode = 2
  FaceMakerClass = Part::FaceMakerBullseye
  LengthFwd = 10
  LengthRev = 0
  Placement = pos=(0,0,31) rot=(0,0,1;0rad)
  Solid = true
  Symmetric = false
FEATURE [Part::Cut] Cut051
  Base = -> Extrude058
  Tool = -> Fusion120
FEATURE [Part::Fillet] Fillet049
  Base = -> Cut051
  Edges = 1 edges r=2: [Edge1]
FEATURE [Part::Fillet] Fillet050
  Base = -> Fillet049
  Edges = 1 edges r=2.5: [Edge1]
FEATURE [Part::Fillet] Fillet051
  Base = -> Fillet050
  Edges = 1 edges r=2.5: [Edge2]
FEATURE [Part::MultiFuse] Fusion121  label="wireHolder003"
  Shapes = -> [Fusion116,Fillet051]
FEATURE [Part::MultiFuse] Fusion122
  Shapes = -> [Fillet045,Fusion121]
FEATURE [Part::MultiFuse] Fusion123  label="wireHolder004"
  Shapes = -> [Fusion122,Fillet048]
FEATURE [Part::MultiFuse] Fusion124  label="wireHolder005"
  Shapes = -> [Fillet044,Fusion119,Fusion123]
FEATURE [Sketcher::SketchObject] Sketch068  label="topSketch019"
  FullyConstrained = true
  sketch-geometry (6):
    g0: LineSegment StartX=19 StartY=38 StartZ=0 EndX=117 EndY=38 EndZ=0
    g1: ArcOfCircle CenterX=19 CenterY=19 CenterZ=0 NormalX=0 NormalY=0 NormalZ=1 AngleXU=0 Radius=19 StartAngle=1.5708 EndAngle=3.14159
    g2: LineSegment StartX=117 StartY=38 StartZ=0 EndX=117 EndY=19 EndZ=0
    g3: LineSegment StartX=98 StartY=1.0161e-12 StartZ=0 EndX=5.22862e-06 EndY=1.0161e-12 EndZ=0
    g4: LineSegment StartX=5.22862e-06 StartY=19 StartZ=0 EndX=5.22862e-06 EndY=1.0161e-12 EndZ=0
    g5: ArcOfCircle CenterX=98 CenterY=19 CenterZ=0 NormalX=0 NormalY=0 NormalZ=1 AngleXU=0 Radius=19 StartAngle=4.71239 EndAngle=6.28319
  constraints (16):
    c: Horizontal(g0)
    c: Distance(g0) = 98
    c: Coincident(g1,g0)
    c: Block(g1)
    c: Coincident(g2,g0)
    c: Vertical(g2)
    c: Distance(g2) = 19
    c: Horizontal(g3)
    c: Coincident(g4,g1)
    c: Vertical(g4)
    c: Coincident(g3,g4)
    c: Block(g3)
    c: Coincident(g5,g2)
    c: Coincident(g5,g3)
    c: Block(g0)
    c: Block(g5)
FEATURE [Part::Extrusion] Extrude059  label="sideA002"
  Base = -> Sketch068
  Dir = (0,0,1)
  DirMode = 2
  FaceMakerClass = Part::FaceMakerBullseye
  LengthFwd = 3
  LengthRev = 0
  Placement = pos=(0,0,-2.7) rot=(0,0,1;0rad)
  Solid = true
  Symmetric = false
FEATURE [Sketcher::SketchObject] Sketch069  label="topSketch020"
  FullyConstrained = true
  sketch-geometry (6):
    g0: LineSegment StartX=19 StartY=38 StartZ=0 EndX=117 EndY=38 EndZ=0
    g1: ArcOfCircle CenterX=19 CenterY=19 CenterZ=0 NormalX=0 NormalY=0 NormalZ=1 AngleXU=0 Radius=19 StartAngle=1.5708 EndAngle=3.14159
    g2: LineSegment StartX=117 StartY=38 StartZ=0 EndX=117 EndY=19 EndZ=0
    g3: LineSegment StartX=98 StartY=1.0161e-12 StartZ=0 EndX=5.22862e-06 EndY=1.0161e-12 EndZ=0
    g4: LineSegment StartX=5.22862e-06 StartY=19 StartZ=0 EndX=5.22862e-06 EndY=1.0161e-12 EndZ=0
    g5: ArcOfCircle CenterX=98 CenterY=19 CenterZ=0 NormalX=0 NormalY=0 NormalZ=1 AngleXU=0 Radius=19 StartAngle=4.71239 EndAngle=6.28319
  constraints (16):
    c: Horizontal(g0)
    c: Distance(g0) = 98
    c: Coincident(g1,g0)
    c: Block(g1)
    c: Coincident(g2,g0)
    c: Vertical(g2)
    c: Distance(g2) = 19
    c: Horizontal(g3)
    c: Coincident(g4,g1)
    c: Vertical(g4)
    c: Coincident(g3,g4)
    c: Block(g3)
    c: Coincident(g5,g2)
    c: Coincident(g5,g3)
    c: Block(g0)
    c: Block(g5)
FEATURE [Part::Extrusion] Extrude060  label="sideB002"
  Base = -> Sketch069
  Dir = (0,0,1)
  DirMode = 2
  FaceMakerClass = Part::FaceMakerBullseye
  LengthFwd = 3
  LengthRev = 0
  Placement = pos=(0,0,71.7) rot=(0,0,1;0rad)
  Solid = true
  Symmetric = false
FEATURE [Part::MultiFuse] Fusion127  label="removeFromBottom001"
  Placement = pos=(2,0,0) rot=(0,0,1;0rad)
  Shapes = -> [Extrude059,Extrude060]
FEATURE [Part::Cylinder] Cylinder052
  Angle = 360
  AttacherType = Attacher::AttachEngine3D
  Height = 20
  Placement = pos=(0,0,36.15) rot=(0,0,1;0rad)
  Radius = 14
FEATURE [Part::Cylinder] Cylinder053
  Angle = 360
  AttacherType = Attacher::AttachEngine3D
  Height = 10
  Placement = pos=(0,0,36.15) rot=(0,0,1;0rad)
  Radius = 4
FEATURE [Part::MultiFuse] Fusion128  label="removeToCreteHoleForPlugHousing044"
  Placement = pos=(70,19,36) rot=(0,1,0;1.5708rad)
  Shapes = -> [Cylinder052,Cylinder053]
FEATURE [Part::Cut] Cut052  label="bottom011"
  Base = -> Extrude043
  Tool = -> Fusion128
FEATURE [Part::Cut] Cut054  label="bottom012"
  Base = -> Cut052
  Tool = -> Fusion115
FEATURE [Sketcher::SketchObject] Sketch070
  FullyConstrained = true
  Placement = pos=(117,19,0) rot=(0.57735,0.57735,0.57735;2.0944rad)
  sketch-geometry (48):
    g0: LineSegment StartX=-49.19 StartY=69.25 StartZ=0 EndX=-49.19 EndY=66.25 EndZ=0
    g1: LineSegment StartX=-49.19 StartY=63.5 StartZ=0 EndX=-49.19 EndY=60.5 EndZ=0
    g2: LineSegment StartX=-49.19 StartY=57.75 StartZ=0 EndX=-49.19 EndY=54.75 EndZ=0
    g3: LineSegment StartX=-49.19 StartY=52 StartZ=0 EndX=-49.19 EndY=49 EndZ=0
    g4: LineSegment StartX=-49.19 StartY=46.25 StartZ=0 EndX=-49.19 EndY=43.25 EndZ=0
    g5: LineSegment StartX=-49.19 StartY=40.5 StartZ=0 EndX=-49.19 EndY=37.5 EndZ=0
    g6: LineSegment StartX=-49.19 StartY=34.5 StartZ=0 EndX=-49.19 EndY=31.5 EndZ=0
    g7: LineSegment StartX=-49.19 StartY=28.75 StartZ=0 EndX=-49.19 EndY=25.75 EndZ=0
    g8: LineSegment StartX=-49.19 StartY=23 StartZ=0 EndX=-49.19 EndY=20 EndZ=0
    g9: LineSegment StartX=-49.19 StartY=17.25 StartZ=0 EndX=-49.19 EndY=14.25 EndZ=0
    g10: LineSegment StartX=-49.19 StartY=11.5 StartZ=0 EndX=-49.19 EndY=8.5 EndZ=0
    g11: LineSegment StartX=-49.19 StartY=5.75 StartZ=0 EndX=-49.19 EndY=2.75 EndZ=0
    g12: ArcOfCircle CenterX=-1.5 CenterY=67.75 CenterZ=0 NormalX=0 NormalY=0 NormalZ=1 AngleXU=0 Radius=1.5 StartAngle=4.71239 EndAngle=7.85398
    g13: ArcOfCircle CenterX=-1.5 CenterY=62 CenterZ=0 NormalX=0 NormalY=0 NormalZ=1 AngleXU=0 Radius=1.5 StartAngle=4.71239 EndAngle=7.85398
    g14: ArcOfCircle CenterX=-1.5 CenterY=56.25 CenterZ=0 NormalX=0 NormalY=0 NormalZ=1 AngleXU=0 Radius=1.5 StartAngle=4.71239 EndAngle=7.85398
    g15: ArcOfCircle CenterX=-11.49 CenterY=50.5 CenterZ=0 NormalX=0 NormalY=0 NormalZ=1 AngleXU=0 Radius=1.5 StartAngle=4.71239 EndAngle=7.85398
    g16: ArcOfCircle CenterX=-16.28 CenterY=44.75 CenterZ=0 NormalX=0 NormalY=0 NormalZ=1 AngleXU=0 Radius=1.5 StartAngle=4.71239 EndAngle=7.85398
    g17: ArcOfCircle CenterX=-18.2337 CenterY=39 CenterZ=0 NormalX=0 NormalY=0 NormalZ=1 AngleXU=0 Radius=1.5 StartAngle=4.71485 EndAngle=7.85398
    g18: ArcOfCircle CenterX=-16.2837 CenterY=27.25 CenterZ=0 NormalX=0 NormalY=0 NormalZ=1 AngleXU=0 Radius=1.5 StartAngle=4.71485 EndAngle=7.85398
    g19: ArcOfCircle CenterX=-18.2337 CenterY=33 CenterZ=0 NormalX=0 NormalY=0 NormalZ=1 AngleXU=0 Radius=1.5 StartAngle=4.71485 EndAngle=7.85398
    g20: ArcOfCircle CenterX=-11.49 CenterY=21.5 CenterZ=0 NormalX=0 NormalY=0 NormalZ=1 AngleXU=0 Radius=1.5 StartAngle=4.71239 EndAngle=7.85398
    g21: ArcOfCircle CenterX=-1.5 CenterY=4.25 CenterZ=0 NormalX=0 NormalY=0 NormalZ=1 AngleXU=0 Radius=1.5 StartAngle=4.71239 EndAngle=7.85398
    g22: ArcOfCircle CenterX=-1.5 CenterY=10 CenterZ=0 NormalX=0 NormalY=0 NormalZ=1 AngleXU=0 Radius=1.5 StartAngle=4.71239 EndAngle=7.85398
    g23: ArcOfCircle CenterX=-1.5 CenterY=15.75 CenterZ=0 NormalX=0 NormalY=0 NormalZ=1 AngleXU=0 Radius=1.5 StartAngle=4.71239 EndAngle=7.85398
    g24: LineSegment StartX=-49.19 StartY=69.25 StartZ=0 EndX=-1.5 EndY=69.25 EndZ=0
    g25: LineSegment StartX=-49.19 StartY=66.25 StartZ=0 EndX=-1.5 EndY=66.25 EndZ=0
    g26: LineSegment StartX=-49.19 StartY=63.5 StartZ=0 EndX=-1.5 EndY=63.5 EndZ=0
    g27: LineSegment StartX=-49.19 StartY=60.5 StartZ=0 EndX=-1.5 EndY=60.5 EndZ=0
    g28: LineSegment StartX=-49.19 StartY=57.75 StartZ=0 EndX=-1.5 EndY=57.75 EndZ=0
    g29: LineSegment StartX=-49.19 StartY=54.75 StartZ=0 EndX=-1.5 EndY=54.75 EndZ=0
    g30: LineSegment StartX=-49.19 StartY=52 StartZ=0 EndX=-11.49 EndY=52 EndZ=0
    g31: LineSegment StartX=-49.19 StartY=49 StartZ=0 EndX=-11.49 EndY=49 EndZ=0
    g32: LineSegment StartX=-49.19 StartY=46.25 StartZ=0 EndX=-16.28 EndY=46.25 EndZ=0
    g33: LineSegment StartX=-49.19 StartY=43.25 StartZ=0 EndX=-16.28 EndY=43.25 EndZ=0
    g34: LineSegment StartX=-49.19 StartY=40.5 StartZ=0 EndX=-18.2337 EndY=40.5 EndZ=0
    g35: LineSegment StartX=-49.19 StartY=37.5 StartZ=0 EndX=-18.23 EndY=37.5 EndZ=0
    g36: LineSegment StartX=-49.19 StartY=34.5 StartZ=0 EndX=-18.2337 EndY=34.5 EndZ=0
    g37: LineSegment StartX=-49.19 StartY=31.5 StartZ=0 EndX=-18.23 EndY=31.5 EndZ=0
    g38: LineSegment StartX=-49.19 StartY=28.75 StartZ=0 EndX=-16.2837 EndY=28.75 EndZ=0
    g39: LineSegment StartX=-49.19 StartY=25.75 StartZ=0 EndX=-16.28 EndY=25.75 EndZ=0
    g40: LineSegment StartX=-49.19 StartY=23 StartZ=0 EndX=-11.49 EndY=23 EndZ=0
    g41: LineSegment StartX=-49.19 StartY=20 StartZ=0 EndX=-11.49 EndY=20 EndZ=0
    g42: LineSegment StartX=-49.19 StartY=17.25 StartZ=0 EndX=-1.5 EndY=17.25 EndZ=0
    g43: LineSegment StartX=-49.19 StartY=14.25 StartZ=0 EndX=-1.5 EndY=14.25 EndZ=0
    g44: LineSegment StartX=-49.19 StartY=11.5 StartZ=0 EndX=-1.5 EndY=11.5 EndZ=0
    g45: LineSegment StartX=-49.19 StartY=8.5 StartZ=0 EndX=-1.5 EndY=8.5 EndZ=0
    g46: LineSegment StartX=-49.19 StartY=5.75 StartZ=0 EndX=-1.5 EndY=5.75 EndZ=0
    g47: LineSegment StartX=-49.19 StartY=2.75 StartZ=0 EndX=-1.5 EndY=2.75 EndZ=0
  constraints (120):
    c: Vertical(g0)
    c: Distance(g0) = 3
    c: Block(g0)
    c: Vertical(g1)
    c: Distance(g1) = 3
    c: Vertical(g2)
    c: Equal(g0,g2) = 3
    c: Block(g2)
    c: Vertical(g3)
    c: Equal(g1,g3) = 3
    c: Vertical(g4)
    c: Equal(g0,g4) = 3
    c: Block(g4)
    c: Vertical(g5)
    c: Equal(g1,g5) = 3
    c: Vertical(g6)
    c: Equal(g0,g6) = 3
    c: Block(g6)
    c: Vertical(g7)
    c: Equal(g1,g7) = 3
    c: Vertical(g8)
    c: Equal(g0,g8) = 3
    c: Block(g8)
    c: Vertical(g9)
    c: Equal(g1,g9) = 3
    c: Vertical(g10)
    c: Equal(g0,g10) = 3
    c: Block(g10)
    c: Vertical(g11)
    c: Equal(g1,g11) = 3
    c: Block(g12)
    c: Block(g13)
    c: Block(g14)
    c: Block(g15)
    c: Block(g16)
    c: Block(g17)
    c: Block(g18)
    c: Block(g19)
    c: Block(g20)
    c: Block(g21)
    c: Block(g22)
    c: Block(g23)
    c: Block(g11)
    c: Block(g9)
    c: Block(g7)
    c: Block(g5)
    c: Block(g3)
    c: Block(g1)
    c: Coincident(g24,g0)
    c: Coincident(g24,g12)
    c: Horizontal(g24)
    c: Coincident(g25,g0)
    c: Coincident(g25,g12)
    c: Horizontal(g25)
    c: Coincident(g26,g1)
    c: Coincident(g26,g13)
    c: Horizontal(g26)
    c: Coincident(g27,g1)
    c: Coincident(g27,g13)
    c: Horizontal(g27)
    c: Coincident(g28,g2)
    c: Coincident(g28,g14)
    c: Horizontal(g28)
    c: Coincident(g29,g2)
    c: Coincident(g29,g14)
    c: Horizontal(g29)
    c: Coincident(g30,g3)
    c: Coincident(g30,g15)
    c: Horizontal(g30)
    c: Coincident(g31,g3)
    c: Coincident(g31,g15)
    c: Horizontal(g31)
    c: Coincident(g32,g4)
    c: Coincident(g32,g16)
    c: Horizontal(g32)
    c: Coincident(g33,g4)
    c: Coincident(g33,g16)
    c: Horizontal(g33)
    c: Coincident(g34,g5)
    c: Coincident(g34,g17)
    c: Horizontal(g34)
    c: Coincident(g35,g5)
    c: Coincident(g35,g17)
    c: Horizontal(g35)
    c: Coincident(g36,g6)
    c: Coincident(g36,g19)
    c: Horizontal(g36)
    c: Coincident(g37,g6)
    c: Coincident(g37,g19)
    c: Horizontal(g37)
    c: Coincident(g38,g7)
    c: Coincident(g38,g18)
    c: Horizontal(g38)
    c: Coincident(g39,g7)
    c: Coincident(g39,g18)
    c: Horizontal(g39)
    c: Coincident(g40,g8)
    c: Coincident(g40,g20)
    c: Horizontal(g40)
    c: Coincident(g41,g8)
    c: Coincident(g41,g20)
    c: Horizontal(g41)
    c: Coincident(g42,g9)
    c: Coincident(g42,g23)
    c: Horizontal(g42)
    c: Coincident(g43,g9)
    c: Coincident(g43,g23)
    c: Horizontal(g43)
    c: Coincident(g44,g10)
    c: Coincident(g44,g22)
    c: Horizontal(g44)
    c: Coincident(g45,g10)
    c: Coincident(g45,g22)
    c: Horizontal(g45)
    c: Coincident(g46,g11)
    c: Coincident(g46,g21)
    c: Horizontal(g46)
    c: Coincident(g47,g11)
    c: Coincident(g47,g21)
    c: Horizontal(g47)
FEATURE [Part::Extrusion] Extrude061
  Base = -> Sketch070
  Dir = (1,0,0)
  DirMode = 2
  FaceMakerClass = Part::FaceMakerBullseye
  LengthFwd = 23
  LengthRev = 0
  Placement = pos=(-19,0,0) rot=(0,0,1;0rad)
  Solid = true
  Symmetric = false
FEATURE [Part::Fillet] Fillet052  label="removeToCreateVentalationHoles002"
  Base = -> Extrude061
  Edges = <same value as first occurrence — deduplicated (x6 in doc)>
  Placement = pos=(7,0.02,0) rot=(0,0,1;0rad)
FEATURE [Part::MultiFuse] Fusion130  label="bottom013"
  Shapes = -> [Cut054,Cut034]
FEATURE [Part::Cut] Cut055
  Base = -> Fusion130
  Tool = -> Fillet052
FEATURE [Part::Cylinder] Cylinder054
  Angle = 360
  AttacherType = Attacher::AttachEngine3D
  Height = 20
  Placement = pos=(0,0,36.15) rot=(0,0,1;0rad)
  Radius = 4
FEATURE [Sketcher::SketchObject] Sketch071  label="bottomSketch002"
  FullyConstrained = true
  sketch-geometry (32):
    g0: LineSegment StartX=3.3 StartY=-6.03275e-07 StartZ=0 EndX=98 EndY=-6.03275e-07 EndZ=0
    g1: ArcOfCircle CenterX=98 CenterY=19 CenterZ=0 NormalX=0 NormalY=0 NormalZ=1 AngleXU=0 Radius=19 StartAngle=4.71239 EndAngle=5.71103
    g2: LineSegment StartX=6.3 StartY=8 StartZ=0 EndX=3.3 EndY=8 EndZ=0
    g3: LineSegment StartX=3.3 StartY=8 StartZ=0 EndX=3.3 EndY=-6.03275e-07 EndZ=0
    g4: ArcOfCircle CenterX=8.3 CenterY=5 CenterZ=0 NormalX=0 NormalY=0 NormalZ=1 AngleXU=0 Radius=2 StartAngle=3.14159 EndAngle=4.71239
    g5: LineSegment StartX=6.3 StartY=8 StartZ=0 EndX=6.3 EndY=5 EndZ=0
    g6: ArcOfCircle CenterX=98 CenterY=19 CenterZ=0 NormalX=0 NormalY=0 NormalZ=1 AngleXU=0 Radius=12.7 StartAngle=4.71239 EndAngle=6.28319
    g7: LineSegment StartX=94.7 StartY=3 StartZ=0 EndX=8.3 EndY=3 EndZ=0
    g8-g12: Circle x5 (B-spline internal-alignment scaffolding for g13; pole/knot coordinates omitted)
    g13: BSplineCurve PolesCount=5 KnotsCount=3 Degree=3 IsPeriodic=0
    g14: GeomPoint X=98 Y=6.3 Z=0
    g15: GeomPoint X=96.3938 Y=4.71946 Z=0
    g16: GeomPoint X=94.7 Y=3 Z=0
    g17-g23: Circle x7 (B-spline internal-alignment scaffolding for g24; pole/knot coordinates omitted)
    g24: BSplineCurve PolesCount=7 KnotsCount=5 Degree=3 IsPeriodic=0
    g25-g29: GeomPoint x5 (B-spline internal-alignment scaffolding for g24; pole/knot coordinates omitted)
    g30: ArcOfCircle CenterX=98 CenterY=19 CenterZ=0 NormalX=0 NormalY=0 NormalZ=1 AngleXU=0 Radius=15.7 StartAngle=5.81226 EndAngle=6.28319
    g31: LineSegment StartX=110.7 StartY=19 StartZ=0 EndX=113.7 EndY=19 EndZ=0
  constraints (41):
    c: Horizontal(g0)
    c: Coincident(g1,g0)
    c: Block(g1)
    c: Horizontal(g2)
    c: Distance(g2) = 3
    c: Coincident(g3,g2)
    c: Vertical(g3)
    c: Coincident(g3,g0)
    c: Block(g4)
    c: Block(g2)
    c: Coincident(g5,g2)
    c: Coincident(g5,g4)
    c: Vertical(g5)
    c: Coincident(g6,g1)
    c: Block(g6)
    c: Coincident(g7,g4)
    c: Horizontal(g7)
    c: Block(g0)
    c: Block(g7)
    c: Block(g3)
    c: Coincident(g13,g6)
    c: Weight(g8) = 1
    c: Equal(g8, g9-g12) x4
    c: Coincident(g13,g7)
    c: InternalAlignment(g8-g12 -> g13) x5
    c: InternalAlignment(g14,g13)
    c: InternalAlignment(g15,g13)
    c: InternalAlignment(g16,g13)
    c: Block(g13)
    c: Weight(g17) = 1
    c: Equal(g17, g18-g23) x6
    c: Coincident(g24,g1)
    c: InternalAlignment(g17-g23 -> g24) x7
    c: InternalAlignment(g25-g29 -> g24) x5
    c: Block(g24)
    c: Coincident(g30,g24)
    c: Coincident(g31,g6)
    c: Coincident(g31,g30)
    c: Horizontal(g31)
    c: Block(g31)
    c: Block(g30)
FEATURE [Part::Extrusion] Extrude062  label="bottom014"
  Base = -> Sketch071
  Dir = (0,0,1)
  DirMode = 2
  FaceMakerClass = Part::FaceMakerBullseye
  LengthFwd = 71.4
  LengthRev = 0
  Placement = pos=(0,0,0.3) rot=(0,0,1;0rad)
  Solid = true
  Symmetric = false
FEATURE [Part::Fillet] Fillet054
  Base = -> Extrude062
  Edges = 1 edges r=2.4: [Edge17]
FEATURE [Part::Fillet] Fillet055  label="bottom015"
  Base = -> Fillet054
  Edges = 1 edges r=2.4: [Edge36]
FEATURE [Part::Cylinder] Cylinder055
  Angle = 360
  AttacherType = Attacher::AttachEngine3D
  Height = 10
  Placement = pos=(0,0,36.15) rot=(0,0,1;0rad)
  Radius = 4
FEATURE [Part::MultiFuse] Fusion131  label="removeToCreateHoleForPlugHousing002"
  Placement = pos=(70,19,36.15) rot=(0,1,0;1.5708rad)
  Shapes = -> [Cylinder054,Cylinder055]
FEATURE [Part::Cut] Cut056  label="Bottom001"
  Base = -> Fillet055
  Placement = pos=(9,0,0) rot=(0,0,1;0rad)
  Tool = -> Fusion131
FEATURE [Part::Cut] Cut057
  Base = -> Cut055
  Tool = -> Cut056
FEATURE [Sketcher::SketchObject] Sketch072  label="topSketch021"
  FullyConstrained = true
  sketch-geometry (4):
    g0: ArcOfCircle CenterX=105 CenterY=19 CenterZ=0 NormalX=0 NormalY=0 NormalZ=1 AngleXU=0 Radius=20.6155 StartAngle=5.54125 EndAngle=6.28319
    g1: ArcOfCircle CenterX=105 CenterY=19 CenterZ=0 NormalX=0 NormalY=0 NormalZ=1 AngleXU=0 Radius=13 StartAngle=5.54125 EndAngle=6.28319
    g2: LineSegment StartX=118 StartY=19 StartZ=0 EndX=125.616 EndY=19 EndZ=0
    g3: LineSegment StartX=114.583 StartY=10.2157 StartZ=0 EndX=120.197 EndY=5.06982 EndZ=0
  constraints (7):
    c: Block(g0)
    c: Block(g1)
    c: Coincident(g2,g1)
    c: Coincident(g2,g0)
    c: Horizontal(g2)
    c: Coincident(g3,g1)
    c: Coincident(g3,g0)
FEATURE [Part::Extrusion] Extrude063  label="bottomPlugHousingBit003"
  Base = -> Sketch072
  Dir = (0,0,1)
  DirMode = 2
  FaceMakerClass = Part::FaceMakerBullseye
  LengthFwd = 72
  LengthRev = 0
  Solid = true
  Symmetric = false
FEATURE [Part::Cylinder] Cylinder056
  Angle = 360
  AttacherType = Attacher::AttachEngine3D
  Height = 20
  Placement = pos=(0,0,36.15) rot=(0,0,1;0rad)
  Radius = 14.3
FEATURE [Part::Cylinder] Cylinder057
  Angle = 360
  AttacherType = Attacher::AttachEngine3D
  Height = 10
  Placement = pos=(0,0,36.15) rot=(0,0,1;0rad)
  Radius = 4
FEATURE [Part::Box] Box034  label="removeToCreteHoleForPlugHousing047"
  AttacherType = Attacher::AttachEngine3D
  Height = 28.6
  Length = 20
  Placement = pos=(106.15,0,21.7) rot=(0,0,1;0rad)
  Width = 19
FEATURE [Part::Cylinder] Cylinder058
  Angle = 360
  AttacherType = Attacher::AttachEngine3D
  Height = 20
  Placement = pos=(0,0,36.15) rot=(0,0,1;0rad)
  Radius = 14.3
FEATURE [Part::Cylinder] Cylinder059
  Angle = 360
  AttacherType = Attacher::AttachEngine3D
  Height = 10
  Placement = pos=(0,0,36.15) rot=(0,0,1;0rad)
  Radius = 4
FEATURE [Part::MultiFuse] Fusion134  label="removeToCreteHoleForPlugHousing046"
  Placement = pos=(70,19,36) rot=(0,1,0;1.5708rad)
  Shapes = -> [Cylinder058,Cylinder059]
FEATURE [Part::Cylinder] Cylinder060
  Angle = 360
  AttacherType = Attacher::AttachEngine3D
  Height = 20
  Placement = pos=(0,0,36.15) rot=(0,0,1;0rad)
  Radius = 14
FEATURE [Part::Cylinder] Cylinder061
  Angle = 360
  AttacherType = Attacher::AttachEngine3D
  Height = 10
  Placement = pos=(0,0,36.15) rot=(0,0,1;0rad)
  Radius = 4
FEATURE [Part::MultiFuse] Fusion135  label="removeToCreteHoleForPlugHousing048"
  Placement = pos=(70,19,36) rot=(0,1,0;1.5708rad)
  Shapes = -> [Cylinder060,Cylinder061]
FEATURE [Part::Box] Box035  label="removeToCreteHoleForPlugHousing049"
  AttacherType = Attacher::AttachEngine3D
  Height = 28.6
  Length = 20
  Placement = pos=(106.15,0,21.7) rot=(0,0,1;0rad)
  Width = 19
FEATURE [Part::MultiFuse] Fusion133  label="removeToCreteHoleForPlugHousing045"
  Placement = pos=(0,0,-28.3) rot=(0,0,1;0rad)
  Shapes = -> [Box035,Fusion134]
FEATURE [Part::MultiFuse] Fusion138  label="removeToCreteHoleForPlugHousing051"
  Placement = pos=(70,19,36) rot=(0,1,0;1.5708rad)
  Shapes = -> [Cylinder056,Cylinder057]
FEATURE [Part::MultiFuse] Fusion137  label="removeToCreteHoleForPlugHousing050"
  Placement = pos=(0,0,28.3) rot=(0,0,1;0rad)
  Shapes = -> [Box034,Fusion138]
FEATURE [Part::MultiFuse] Fusion132  label="removeToCreatePlugHousingBottomBit002"
  Shapes = -> [Fusion133,Fusion137]
FEATURE [Part::MultiFuse] Fusion136  label="removeToCreatePlugHousingBottomBit003"
  Shapes = -> [Fusion135,Fusion132]
FEATURE [Part::Cut] Cut058  label="bottomPlugHousingBit002"
  Base = -> Extrude063
  Placement = pos=(-0.09,0,0) rot=(0,0,1;0rad)
  Tool = -> Fusion136
FEATURE [Sketcher::SketchObject] Sketch073  label="bottomSketch003"
  FullyConstrained = true
  sketch-geometry (45):
    g0: LineSegment StartX=6.29999 StartY=8 StartZ=0 EndX=3.29999 EndY=8 EndZ=0
    g1: LineSegment StartX=3.29999 StartY=8 StartZ=0 EndX=3.29999 EndY=-6.03275e-07 EndZ=0
    g2: ArcOfCircle CenterX=8.29999 CenterY=5 CenterZ=0 NormalX=0 NormalY=0 NormalZ=1 AngleXU=0 Radius=2 StartAngle=3.14159 EndAngle=4.71239
    g3: LineSegment StartX=6.29999 StartY=8 StartZ=0 EndX=6.29999 EndY=5 EndZ=0
    g4: ArcOfCircle CenterX=105 CenterY=19 CenterZ=0 NormalX=0 NormalY=0 NormalZ=1 AngleXU=0 Radius=12.7 StartAngle=4.71239 EndAngle=5.94289
    g5-g11: Circle x7 (B-spline internal-alignment scaffolding for g12; pole/knot coordinates omitted)
    g12: BSplineCurve PolesCount=7 KnotsCount=5 Degree=3 IsPeriodic=0
    g13-g17: GeomPoint x5 (B-spline internal-alignment scaffolding for g12; pole/knot coordinates omitted)
    g18: ArcOfCircle CenterX=105 CenterY=19 CenterZ=0 NormalX=0 NormalY=0 NormalZ=1 AngleXU=0 Radius=15.7 StartAngle=5.81226 EndAngle=6.28319
    g19: BSplineCurve PolesCount=5 KnotsCount=3 Degree=3 IsPeriodic=0
    g20: LineSegment StartX=8.29999 StartY=3 StartZ=0 EndX=101.7 EndY=3 EndZ=0
    g21: LineSegment StartX=3.29999 StartY=-6.03275e-07 StartZ=0 EndX=105 EndY=-6.03275e-07 EndZ=0
    g22: LineSegment StartX=120.974 StartY=8.71251 StartZ=0 EndX=122.332 EndY=7.83778 EndZ=0
    g23: LineSegment StartX=105 StartY=-6.03274e-07 StartZ=0 EndX=113 EndY=-6.03274e-07 EndZ=0
    g24: ArcOfCircle CenterX=105 CenterY=19 CenterZ=0 NormalX=0 NormalY=0 NormalZ=1 AngleXU=0 Radius=20.6155 StartAngle=5.11091 EndAngle=5.71103
    g25: ArcOfCircle CenterX=117.7 CenterY=19 CenterZ=0 NormalX=0 NormalY=0 NormalZ=1 AngleXU=0 Radius=3 StartAngle=1.2e-15 EndAngle=2.10468
    g26: Circle CenterX=116.345 CenterY=16.3232 CenterZ=0 NormalX=0 NormalY=0 NormalZ=1 AngleXU=0 Radius=1
    g27: Circle CenterX=117.24 CenterY=15.7584 CenterZ=0 NormalX=0 NormalY=0 NormalZ=1 AngleXU=0 Radius=1
    g28: Circle CenterX=116.972 CenterY=14.7612 CenterZ=0 NormalX=0 NormalY=0 NormalZ=1 AngleXU=0 Radius=1
    g29: BSplineCurve PolesCount=3 KnotsCount=2 Degree=2 IsPeriodic=0
    g30: GeomPoint X=116.345 Y=16.3232 Z=0
    g31: GeomPoint X=116.972 Y=14.7612 Z=0
    g32: Circle CenterX=115.828 CenterY=17.157 CenterZ=0 NormalX=0 NormalY=0 NormalZ=1 AngleXU=0 Radius=1
    g33: Circle CenterX=115.841 CenterY=16.639 CenterZ=0 NormalX=0 NormalY=0 NormalZ=1 AngleXU=0 Radius=1
    g34: Circle CenterX=116.345 CenterY=16.3232 CenterZ=0 NormalX=0 NormalY=0 NormalZ=1 AngleXU=0 Radius=1
    g35: BSplineCurve PolesCount=3 KnotsCount=2 Degree=2 IsPeriodic=0
    g36: GeomPoint X=115.828 Y=17.157 Z=0
    g37: GeomPoint X=116.345 Y=16.3232 Z=0
    g38: LineSegment StartX=115.828 StartY=17.157 StartZ=0 EndX=115.828 EndY=20.8307 EndZ=0
    g39: Circle CenterX=115.828 CenterY=20.8307 CenterZ=0 NormalX=0 NormalY=0 NormalZ=1 AngleXU=0 Radius=1
    g40: Circle CenterX=115.831 CenterY=21.3396 CenterZ=0 NormalX=0 NormalY=0 NormalZ=1 AngleXU=0 Radius=1
    g41: Circle CenterX=116.173 CenterY=21.5825 CenterZ=0 NormalX=0 NormalY=0 NormalZ=1 AngleXU=0 Radius=1
    g42: BSplineCurve PolesCount=3 KnotsCount=2 Degree=2 IsPeriodic=0
    g43: GeomPoint X=115.828 Y=20.8307 Z=0
    g44: GeomPoint X=116.173 Y=21.5825 Z=0
  constraints (70):
    c: Horizontal(g0)
    c: Distance(g0) = 3
    c: Coincident(g1,g0)
    c: Vertical(g1)
    c: Block(g2)
    c: Block(g0)
    c: Coincident(g3,g0)
    c: Coincident(g3,g2)
    c: Vertical(g3)
    c: Block(g1)
    c: Block(g4)
    c: Coincident(g19,g4)
    c: Block(g19)
    c: Equal(g5, g6-g11) x6
    c: InternalAlignment(g5-g11 -> g12) x7
    c: InternalAlignment(g13-g17 -> g12) x5
    c: Block(g12)
    c: Coincident(g18,g12)
    c: Block(g18)
    c: Coincident(g20,g2)
    c: Coincident(g20,g19)
    c: Horizontal(g20)
    c: Distance(g20) = 93.4
    c: Coincident(g21,g1)
    c: Horizontal(g21)
    c: Distance(g21) = 101.7
    c: Horizontal(g23)
    c: Distance(g23) = 8
    c: Coincident(g24,g23)
    c: Block(g23)
    c: Coincident(g22,g24)
    c: Block(g24)
    c: Block(g22)
    c: Distance(g22) = 1.61553
    c: Coincident(g25,g18)
    c: Block(g25)
    c: Weight(g26) = 1
    c: Equal(g26,g27)
    c: Equal(g26,g28)
    c: Coincident(g29,g4)
    c: InternalAlignment(g26,g29)
    c: InternalAlignment(g27,g29)
    c: InternalAlignment(g28,g29)
    c: InternalAlignment(g30,g29)
    c: InternalAlignment(g31,g29)
    c: Block(g29)
    c: Weight(g32) = 1
    c: Equal(g32,g33)
    c: Equal(g32,g34)
    c: Coincident(g35,g29)
    c: InternalAlignment(g32,g35)
    c: InternalAlignment(g33,g35)
    c: InternalAlignment(g34,g35)
    c: InternalAlignment(g36,g35)
    c: InternalAlignment(g37,g35)
    c: Block(g35)
    c: Coincident(g38,g35)
    c: Vertical(g38)
    c: Block(g38)
    c: Coincident(g42,g38)
    c: Weight(g39) = 1
    c: Equal(g39,g40)
    c: Equal(g39,g41)
    c: Coincident(g42,g25)
    c: InternalAlignment(g39,g42)
    c: InternalAlignment(g40,g42)
    c: InternalAlignment(g41,g42)
    c: InternalAlignment(g43,g42)
    c: InternalAlignment(g44,g42)
    c: Block(g42)
FEATURE [Part::Extrusion] Extrude064  label="bottom016"
  Base = -> Sketch073
  Dir = (0,0,1)
  DirMode = 2
  FaceMakerClass = Part::FaceMakerBullseye
  LengthFwd = 71.4
  LengthRev = 0
  Placement = pos=(0,0,0.3) rot=(0,0,1;0rad)
  Solid = true
  Symmetric = false
FEATURE [Part::Revolution] Revolve157  label="removeToCreateScrewAndThreadedInsertHole063"
  Angle = 360
  Axis = (0,1,0)
  Base = (0,0,0)
  FaceMakerClass = Part::FaceMakerBullseye
  Placement = pos=(12.5,0,10) rot=(0,0,1;0rad)
  Solid = false
  Source = -> Face141
  Symmetric = false
FEATURE [Sketcher::SketchObject] Sketch074
  FullyConstrained = true
  Placement = pos=(117,19,0) rot=(0.57735,0.57735,0.57735;2.0944rad)
  sketch-geometry (48):
    g0: LineSegment StartX=-49.19 StartY=69.25 StartZ=0 EndX=-49.19 EndY=66.25 EndZ=0
    g1: LineSegment StartX=-49.19 StartY=63.5 StartZ=0 EndX=-49.19 EndY=60.5 EndZ=0
    g2: LineSegment StartX=-49.19 StartY=57.75 StartZ=0 EndX=-49.19 EndY=54.75 EndZ=0
    g3: LineSegment StartX=-49.19 StartY=52 StartZ=0 EndX=-49.19 EndY=49 EndZ=0
    g4: LineSegment StartX=-49.19 StartY=46.25 StartZ=0 EndX=-49.19 EndY=43.25 EndZ=0
    g5: LineSegment StartX=-49.19 StartY=40.5 StartZ=0 EndX=-49.19 EndY=37.5 EndZ=0
    g6: LineSegment StartX=-49.19 StartY=34.5 StartZ=0 EndX=-49.19 EndY=31.5 EndZ=0
    g7: LineSegment StartX=-49.19 StartY=28.75 StartZ=0 EndX=-49.19 EndY=25.75 EndZ=0
    g8: LineSegment StartX=-49.19 StartY=23 StartZ=0 EndX=-49.19 EndY=20 EndZ=0
    g9: LineSegment StartX=-49.19 StartY=17.25 StartZ=0 EndX=-49.19 EndY=14.25 EndZ=0
    g10: LineSegment StartX=-49.19 StartY=11.5 StartZ=0 EndX=-49.19 EndY=8.5 EndZ=0
    g11: LineSegment StartX=-49.19 StartY=5.75 StartZ=0 EndX=-49.19 EndY=2.75 EndZ=0
    g12: ArcOfCircle CenterX=-1.5 CenterY=67.75 CenterZ=0 NormalX=0 NormalY=0 NormalZ=1 AngleXU=0 Radius=1.5 StartAngle=4.71239 EndAngle=7.85398
    g13: ArcOfCircle CenterX=-1.5 CenterY=62 CenterZ=0 NormalX=0 NormalY=0 NormalZ=1 AngleXU=0 Radius=1.5 StartAngle=4.71239 EndAngle=7.85398
    g14: ArcOfCircle CenterX=-1.5 CenterY=56.25 CenterZ=0 NormalX=0 NormalY=0 NormalZ=1 AngleXU=0 Radius=1.5 StartAngle=4.71239 EndAngle=7.85398
    g15: ArcOfCircle CenterX=-11.49 CenterY=50.5 CenterZ=0 NormalX=0 NormalY=0 NormalZ=1 AngleXU=0 Radius=1.5 StartAngle=4.71239 EndAngle=7.85398
    g16: ArcOfCircle CenterX=-16.28 CenterY=44.75 CenterZ=0 NormalX=0 NormalY=0 NormalZ=1 AngleXU=0 Radius=1.5 StartAngle=4.71239 EndAngle=7.85398
    g17: ArcOfCircle CenterX=-18.2337 CenterY=39 CenterZ=0 NormalX=0 NormalY=0 NormalZ=1 AngleXU=0 Radius=1.5 StartAngle=4.71485 EndAngle=7.85398
    g18: ArcOfCircle CenterX=-16.2837 CenterY=27.25 CenterZ=0 NormalX=0 NormalY=0 NormalZ=1 AngleXU=0 Radius=1.5 StartAngle=4.71485 EndAngle=7.85398
    g19: ArcOfCircle CenterX=-18.2337 CenterY=33 CenterZ=0 NormalX=0 NormalY=0 NormalZ=1 AngleXU=0 Radius=1.5 StartAngle=4.71485 EndAngle=7.85398
    g20: ArcOfCircle CenterX=-11.49 CenterY=21.5 CenterZ=0 NormalX=0 NormalY=0 NormalZ=1 AngleXU=0 Radius=1.5 StartAngle=4.71239 EndAngle=7.85398
    g21: ArcOfCircle CenterX=-1.5 CenterY=4.25 CenterZ=0 NormalX=0 NormalY=0 NormalZ=1 AngleXU=0 Radius=1.5 StartAngle=4.71239 EndAngle=7.85398
    g22: ArcOfCircle CenterX=-1.5 CenterY=10 CenterZ=0 NormalX=0 NormalY=0 NormalZ=1 AngleXU=0 Radius=1.5 StartAngle=4.71239 EndAngle=7.85398
    g23: ArcOfCircle CenterX=-1.5 CenterY=15.75 CenterZ=0 NormalX=0 NormalY=0 NormalZ=1 AngleXU=0 Radius=1.5 StartAngle=4.71239 EndAngle=7.85398
    g24: LineSegment StartX=-49.19 StartY=69.25 StartZ=0 EndX=-1.5 EndY=69.25 EndZ=0
    g25: LineSegment StartX=-49.19 StartY=66.25 StartZ=0 EndX=-1.5 EndY=66.25 EndZ=0
    g26: LineSegment StartX=-49.19 StartY=63.5 StartZ=0 EndX=-1.5 EndY=63.5 EndZ=0
    g27: LineSegment StartX=-49.19 StartY=60.5 StartZ=0 EndX=-1.5 EndY=60.5 EndZ=0
    g28: LineSegment StartX=-49.19 StartY=57.75 StartZ=0 EndX=-1.5 EndY=57.75 EndZ=0
    g29: LineSegment StartX=-49.19 StartY=54.75 StartZ=0 EndX=-1.5 EndY=54.75 EndZ=0
    g30: LineSegment StartX=-49.19 StartY=52 StartZ=0 EndX=-11.49 EndY=52 EndZ=0
    g31: LineSegment StartX=-49.19 StartY=49 StartZ=0 EndX=-11.49 EndY=49 EndZ=0
    g32: LineSegment StartX=-49.19 StartY=46.25 StartZ=0 EndX=-16.28 EndY=46.25 EndZ=0
    g33: LineSegment StartX=-49.19 StartY=43.25 StartZ=0 EndX=-16.28 EndY=43.25 EndZ=0
    g34: LineSegment StartX=-49.19 StartY=40.5 StartZ=0 EndX=-18.2337 EndY=40.5 EndZ=0
    g35: LineSegment StartX=-49.19 StartY=37.5 StartZ=0 EndX=-18.23 EndY=37.5 EndZ=0
    g36: LineSegment StartX=-49.19 StartY=34.5 StartZ=0 EndX=-18.2337 EndY=34.5 EndZ=0
    g37: LineSegment StartX=-49.19 StartY=31.5 StartZ=0 EndX=-18.23 EndY=31.5 EndZ=0
    g38: LineSegment StartX=-49.19 StartY=28.75 StartZ=0 EndX=-16.2837 EndY=28.75 EndZ=0
    g39: LineSegment StartX=-49.19 StartY=25.75 StartZ=0 EndX=-16.28 EndY=25.75 EndZ=0
    g40: LineSegment StartX=-49.19 StartY=23 StartZ=0 EndX=-11.49 EndY=23 EndZ=0
    g41: LineSegment StartX=-49.19 StartY=20 StartZ=0 EndX=-11.49 EndY=20 EndZ=0
    g42: LineSegment StartX=-49.19 StartY=17.25 StartZ=0 EndX=-1.5 EndY=17.25 EndZ=0
    g43: LineSegment StartX=-49.19 StartY=14.25 StartZ=0 EndX=-1.5 EndY=14.25 EndZ=0
    g44: LineSegment StartX=-49.19 StartY=11.5 StartZ=0 EndX=-1.5 EndY=11.5 EndZ=0
    g45: LineSegment StartX=-49.19 StartY=8.5 StartZ=0 EndX=-1.5 EndY=8.5 EndZ=0
    g46: LineSegment StartX=-49.19 StartY=5.75 StartZ=0 EndX=-1.5 EndY=5.75 EndZ=0
    g47: LineSegment StartX=-49.19 StartY=2.75 StartZ=0 EndX=-1.5 EndY=2.75 EndZ=0
  constraints (120):
    c: Vertical(g0)
    c: Distance(g0) = 3
    c: Block(g0)
    c: Vertical(g1)
    c: Distance(g1) = 3
    c: Vertical(g2)
    c: Equal(g0,g2) = 3
    c: Block(g2)
    c: Vertical(g3)
    c: Equal(g1,g3) = 3
    c: Vertical(g4)
    c: Equal(g0,g4) = 3
    c: Block(g4)
    c: Vertical(g5)
    c: Equal(g1,g5) = 3
    c: Vertical(g6)
    c: Equal(g0,g6) = 3
    c: Block(g6)
    c: Vertical(g7)
    c: Equal(g1,g7) = 3
    c: Vertical(g8)
    c: Equal(g0,g8) = 3
    c: Block(g8)
    c: Vertical(g9)
    c: Equal(g1,g9) = 3
    c: Vertical(g10)
    c: Equal(g0,g10) = 3
    c: Block(g10)
    c: Vertical(g11)
    c: Equal(g1,g11) = 3
    c: Block(g12)
    c: Block(g13)
    c: Block(g14)
    c: Block(g15)
    c: Block(g16)
    c: Block(g17)
    c: Block(g18)
    c: Block(g19)
    c: Block(g20)
    c: Block(g21)
    c: Block(g22)
    c: Block(g23)
    c: Block(g11)
    c: Block(g9)
    c: Block(g7)
    c: Block(g5)
    c: Block(g3)
    c: Block(g1)
    c: Coincident(g24,g0)
    c: Coincident(g24,g12)
    c: Horizontal(g24)
    c: Coincident(g25,g0)
    c: Coincident(g25,g12)
    c: Horizontal(g25)
    c: Coincident(g26,g1)
    c: Coincident(g26,g13)
    c: Horizontal(g26)
    c: Coincident(g27,g1)
    c: Coincident(g27,g13)
    c: Horizontal(g27)
    c: Coincident(g28,g2)
    c: Coincident(g28,g14)
    c: Horizontal(g28)
    c: Coincident(g29,g2)
    c: Coincident(g29,g14)
    c: Horizontal(g29)
    c: Coincident(g30,g3)
    c: Coincident(g30,g15)
    c: Horizontal(g30)
    c: Coincident(g31,g3)
    c: Coincident(g31,g15)
    c: Horizontal(g31)
    c: Coincident(g32,g4)
    c: Coincident(g32,g16)
    c: Horizontal(g32)
    c: Coincident(g33,g4)
    c: Coincident(g33,g16)
    c: Horizontal(g33)
    c: Coincident(g34,g5)
    c: Coincident(g34,g17)
    c: Horizontal(g34)
    c: Coincident(g35,g5)
    c: Coincident(g35,g17)
    c: Horizontal(g35)
    c: Coincident(g36,g6)
    c: Coincident(g36,g19)
    c: Horizontal(g36)
    c: Coincident(g37,g6)
    c: Coincident(g37,g19)
    c: Horizontal(g37)
    c: Coincident(g38,g7)
    c: Coincident(g38,g18)
    c: Horizontal(g38)
    c: Coincident(g39,g7)
    c: Coincident(g39,g18)
    c: Horizontal(g39)
    c: Coincident(g40,g8)
    c: Coincident(g40,g20)
    c: Horizontal(g40)
    c: Coincident(g41,g8)
    c: Coincident(g41,g20)
    c: Horizontal(g41)
    c: Coincident(g42,g9)
    c: Coincident(g42,g23)
    c: Horizontal(g42)
    c: Coincident(g43,g9)
    c: Coincident(g43,g23)
    c: Horizontal(g43)
    c: Coincident(g44,g10)
    c: Coincident(g44,g22)
    c: Horizontal(g44)
    c: Coincident(g45,g10)
    c: Coincident(g45,g22)
    c: Horizontal(g45)
    c: Coincident(g46,g11)
    c: Coincident(g46,g21)
    c: Horizontal(g46)
    c: Coincident(g47,g11)
    c: Coincident(g47,g21)
    c: Horizontal(g47)
FEATURE [Part::Extrusion] Extrude065
  Base = -> Sketch074
  Dir = (1,0,0)
  DirMode = 2
  FaceMakerClass = Part::FaceMakerBullseye
  LengthFwd = 23
  LengthRev = 0
  Placement = pos=(-19,0,0) rot=(0,0,1;0rad)
  Solid = true
  Symmetric = false
FEATURE [Part::Fillet] Fillet056  label="removeToCreateVentalationHoles003"
  Base = -> Extrude065
  Edges = <same value as first occurrence — deduplicated (x6 in doc)>
  Placement = pos=(7,0.02,0) rot=(0,0,1;0rad)
FEATURE [Part::Revolution] Revolve158  label="removeToCreateScrewAndThreadedInsertHole065"
  Angle = 360
  Axis = (0,1,0)
  Base = (0,0,0)
  FaceMakerClass = Part::FaceMakerBullseye
  Placement = pos=(12.5,0,62) rot=(0,0,1;0rad)
  Solid = false
  Source = -> Face146
  Symmetric = false
FEATURE [Part::Revolution] Revolve159  label="removeToCreateScrewAndThreadedInsertHole066"
  Angle = 360
  Axis = (0,1,0)
  Base = (0,0,0)
  FaceMakerClass = Part::FaceMakerBullseye
  Placement = pos=(89.5,0,68.5) rot=(0,0,1;0rad)
  Solid = false
  Source = -> Face143
  Symmetric = false
FEATURE [Part::Revolution] Revolve160  label="removeToCreateScrewAndThreadedInsertHole067"
  Angle = 360
  Axis = (0,1,0)
  Base = (0,0,0)
  FaceMakerClass = Part::FaceMakerBullseye
  Placement = pos=(89.5,0,3.5) rot=(0,0,1;0rad)
  Solid = false
  Source = -> Face142
  Symmetric = false
FEATURE [Part::Revolution] Revolve161  label="removeToCreateScrewAndThreadedInsertHole068"
  Angle = 360
  Axis = (0,1,0)
  Base = (0,0,0)
  FaceMakerClass = Part::FaceMakerBullseye
  Placement = pos=(109.5,4.7,3.5) rot=(0,0,1;0rad)
  Solid = false
  Source = -> Face145
  Symmetric = false
FEATURE [Part::Revolution] Revolve162  label="removeToCreateScrewAndThreadedInsertHole069"
  Angle = 360
  Axis = (0,1,0)
  Base = (0,0,0)
  FaceMakerClass = Part::FaceMakerBullseye
  Placement = pos=(109.5,4.7,68.5) rot=(0,0,1;0rad)
  Solid = false
  Source = -> Face144
  Symmetric = false
FEATURE [Part::MultiFuse] Fusion141  label="removeToCreateScrewAndThreadedInsertHole064"
  Shapes = -> [Revolve162,Revolve161,Revolve160,Revolve159,Revolve158,Revolve157]
FEATURE [Part::Cylinder] Cylinder062
  Angle = 360
  AttacherType = Attacher::AttachEngine3D
  Height = 20
  Placement = pos=(0,0,36.15) rot=(0,0,1;0rad)
  Radius = 14
FEATURE [Part::Cylinder] Cylinder063
  Angle = 360
  AttacherType = Attacher::AttachEngine3D
  Height = 10
  Placement = pos=(0,0,36.15) rot=(0,0,1;0rad)
  Radius = 4
FEATURE [Part::MultiFuse] Fusion139  label="removeToCreteHoleForPlugHousing052"
  Placement = pos=(70,19,36) rot=(0,1,0;1.5708rad)
  Shapes = -> [Cylinder062,Cylinder063]
FEATURE [Part::Cut] Cut060  label="bottom017"
  Base = -> Extrude064
  Tool = -> Fusion139
FEATURE [Part::Cut] Cut061  label="bottom019"
  Base = -> Cut060
  Tool = -> Fusion141
FEATURE [Part::MultiFuse] Fusion140  label="bottom018"
  Shapes = -> [Cut061,Cut058]
FEATURE [Part::Cut] Cut059  label="bottom020"
  Base = -> Fusion140
  Tool = -> Fillet056
FEATURE [Part::Box] Box036  label="Cube021"
  AttacherType = Attacher::AttachEngine3D
  Height = 80
  Length = 26
  Placement = pos=(0,-1,-5) rot=(0,0,1;0rad)
  Width = 11
FEATURE [Part::Cut] Cut062  label="removeFromBottom002"
  Base = -> Cut057
  Tool = -> Box036
FEATURE [Part::Cut] Cut063
  Base = -> Cut059
  Tool = -> Cut062
FEATURE [Part::Cut] Cut064  label="pcbStands"
  Base = -> Fusion095
  Tool = -> Fusion127
FEATURE [Sketcher::SketchObject] Sketch075  label="topSketch022"
  FullyConstrained = true
  sketch-geometry (6):
    g0: LineSegment StartX=19 StartY=38 StartZ=0 EndX=117 EndY=38 EndZ=0
    g1: ArcOfCircle CenterX=19 CenterY=19 CenterZ=0 NormalX=0 NormalY=0 NormalZ=1 AngleXU=0 Radius=19 StartAngle=1.5708 EndAngle=3.14159
    g2: LineSegment StartX=117 StartY=38 StartZ=0 EndX=117 EndY=19 EndZ=0
    g3: LineSegment StartX=98 StartY=1.0161e-12 StartZ=0 EndX=5.22862e-06 EndY=1.0161e-12 EndZ=0
    g4: LineSegment StartX=5.22862e-06 StartY=19 StartZ=0 EndX=5.22862e-06 EndY=1.0161e-12 EndZ=0
    g5: ArcOfCircle CenterX=98 CenterY=19 CenterZ=0 NormalX=0 NormalY=0 NormalZ=1 AngleXU=0 Radius=19 StartAngle=4.71239 EndAngle=6.28319
  constraints (16):
    c: Horizontal(g0)
    c: Distance(g0) = 98
    c: Coincident(g1,g0)
    c: Block(g1)
    c: Coincident(g2,g0)
    c: Vertical(g2)
    c: Distance(g2) = 19
    c: Horizontal(g3)
    c: Coincident(g4,g1)
    c: Vertical(g4)
    c: Coincident(g3,g4)
    c: Block(g3)
    c: Coincident(g5,g2)
    c: Coincident(g5,g3)
    c: Block(g0)
    c: Block(g5)
FEATURE [Part::Extrusion] Extrude067  label="sideB003"
  Base = -> Sketch075
  Dir = (0,0,1)
  DirMode = 2
  FaceMakerClass = Part::FaceMakerBullseye
  LengthFwd = 3
  LengthRev = 0
  Placement = pos=(0,0,71.7) rot=(0,0,1;0rad)
  Solid = true
  Symmetric = false
FEATURE [Sketcher::SketchObject] Sketch076  label="topSketch023"
  FullyConstrained = true
  sketch-geometry (6):
    g0: LineSegment StartX=19 StartY=38 StartZ=0 EndX=117 EndY=38 EndZ=0
    g1: ArcOfCircle CenterX=19 CenterY=19 CenterZ=0 NormalX=0 NormalY=0 NormalZ=1 AngleXU=0 Radius=19 StartAngle=1.5708 EndAngle=3.14159
    g2: LineSegment StartX=117 StartY=38 StartZ=0 EndX=117 EndY=19 EndZ=0
    g3: LineSegment StartX=98 StartY=1.0161e-12 StartZ=0 EndX=5.22862e-06 EndY=1.0161e-12 EndZ=0
    g4: LineSegment StartX=5.22862e-06 StartY=19 StartZ=0 EndX=5.22862e-06 EndY=1.0161e-12 EndZ=0
    g5: ArcOfCircle CenterX=98 CenterY=19 CenterZ=0 NormalX=0 NormalY=0 NormalZ=1 AngleXU=0 Radius=19 StartAngle=4.71239 EndAngle=6.28319
  constraints (16):
    c: Horizontal(g0)
    c: Distance(g0) = 98
    c: Coincident(g1,g0)
    c: Block(g1)
    c: Coincident(g2,g0)
    c: Vertical(g2)
    c: Distance(g2) = 19
    c: Horizontal(g3)
    c: Coincident(g4,g1)
    c: Vertical(g4)
    c: Coincident(g3,g4)
    c: Block(g3)
    c: Coincident(g5,g2)
    c: Coincident(g5,g3)
    c: Block(g0)
    c: Block(g5)
FEATURE [Part::Extrusion] Extrude066  label="sideA003"
  Base = -> Sketch076
  Dir = (0,0,1)
  DirMode = 2
  FaceMakerClass = Part::FaceMakerBullseye
  LengthFwd = 3
  LengthRev = 0
  Placement = pos=(0,0,-2.7) rot=(0,0,1;0rad)
  Solid = true
  Symmetric = false
FEATURE [Part::MultiFuse] Fusion142  label="removeFromBottom003"
  Placement = pos=(2,0,0) rot=(0,0,1;0rad)
  Shapes = -> [Extrude066,Extrude067]
FEATURE [Part::Cut] Cut065  label="screwRetainers002"
  Base = -> Fusion096
  Tool = -> Fusion142
FEATURE [Sketcher::SketchObject] Sketch077
  FullyConstrained = true
  Placement = pos=(117,19,0) rot=(0.57735,0.57735,0.57735;2.0944rad)
  sketch-geometry (8):
    g0: LineSegment StartX=-49.19 StartY=63.5 StartZ=0 EndX=-49.19 EndY=60.5 EndZ=0
    g1: LineSegment StartX=-49.19 StartY=11.5 StartZ=0 EndX=-49.19 EndY=8.5 EndZ=0
    g2: ArcOfCircle CenterX=-1.5 CenterY=62 CenterZ=0 NormalX=0 NormalY=0 NormalZ=1 AngleXU=0 Radius=1.5 StartAngle=4.71239 EndAngle=7.85398
    g3: ArcOfCircle CenterX=-1.5 CenterY=10 CenterZ=0 NormalX=0 NormalY=0 NormalZ=1 AngleXU=0 Radius=1.5 StartAngle=4.71239 EndAngle=7.85398
    g4: LineSegment StartX=-49.19 StartY=63.5 StartZ=0 EndX=-1.5 EndY=63.5 EndZ=0
    g5: LineSegment StartX=-49.19 StartY=60.5 StartZ=0 EndX=-1.5 EndY=60.5 EndZ=0
    g6: LineSegment StartX=-49.19 StartY=11.5 StartZ=0 EndX=-1.5 EndY=11.5 EndZ=0
    g7: LineSegment StartX=-49.19 StartY=8.5 StartZ=0 EndX=-1.5 EndY=8.5 EndZ=0
  constraints (19):
    c: Vertical(g0)
    c: Distance(g0) = 3
    c: Vertical(g1)
    c: Block(g1)
    c: Block(g2)
    c: Block(g3)
    c: Block(g0)
    c: Coincident(g4,g0)
    c: Coincident(g4,g2)
    c: Horizontal(g4)
    c: Coincident(g5,g0)
    c: Coincident(g5,g2)
    c: Horizontal(g5)
    c: Coincident(g6,g1)
    c: Coincident(g6,g3)
    c: Horizontal(g6)
    c: Coincident(g7,g1)
    c: Coincident(g7,g3)
    c: Horizontal(g7)
FEATURE [Part::Extrusion] Extrude068
  Base = -> Sketch077
  Dir = (1,0,0)
  DirMode = 2
  FaceMakerClass = Part::FaceMakerBullseye
  LengthFwd = 10
  LengthRev = 0
  Solid = true
  Symmetric = false
FEATURE [Part::Fillet] Fillet057  label="removeFromtMoreFrontCaseScrewRetainers002"
  Base = -> Extrude068
  Edges = 4 edges r=1.49: [Edge6,Edge11,Edge18,Edge23]
  Placement = pos=(-12,0,0) rot=(0,0,1;0rad)
FEATURE [Sketcher::SketchObject] Sketch078
  FullyConstrained = true
  Placement = pos=(117,19,0) rot=(0.57735,0.57735,0.57735;2.0944rad)
  sketch-geometry (8):
    g0: LineSegment StartX=-49.19 StartY=69.25 StartZ=0 EndX=-49.19 EndY=66.25 EndZ=0
    g1: LineSegment StartX=-49.19 StartY=5.75 StartZ=0 EndX=-49.19 EndY=2.75 EndZ=0
    g2: ArcOfCircle CenterX=-1.5 CenterY=67.75 CenterZ=0 NormalX=0 NormalY=0 NormalZ=1 AngleXU=0 Radius=1.5 StartAngle=4.71239 EndAngle=7.85398
    g3: ArcOfCircle CenterX=-1.5 CenterY=4.25 CenterZ=0 NormalX=0 NormalY=0 NormalZ=1 AngleXU=0 Radius=1.5 StartAngle=4.71239 EndAngle=7.85398
    g4: LineSegment StartX=-49.19 StartY=69.25 StartZ=0 EndX=-1.5 EndY=69.25 EndZ=0
    g5: LineSegment StartX=-49.19 StartY=66.25 StartZ=0 EndX=-1.5 EndY=66.25 EndZ=0
    g6: LineSegment StartX=-49.19 StartY=5.75 StartZ=0 EndX=-1.5 EndY=5.75 EndZ=0
    g7: LineSegment StartX=-49.19 StartY=2.75 StartZ=0 EndX=-1.5 EndY=2.75 EndZ=0
  constraints (19):
    c: Vertical(g0)
    c: Distance(g0) = 3
    c: Block(g0)
    c: Vertical(g1)
    c: Block(g2)
    c: Block(g3)
    c: Block(g1)
    c: Coincident(g4,g0)
    c: Coincident(g4,g2)
    c: Horizontal(g4)
    c: Coincident(g5,g0)
    c: Coincident(g5,g2)
    c: Horizontal(g5)
    c: Coincident(g6,g1)
    c: Coincident(g6,g3)
    c: Horizontal(g6)
    c: Coincident(g7,g1)
    c: Coincident(g7,g3)
    c: Horizontal(g7)
FEATURE [Part::Extrusion] Extrude069
  Base = -> Sketch078
  Dir = (1,0,0)
  DirMode = 2
  FaceMakerClass = Part::FaceMakerBullseye
  LengthFwd = 10
  LengthRev = 0
  Solid = true
  Symmetric = false
FEATURE [Part::Fillet] Fillet058  label="removeFromtMoreFrontCaseScrewRetainers003"
  Base = -> Extrude069
  Edges = 4 edges r=1.49: [Edge6,Edge11,Edge18,Edge23]
  Placement = pos=(-4,0,0) rot=(0,0,1;0rad)
FEATURE [Part::Cut] Cut066
  Base = -> Cut065
  Tool = -> Fillet058
FEATURE [Part::Cut] Cut067  label="screwPillars"
  Base = -> Cut066
  Tool = -> Fillet057
FEATURE [Part::MultiFuse] Fusion143  label="bottom021"
  Shapes = -> [Cut031,Cut063]
FEATURE [Part::Cylinder] Cylinder
  Angle = 360
  AttacherType = Attacher::AttachEngine3D
  Height = 10
  Placement = pos=(20.65,12,4.68) rot=(1,0,0;1.5708rad)
  Radius = 2
FEATURE [Part::Cylinder] Cylinder064
  Angle = 360
  AttacherType = Attacher::AttachEngine3D
  Height = 10
  Placement = pos=(20.65,12,67.38) rot=(1,0,0;1.5708rad)
  Radius = 2
FEATURE [Part::Cylinder] Cylinder065
  Angle = 360
  AttacherType = Attacher::AttachEngine3D
  Height = 10
  Placement = pos=(77.15,12,67.38) rot=(1,0,0;1.5708rad)
  Radius = 2
FEATURE [Part::Cylinder] Cylinder066
  Angle = 360
  AttacherType = Attacher::AttachEngine3D
  Height = 10
  Placement = pos=(77.15,12,4.68) rot=(1,0,0;1.5708rad)
  Radius = 2
FEATURE [Part::MultiFuse] Fusion144  label="removeFromThreadedInsertHousing"
  Shapes = -> [Cylinder065,Cylinder064,Cylinder,Cylinder066]
FEATURE [Part::Cut] Cut068  label="pcbStands001"
  Base = -> Cut064
  Tool = -> Fusion144
FEATURE [Part::MultiFuse] Fusion145
  Shapes = -> [Cut068,Fusion143]
FEATURE [Part::MultiFuse] Fusion146
  Shapes = -> [Fusion145]
FEATURE [Part::MultiFuse] Fusion147  label="bottom022"
  Shapes = -> [Cut067,Fusion146]
FEATURE [Part::MultiFuse] Fusion148  label="casePillars005"
  Shapes = -> [Cut047,Fusion092]
FEATURE [Part::MultiFuse] Fusion149  label="bottom023"
  Shapes = -> [Fusion124,Fusion113,Fusion147]
FEATURE [Part::MultiFuse] Fusion150  label="topBits"
  Shapes = -> [Cut025,Fusion148,Cut030,Fillet034]
FEATURE [Part::Feature] Face149 .. Face152  x4 (patterned run collapsed; names and placements below)
  shape: bbox 3.2 x 1.5 x 2e-07 mm, 1 faces, 0 solids (baked)
FEATURE [Part::Feature] Face153
  shape: bbox 3.6 x 3.2 x 2e-07 mm, 1 faces, 0 solids (baked)
FEATURE [Part::Feature] Face154
  shape: bbox 3.6 x 3.2 x 2e-07 mm, 1 faces, 0 solids (baked)
FEATURE [Sketcher::SketchObject] Sketch079  label="topSketch024"
  FullyConstrained = true
  sketch-geometry (6):
    g0: LineSegment StartX=19 StartY=38 StartZ=0 EndX=117 EndY=38 EndZ=0
    g1: ArcOfCircle CenterX=19 CenterY=19 CenterZ=0 NormalX=0 NormalY=0 NormalZ=1 AngleXU=0 Radius=19 StartAngle=1.5708 EndAngle=3.14159
    g2: LineSegment StartX=117 StartY=38 StartZ=0 EndX=117 EndY=19 EndZ=0
    g3: LineSegment StartX=98 StartY=1.0161e-12 StartZ=0 EndX=5.22862e-06 EndY=1.0161e-12 EndZ=0
    g4: LineSegment StartX=5.22862e-06 StartY=19 StartZ=0 EndX=5.22862e-06 EndY=1.0161e-12 EndZ=0
    g5: ArcOfCircle CenterX=98 CenterY=19 CenterZ=0 NormalX=0 NormalY=0 NormalZ=1 AngleXU=0 Radius=19 StartAngle=4.71239 EndAngle=6.28319
  constraints (16):
    c: Horizontal(g0)
    c: Distance(g0) = 98
    c: Coincident(g1,g0)
    c: Block(g1)
    c: Coincident(g2,g0)
    c: Vertical(g2)
    c: Distance(g2) = 19
    c: Horizontal(g3)
    c: Coincident(g4,g1)
    c: Vertical(g4)
    c: Coincident(g3,g4)
    c: Block(g3)
    c: Coincident(g5,g2)
    c: Coincident(g5,g3)
    c: Block(g0)
    c: Block(g5)
FEATURE [Sketcher::SketchObject] Sketch080  label="topSketch025"
  FullyConstrained = true
  sketch-geometry (6):
    g0: LineSegment StartX=19 StartY=38 StartZ=0 EndX=117 EndY=38 EndZ=0
    g1: ArcOfCircle CenterX=19 CenterY=19 CenterZ=0 NormalX=0 NormalY=0 NormalZ=1 AngleXU=0 Radius=19 StartAngle=1.5708 EndAngle=3.14159
    g2: LineSegment StartX=117 StartY=38 StartZ=0 EndX=117 EndY=19 EndZ=0
    g3: LineSegment StartX=98 StartY=1.0161e-12 StartZ=0 EndX=5.22862e-06 EndY=1.0161e-12 EndZ=0
    g4: LineSegment StartX=5.22862e-06 StartY=19 StartZ=0 EndX=5.22862e-06 EndY=1.0161e-12 EndZ=0
    g5: ArcOfCircle CenterX=98 CenterY=19 CenterZ=0 NormalX=0 NormalY=0 NormalZ=1 AngleXU=0 Radius=19 StartAngle=4.71239 EndAngle=6.28319
  constraints (16):
    c: Horizontal(g0)
    c: Distance(g0) = 98
    c: Coincident(g1,g0)
    c: Block(g1)
    c: Coincident(g2,g0)
    c: Vertical(g2)
    c: Distance(g2) = 19
    c: Horizontal(g3)
    c: Coincident(g4,g1)
    c: Vertical(g4)
    c: Coincident(g3,g4)
    c: Block(g3)
    c: Coincident(g5,g2)
    c: Coincident(g5,g3)
    c: Block(g0)
    c: Block(g5)
FEATURE [Part::Extrusion] Extrude070  label="sideA004"
  Base = -> Sketch080
  Dir = (0,0,1)
  DirMode = 2
  FaceMakerClass = Part::FaceMakerBullseye
  LengthFwd = 3
  LengthRev = 0
  Placement = pos=(0,0,-2.7) rot=(0,0,1;0rad)
  Solid = true
  Symmetric = false
FEATURE [Sketcher::SketchObject] Sketch081
  FullyConstrained = true
  Placement = pos=(117,19,0) rot=(0.57735,0.57735,0.57735;2.0944rad)
  sketch-geometry (8):
    g0: LineSegment StartX=-49.19 StartY=63.5 StartZ=0 EndX=-49.19 EndY=60.5 EndZ=0
    g1: LineSegment StartX=-49.19 StartY=11.5 StartZ=0 EndX=-49.19 EndY=8.5 EndZ=0
    g2: ArcOfCircle CenterX=-1.5 CenterY=62 CenterZ=0 NormalX=0 NormalY=0 NormalZ=1 AngleXU=0 Radius=1.5 StartAngle=4.71239 EndAngle=7.85398
    g3: ArcOfCircle CenterX=-1.5 CenterY=10 CenterZ=0 NormalX=0 NormalY=0 NormalZ=1 AngleXU=0 Radius=1.5 StartAngle=4.71239 EndAngle=7.85398
    g4: LineSegment StartX=-49.19 StartY=63.5 StartZ=0 EndX=-1.5 EndY=63.5 EndZ=0
    g5: LineSegment StartX=-49.19 StartY=60.5 StartZ=0 EndX=-1.5 EndY=60.5 EndZ=0
    g6: LineSegment StartX=-49.19 StartY=11.5 StartZ=0 EndX=-1.5 EndY=11.5 EndZ=0
    g7: LineSegment StartX=-49.19 StartY=8.5 StartZ=0 EndX=-1.5 EndY=8.5 EndZ=0
  constraints (19):
    c: Vertical(g0)
    c: Distance(g0) = 3
    c: Vertical(g1)
    c: Block(g1)
    c: Block(g2)
    c: Block(g3)
    c: Block(g0)
    c: Coincident(g4,g0)
    c: Coincident(g4,g2)
    c: Horizontal(g4)
    c: Coincident(g5,g0)
    c: Coincident(g5,g2)
    c: Horizontal(g5)
    c: Coincident(g6,g1)
    c: Coincident(g6,g3)
    c: Horizontal(g6)
    c: Coincident(g7,g1)
    c: Coincident(g7,g3)
    c: Horizontal(g7)
FEATURE [Part::Extrusion] Extrude071  label="sideB004"
  Base = -> Sketch079
  Dir = (0,0,1)
  DirMode = 2
  FaceMakerClass = Part::FaceMakerBullseye
  LengthFwd = 3
  LengthRev = 0
  Placement = pos=(0,0,71.7) rot=(0,0,1;0rad)
  Solid = true
  Symmetric = false
FEATURE [Part::MultiFuse] Fusion152  label="removeFromBottom004"
  Placement = pos=(2,0,0) rot=(0,0,1;0rad)
  Shapes = -> [Extrude070,Extrude071]
FEATURE [Part::Extrusion] Extrude072
  Base = -> Sketch081
  Dir = (1,0,0)
  DirMode = 2
  FaceMakerClass = Part::FaceMakerBullseye
  LengthFwd = 10
  LengthRev = 0
  Solid = true
  Symmetric = false
FEATURE [Part::Fillet] Fillet059  label="removeFromtMoreFrontCaseScrewRetainers004"
  Base = -> Extrude072
  Edges = 4 edges r=1.49: [Edge6,Edge11,Edge18,Edge23]
  Placement = pos=(-12,0,0) rot=(0,0,1;0rad)
FEATURE [Sketcher::SketchObject] Sketch082
  FullyConstrained = true
  Placement = pos=(117,19,0) rot=(0.57735,0.57735,0.57735;2.0944rad)
  sketch-geometry (8):
    g0: LineSegment StartX=-49.19 StartY=69.25 StartZ=0 EndX=-49.19 EndY=66.25 EndZ=0
    g1: LineSegment StartX=-49.19 StartY=5.75 StartZ=0 EndX=-49.19 EndY=2.75 EndZ=0
    g2: ArcOfCircle CenterX=-1.5 CenterY=67.75 CenterZ=0 NormalX=0 NormalY=0 NormalZ=1 AngleXU=0 Radius=1.5 StartAngle=4.71239 EndAngle=7.85398
    g3: ArcOfCircle CenterX=-1.5 CenterY=4.25 CenterZ=0 NormalX=0 NormalY=0 NormalZ=1 AngleXU=0 Radius=1.5 StartAngle=4.71239 EndAngle=7.85398
    g4: LineSegment StartX=-49.19 StartY=69.25 StartZ=0 EndX=-1.5 EndY=69.25 EndZ=0
    g5: LineSegment StartX=-49.19 StartY=66.25 StartZ=0 EndX=-1.5 EndY=66.25 EndZ=0
    g6: LineSegment StartX=-49.19 StartY=5.75 StartZ=0 EndX=-1.5 EndY=5.75 EndZ=0
    g7: LineSegment StartX=-49.19 StartY=2.75 StartZ=0 EndX=-1.5 EndY=2.75 EndZ=0
  constraints (19):
    c: Vertical(g0)
    c: Distance(g0) = 3
    c: Block(g0)
    c: Vertical(g1)
    c: Block(g2)
    c: Block(g3)
    c: Block(g1)
    c: Coincident(g4,g0)
    c: Coincident(g4,g2)
    c: Horizontal(g4)
    c: Coincident(g5,g0)
    c: Coincident(g5,g2)
    c: Horizontal(g5)
    c: Coincident(g6,g1)
    c: Coincident(g6,g3)
    c: Horizontal(g6)
    c: Coincident(g7,g1)
    c: Coincident(g7,g3)
    c: Horizontal(g7)
FEATURE [Part::Extrusion] Extrude073
  Base = -> Sketch082
  Dir = (1,0,0)
  DirMode = 2
  FaceMakerClass = Part::FaceMakerBullseye
  LengthFwd = 10
  LengthRev = 0
  Solid = true
  Symmetric = false
FEATURE [Part::Fillet] Fillet060  label="removeFromtMoreFrontCaseScrewRetainers005"
  Base = -> Extrude073
  Edges = 4 edges r=1.49: [Edge6,Edge11,Edge18,Edge23]
  Placement = pos=(-4,0,0) rot=(0,0,1;0rad)
FEATURE [Part::Revolution] Revolve163  label="backCaseScrewRetainer004"
  Angle = 360
  Axis = (0,1,0)
  Base = (0,0,0)
  FaceMakerClass = Part::FaceMakerBullseye
  Placement = pos=(12.5,3,62) rot=(0,0,1;0rad)
  Solid = false
  Source = -> Face149
  Symmetric = false
FEATURE [Part::Revolution] Revolve164  label="frontCaseScrewRetainer006"
  Angle = 360
  Axis = (0,1,0)
  Base = (0,0,0)
  FaceMakerClass = Part::FaceMakerBullseye
  Placement = pos=(89.5,3,68.5) rot=(0,0,1;0rad)
  Solid = false
  Source = -> Face151
  Symmetric = false
FEATURE [Part::Revolution] Revolve165  label="frontCaseScrewRetainer007"
  Angle = 360
  Axis = (0,1,0)
  Base = (0,0,0)
  FaceMakerClass = Part::FaceMakerBullseye
  Placement = pos=(89.5,3,3.5) rot=(0,0,1;0rad)
  Solid = false
  Source = -> Face152
  Symmetric = false
FEATURE [Part::Revolution] Revolve166  label="backCaseScrewRetainer005"
  Angle = 360
  Axis = (0,1,0)
  Base = (0,0,0)
  FaceMakerClass = Part::FaceMakerBullseye
  Placement = pos=(12.5,3,10) rot=(0,0,1;0rad)
  Solid = false
  Source = -> Face150
  Symmetric = false
FEATURE [Part::Revolution] Revolve167  label="moreFrontCaseScrewRetainer006"
  Angle = 360
  Axis = (0,1,0)
  Base = (0,0,0)
  FaceMakerClass = Part::FaceMakerBullseye
  Placement = pos=(109.5,4.5,68.5) rot=(0,0,1;0rad)
  Solid = false
  Source = -> Face153
  Symmetric = false
FEATURE [Part::Revolution] Revolve168  label="moreFrontCaseScrewRetainer007"
  Angle = 360
  Axis = (0,1,0)
  Base = (0,0,0)
  FaceMakerClass = Part::FaceMakerBullseye
  Placement = pos=(109.5,4.5,3.5) rot=(0,0,1;0rad)
  Solid = false
  Source = -> Face154
  Symmetric = false
FEATURE [Part::MultiFuse] Fusion151  label="screwRetainers003"
  Shapes = -> [Revolve168,Revolve167,Revolve166,Revolve165,Revolve164,Revolve163]
FEATURE [Part::Cut] Cut069  label="screwRetainers004"
  Base = -> Fusion151
  Tool = -> Fusion152
FEATURE [Part::Cut] Cut070
  Base = -> Cut069
  Tool = -> Fillet060
FEATURE [Part::Cut] Cut071  label="screwPillars001"
  Base = -> Cut070
  Tool = -> Fillet059
FEATURE [Part::MultiFuse] Fusion153  label="bottom024"
  Shapes = -> [Fusion149,Cut071]
FEATURE [Part::Cylinder] Cylinder067
  Angle = 360
  AttacherType = Attacher::AttachEngine3D
  Height = 10
  Placement = pos=(20.65,12,4.68) rot=(1,0,0;1.5708rad)
  Radius = 2
FEATURE [Part::Cylinder] Cylinder068
  Angle = 360
  AttacherType = Attacher::AttachEngine3D
  Height = 10
  Placement = pos=(20.65,12,67.38) rot=(1,0,0;1.5708rad)
  Radius = 2
FEATURE [Part::Cylinder] Cylinder069
  Angle = 360
  AttacherType = Attacher::AttachEngine3D
  Height = 10
  Placement = pos=(77.15,12,67.38) rot=(1,0,0;1.5708rad)
  Radius = 2
FEATURE [Part::Cylinder] Cylinder070
  Angle = 360
  AttacherType = Attacher::AttachEngine3D
  Height = 10
  Placement = pos=(77.15,12,4.68) rot=(1,0,0;1.5708rad)
  Radius = 2
FEATURE [Part::MultiFuse] Fusion154  label="removeFromThreadedInsertHousing001"
  Shapes = -> [Cylinder069,Cylinder068,Cylinder067,Cylinder070]
FEATURE [Part::Cut] Cut072  label="bottom025"
  Base = -> Fusion153
  Tool = -> Fusion154
FEATURE [Image::ImagePlane] ImagePlane
  XSize = 339
  YSize = 72
FEATURE [Sketcher::SketchObject] Sketch083
  FullyConstrained = false
  MapMode = 5
  Support = -> [XY_Plane]
  sketch-geometry (69):
    g0: LineSegment StartX=-151.619 StartY=28.8932 StartZ=0 EndX=-140.819 EndY=28.8932 EndZ=0
    g1: LineSegment StartX=-151.619 StartY=24.0313 StartZ=0 EndX=-151.619 EndY=28.8932 EndZ=0
    g2: LineSegment StartX=-140.819 StartY=17.7713 StartZ=0 EndX=-151.619 EndY=17.7713 EndZ=0
    g3: LineSegment StartX=-151.619 StartY=17.7713 StartZ=0 EndX=-151.619 EndY=22.6313 EndZ=0
    g4: LineSegment StartX=-151.619 StartY=22.6313 StartZ=0 EndX=-145.128 EndY=22.6313 EndZ=0
    g5: LineSegment StartX=-145.128 StartY=24.0313 StartZ=0 EndX=-140.819 EndY=28.8932 EndZ=0
    g6: LineSegment StartX=-145.128 StartY=22.6313 StartZ=0 EndX=-140.819 EndY=17.7713 EndZ=0
    g7: ArcOfCircle CenterX=-155.157 CenterY=23.3323 CenterZ=0 NormalX=0 NormalY=0 NormalZ=1 AngleXU=0 Radius=6.92354 StartAngle=1.03434 EndAngle=5.24885
    g8: ArcOfCircle CenterX=-155.157 CenterY=23.3323 CenterZ=0 NormalX=0 NormalY=0 NormalZ=1 AngleXU=0 Radius=12.6269 StartAngle=1.28675 EndAngle=4.99643
    g9: LineSegment StartX=-151.619 StartY=35.4532 StartZ=0 EndX=-151.619 EndY=29.2832 EndZ=0
    g10: LineSegment StartX=-151.619 StartY=17.3813 StartZ=0 EndX=-151.619 EndY=11.2113 EndZ=0
    g11-g21: Circle x11 (B-spline internal-alignment scaffolding for g22; pole/knot coordinates omitted)
    g22: BSplineCurve PolesCount=11 KnotsCount=9 Degree=3 IsPeriodic=0
    g23-g31: GeomPoint x9 (B-spline internal-alignment scaffolding for g22; pole/knot coordinates omitted)
    g32-g49: Circle x18 (B-spline internal-alignment scaffolding for g50; pole/knot coordinates omitted)
    g50: BSplineCurve PolesCount=18 KnotsCount=16 Degree=3 IsPeriodic=0
    g51-g66: GeomPoint x16 (B-spline internal-alignment scaffolding for g50; pole/knot coordinates omitted)
    g67: LineSegment StartX=-117.124 StartY=30.093 StartZ=0 EndX=-117.603 EndY=26.5272 EndZ=0
    g68: LineSegment StartX=-117.603 StartY=17.8472 StartZ=0 EndX=-117.124 EndY=14.2659 EndZ=0
  constraints (38):
    c: Coincident(g1,g0)
    c: Horizontal(g0)
    c: Vertical(g1)
    c: Coincident(g2,g3)
    c: Coincident(g3,g4)
    c: Horizontal(g4)
    c: Horizontal(g2)
    c: Vertical(g3)
    c: Block(g1)
    c: Distance(g3) = 4.86
    c: Block(g4)
    c: Distance(g0) = 10.8
    c: Distance(g2) = 10.8
    c: Coincident(g5,g0)
    c: Coincident(g6,g4)
    c: Coincident(g6,g2)
    c: Block(g8)
    c: Block(g7)
    c: Coincident(g9,g8)
    c: Coincident(g9,g7)
    c: Vertical(g9)
    c: Coincident(g10,g7)
    c: Coincident(g10,g8)
    c: Vertical(g10)
    c: Weight(g11) = 1
    c: Equal(g11, g12-g21) x10
    c: InternalAlignment(g11-g21 -> g22) x11
    c: InternalAlignment(g23-g31 -> g22) x9
    c: Block(g22)
    c: Weight(g32) = 1
    c: Equal(g32, g33-g49) x17
    c: InternalAlignment(g32-g49 -> g50) x18
    c: InternalAlignment(g51-g66 -> g50) x16
    c: Block(g50)
    c: Coincident(g67,g50)
    c: Coincident(g67,g22)
    c: Coincident(g68,g22)
    c: Coincident(g68,g50)
FEATURE [PartDesign::Body] Body
  Group = -> [Sketch083]
  Origin = -> Origin
FEATURE [Sketcher::SketchObject] Sketch084
  FullyConstrained = true
  MapMode = 5
  Support = -> [XY_Plane001]
FEATURE [PartDesign::Body] Body001
  Group = -> [Sketch084]
  Origin = -> Origin001
